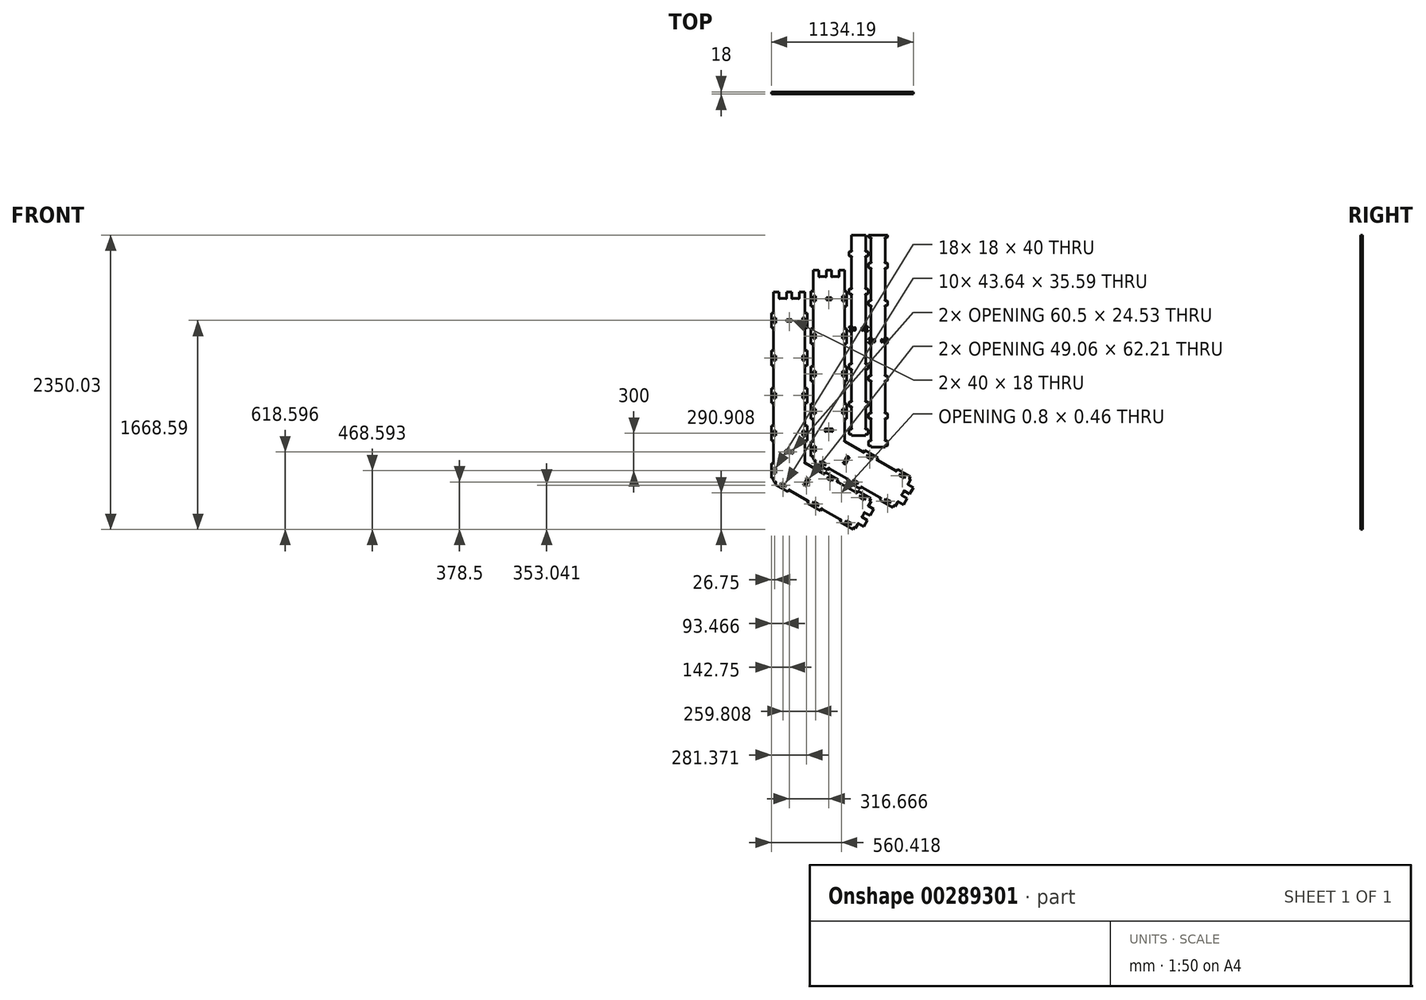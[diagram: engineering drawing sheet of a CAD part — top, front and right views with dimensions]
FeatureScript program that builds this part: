
annotation { "Feature Type Name" : "Feature", "Feature Type Description" : "" }
export const myFeature = defineFeature(function(context is Context, id is Id, definition is map)
    precondition{}
    {
        {
            var Q0;
            Q0=qCreatedBy(makeId("Front.planeOp"),FACE);
            var sketch = newSketch(context, id + "F0", { "sketchPlane" : qUnion([Q0])});
            skLineSegment(sketch, "E0", {"start": v(-135.58, 658.39) * mm, "end": v(-95.58, 658.39) * mm});
            skLineSegment(sketch, "E1", {"start": v(-95.58, 658.39) * mm, "end": v(-95.58, 676.39) * mm});
            skLineSegment(sketch, "E2", {"start": v(-95.58, 676.39) * mm, "end": v(-135.58, 676.39) * mm});
            skLineSegment(sketch, "E3", {"start": v(-135.58, 676.39) * mm, "end": v(-135.58, 658.39) * mm});
            skLineSegment(sketch, "E4", {"start": v(-600, -1200) * mm, "end": v(600, -1200) * mm});
            skLineSegment(sketch, "E5", {"start": v(600, -1200) * mm, "end": v(600, 1200) * mm});
            skLineSegment(sketch, "E6", {"start": v(600, 1200) * mm, "end": v(-600, 1200) * mm});
            skLineSegment(sketch, "E7", {"start": v(-600, 1200) * mm, "end": v(-600, -1200) * mm});
            skLineSegment(sketch, "E8", {"start": v(-480, 825) * mm, "end": v(-480, 1075) * mm});
            skLineSegment(sketch, "E9", {"start": v(-480, 1075) * mm, "end": v(-433.22, 1075) * mm});
            skLineSegment(sketch, "E10", {"start": v(-433.22, 1075) * mm, "end": v(-425, 1083.22) * mm});
            skLineSegment(sketch, "E11", {"start": v(-425, 1083.22) * mm, "end": v(-425, 1166.78) * mm});
            skLineSegment(sketch, "E12", {"start": v(-425, 1166.78) * mm, "end": v(-433.22, 1175) * mm});
            skLineSegment(sketch, "E13", {"start": v(-433.22, 1175) * mm, "end": v(-566.78, 1175) * mm});
            skLineSegment(sketch, "E14", {"start": v(-566.78, 1175) * mm, "end": v(-575, 1166.78) * mm});
            skLineSegment(sketch, "E15", {"start": v(-575, 1166.78) * mm, "end": v(-575, 1083.22) * mm});
            skLineSegment(sketch, "E16", {"start": v(-575, 1083.22) * mm, "end": v(-566.78, 1075) * mm});
            skLineSegment(sketch, "E17", {"start": v(-566.78, 1075) * mm, "end": v(-520, 1075) * mm});
            skLineSegment(sketch, "E18", {"start": v(-520, 1075) * mm, "end": v(-520, 825) * mm});
            skLineSegment(sketch, "E19", {"start": v(-520, 825) * mm, "end": v(-480, 825) * mm});
            skLineSegment(sketch, "E20", {"start": v(-405, 1175) * mm, "end": v(-405, 925) * mm});
            skLineSegment(sketch, "E21", {"start": v(-405, 925) * mm, "end": v(-451.78, 925) * mm});
            skLineSegment(sketch, "E22", {"start": v(-451.78, 925) * mm, "end": v(-460, 916.78) * mm});
            skLineSegment(sketch, "E23", {"start": v(-460, 916.78) * mm, "end": v(-460, 833.22) * mm});
            skLineSegment(sketch, "E24", {"start": v(-460, 833.22) * mm, "end": v(-451.78, 825) * mm});
            skLineSegment(sketch, "E25", {"start": v(-451.78, 825) * mm, "end": v(-318.22, 825) * mm});
            skLineSegment(sketch, "E26", {"start": v(-318.22, 825) * mm, "end": v(-310, 833.22) * mm});
            skLineSegment(sketch, "E27", {"start": v(-310, 833.22) * mm, "end": v(-310, 916.78) * mm});
            skLineSegment(sketch, "E28", {"start": v(-310, 916.78) * mm, "end": v(-318.22, 925) * mm});
            skLineSegment(sketch, "E29", {"start": v(-318.22, 925) * mm, "end": v(-365, 925) * mm});
            skLineSegment(sketch, "E30", {"start": v(-365, 925) * mm, "end": v(-365, 1175) * mm});
            skLineSegment(sketch, "E31", {"start": v(-365, 1175) * mm, "end": v(-405, 1175) * mm});
            skLineSegment(sketch, "E32", {"start": v(575, -1175) * mm, "end": v(575, -953) * mm});
            skLineSegment(sketch, "E33", {"start": v(575, -953) * mm, "end": v(540, -953) * mm});
            skLineSegment(sketch, "E34", {"start": v(540, -953) * mm, "end": v(540, -1008) * mm});
            skLineSegment(sketch, "E35", {"start": v(540, -1008) * mm, "end": v(446, -1008) * mm});
            skLineSegment(sketch, "E36", {"start": v(446, -1008) * mm, "end": v(446, -1033.28) * mm});
            skLineSegment(sketch, "E37", {"start": v(446, -1033.28) * mm, "end": v(527, -1040.95) * mm});
            skLineSegment(sketch, "E38", {"start": v(527, -1040.95) * mm, "end": v(527, -1088.05) * mm});
            skLineSegment(sketch, "E39", {"start": v(527, -1088.05) * mm, "end": v(446, -1095.72) * mm});
            skLineSegment(sketch, "E40", {"start": v(446, -1095.72) * mm, "end": v(446, -1121) * mm});
            skLineSegment(sketch, "E41", {"start": v(446, -1121) * mm, "end": v(540, -1121) * mm});
            skLineSegment(sketch, "E42", {"start": v(540, -1121) * mm, "end": v(540, -1175) * mm});
            skLineSegment(sketch, "E43", {"start": v(540, -1175) * mm, "end": v(575, -1175) * mm});
            skLineSegment(sketch, "E44", {"start": v(199, -1174.72) * mm, "end": v(421, -1174.72) * mm});
            skLineSegment(sketch, "E45", {"start": v(421, -1174.72) * mm, "end": v(421, -1139.72) * mm});
            skLineSegment(sketch, "E46", {"start": v(421, -1139.72) * mm, "end": v(366, -1139.72) * mm});
            skLineSegment(sketch, "E47", {"start": v(366, -1139.72) * mm, "end": v(366, -1045.72) * mm});
            skLineSegment(sketch, "E48", {"start": v(366, -1045.72) * mm, "end": v(340.72, -1045.72) * mm});
            skLineSegment(sketch, "E49", {"start": v(340.72, -1045.72) * mm, "end": v(333.05, -1126.72) * mm});
            skLineSegment(sketch, "E50", {"start": v(333.05, -1126.72) * mm, "end": v(285.95, -1126.72) * mm});
            skLineSegment(sketch, "E51", {"start": v(285.95, -1126.72) * mm, "end": v(278.28, -1045.72) * mm});
            skLineSegment(sketch, "E52", {"start": v(278.28, -1045.72) * mm, "end": v(253, -1045.72) * mm});
            skLineSegment(sketch, "E53", {"start": v(253, -1045.72) * mm, "end": v(253, -1139.72) * mm});
            skLineSegment(sketch, "E54", {"start": v(253, -1139.72) * mm, "end": v(199, -1139.72) * mm});
            skLineSegment(sketch, "E55", {"start": v(199, -1139.72) * mm, "end": v(199, -1174.72) * mm});
            skLineSegment(sketch, "E56", {"start": v(576.88, -543.09) * mm, "end": v(354.87, -543.09) * mm});
            skLineSegment(sketch, "E57", {"start": v(354.87, -543.09) * mm, "end": v(354.87, -578.09) * mm});
            skLineSegment(sketch, "E58", {"start": v(354.87, -578.09) * mm, "end": v(409.87, -578.09) * mm});
            skLineSegment(sketch, "E59", {"start": v(409.87, -578.09) * mm, "end": v(409.87, -672.09) * mm});
            skLineSegment(sketch, "E60", {"start": v(409.87, -672.09) * mm, "end": v(435.16, -672.09) * mm});
            skLineSegment(sketch, "E61", {"start": v(435.16, -672.09) * mm, "end": v(442.82, -591.09) * mm});
            skLineSegment(sketch, "E62", {"start": v(442.82, -591.09) * mm, "end": v(489.93, -591.09) * mm});
            skLineSegment(sketch, "E63", {"start": v(489.93, -591.09) * mm, "end": v(497.6, -672.09) * mm});
            skLineSegment(sketch, "E64", {"start": v(497.6, -672.09) * mm, "end": v(522.88, -672.09) * mm});
            skLineSegment(sketch, "E65", {"start": v(522.88, -672.09) * mm, "end": v(522.88, -578.09) * mm});
            skLineSegment(sketch, "E66", {"start": v(522.88, -578.09) * mm, "end": v(576.88, -578.09) * mm});
            skLineSegment(sketch, "E67", {"start": v(576.88, -578.09) * mm, "end": v(576.88, -543.09) * mm});
            skLineSegment(sketch, "E68", {"start": v(-289.5, -46.66) * mm, "end": v(-307.25, -46.66) * mm});
            skArc(sketch, "E69", {"start": v(-307.25, -46.66) * mm, "mid": v(-310.5, -43.52) * mm, "end": v(-307.5, -40.14) * mm});
            skLineSegment(sketch, "E70", {"start": v(-307.5, -40.14) * mm, "end": v(-307.5, 127.32) * mm});
            skArc(sketch, "E71", {"start": v(-307.5, 127.32) * mm, "mid": v(-310.52, 130.7) * mm, "end": v(-307.25, 133.84) * mm});
            skLineSegment(sketch, "E72", {"start": v(-307.25, 133.84) * mm, "end": v(-289.5, 133.84) * mm});
            skLineSegment(sketch, "E73", {"start": v(-289.5, 133.84) * mm, "end": v(-289.5, 253.34) * mm});
            skLineSegment(sketch, "E74", {"start": v(-289.5, 253.34) * mm, "end": v(-307.25, 253.34) * mm});
            skArc(sketch, "E75", {"start": v(-307.25, 253.34) * mm, "mid": v(-310.5, 256.48) * mm, "end": v(-307.5, 259.86) * mm});
            skLineSegment(sketch, "E76", {"start": v(-307.5, 259.86) * mm, "end": v(-307.5, 427.32) * mm});
            skArc(sketch, "E77", {"start": v(-307.5, 427.32) * mm, "mid": v(-310.52, 430.7) * mm, "end": v(-307.25, 433.84) * mm});
            skLineSegment(sketch, "E78", {"start": v(-307.25, 433.84) * mm, "end": v(-289.5, 433.84) * mm});
            skLineSegment(sketch, "E79", {"start": v(-289.5, 433.84) * mm, "end": v(-289.5, 553.34) * mm});
            skLineSegment(sketch, "E80", {"start": v(-289.5, 553.34) * mm, "end": v(-307.25, 553.34) * mm});
            skArc(sketch, "E81", {"start": v(-307.25, 553.34) * mm, "mid": v(-310.5, 556.48) * mm, "end": v(-307.5, 559.86) * mm});
            skLineSegment(sketch, "E82", {"start": v(-307.5, 559.86) * mm, "end": v(-307.5, 720.04) * mm});
            skLineSegment(sketch, "E83", {"start": v(-307.5, 720.04) * mm, "end": v(-352, 720.04) * mm});
            skLineSegment(sketch, "E84", {"start": v(-352, 720.04) * mm, "end": v(-352, 670.3) * mm});
            skArc(sketch, "E85", {"start": v(-352, 670.3) * mm, "mid": v(-355.14, 667.03) * mm, "end": v(-358.52, 670.04) * mm});
            skLineSegment(sketch, "E86", {"start": v(-358.52, 670.04) * mm, "end": v(-405.98, 670.04) * mm});
            skArc(sketch, "E87", {"start": v(-405.98, 670.04) * mm, "mid": v(-409.36, 667.02) * mm, "end": v(-412.5, 670.3) * mm});
            skLineSegment(sketch, "E88", {"start": v(-412.5, 670.3) * mm, "end": v(-412.5, 720.04) * mm});
            skLineSegment(sketch, "E89", {"start": v(-412.5, 720.04) * mm, "end": v(-452, 720.04) * mm});
            skLineSegment(sketch, "E90", {"start": v(-452, 720.04) * mm, "end": v(-452, 670.3) * mm});
            skArc(sketch, "E91", {"start": v(-452, 670.3) * mm, "mid": v(-455.14, 667.03) * mm, "end": v(-458.52, 670.04) * mm});
            skLineSegment(sketch, "E92", {"start": v(-458.52, 670.04) * mm, "end": v(-505.98, 670.04) * mm});
            skArc(sketch, "E93", {"start": v(-505.98, 670.04) * mm, "mid": v(-509.36, 667.02) * mm, "end": v(-512.5, 670.3) * mm});
            skLineSegment(sketch, "E94", {"start": v(-512.5, 670.3) * mm, "end": v(-512.5, 720.04) * mm});
            skLineSegment(sketch, "E95", {"start": v(-512.5, 720.04) * mm, "end": v(-557, 720.04) * mm});
            skLineSegment(sketch, "E96", {"start": v(-557, 720.04) * mm, "end": v(-557, 559.86) * mm});
            skArc(sketch, "E97", {"start": v(-557, 559.86) * mm, "mid": v(-553.98, 556.48) * mm, "end": v(-557.25, 553.34) * mm});
            skLineSegment(sketch, "E98", {"start": v(-557.25, 553.34) * mm, "end": v(-575, 553.34) * mm});
            skLineSegment(sketch, "E99", {"start": v(-575, 553.34) * mm, "end": v(-575, 433.84) * mm});
            skLineSegment(sketch, "E100", {"start": v(-575, 433.84) * mm, "end": v(-557.25, 433.84) * mm});
            skArc(sketch, "E101", {"start": v(-557.25, 433.84) * mm, "mid": v(-554, 430.7) * mm, "end": v(-557, 427.32) * mm});
            skLineSegment(sketch, "E102", {"start": v(-557, 427.32) * mm, "end": v(-557, 259.86) * mm});
            skArc(sketch, "E103", {"start": v(-557, 259.86) * mm, "mid": v(-553.98, 256.48) * mm, "end": v(-557.25, 253.34) * mm});
            skLineSegment(sketch, "E104", {"start": v(-557.25, 253.34) * mm, "end": v(-575, 253.34) * mm});
            skLineSegment(sketch, "E105", {"start": v(-575, 253.34) * mm, "end": v(-575, 133.84) * mm});
            skLineSegment(sketch, "E106", {"start": v(-575, 133.84) * mm, "end": v(-557.25, 133.84) * mm});
            skArc(sketch, "E107", {"start": v(-557.25, 133.84) * mm, "mid": v(-554, 130.7) * mm, "end": v(-557, 127.32) * mm});
            skLineSegment(sketch, "E108", {"start": v(-557, 127.32) * mm, "end": v(-557, -40.14) * mm});
            skArc(sketch, "E109", {"start": v(-557, -40.14) * mm, "mid": v(-553.98, -43.52) * mm, "end": v(-557.25, -46.66) * mm});
            skLineSegment(sketch, "E110", {"start": v(-557.25, -46.66) * mm, "end": v(-575, -46.66) * mm});
            skLineSegment(sketch, "E111", {"start": v(-575, -46.66) * mm, "end": v(-575, -166.16) * mm});
            skLineSegment(sketch, "E112", {"start": v(-575, -166.16) * mm, "end": v(-557.25, -166.16) * mm});
            skArc(sketch, "E113", {"start": v(-557.25, -166.16) * mm, "mid": v(-554, -169.3) * mm, "end": v(-557, -172.68) * mm});
            skLineSegment(sketch, "E114", {"start": v(-557, -172.68) * mm, "end": v(-557, -340.14) * mm});
            skArc(sketch, "E115", {"start": v(-557, -340.14) * mm, "mid": v(-553.98, -343.52) * mm, "end": v(-557.25, -346.66) * mm});
            skLineSegment(sketch, "E116", {"start": v(-557.25, -346.66) * mm, "end": v(-575, -346.66) * mm});
            skLineSegment(sketch, "E117", {"start": v(-575, -346.66) * mm, "end": v(-575, -466.16) * mm});
            skLineSegment(sketch, "E118", {"start": v(-575, -466.16) * mm, "end": v(-557.25, -466.16) * mm});
            skArc(sketch, "E119", {"start": v(-557.25, -466.16) * mm, "mid": v(-554, -469.3) * mm, "end": v(-557, -472.68) * mm});
            skLineSegment(sketch, "E120", {"start": v(-557, -472.68) * mm, "end": v(-557, -640.14) * mm});
            skArc(sketch, "E121", {"start": v(-557, -640.14) * mm, "mid": v(-553.98, -643.52) * mm, "end": v(-557.25, -646.66) * mm});
            skLineSegment(sketch, "E122", {"start": v(-557.25, -646.66) * mm, "end": v(-575, -646.66) * mm});
            skLineSegment(sketch, "E123", {"start": v(-575, -646.66) * mm, "end": v(-575, -766.16) * mm});
            skLineSegment(sketch, "E124", {"start": v(-575, -766.16) * mm, "end": v(-557.25, -766.16) * mm});
            skArc(sketch, "E125", {"start": v(-557.25, -766.16) * mm, "mid": v(-554, -769.3) * mm, "end": v(-557, -772.68) * mm});
            skLineSegment(sketch, "E126", {"start": v(-557, -772.68) * mm, "end": v(-557, -788.5) * mm});
            skLineSegment(sketch, "E127", {"start": v(-557, -788.5) * mm, "end": v(-543.3, -796.4) * mm});
            skArc(sketch, "E128", {"start": v(-543.3, -796.4) * mm, "mid": v(-538.86, -795.48) * mm, "end": v(-537.78, -799.88) * mm});
            skLineSegment(sketch, "E129", {"start": v(-537.78, -799.88) * mm, "end": v(-546.65, -815.25) * mm});
            skLineSegment(sketch, "E130", {"start": v(-546.65, -815.25) * mm, "end": v(-443.16, -875) * mm});
            skLineSegment(sketch, "E131", {"start": v(-443.16, -875) * mm, "end": v(-434.29, -859.63) * mm});
            skArc(sketch, "E132", {"start": v(-434.29, -859.63) * mm, "mid": v(-429.94, -858.38) * mm, "end": v(-428.52, -862.67) * mm});
            skLineSegment(sketch, "E133", {"start": v(-428.52, -862.67) * mm, "end": v(-283.5, -946.4) * mm});
            skArc(sketch, "E134", {"start": v(-283.5, -946.4) * mm, "mid": v(-279.06, -945.48) * mm, "end": v(-277.97, -949.88) * mm});
            skLineSegment(sketch, "E135", {"start": v(-277.97, -949.88) * mm, "end": v(-286.85, -965.25) * mm});
            skLineSegment(sketch, "E136", {"start": v(-286.85, -965.25) * mm, "end": v(-183.36, -1025) * mm});
            skLineSegment(sketch, "E137", {"start": v(-183.36, -1025) * mm, "end": v(-174.48, -1009.63) * mm});
            skArc(sketch, "E138", {"start": v(-174.48, -1009.63) * mm, "mid": v(-170.13, -1008.38) * mm, "end": v(-168.7, -1012.67) * mm});
            skLineSegment(sketch, "E139", {"start": v(-168.7, -1012.67) * mm, "end": v(-23.69, -1096.4) * mm});
            skArc(sketch, "E140", {"start": v(-23.69, -1096.4) * mm, "mid": v(-19.25, -1095.48) * mm, "end": v(-18.16, -1099.88) * mm});
            skLineSegment(sketch, "E141", {"start": v(-18.16, -1099.88) * mm, "end": v(-27.04, -1115.25) * mm});
            skLineSegment(sketch, "E142", {"start": v(-27.04, -1115.25) * mm, "end": v(76.45, -1175) * mm});
            skLineSegment(sketch, "E143", {"start": v(76.45, -1175) * mm, "end": v(85.33, -1159.63) * mm});
            skArc(sketch, "E144", {"start": v(85.33, -1159.63) * mm, "mid": v(89.67, -1158.38) * mm, "end": v(91.1, -1162.67) * mm});
            skLineSegment(sketch, "E145", {"start": v(91.1, -1162.67) * mm, "end": v(96.97, -1166.06) * mm});
            skLineSegment(sketch, "E146", {"start": v(96.97, -1166.06) * mm, "end": v(116.21, -1132.74) * mm});
            skArc(sketch, "E147", {"start": v(116.21, -1132.74) * mm, "mid": v(115.3, -1128.3) * mm, "end": v(119.7, -1127.22) * mm});
            skLineSegment(sketch, "E148", {"start": v(119.7, -1127.22) * mm, "end": v(162.78, -1152.1) * mm});
            skLineSegment(sketch, "E149", {"start": v(162.78, -1152.1) * mm, "end": v(192.53, -1100.56) * mm});
            skLineSegment(sketch, "E150", {"start": v(192.53, -1100.56) * mm, "end": v(149.44, -1075.69) * mm});
            skArc(sketch, "E151", {"start": v(149.44, -1075.69) * mm, "mid": v(148.2, -1071.34) * mm, "end": v(152.49, -1069.92) * mm});
            skLineSegment(sketch, "E152", {"start": v(152.49, -1069.92) * mm, "end": v(166.21, -1046.14) * mm});
            skArc(sketch, "E153", {"start": v(166.21, -1046.14) * mm, "mid": v(165.3, -1041.7) * mm, "end": v(169.7, -1040.62) * mm});
            skLineSegment(sketch, "E154", {"start": v(169.7, -1040.62) * mm, "end": v(212.78, -1065.5) * mm});
            skLineSegment(sketch, "E155", {"start": v(212.78, -1065.5) * mm, "end": v(242.53, -1013.96) * mm});
            skLineSegment(sketch, "E156", {"start": v(242.53, -1013.96) * mm, "end": v(199.44, -989.09) * mm});
            skArc(sketch, "E157", {"start": v(199.44, -989.09) * mm, "mid": v(198.19, -984.74) * mm, "end": v(202.48, -983.32) * mm});
            skLineSegment(sketch, "E158", {"start": v(202.48, -983.32) * mm, "end": v(221.73, -949.99) * mm});
            skLineSegment(sketch, "E159", {"start": v(221.73, -949.99) * mm, "end": v(215.85, -946.6) * mm});
            skArc(sketch, "E160", {"start": v(215.85, -946.6) * mm, "mid": v(211.41, -947.52) * mm, "end": v(210.33, -943.12) * mm});
            skLineSegment(sketch, "E161", {"start": v(210.33, -943.12) * mm, "end": v(219.2, -927.75) * mm});
            skLineSegment(sketch, "E162", {"start": v(219.2, -927.75) * mm, "end": v(115.71, -868) * mm});
            skLineSegment(sketch, "E163", {"start": v(115.71, -868) * mm, "end": v(106.84, -883.37) * mm});
            skArc(sketch, "E164", {"start": v(106.84, -883.37) * mm, "mid": v(102.49, -884.62) * mm, "end": v(101.06, -880.33) * mm});
            skLineSegment(sketch, "E165", {"start": v(101.06, -880.33) * mm, "end": v(-43.96, -796.6) * mm});
            skArc(sketch, "E166", {"start": v(-43.96, -796.6) * mm, "mid": v(-48.4, -797.52) * mm, "end": v(-49.48, -793.12) * mm});
            skLineSegment(sketch, "E167", {"start": v(-49.48, -793.12) * mm, "end": v(-40.6, -777.75) * mm});
            skLineSegment(sketch, "E168", {"start": v(-40.6, -777.75) * mm, "end": v(-144.1, -718) * mm});
            skLineSegment(sketch, "E169", {"start": v(-144.1, -718) * mm, "end": v(-152.97, -733.37) * mm});
            skArc(sketch, "E170", {"start": v(-152.97, -733.37) * mm, "mid": v(-157.32, -734.62) * mm, "end": v(-158.74, -730.33) * mm});
            skLineSegment(sketch, "E171", {"start": v(-158.74, -730.33) * mm, "end": v(-304.24, -646.33) * mm});
            skArc(sketch, "E172", {"start": v(-304.24, -646.33) * mm, "mid": v(-308.57, -645.06) * mm, "end": v(-307.5, -640.68) * mm});
            skLineSegment(sketch, "E173", {"start": v(-307.5, -640.68) * mm, "end": v(-307.5, -472.68) * mm});
            skArc(sketch, "E174", {"start": v(-307.5, -472.68) * mm, "mid": v(-310.52, -469.3) * mm, "end": v(-307.25, -466.16) * mm});
            skLineSegment(sketch, "E175", {"start": v(-307.25, -466.16) * mm, "end": v(-289.5, -466.16) * mm});
            skLineSegment(sketch, "E176", {"start": v(-289.5, -466.16) * mm, "end": v(-289.5, -346.66) * mm});
            skLineSegment(sketch, "E177", {"start": v(-289.5, -346.66) * mm, "end": v(-307.25, -346.66) * mm});
            skArc(sketch, "E178", {"start": v(-307.25, -346.66) * mm, "mid": v(-310.5, -343.52) * mm, "end": v(-307.5, -340.14) * mm});
            skLineSegment(sketch, "E179", {"start": v(-307.5, -340.14) * mm, "end": v(-307.5, -172.68) * mm});
            skArc(sketch, "E180", {"start": v(-307.5, -172.68) * mm, "mid": v(-310.52, -169.3) * mm, "end": v(-307.25, -166.16) * mm});
            skLineSegment(sketch, "E181", {"start": v(-307.25, -166.16) * mm, "end": v(-289.5, -166.16) * mm});
            skLineSegment(sketch, "E182", {"start": v(-289.5, -166.16) * mm, "end": v(-289.5, -46.66) * mm});
            skLineSegment(sketch, "E183", {"start": v(9.17, 133.66) * mm, "end": v(9.17, 301.12) * mm});
            skArc(sketch, "E184", {"start": v(9.17, 301.12) * mm, "mid": v(6.15, 304.5) * mm, "end": v(9.42, 307.64) * mm});
            skLineSegment(sketch, "E185", {"start": v(9.42, 307.64) * mm, "end": v(27.17, 307.64) * mm});
            skLineSegment(sketch, "E186", {"start": v(27.17, 307.64) * mm, "end": v(27.17, 427.14) * mm});
            skLineSegment(sketch, "E187", {"start": v(27.17, 427.14) * mm, "end": v(9.42, 427.14) * mm});
            skArc(sketch, "E188", {"start": v(9.42, 427.14) * mm, "mid": v(6.16, 430.28) * mm, "end": v(9.17, 433.66) * mm});
            skLineSegment(sketch, "E189", {"start": v(9.17, 433.66) * mm, "end": v(9.17, 601.12) * mm});
            skArc(sketch, "E190", {"start": v(9.17, 601.12) * mm, "mid": v(6.15, 604.5) * mm, "end": v(9.42, 607.64) * mm});
            skLineSegment(sketch, "E191", {"start": v(9.42, 607.64) * mm, "end": v(27.17, 607.64) * mm});
            skLineSegment(sketch, "E192", {"start": v(27.17, 607.64) * mm, "end": v(27.17, 727.14) * mm});
            skLineSegment(sketch, "E193", {"start": v(27.17, 727.14) * mm, "end": v(9.42, 727.14) * mm});
            skArc(sketch, "E194", {"start": v(9.42, 727.14) * mm, "mid": v(6.16, 730.28) * mm, "end": v(9.17, 733.66) * mm});
            skLineSegment(sketch, "E195", {"start": v(9.17, 733.66) * mm, "end": v(9.17, 893.84) * mm});
            skLineSegment(sketch, "E196", {"start": v(9.17, 893.84) * mm, "end": v(-35.33, 893.84) * mm});
            skLineSegment(sketch, "E197", {"start": v(-35.33, 893.84) * mm, "end": v(-35.33, 844.09) * mm});
            skArc(sketch, "E198", {"start": v(-35.33, 844.09) * mm, "mid": v(-38.47, 840.83) * mm, "end": v(-41.85, 843.84) * mm});
            skLineSegment(sketch, "E199", {"start": v(-41.85, 843.84) * mm, "end": v(-89.31, 843.84) * mm});
            skArc(sketch, "E200", {"start": v(-89.31, 843.84) * mm, "mid": v(-92.7, 840.82) * mm, "end": v(-95.83, 844.09) * mm});
            skLineSegment(sketch, "E201", {"start": v(-95.83, 844.09) * mm, "end": v(-95.83, 893.84) * mm});
            skLineSegment(sketch, "E202", {"start": v(-95.83, 893.84) * mm, "end": v(-135.33, 893.84) * mm});
            skLineSegment(sketch, "E203", {"start": v(-135.33, 893.84) * mm, "end": v(-135.33, 844.09) * mm});
            skArc(sketch, "E204", {"start": v(-135.33, 844.09) * mm, "mid": v(-138.47, 840.83) * mm, "end": v(-141.85, 843.84) * mm});
            skLineSegment(sketch, "E205", {"start": v(-141.85, 843.84) * mm, "end": v(-189.31, 843.84) * mm});
            skArc(sketch, "E206", {"start": v(-189.31, 843.84) * mm, "mid": v(-192.7, 840.82) * mm, "end": v(-195.83, 844.09) * mm});
            skLineSegment(sketch, "E207", {"start": v(-195.83, 844.09) * mm, "end": v(-195.83, 893.84) * mm});
            skLineSegment(sketch, "E208", {"start": v(-195.83, 893.84) * mm, "end": v(-240.33, 893.84) * mm});
            skLineSegment(sketch, "E209", {"start": v(-240.33, 893.84) * mm, "end": v(-240.33, 733.66) * mm});
            skArc(sketch, "E210", {"start": v(-240.33, 733.66) * mm, "mid": v(-237.32, 730.28) * mm, "end": v(-240.58, 727.14) * mm});
            skLineSegment(sketch, "E211", {"start": v(-240.58, 727.14) * mm, "end": v(-258.33, 727.14) * mm});
            skLineSegment(sketch, "E212", {"start": v(-258.33, 727.14) * mm, "end": v(-258.33, 607.64) * mm});
            skLineSegment(sketch, "E213", {"start": v(-258.33, 607.64) * mm, "end": v(-240.58, 607.64) * mm});
            skArc(sketch, "E214", {"start": v(-240.58, 607.64) * mm, "mid": v(-237.33, 604.5) * mm, "end": v(-240.33, 601.12) * mm});
            skLineSegment(sketch, "E215", {"start": v(-240.33, 601.12) * mm, "end": v(-240.33, 433.66) * mm});
            skArc(sketch, "E216", {"start": v(-240.33, 433.66) * mm, "mid": v(-237.32, 430.28) * mm, "end": v(-240.58, 427.14) * mm});
            skLineSegment(sketch, "E217", {"start": v(-240.58, 427.14) * mm, "end": v(-258.33, 427.14) * mm});
            skLineSegment(sketch, "E218", {"start": v(-258.33, 427.14) * mm, "end": v(-258.33, 307.64) * mm});
            skLineSegment(sketch, "E219", {"start": v(-258.33, 307.64) * mm, "end": v(-240.58, 307.64) * mm});
            skArc(sketch, "E220", {"start": v(-240.58, 307.64) * mm, "mid": v(-237.33, 304.5) * mm, "end": v(-240.33, 301.12) * mm});
            skLineSegment(sketch, "E221", {"start": v(-240.33, 301.12) * mm, "end": v(-240.33, 133.66) * mm});
            skArc(sketch, "E222", {"start": v(-240.33, 133.66) * mm, "mid": v(-237.32, 130.28) * mm, "end": v(-240.58, 127.14) * mm});
            skLineSegment(sketch, "E223", {"start": v(-240.58, 127.14) * mm, "end": v(-258.33, 127.14) * mm});
            skLineSegment(sketch, "E224", {"start": v(-258.33, 127.14) * mm, "end": v(-258.33, 7.64) * mm});
            skLineSegment(sketch, "E225", {"start": v(-258.33, 7.64) * mm, "end": v(-240.58, 7.64) * mm});
            skArc(sketch, "E226", {"start": v(-240.58, 7.64) * mm, "mid": v(-237.33, 4.5) * mm, "end": v(-240.33, 1.12) * mm});
            skLineSegment(sketch, "E227", {"start": v(-240.33, 1.12) * mm, "end": v(-240.33, -166.34) * mm});
            skArc(sketch, "E228", {"start": v(-240.33, -166.34) * mm, "mid": v(-237.32, -169.72) * mm, "end": v(-240.58, -172.86) * mm});
            skLineSegment(sketch, "E229", {"start": v(-240.58, -172.86) * mm, "end": v(-258.33, -172.86) * mm});
            skLineSegment(sketch, "E230", {"start": v(-258.33, -172.86) * mm, "end": v(-258.33, -292.36) * mm});
            skLineSegment(sketch, "E231", {"start": v(-258.33, -292.36) * mm, "end": v(-240.58, -292.36) * mm});
            skArc(sketch, "E232", {"start": v(-240.58, -292.36) * mm, "mid": v(-237.33, -295.5) * mm, "end": v(-240.33, -298.88) * mm});
            skLineSegment(sketch, "E233", {"start": v(-240.33, -298.88) * mm, "end": v(-240.33, -466.34) * mm});
            skArc(sketch, "E234", {"start": v(-240.33, -466.34) * mm, "mid": v(-237.32, -469.72) * mm, "end": v(-240.58, -472.86) * mm});
            skLineSegment(sketch, "E235", {"start": v(-240.58, -472.86) * mm, "end": v(-258.33, -472.86) * mm});
            skLineSegment(sketch, "E236", {"start": v(-258.33, -472.86) * mm, "end": v(-258.33, -592.36) * mm});
            skLineSegment(sketch, "E237", {"start": v(-258.33, -592.36) * mm, "end": v(-240.58, -592.36) * mm});
            skArc(sketch, "E238", {"start": v(-240.58, -592.36) * mm, "mid": v(-237.33, -595.5) * mm, "end": v(-240.33, -598.88) * mm});
            skLineSegment(sketch, "E239", {"start": v(-240.33, -598.88) * mm, "end": v(-240.33, -614.7) * mm});
            skLineSegment(sketch, "E240", {"start": v(-240.33, -614.7) * mm, "end": v(-226.63, -622.6) * mm});
            skArc(sketch, "E241", {"start": v(-226.63, -622.6) * mm, "mid": v(-222.2, -621.68) * mm, "end": v(-221.11, -626.08) * mm});
            skLineSegment(sketch, "E242", {"start": v(-221.11, -626.08) * mm, "end": v(-229.99, -641.46) * mm});
            skLineSegment(sketch, "E243", {"start": v(-229.99, -641.46) * mm, "end": v(-126.5, -701.2) * mm});
            skLineSegment(sketch, "E244", {"start": v(-126.5, -701.2) * mm, "end": v(-117.62, -685.83) * mm});
            skArc(sketch, "E245", {"start": v(-117.62, -685.83) * mm, "mid": v(-113.27, -684.58) * mm, "end": v(-111.85, -688.88) * mm});
            skLineSegment(sketch, "E246", {"start": v(-111.85, -688.88) * mm, "end": v(33.17, -772.6) * mm});
            skArc(sketch, "E247", {"start": v(33.17, -772.6) * mm, "mid": v(37.6, -771.68) * mm, "end": v(38.7, -776.08) * mm});
            skLineSegment(sketch, "E248", {"start": v(38.7, -776.08) * mm, "end": v(29.82, -791.46) * mm});
            skLineSegment(sketch, "E249", {"start": v(29.82, -791.46) * mm, "end": v(133.3, -851.2) * mm});
            skLineSegment(sketch, "E250", {"start": v(133.3, -851.2) * mm, "end": v(142.18, -835.83) * mm});
            skArc(sketch, "E251", {"start": v(142.18, -835.83) * mm, "mid": v(146.53, -834.58) * mm, "end": v(147.96, -838.88) * mm});
            skLineSegment(sketch, "E252", {"start": v(147.96, -838.88) * mm, "end": v(292.98, -922.6) * mm});
            skArc(sketch, "E253", {"start": v(292.98, -922.6) * mm, "mid": v(297.42, -921.68) * mm, "end": v(298.5, -926.08) * mm});
            skLineSegment(sketch, "E254", {"start": v(298.5, -926.08) * mm, "end": v(289.63, -941.46) * mm});
            skLineSegment(sketch, "E255", {"start": v(289.63, -941.46) * mm, "end": v(393.12, -1001.2) * mm});
            skLineSegment(sketch, "E256", {"start": v(393.12, -1001.2) * mm, "end": v(402, -985.83) * mm});
            skArc(sketch, "E257", {"start": v(402, -985.83) * mm, "mid": v(406.34, -984.58) * mm, "end": v(407.76, -988.88) * mm});
            skLineSegment(sketch, "E258", {"start": v(407.76, -988.88) * mm, "end": v(413.64, -992.27) * mm});
            skLineSegment(sketch, "E259", {"start": v(413.64, -992.27) * mm, "end": v(432.88, -958.95) * mm});
            skArc(sketch, "E260", {"start": v(432.88, -958.95) * mm, "mid": v(431.96, -954.5) * mm, "end": v(436.36, -953.42) * mm});
            skLineSegment(sketch, "E261", {"start": v(436.36, -953.42) * mm, "end": v(479.44, -978.3) * mm});
            skLineSegment(sketch, "E262", {"start": v(479.44, -978.3) * mm, "end": v(509.2, -926.77) * mm});
            skLineSegment(sketch, "E263", {"start": v(509.2, -926.77) * mm, "end": v(466.1, -901.9) * mm});
            skArc(sketch, "E264", {"start": v(466.1, -901.9) * mm, "mid": v(464.86, -897.55) * mm, "end": v(469.15, -896.12) * mm});
            skLineSegment(sketch, "E265", {"start": v(469.15, -896.12) * mm, "end": v(482.88, -872.34) * mm});
            skArc(sketch, "E266", {"start": v(482.88, -872.34) * mm, "mid": v(481.96, -867.9) * mm, "end": v(486.36, -866.82) * mm});
            skLineSegment(sketch, "E267", {"start": v(486.36, -866.82) * mm, "end": v(529.44, -891.7) * mm});
            skLineSegment(sketch, "E268", {"start": v(529.44, -891.7) * mm, "end": v(559.2, -840.17) * mm});
            skLineSegment(sketch, "E269", {"start": v(559.2, -840.17) * mm, "end": v(516.1, -815.3) * mm});
            skArc(sketch, "E270", {"start": v(516.1, -815.3) * mm, "mid": v(514.86, -810.94) * mm, "end": v(519.15, -809.52) * mm});
            skLineSegment(sketch, "E271", {"start": v(519.15, -809.52) * mm, "end": v(538.4, -776.2) * mm});
            skLineSegment(sketch, "E272", {"start": v(538.4, -776.2) * mm, "end": v(532.51, -772.8) * mm});
            skArc(sketch, "E273", {"start": v(532.51, -772.8) * mm, "mid": v(528.08, -773.73) * mm, "end": v(527, -769.33) * mm});
            skLineSegment(sketch, "E274", {"start": v(527, -769.33) * mm, "end": v(535.87, -753.96) * mm});
            skLineSegment(sketch, "E275", {"start": v(535.87, -753.96) * mm, "end": v(432.38, -694.2) * mm});
            skLineSegment(sketch, "E276", {"start": v(432.38, -694.2) * mm, "end": v(423.5, -709.58) * mm});
            skArc(sketch, "E277", {"start": v(423.5, -709.58) * mm, "mid": v(419.15, -710.83) * mm, "end": v(417.73, -706.53) * mm});
            skLineSegment(sketch, "E278", {"start": v(417.73, -706.53) * mm, "end": v(272.7, -622.8) * mm});
            skArc(sketch, "E279", {"start": v(272.7, -622.8) * mm, "mid": v(268.27, -623.73) * mm, "end": v(267.19, -619.33) * mm});
            skLineSegment(sketch, "E280", {"start": v(267.19, -619.33) * mm, "end": v(276.06, -603.96) * mm});
            skLineSegment(sketch, "E281", {"start": v(276.06, -603.96) * mm, "end": v(172.57, -544.2) * mm});
            skLineSegment(sketch, "E282", {"start": v(172.57, -544.2) * mm, "end": v(163.7, -559.58) * mm});
            skArc(sketch, "E283", {"start": v(163.7, -559.58) * mm, "mid": v(159.35, -560.83) * mm, "end": v(157.92, -556.53) * mm});
            skLineSegment(sketch, "E284", {"start": v(157.92, -556.53) * mm, "end": v(12.43, -472.53) * mm});
            skArc(sketch, "E285", {"start": v(12.43, -472.53) * mm, "mid": v(8.1, -471.27) * mm, "end": v(9.17, -466.88) * mm});
            skLineSegment(sketch, "E286", {"start": v(9.17, -466.88) * mm, "end": v(9.17, -298.88) * mm});
            skArc(sketch, "E287", {"start": v(9.17, -298.88) * mm, "mid": v(6.15, -295.5) * mm, "end": v(9.42, -292.36) * mm});
            skLineSegment(sketch, "E288", {"start": v(9.42, -292.36) * mm, "end": v(27.17, -292.36) * mm});
            skLineSegment(sketch, "E289", {"start": v(27.17, -292.36) * mm, "end": v(27.17, -172.86) * mm});
            skLineSegment(sketch, "E290", {"start": v(27.17, -172.86) * mm, "end": v(9.42, -172.86) * mm});
            skArc(sketch, "E291", {"start": v(9.42, -172.86) * mm, "mid": v(6.16, -169.72) * mm, "end": v(9.17, -166.34) * mm});
            skLineSegment(sketch, "E292", {"start": v(9.17, -166.34) * mm, "end": v(9.17, 1.12) * mm});
            skArc(sketch, "E293", {"start": v(9.17, 1.12) * mm, "mid": v(6.15, 4.5) * mm, "end": v(9.42, 7.64) * mm});
            skLineSegment(sketch, "E294", {"start": v(9.42, 7.64) * mm, "end": v(27.17, 7.64) * mm});
            skLineSegment(sketch, "E295", {"start": v(27.17, 7.64) * mm, "end": v(27.17, 127.14) * mm});
            skLineSegment(sketch, "E296", {"start": v(27.17, 127.14) * mm, "end": v(9.42, 127.14) * mm});
            skArc(sketch, "E297", {"start": v(9.42, 127.14) * mm, "mid": v(6.16, 130.28) * mm, "end": v(9.17, 133.66) * mm});
            skLineSegment(sketch, "E298", {"start": v(372, 1175) * mm, "end": v(372, 1158) * mm});
            skLineSegment(sketch, "E299", {"start": v(372, 1158) * mm, "end": v(375, 1155) * mm});
            skLineSegment(sketch, "E300", {"start": v(375, 1155) * mm, "end": v(390, 1155) * mm});
            skArc(sketch, "E301", {"start": v(390, 1155) * mm, "mid": v(393, 1151.99) * mm, "end": v(390, 1148.98) * mm});
            skLineSegment(sketch, "E302", {"start": v(390, 1148.98) * mm, "end": v(390, 957.7) * mm});
            skArc(sketch, "E303", {"start": v(390, 957.7) * mm, "mid": v(393, 954.69) * mm, "end": v(390, 951.68) * mm});
            skLineSegment(sketch, "E304", {"start": v(390, 951.68) * mm, "end": v(375, 951.68) * mm});
            skLineSegment(sketch, "E305", {"start": v(375, 951.68) * mm, "end": v(372, 948.68) * mm});
            skLineSegment(sketch, "E306", {"start": v(372, 948.68) * mm, "end": v(372, 914.68) * mm});
            skLineSegment(sketch, "E307", {"start": v(372, 914.68) * mm, "end": v(375, 911.68) * mm});
            skLineSegment(sketch, "E308", {"start": v(375, 911.68) * mm, "end": v(390, 911.68) * mm});
            skArc(sketch, "E309", {"start": v(390, 911.68) * mm, "mid": v(393, 908.67) * mm, "end": v(390, 905.66) * mm});
            skLineSegment(sketch, "E310", {"start": v(390, 905.66) * mm, "end": v(390, 657.7) * mm});
            skArc(sketch, "E311", {"start": v(390, 657.7) * mm, "mid": v(393.01, 654.69) * mm, "end": v(390, 651.68) * mm});
            skLineSegment(sketch, "E312", {"start": v(390, 651.68) * mm, "end": v(375, 651.68) * mm});
            skLineSegment(sketch, "E313", {"start": v(375, 651.68) * mm, "end": v(372, 648.68) * mm});
            skLineSegment(sketch, "E314", {"start": v(372, 648.68) * mm, "end": v(372, 614.68) * mm});
            skLineSegment(sketch, "E315", {"start": v(372, 614.68) * mm, "end": v(375, 611.68) * mm});
            skLineSegment(sketch, "E316", {"start": v(375, 611.68) * mm, "end": v(390, 611.68) * mm});
            skArc(sketch, "E317", {"start": v(390, 611.68) * mm, "mid": v(393.01, 608.67) * mm, "end": v(390, 605.66) * mm});
            skLineSegment(sketch, "E318", {"start": v(390, 605.66) * mm, "end": v(390, 357.7) * mm});
            skArc(sketch, "E319", {"start": v(390, 357.7) * mm, "mid": v(393.02, 354.69) * mm, "end": v(390, 351.68) * mm});
            skLineSegment(sketch, "E320", {"start": v(390, 351.68) * mm, "end": v(375, 351.68) * mm});
            skLineSegment(sketch, "E321", {"start": v(375, 351.68) * mm, "end": v(372, 348.68) * mm});
            skLineSegment(sketch, "E322", {"start": v(372, 348.68) * mm, "end": v(372, 340.68) * mm});
            skLineSegment(sketch, "E323", {"start": v(372, 340.68) * mm, "end": v(414.99, 340.68) * mm});
            skArc(sketch, "E324", {"start": v(414.99, 340.68) * mm, "mid": v(418, 343.69) * mm, "end": v(421, 340.68) * mm});
            skLineSegment(sketch, "E325", {"start": v(421, 340.68) * mm, "end": v(421, 322.68) * mm});
            skArc(sketch, "E326", {"start": v(421, 322.68) * mm, "mid": v(418, 319.67) * mm, "end": v(414.99, 322.68) * mm});
            skLineSegment(sketch, "E327", {"start": v(414.99, 322.68) * mm, "end": v(372, 322.68) * mm});
            skLineSegment(sketch, "E328", {"start": v(372, 322.68) * mm, "end": v(372, 314.68) * mm});
            skLineSegment(sketch, "E329", {"start": v(372, 314.68) * mm, "end": v(375, 311.68) * mm});
            skLineSegment(sketch, "E330", {"start": v(375, 311.68) * mm, "end": v(390, 311.68) * mm});
            skArc(sketch, "E331", {"start": v(390, 311.68) * mm, "mid": v(393.02, 308.67) * mm, "end": v(390, 305.66) * mm});
            skLineSegment(sketch, "E332", {"start": v(390, 305.66) * mm, "end": v(390.01, 57.7) * mm});
            skArc(sketch, "E333", {"start": v(390.01, 57.7) * mm, "mid": v(393.02, 54.69) * mm, "end": v(390.01, 51.68) * mm});
            skLineSegment(sketch, "E334", {"start": v(390.01, 51.68) * mm, "end": v(375.01, 51.68) * mm});
            skLineSegment(sketch, "E335", {"start": v(375.01, 51.68) * mm, "end": v(372.01, 48.68) * mm});
            skLineSegment(sketch, "E336", {"start": v(372.01, 48.68) * mm, "end": v(372.01, 14.68) * mm});
            skLineSegment(sketch, "E337", {"start": v(372.01, 14.68) * mm, "end": v(375.01, 11.68) * mm});
            skLineSegment(sketch, "E338", {"start": v(375.01, 11.68) * mm, "end": v(390.01, 11.68) * mm});
            skArc(sketch, "E339", {"start": v(390.01, 11.68) * mm, "mid": v(393.02, 8.67) * mm, "end": v(390.01, 5.66) * mm});
            skLineSegment(sketch, "E340", {"start": v(390.01, 5.66) * mm, "end": v(390.02, -242.3) * mm});
            skArc(sketch, "E341", {"start": v(390.02, -242.3) * mm, "mid": v(393.03, -245.31) * mm, "end": v(390.02, -248.32) * mm});
            skLineSegment(sketch, "E342", {"start": v(390.02, -248.32) * mm, "end": v(375.02, -248.32) * mm});
            skLineSegment(sketch, "E343", {"start": v(375.02, -248.32) * mm, "end": v(372.02, -251.32) * mm});
            skLineSegment(sketch, "E344", {"start": v(372.02, -251.32) * mm, "end": v(372.02, -285.32) * mm});
            skLineSegment(sketch, "E345", {"start": v(372.02, -285.32) * mm, "end": v(375.02, -288.32) * mm});
            skLineSegment(sketch, "E346", {"start": v(375.02, -288.32) * mm, "end": v(390.02, -288.32) * mm});
            skArc(sketch, "E347", {"start": v(390.02, -288.32) * mm, "mid": v(393.03, -291.33) * mm, "end": v(390.02, -294.34) * mm});
            skLineSegment(sketch, "E348", {"start": v(390.02, -294.34) * mm, "end": v(390.02, -462.3) * mm});
            skArc(sketch, "E349", {"start": v(390.02, -462.3) * mm, "mid": v(393.03, -465.31) * mm, "end": v(390.02, -468.32) * mm});
            skLineSegment(sketch, "E350", {"start": v(390.02, -468.32) * mm, "end": v(375.02, -468.32) * mm});
            skLineSegment(sketch, "E351", {"start": v(375.02, -468.32) * mm, "end": v(372.02, -471.32) * mm});
            skLineSegment(sketch, "E352", {"start": v(372.02, -471.32) * mm, "end": v(372.02, -505.32) * mm});
            skLineSegment(sketch, "E353", {"start": v(372.02, -505.32) * mm, "end": v(375.02, -508.32) * mm});
            skLineSegment(sketch, "E354", {"start": v(375.02, -508.32) * mm, "end": v(390.02, -508.32) * mm});
            skArc(sketch, "E355", {"start": v(390.02, -508.32) * mm, "mid": v(393.03, -511.33) * mm, "end": v(390.02, -514.34) * mm});
            skLineSegment(sketch, "E356", {"start": v(390.02, -514.34) * mm, "end": v(390.02, -518.09) * mm});
            skLineSegment(sketch, "E357", {"start": v(390.02, -518.09) * mm, "end": v(504.02, -518.09) * mm});
            skLineSegment(sketch, "E358", {"start": v(504.02, -518.09) * mm, "end": v(504.02, -514.34) * mm});
            skArc(sketch, "E359", {"start": v(504.02, -514.34) * mm, "mid": v(501.01, -511.33) * mm, "end": v(504.02, -508.32) * mm});
            skLineSegment(sketch, "E360", {"start": v(504.02, -508.32) * mm, "end": v(519.02, -508.32) * mm});
            skLineSegment(sketch, "E361", {"start": v(519.02, -508.32) * mm, "end": v(522.02, -505.32) * mm});
            skLineSegment(sketch, "E362", {"start": v(522.02, -505.32) * mm, "end": v(522.02, -471.32) * mm});
            skLineSegment(sketch, "E363", {"start": v(522.02, -471.32) * mm, "end": v(519.02, -468.32) * mm});
            skLineSegment(sketch, "E364", {"start": v(519.02, -468.32) * mm, "end": v(504.02, -468.32) * mm});
            skArc(sketch, "E365", {"start": v(504.02, -468.32) * mm, "mid": v(501.01, -465.31) * mm, "end": v(504.02, -462.3) * mm});
            skLineSegment(sketch, "E366", {"start": v(504.02, -462.3) * mm, "end": v(504.02, -294.34) * mm});
            skArc(sketch, "E367", {"start": v(504.02, -294.34) * mm, "mid": v(501, -291.33) * mm, "end": v(504.02, -288.32) * mm});
            skLineSegment(sketch, "E368", {"start": v(504.02, -288.32) * mm, "end": v(519.02, -288.32) * mm});
            skLineSegment(sketch, "E369", {"start": v(519.02, -288.32) * mm, "end": v(522.02, -285.32) * mm});
            skLineSegment(sketch, "E370", {"start": v(522.02, -285.32) * mm, "end": v(522.02, -251.32) * mm});
            skLineSegment(sketch, "E371", {"start": v(522.02, -251.32) * mm, "end": v(519.02, -248.32) * mm});
            skLineSegment(sketch, "E372", {"start": v(519.02, -248.32) * mm, "end": v(504.02, -248.32) * mm});
            skArc(sketch, "E373", {"start": v(504.02, -248.32) * mm, "mid": v(501, -245.31) * mm, "end": v(504.02, -242.3) * mm});
            skLineSegment(sketch, "E374", {"start": v(504.02, -242.3) * mm, "end": v(504.01, 5.66) * mm});
            skArc(sketch, "E375", {"start": v(504.01, 5.66) * mm, "mid": v(501, 8.67) * mm, "end": v(504.01, 11.68) * mm});
            skLineSegment(sketch, "E376", {"start": v(504.01, 11.68) * mm, "end": v(519.01, 11.68) * mm});
            skLineSegment(sketch, "E377", {"start": v(519.01, 11.68) * mm, "end": v(522.01, 14.68) * mm});
            skLineSegment(sketch, "E378", {"start": v(522.01, 14.68) * mm, "end": v(522.01, 48.68) * mm});
            skLineSegment(sketch, "E379", {"start": v(522.01, 48.68) * mm, "end": v(519.01, 51.68) * mm});
            skLineSegment(sketch, "E380", {"start": v(519.01, 51.68) * mm, "end": v(504.01, 51.68) * mm});
            skArc(sketch, "E381", {"start": v(504.01, 51.68) * mm, "mid": v(501, 54.69) * mm, "end": v(504.01, 57.7) * mm});
            skLineSegment(sketch, "E382", {"start": v(504.01, 57.7) * mm, "end": v(504, 305.66) * mm});
            skArc(sketch, "E383", {"start": v(504, 305.66) * mm, "mid": v(501, 308.67) * mm, "end": v(504, 311.68) * mm});
            skLineSegment(sketch, "E384", {"start": v(504, 311.68) * mm, "end": v(519, 311.68) * mm});
            skLineSegment(sketch, "E385", {"start": v(519, 311.68) * mm, "end": v(522, 314.68) * mm});
            skLineSegment(sketch, "E386", {"start": v(522, 314.68) * mm, "end": v(522, 322.68) * mm});
            skLineSegment(sketch, "E387", {"start": v(522, 322.68) * mm, "end": v(479.02, 322.68) * mm});
            skArc(sketch, "E388", {"start": v(479.02, 322.68) * mm, "mid": v(476.01, 319.67) * mm, "end": v(473, 322.68) * mm});
            skLineSegment(sketch, "E389", {"start": v(473, 322.68) * mm, "end": v(473, 340.68) * mm});
            skArc(sketch, "E390", {"start": v(473, 340.68) * mm, "mid": v(476.01, 343.69) * mm, "end": v(479.02, 340.68) * mm});
            skLineSegment(sketch, "E391", {"start": v(479.02, 340.68) * mm, "end": v(522, 340.68) * mm});
            skLineSegment(sketch, "E392", {"start": v(522, 340.68) * mm, "end": v(522, 348.68) * mm});
            skLineSegment(sketch, "E393", {"start": v(522, 348.68) * mm, "end": v(519, 351.68) * mm});
            skLineSegment(sketch, "E394", {"start": v(519, 351.68) * mm, "end": v(504, 351.68) * mm});
            skArc(sketch, "E395", {"start": v(504, 351.68) * mm, "mid": v(501, 354.69) * mm, "end": v(504, 357.7) * mm});
            skLineSegment(sketch, "E396", {"start": v(504, 357.7) * mm, "end": v(504, 605.66) * mm});
            skArc(sketch, "E397", {"start": v(504, 605.66) * mm, "mid": v(501, 608.67) * mm, "end": v(504, 611.68) * mm});
            skLineSegment(sketch, "E398", {"start": v(504, 611.68) * mm, "end": v(519, 611.68) * mm});
            skLineSegment(sketch, "E399", {"start": v(519, 611.68) * mm, "end": v(522, 614.68) * mm});
            skLineSegment(sketch, "E400", {"start": v(522, 614.68) * mm, "end": v(522, 648.68) * mm});
            skLineSegment(sketch, "E401", {"start": v(522, 648.68) * mm, "end": v(519, 651.68) * mm});
            skLineSegment(sketch, "E402", {"start": v(519, 651.68) * mm, "end": v(504, 651.68) * mm});
            skArc(sketch, "E403", {"start": v(504, 651.68) * mm, "mid": v(501, 654.7) * mm, "end": v(504, 657.7) * mm});
            skLineSegment(sketch, "E404", {"start": v(504, 657.7) * mm, "end": v(504, 905.66) * mm});
            skArc(sketch, "E405", {"start": v(504, 905.66) * mm, "mid": v(500.99, 908.67) * mm, "end": v(504, 911.68) * mm});
            skLineSegment(sketch, "E406", {"start": v(504, 911.68) * mm, "end": v(519, 911.68) * mm});
            skLineSegment(sketch, "E407", {"start": v(519, 911.68) * mm, "end": v(522, 914.68) * mm});
            skLineSegment(sketch, "E408", {"start": v(522, 914.68) * mm, "end": v(522, 948.68) * mm});
            skLineSegment(sketch, "E409", {"start": v(522, 948.68) * mm, "end": v(519, 951.68) * mm});
            skLineSegment(sketch, "E410", {"start": v(519, 951.68) * mm, "end": v(504, 951.68) * mm});
            skArc(sketch, "E411", {"start": v(504, 951.68) * mm, "mid": v(500.99, 954.7) * mm, "end": v(504, 957.7) * mm});
            skLineSegment(sketch, "E412", {"start": v(504, 957.7) * mm, "end": v(504, 1148.98) * mm});
            skArc(sketch, "E413", {"start": v(504, 1148.98) * mm, "mid": v(500.99, 1151.99) * mm, "end": v(504, 1155) * mm});
            skLineSegment(sketch, "E414", {"start": v(504, 1155) * mm, "end": v(519, 1155) * mm});
            skLineSegment(sketch, "E415", {"start": v(519, 1155) * mm, "end": v(522, 1158) * mm});
            skLineSegment(sketch, "E416", {"start": v(522, 1158) * mm, "end": v(522, 1175) * mm});
            skLineSegment(sketch, "E417", {"start": v(522, 1175) * mm, "end": v(372, 1175) * mm});
            skLineSegment(sketch, "E418", {"start": v(64.62, 1175.03) * mm, "end": v(64.62, 1051.05) * mm});
            skArc(sketch, "E419", {"start": v(64.62, 1051.05) * mm, "mid": v(67.63, 1048.04) * mm, "end": v(64.62, 1045.03) * mm});
            skLineSegment(sketch, "E420", {"start": v(64.62, 1045.03) * mm, "end": v(49.62, 1045.03) * mm});
            skLineSegment(sketch, "E421", {"start": v(49.62, 1045.03) * mm, "end": v(46.62, 1042.03) * mm});
            skLineSegment(sketch, "E422", {"start": v(46.62, 1042.03) * mm, "end": v(46.62, 1008.03) * mm});
            skLineSegment(sketch, "E423", {"start": v(46.62, 1008.03) * mm, "end": v(49.62, 1005.03) * mm});
            skLineSegment(sketch, "E424", {"start": v(49.62, 1005.03) * mm, "end": v(64.62, 1005.03) * mm});
            skArc(sketch, "E425", {"start": v(64.62, 1005.03) * mm, "mid": v(67.63, 1002.02) * mm, "end": v(64.62, 999) * mm});
            skLineSegment(sketch, "E426", {"start": v(64.62, 999) * mm, "end": v(64.63, 751.05) * mm});
            skArc(sketch, "E427", {"start": v(64.63, 751.05) * mm, "mid": v(67.64, 748.04) * mm, "end": v(64.63, 745.03) * mm});
            skLineSegment(sketch, "E428", {"start": v(64.63, 745.03) * mm, "end": v(49.63, 745.03) * mm});
            skLineSegment(sketch, "E429", {"start": v(49.63, 745.03) * mm, "end": v(46.63, 742.03) * mm});
            skLineSegment(sketch, "E430", {"start": v(46.63, 742.03) * mm, "end": v(46.63, 708.03) * mm});
            skLineSegment(sketch, "E431", {"start": v(46.63, 708.03) * mm, "end": v(49.63, 705.03) * mm});
            skLineSegment(sketch, "E432", {"start": v(49.63, 705.03) * mm, "end": v(64.63, 705.03) * mm});
            skArc(sketch, "E433", {"start": v(64.63, 705.03) * mm, "mid": v(67.64, 702.02) * mm, "end": v(64.63, 699) * mm});
            skLineSegment(sketch, "E434", {"start": v(64.63, 699) * mm, "end": v(64.63, 451.04) * mm});
            skArc(sketch, "E435", {"start": v(64.63, 451.04) * mm, "mid": v(67.64, 448.03) * mm, "end": v(64.63, 445.02) * mm});
            skLineSegment(sketch, "E436", {"start": v(64.63, 445.02) * mm, "end": v(49.63, 445.02) * mm});
            skLineSegment(sketch, "E437", {"start": v(49.63, 445.02) * mm, "end": v(46.63, 442.02) * mm});
            skLineSegment(sketch, "E438", {"start": v(46.63, 442.02) * mm, "end": v(46.63, 434.02) * mm});
            skLineSegment(sketch, "E439", {"start": v(46.63, 434.02) * mm, "end": v(89.6, 434.03) * mm});
            skArc(sketch, "E440", {"start": v(89.6, 434.03) * mm, "mid": v(92.62, 437.04) * mm, "end": v(95.63, 434.03) * mm});
            skLineSegment(sketch, "E441", {"start": v(95.63, 434.03) * mm, "end": v(95.63, 416.03) * mm});
            skArc(sketch, "E442", {"start": v(95.63, 416.03) * mm, "mid": v(92.62, 413.02) * mm, "end": v(89.6, 416.03) * mm});
            skLineSegment(sketch, "E443", {"start": v(89.6, 416.03) * mm, "end": v(46.63, 416.02) * mm});
            skLineSegment(sketch, "E444", {"start": v(46.63, 416.02) * mm, "end": v(46.63, 408.02) * mm});
            skLineSegment(sketch, "E445", {"start": v(46.63, 408.02) * mm, "end": v(49.63, 405.02) * mm});
            skLineSegment(sketch, "E446", {"start": v(49.63, 405.02) * mm, "end": v(64.63, 405.02) * mm});
            skArc(sketch, "E447", {"start": v(64.63, 405.02) * mm, "mid": v(67.64, 402.01) * mm, "end": v(64.63, 399) * mm});
            skLineSegment(sketch, "E448", {"start": v(64.63, 399) * mm, "end": v(64.64, 151.05) * mm});
            skArc(sketch, "E449", {"start": v(64.64, 151.05) * mm, "mid": v(67.65, 148.04) * mm, "end": v(64.64, 145.03) * mm});
            skLineSegment(sketch, "E450", {"start": v(64.64, 145.03) * mm, "end": v(49.64, 145.03) * mm});
            skLineSegment(sketch, "E451", {"start": v(49.64, 145.03) * mm, "end": v(46.64, 142.03) * mm});
            skLineSegment(sketch, "E452", {"start": v(46.64, 142.03) * mm, "end": v(46.64, 108.03) * mm});
            skLineSegment(sketch, "E453", {"start": v(46.64, 108.03) * mm, "end": v(49.64, 105.03) * mm});
            skLineSegment(sketch, "E454", {"start": v(49.64, 105.03) * mm, "end": v(64.64, 105.03) * mm});
            skArc(sketch, "E455", {"start": v(64.64, 105.03) * mm, "mid": v(67.65, 102.02) * mm, "end": v(64.64, 99) * mm});
            skLineSegment(sketch, "E456", {"start": v(64.64, 99) * mm, "end": v(64.64, -148.95) * mm});
            skArc(sketch, "E457", {"start": v(64.64, -148.95) * mm, "mid": v(67.65, -151.96) * mm, "end": v(64.64, -154.97) * mm});
            skLineSegment(sketch, "E458", {"start": v(64.64, -154.97) * mm, "end": v(49.64, -154.98) * mm});
            skLineSegment(sketch, "E459", {"start": v(49.64, -154.98) * mm, "end": v(46.64, -157.97) * mm});
            skLineSegment(sketch, "E460", {"start": v(46.64, -157.97) * mm, "end": v(46.64, -191.97) * mm});
            skLineSegment(sketch, "E461", {"start": v(46.64, -191.97) * mm, "end": v(49.64, -194.98) * mm});
            skLineSegment(sketch, "E462", {"start": v(49.64, -194.98) * mm, "end": v(64.64, -194.98) * mm});
            skArc(sketch, "E463", {"start": v(64.64, -194.98) * mm, "mid": v(67.65, -197.99) * mm, "end": v(64.64, -201) * mm});
            skLineSegment(sketch, "E464", {"start": v(64.64, -201) * mm, "end": v(64.65, -368.95) * mm});
            skArc(sketch, "E465", {"start": v(64.65, -368.95) * mm, "mid": v(67.66, -371.96) * mm, "end": v(64.65, -374.97) * mm});
            skLineSegment(sketch, "E466", {"start": v(64.65, -374.97) * mm, "end": v(49.65, -374.98) * mm});
            skLineSegment(sketch, "E467", {"start": v(49.65, -374.98) * mm, "end": v(46.65, -377.98) * mm});
            skLineSegment(sketch, "E468", {"start": v(46.65, -377.98) * mm, "end": v(46.65, -411.98) * mm});
            skLineSegment(sketch, "E469", {"start": v(46.65, -411.98) * mm, "end": v(49.65, -414.98) * mm});
            skLineSegment(sketch, "E470", {"start": v(49.65, -414.98) * mm, "end": v(64.65, -414.98) * mm});
            skArc(sketch, "E471", {"start": v(64.65, -414.98) * mm, "mid": v(67.66, -417.99) * mm, "end": v(64.65, -421) * mm});
            skLineSegment(sketch, "E472", {"start": v(64.65, -421) * mm, "end": v(64.65, -424.74) * mm});
            skLineSegment(sketch, "E473", {"start": v(64.65, -424.74) * mm, "end": v(178.65, -424.74) * mm});
            skLineSegment(sketch, "E474", {"start": v(178.65, -424.74) * mm, "end": v(178.65, -421) * mm});
            skArc(sketch, "E475", {"start": v(178.65, -421) * mm, "mid": v(175.64, -417.98) * mm, "end": v(178.65, -414.97) * mm});
            skLineSegment(sketch, "E476", {"start": v(178.65, -414.97) * mm, "end": v(193.65, -414.97) * mm});
            skLineSegment(sketch, "E477", {"start": v(193.65, -414.97) * mm, "end": v(196.65, -411.97) * mm});
            skLineSegment(sketch, "E478", {"start": v(196.65, -411.97) * mm, "end": v(196.65, -377.97) * mm});
            skLineSegment(sketch, "E479", {"start": v(196.65, -377.97) * mm, "end": v(193.65, -374.97) * mm});
            skLineSegment(sketch, "E480", {"start": v(193.65, -374.97) * mm, "end": v(178.65, -374.97) * mm});
            skArc(sketch, "E481", {"start": v(178.65, -374.97) * mm, "mid": v(175.64, -371.96) * mm, "end": v(178.65, -368.95) * mm});
            skLineSegment(sketch, "E482", {"start": v(178.65, -368.95) * mm, "end": v(178.64, -201) * mm});
            skArc(sketch, "E483", {"start": v(178.64, -201) * mm, "mid": v(175.63, -197.98) * mm, "end": v(178.64, -194.97) * mm});
            skLineSegment(sketch, "E484", {"start": v(178.64, -194.97) * mm, "end": v(193.64, -194.97) * mm});
            skLineSegment(sketch, "E485", {"start": v(193.64, -194.97) * mm, "end": v(196.64, -191.97) * mm});
            skLineSegment(sketch, "E486", {"start": v(196.64, -191.97) * mm, "end": v(196.64, -157.97) * mm});
            skLineSegment(sketch, "E487", {"start": v(196.64, -157.97) * mm, "end": v(193.64, -154.97) * mm});
            skLineSegment(sketch, "E488", {"start": v(193.64, -154.97) * mm, "end": v(178.64, -154.97) * mm});
            skArc(sketch, "E489", {"start": v(178.64, -154.97) * mm, "mid": v(175.63, -151.96) * mm, "end": v(178.64, -148.95) * mm});
            skLineSegment(sketch, "E490", {"start": v(178.64, -148.95) * mm, "end": v(178.64, 99) * mm});
            skArc(sketch, "E491", {"start": v(178.64, 99) * mm, "mid": v(175.63, 102.02) * mm, "end": v(178.64, 105.03) * mm});
            skLineSegment(sketch, "E492", {"start": v(178.64, 105.03) * mm, "end": v(193.64, 105.03) * mm});
            skLineSegment(sketch, "E493", {"start": v(193.64, 105.03) * mm, "end": v(196.64, 108.03) * mm});
            skLineSegment(sketch, "E494", {"start": v(196.64, 108.03) * mm, "end": v(196.64, 142.03) * mm});
            skLineSegment(sketch, "E495", {"start": v(196.64, 142.03) * mm, "end": v(193.64, 145.03) * mm});
            skLineSegment(sketch, "E496", {"start": v(193.64, 145.03) * mm, "end": v(178.64, 145.03) * mm});
            skArc(sketch, "E497", {"start": v(178.64, 145.03) * mm, "mid": v(175.63, 148.04) * mm, "end": v(178.64, 151.05) * mm});
            skLineSegment(sketch, "E498", {"start": v(178.64, 151.05) * mm, "end": v(178.63, 399) * mm});
            skArc(sketch, "E499", {"start": v(178.63, 399) * mm, "mid": v(175.62, 402.02) * mm, "end": v(178.63, 405.03) * mm});
            skLineSegment(sketch, "E500", {"start": v(178.63, 405.03) * mm, "end": v(193.63, 405.03) * mm});
            skLineSegment(sketch, "E501", {"start": v(193.63, 405.03) * mm, "end": v(196.63, 408.03) * mm});
            skLineSegment(sketch, "E502", {"start": v(196.63, 408.03) * mm, "end": v(196.63, 416.03) * mm});
            skLineSegment(sketch, "E503", {"start": v(196.63, 416.03) * mm, "end": v(153.65, 416.03) * mm});
            skArc(sketch, "E504", {"start": v(153.65, 416.03) * mm, "mid": v(150.64, 413.02) * mm, "end": v(147.63, 416.03) * mm});
            skLineSegment(sketch, "E505", {"start": v(147.63, 416.03) * mm, "end": v(147.63, 434.03) * mm});
            skArc(sketch, "E506", {"start": v(147.63, 434.03) * mm, "mid": v(150.64, 437.04) * mm, "end": v(153.65, 434.03) * mm});
            skLineSegment(sketch, "E507", {"start": v(153.65, 434.03) * mm, "end": v(196.63, 434.03) * mm});
            skLineSegment(sketch, "E508", {"start": v(196.63, 434.03) * mm, "end": v(196.63, 442.03) * mm});
            skLineSegment(sketch, "E509", {"start": v(196.63, 442.03) * mm, "end": v(193.63, 445.03) * mm});
            skLineSegment(sketch, "E510", {"start": v(193.63, 445.03) * mm, "end": v(178.63, 445.03) * mm});
            skArc(sketch, "E511", {"start": v(178.63, 445.03) * mm, "mid": v(175.62, 448.04) * mm, "end": v(178.63, 451.05) * mm});
            skLineSegment(sketch, "E512", {"start": v(178.63, 451.05) * mm, "end": v(178.63, 699) * mm});
            skArc(sketch, "E513", {"start": v(178.63, 699) * mm, "mid": v(175.62, 702.02) * mm, "end": v(178.63, 705.03) * mm});
            skLineSegment(sketch, "E514", {"start": v(178.63, 705.03) * mm, "end": v(193.63, 705.03) * mm});
            skLineSegment(sketch, "E515", {"start": v(193.63, 705.03) * mm, "end": v(196.63, 708.03) * mm});
            skLineSegment(sketch, "E516", {"start": v(196.63, 708.03) * mm, "end": v(196.63, 742.03) * mm});
            skLineSegment(sketch, "E517", {"start": v(196.63, 742.03) * mm, "end": v(193.63, 745.03) * mm});
            skLineSegment(sketch, "E518", {"start": v(193.63, 745.03) * mm, "end": v(178.63, 745.03) * mm});
            skArc(sketch, "E519", {"start": v(178.63, 745.03) * mm, "mid": v(175.62, 748.04) * mm, "end": v(178.63, 751.05) * mm});
            skLineSegment(sketch, "E520", {"start": v(178.63, 751.05) * mm, "end": v(178.62, 999) * mm});
            skArc(sketch, "E521", {"start": v(178.62, 999) * mm, "mid": v(175.61, 1002.02) * mm, "end": v(178.62, 1005.03) * mm});
            skLineSegment(sketch, "E522", {"start": v(178.62, 1005.03) * mm, "end": v(193.62, 1005.03) * mm});
            skLineSegment(sketch, "E523", {"start": v(193.62, 1005.03) * mm, "end": v(196.62, 1008.03) * mm});
            skLineSegment(sketch, "E524", {"start": v(196.62, 1008.03) * mm, "end": v(196.62, 1042.03) * mm});
            skLineSegment(sketch, "E525", {"start": v(196.62, 1042.03) * mm, "end": v(193.62, 1045.03) * mm});
            skLineSegment(sketch, "E526", {"start": v(193.62, 1045.03) * mm, "end": v(178.62, 1045.03) * mm});
            skArc(sketch, "E527", {"start": v(178.62, 1045.03) * mm, "mid": v(175.61, 1048.04) * mm, "end": v(178.62, 1051.05) * mm});
            skLineSegment(sketch, "E528", {"start": v(178.62, 1051.05) * mm, "end": v(178.62, 1175.03) * mm});
            skLineSegment(sketch, "E529", {"start": v(178.62, 1175.03) * mm, "end": v(64.62, 1175.03) * mm});
            skLineSegment(sketch, "E530", {"start": v(201.97, 1175) * mm, "end": v(201.97, 1158) * mm});
            skLineSegment(sketch, "E531", {"start": v(201.97, 1158) * mm, "end": v(204.97, 1155) * mm});
            skLineSegment(sketch, "E532", {"start": v(204.97, 1155) * mm, "end": v(219.97, 1155) * mm});
            skArc(sketch, "E533", {"start": v(219.97, 1155) * mm, "mid": v(222.98, 1151.99) * mm, "end": v(219.97, 1148.98) * mm});
            skLineSegment(sketch, "E534", {"start": v(219.97, 1148.98) * mm, "end": v(219.97, 957.7) * mm});
            skArc(sketch, "E535", {"start": v(219.97, 957.7) * mm, "mid": v(222.98, 954.69) * mm, "end": v(219.97, 951.68) * mm});
            skLineSegment(sketch, "E536", {"start": v(219.97, 951.68) * mm, "end": v(204.97, 951.68) * mm});
            skLineSegment(sketch, "E537", {"start": v(204.97, 951.68) * mm, "end": v(201.97, 948.68) * mm});
            skLineSegment(sketch, "E538", {"start": v(201.97, 948.68) * mm, "end": v(201.97, 914.68) * mm});
            skLineSegment(sketch, "E539", {"start": v(201.97, 914.68) * mm, "end": v(204.97, 911.68) * mm});
            skLineSegment(sketch, "E540", {"start": v(204.97, 911.68) * mm, "end": v(219.97, 911.68) * mm});
            skArc(sketch, "E541", {"start": v(219.97, 911.68) * mm, "mid": v(222.98, 908.67) * mm, "end": v(219.97, 905.66) * mm});
            skLineSegment(sketch, "E542", {"start": v(219.97, 905.66) * mm, "end": v(219.97, 657.7) * mm});
            skArc(sketch, "E543", {"start": v(219.97, 657.7) * mm, "mid": v(222.98, 654.69) * mm, "end": v(219.97, 651.68) * mm});
            skLineSegment(sketch, "E544", {"start": v(219.97, 651.68) * mm, "end": v(204.97, 651.68) * mm});
            skLineSegment(sketch, "E545", {"start": v(204.97, 651.68) * mm, "end": v(201.97, 648.68) * mm});
            skLineSegment(sketch, "E546", {"start": v(201.97, 648.68) * mm, "end": v(201.97, 614.68) * mm});
            skLineSegment(sketch, "E547", {"start": v(201.97, 614.68) * mm, "end": v(204.97, 611.68) * mm});
            skLineSegment(sketch, "E548", {"start": v(204.97, 611.68) * mm, "end": v(219.97, 611.68) * mm});
            skArc(sketch, "E549", {"start": v(219.97, 611.68) * mm, "mid": v(222.98, 608.67) * mm, "end": v(219.97, 605.66) * mm});
            skLineSegment(sketch, "E550", {"start": v(219.97, 605.66) * mm, "end": v(219.98, 357.7) * mm});
            skArc(sketch, "E551", {"start": v(219.98, 357.7) * mm, "mid": v(222.99, 354.69) * mm, "end": v(219.98, 351.68) * mm});
            skLineSegment(sketch, "E552", {"start": v(219.98, 351.68) * mm, "end": v(204.98, 351.68) * mm});
            skLineSegment(sketch, "E553", {"start": v(204.98, 351.68) * mm, "end": v(201.98, 348.68) * mm});
            skLineSegment(sketch, "E554", {"start": v(201.98, 348.68) * mm, "end": v(201.98, 340.68) * mm});
            skLineSegment(sketch, "E555", {"start": v(201.98, 340.68) * mm, "end": v(244.96, 340.68) * mm});
            skArc(sketch, "E556", {"start": v(244.96, 340.68) * mm, "mid": v(247.97, 343.69) * mm, "end": v(250.98, 340.68) * mm});
            skLineSegment(sketch, "E557", {"start": v(250.98, 340.68) * mm, "end": v(250.98, 322.68) * mm});
            skArc(sketch, "E558", {"start": v(250.98, 322.68) * mm, "mid": v(247.97, 319.67) * mm, "end": v(244.96, 322.68) * mm});
            skLineSegment(sketch, "E559", {"start": v(244.96, 322.68) * mm, "end": v(201.98, 322.68) * mm});
            skLineSegment(sketch, "E560", {"start": v(201.98, 322.68) * mm, "end": v(201.98, 314.68) * mm});
            skLineSegment(sketch, "E561", {"start": v(201.98, 314.68) * mm, "end": v(204.98, 311.68) * mm});
            skLineSegment(sketch, "E562", {"start": v(204.98, 311.68) * mm, "end": v(219.98, 311.68) * mm});
            skArc(sketch, "E563", {"start": v(219.98, 311.68) * mm, "mid": v(222.99, 308.67) * mm, "end": v(219.98, 305.66) * mm});
            skLineSegment(sketch, "E564", {"start": v(219.98, 305.66) * mm, "end": v(219.98, 57.7) * mm});
            skArc(sketch, "E565", {"start": v(219.98, 57.7) * mm, "mid": v(223, 54.69) * mm, "end": v(219.98, 51.68) * mm});
            skLineSegment(sketch, "E566", {"start": v(219.98, 51.68) * mm, "end": v(204.98, 51.68) * mm});
            skLineSegment(sketch, "E567", {"start": v(204.98, 51.68) * mm, "end": v(201.98, 48.68) * mm});
            skLineSegment(sketch, "E568", {"start": v(201.98, 48.68) * mm, "end": v(201.98, 14.68) * mm});
            skLineSegment(sketch, "E569", {"start": v(201.98, 14.68) * mm, "end": v(204.98, 11.68) * mm});
            skLineSegment(sketch, "E570", {"start": v(204.98, 11.68) * mm, "end": v(219.98, 11.68) * mm});
            skArc(sketch, "E571", {"start": v(219.98, 11.68) * mm, "mid": v(223, 8.67) * mm, "end": v(219.98, 5.66) * mm});
            skLineSegment(sketch, "E572", {"start": v(219.98, 5.66) * mm, "end": v(219.99, -242.3) * mm});
            skArc(sketch, "E573", {"start": v(219.99, -242.3) * mm, "mid": v(223, -245.31) * mm, "end": v(219.99, -248.32) * mm});
            skLineSegment(sketch, "E574", {"start": v(219.99, -248.32) * mm, "end": v(204.99, -248.32) * mm});
            skLineSegment(sketch, "E575", {"start": v(204.99, -248.32) * mm, "end": v(201.99, -251.32) * mm});
            skLineSegment(sketch, "E576", {"start": v(201.99, -251.32) * mm, "end": v(201.99, -285.32) * mm});
            skLineSegment(sketch, "E577", {"start": v(201.99, -285.32) * mm, "end": v(204.99, -288.32) * mm});
            skLineSegment(sketch, "E578", {"start": v(204.99, -288.32) * mm, "end": v(219.99, -288.32) * mm});
            skArc(sketch, "E579", {"start": v(219.99, -288.32) * mm, "mid": v(223, -291.33) * mm, "end": v(219.99, -294.34) * mm});
            skLineSegment(sketch, "E580", {"start": v(219.99, -294.34) * mm, "end": v(220, -462.3) * mm});
            skArc(sketch, "E581", {"start": v(220, -462.3) * mm, "mid": v(223, -465.31) * mm, "end": v(220, -468.32) * mm});
            skLineSegment(sketch, "E582", {"start": v(220, -468.32) * mm, "end": v(205, -468.32) * mm});
            skLineSegment(sketch, "E583", {"start": v(205, -468.32) * mm, "end": v(202, -471.32) * mm});
            skLineSegment(sketch, "E584", {"start": v(202, -471.32) * mm, "end": v(202, -505.32) * mm});
            skLineSegment(sketch, "E585", {"start": v(202, -505.32) * mm, "end": v(205, -508.32) * mm});
            skLineSegment(sketch, "E586", {"start": v(205, -508.32) * mm, "end": v(220, -508.32) * mm});
            skArc(sketch, "E587", {"start": v(220, -508.32) * mm, "mid": v(223, -511.33) * mm, "end": v(220, -514.34) * mm});
            skLineSegment(sketch, "E588", {"start": v(220, -514.34) * mm, "end": v(220, -518.09) * mm});
            skLineSegment(sketch, "E589", {"start": v(220, -518.09) * mm, "end": v(334, -518.09) * mm});
            skLineSegment(sketch, "E590", {"start": v(334, -518.09) * mm, "end": v(334, -514.34) * mm});
            skArc(sketch, "E591", {"start": v(334, -514.34) * mm, "mid": v(330.98, -511.33) * mm, "end": v(334, -508.32) * mm});
            skLineSegment(sketch, "E592", {"start": v(334, -508.32) * mm, "end": v(349, -508.32) * mm});
            skLineSegment(sketch, "E593", {"start": v(349, -508.32) * mm, "end": v(352, -505.32) * mm});
            skLineSegment(sketch, "E594", {"start": v(352, -505.32) * mm, "end": v(352, -471.32) * mm});
            skLineSegment(sketch, "E595", {"start": v(352, -471.32) * mm, "end": v(349, -468.32) * mm});
            skLineSegment(sketch, "E596", {"start": v(349, -468.32) * mm, "end": v(334, -468.32) * mm});
            skArc(sketch, "E597", {"start": v(334, -468.32) * mm, "mid": v(330.98, -465.31) * mm, "end": v(334, -462.3) * mm});
            skLineSegment(sketch, "E598", {"start": v(334, -462.3) * mm, "end": v(334, -294.34) * mm});
            skArc(sketch, "E599", {"start": v(334, -294.34) * mm, "mid": v(330.98, -291.33) * mm, "end": v(334, -288.32) * mm});
            skLineSegment(sketch, "E600", {"start": v(334, -288.32) * mm, "end": v(349, -288.32) * mm});
            skLineSegment(sketch, "E601", {"start": v(349, -288.32) * mm, "end": v(352, -285.32) * mm});
            skLineSegment(sketch, "E602", {"start": v(352, -285.32) * mm, "end": v(351.99, -251.32) * mm});
            skLineSegment(sketch, "E603", {"start": v(351.99, -251.32) * mm, "end": v(348.99, -248.32) * mm});
            skLineSegment(sketch, "E604", {"start": v(348.99, -248.32) * mm, "end": v(333.99, -248.32) * mm});
            skArc(sketch, "E605", {"start": v(333.99, -248.32) * mm, "mid": v(330.98, -245.31) * mm, "end": v(333.99, -242.3) * mm});
            skLineSegment(sketch, "E606", {"start": v(333.99, -242.3) * mm, "end": v(333.99, 5.66) * mm});
            skArc(sketch, "E607", {"start": v(333.99, 5.66) * mm, "mid": v(330.98, 8.67) * mm, "end": v(333.99, 11.68) * mm});
            skLineSegment(sketch, "E608", {"start": v(333.99, 11.68) * mm, "end": v(348.99, 11.68) * mm});
            skLineSegment(sketch, "E609", {"start": v(348.99, 11.68) * mm, "end": v(351.99, 14.68) * mm});
            skLineSegment(sketch, "E610", {"start": v(351.99, 14.68) * mm, "end": v(351.98, 48.68) * mm});
            skLineSegment(sketch, "E611", {"start": v(351.98, 48.68) * mm, "end": v(348.98, 51.68) * mm});
            skLineSegment(sketch, "E612", {"start": v(348.98, 51.68) * mm, "end": v(333.98, 51.68) * mm});
            skArc(sketch, "E613", {"start": v(333.98, 51.68) * mm, "mid": v(330.97, 54.69) * mm, "end": v(333.98, 57.7) * mm});
            skLineSegment(sketch, "E614", {"start": v(333.98, 57.7) * mm, "end": v(333.98, 305.66) * mm});
            skArc(sketch, "E615", {"start": v(333.98, 305.66) * mm, "mid": v(330.97, 308.67) * mm, "end": v(333.98, 311.68) * mm});
            skLineSegment(sketch, "E616", {"start": v(333.98, 311.68) * mm, "end": v(348.98, 311.68) * mm});
            skLineSegment(sketch, "E617", {"start": v(348.98, 311.68) * mm, "end": v(351.98, 314.68) * mm});
            skLineSegment(sketch, "E618", {"start": v(351.98, 314.68) * mm, "end": v(351.98, 322.68) * mm});
            skLineSegment(sketch, "E619", {"start": v(351.98, 322.68) * mm, "end": v(309, 322.68) * mm});
            skArc(sketch, "E620", {"start": v(309, 322.68) * mm, "mid": v(305.99, 319.67) * mm, "end": v(302.98, 322.68) * mm});
            skLineSegment(sketch, "E621", {"start": v(302.98, 322.68) * mm, "end": v(302.98, 340.68) * mm});
            skArc(sketch, "E622", {"start": v(302.98, 340.68) * mm, "mid": v(305.99, 343.69) * mm, "end": v(309, 340.68) * mm});
            skLineSegment(sketch, "E623", {"start": v(309, 340.68) * mm, "end": v(351.98, 340.68) * mm});
            skLineSegment(sketch, "E624", {"start": v(351.98, 340.68) * mm, "end": v(351.98, 348.68) * mm});
            skLineSegment(sketch, "E625", {"start": v(351.98, 348.68) * mm, "end": v(348.98, 351.68) * mm});
            skLineSegment(sketch, "E626", {"start": v(348.98, 351.68) * mm, "end": v(333.98, 351.68) * mm});
            skArc(sketch, "E627", {"start": v(333.98, 351.68) * mm, "mid": v(330.97, 354.69) * mm, "end": v(333.98, 357.7) * mm});
            skLineSegment(sketch, "E628", {"start": v(333.98, 357.7) * mm, "end": v(333.97, 605.66) * mm});
            skArc(sketch, "E629", {"start": v(333.97, 605.66) * mm, "mid": v(330.96, 608.67) * mm, "end": v(333.97, 611.68) * mm});
            skLineSegment(sketch, "E630", {"start": v(333.97, 611.68) * mm, "end": v(348.97, 611.68) * mm});
            skLineSegment(sketch, "E631", {"start": v(348.97, 611.68) * mm, "end": v(351.97, 614.68) * mm});
            skLineSegment(sketch, "E632", {"start": v(351.97, 614.68) * mm, "end": v(351.97, 648.68) * mm});
            skLineSegment(sketch, "E633", {"start": v(351.97, 648.68) * mm, "end": v(348.97, 651.68) * mm});
            skLineSegment(sketch, "E634", {"start": v(348.97, 651.68) * mm, "end": v(333.97, 651.68) * mm});
            skArc(sketch, "E635", {"start": v(333.97, 651.68) * mm, "mid": v(330.96, 654.7) * mm, "end": v(333.97, 657.7) * mm});
            skLineSegment(sketch, "E636", {"start": v(333.97, 657.7) * mm, "end": v(333.97, 905.66) * mm});
            skArc(sketch, "E637", {"start": v(333.97, 905.66) * mm, "mid": v(330.96, 908.67) * mm, "end": v(333.97, 911.68) * mm});
            skLineSegment(sketch, "E638", {"start": v(333.97, 911.68) * mm, "end": v(348.97, 911.68) * mm});
            skLineSegment(sketch, "E639", {"start": v(348.97, 911.68) * mm, "end": v(351.97, 914.68) * mm});
            skLineSegment(sketch, "E640", {"start": v(351.97, 914.68) * mm, "end": v(351.97, 948.68) * mm});
            skLineSegment(sketch, "E641", {"start": v(351.97, 948.68) * mm, "end": v(348.97, 951.68) * mm});
            skLineSegment(sketch, "E642", {"start": v(348.97, 951.68) * mm, "end": v(333.97, 951.68) * mm});
            skArc(sketch, "E643", {"start": v(333.97, 951.68) * mm, "mid": v(330.96, 954.7) * mm, "end": v(333.97, 957.7) * mm});
            skLineSegment(sketch, "E644", {"start": v(333.97, 957.7) * mm, "end": v(333.97, 1148.98) * mm});
            skArc(sketch, "E645", {"start": v(333.97, 1148.98) * mm, "mid": v(330.96, 1151.99) * mm, "end": v(333.97, 1155) * mm});
            skLineSegment(sketch, "E646", {"start": v(333.97, 1155) * mm, "end": v(348.97, 1155) * mm});
            skLineSegment(sketch, "E647", {"start": v(348.97, 1155) * mm, "end": v(351.97, 1158) * mm});
            skLineSegment(sketch, "E648", {"start": v(351.97, 1158) * mm, "end": v(351.97, 1175) * mm});
            skLineSegment(sketch, "E649", {"start": v(351.97, 1175) * mm, "end": v(201.97, 1175) * mm});
            skLineSegment(sketch, "E650", {"start": v(-49.43, 1058.71) * mm, "end": v(-122.33, 1058.71) * mm});
            skLineSegment(sketch, "E651", {"start": v(-122.33, 1058.71) * mm, "end": v(-122.33, 1174.71) * mm});
            skLineSegment(sketch, "E652", {"start": v(-122.33, 1174.71) * mm, "end": v(26.47, 1174.71) * mm});
            skLineSegment(sketch, "E653", {"start": v(26.47, 1174.71) * mm, "end": v(26.47, 924.91) * mm});
            skLineSegment(sketch, "E654", {"start": v(26.47, 924.91) * mm, "end": v(-122.33, 924.91) * mm});
            skLineSegment(sketch, "E655", {"start": v(-122.33, 924.91) * mm, "end": v(-122.33, 1040.91) * mm});
            skLineSegment(sketch, "E656", {"start": v(-122.33, 1040.91) * mm, "end": v(-49.43, 1040.91) * mm});
            skArc(sketch, "E657", {"start": v(-49.43, 1040.91) * mm, "mid": v(-47.24, 1041.82) * mm, "end": v(-46.33, 1044.01) * mm});
            skLineSegment(sketch, "E658", {"start": v(-46.33, 1044.01) * mm, "end": v(-46.33, 1055.61) * mm});
            skArc(sketch, "E659", {"start": v(-46.33, 1055.61) * mm, "mid": v(-47.24, 1057.8) * mm, "end": v(-49.43, 1058.71) * mm});
            skLineSegment(sketch, "E660", {"start": v(-218.23, 1058.71) * mm, "end": v(-291.13, 1058.71) * mm});
            skLineSegment(sketch, "E661", {"start": v(-291.13, 1058.71) * mm, "end": v(-291.13, 1174.71) * mm});
            skLineSegment(sketch, "E662", {"start": v(-291.13, 1174.71) * mm, "end": v(-142.33, 1174.71) * mm});
            skLineSegment(sketch, "E663", {"start": v(-142.33, 1174.71) * mm, "end": v(-142.33, 924.91) * mm});
            skLineSegment(sketch, "E664", {"start": v(-142.33, 924.91) * mm, "end": v(-291.13, 924.91) * mm});
            skLineSegment(sketch, "E665", {"start": v(-291.13, 924.91) * mm, "end": v(-291.13, 1040.91) * mm});
            skLineSegment(sketch, "E666", {"start": v(-291.13, 1040.91) * mm, "end": v(-218.23, 1040.91) * mm});
            skArc(sketch, "E667", {"start": v(-218.23, 1040.91) * mm, "mid": v(-216.04, 1041.82) * mm, "end": v(-215.13, 1044.01) * mm});
            skLineSegment(sketch, "E668", {"start": v(-215.13, 1044.01) * mm, "end": v(-215.13, 1055.61) * mm});
            skArc(sketch, "E669", {"start": v(-215.13, 1055.61) * mm, "mid": v(-216.04, 1057.8) * mm, "end": v(-218.23, 1058.71) * mm});
            skLineSegment(sketch, "E670", {"start": v(25.26, -1104.16) * mm, "end": v(16.26, -1119.75) * mm});
            skLineSegment(sketch, "E671", {"start": v(16.26, -1119.75) * mm, "end": v(50.9, -1139.75) * mm});
            skLineSegment(sketch, "E672", {"start": v(50.9, -1139.75) * mm, "end": v(59.9, -1124.16) * mm});
            skLineSegment(sketch, "E673", {"start": v(59.9, -1124.16) * mm, "end": v(25.26, -1104.16) * mm});
            skLineSegment(sketch, "E674", {"start": v(141.26, -903.25) * mm, "end": v(132.26, -918.83) * mm});
            skLineSegment(sketch, "E675", {"start": v(132.26, -918.83) * mm, "end": v(166.9, -938.83) * mm});
            skLineSegment(sketch, "E676", {"start": v(166.9, -938.83) * mm, "end": v(175.9, -923.25) * mm});
            skLineSegment(sketch, "E677", {"start": v(175.9, -923.25) * mm, "end": v(141.26, -903.25) * mm});
            skLineSegment(sketch, "E678", {"start": v(-234.55, -954.16) * mm, "end": v(-243.55, -969.75) * mm});
            skLineSegment(sketch, "E679", {"start": v(-243.55, -969.75) * mm, "end": v(-208.9, -989.75) * mm});
            skLineSegment(sketch, "E680", {"start": v(-208.9, -989.75) * mm, "end": v(-199.9, -974.16) * mm});
            skLineSegment(sketch, "E681", {"start": v(-199.9, -974.16) * mm, "end": v(-234.55, -954.16) * mm});
            skLineSegment(sketch, "E682", {"start": v(-118.55, -753.25) * mm, "end": v(-127.55, -768.83) * mm});
            skLineSegment(sketch, "E683", {"start": v(-127.55, -768.83) * mm, "end": v(-92.9, -788.83) * mm});
            skLineSegment(sketch, "E684", {"start": v(-92.9, -788.83) * mm, "end": v(-83.9, -773.25) * mm});
            skLineSegment(sketch, "E685", {"start": v(-83.9, -773.25) * mm, "end": v(-118.55, -753.25) * mm});
            skLineSegment(sketch, "E686", {"start": v(-494.35, -804.16) * mm, "end": v(-503.35, -819.75) * mm});
            skLineSegment(sketch, "E687", {"start": v(-503.35, -819.75) * mm, "end": v(-468.71, -839.75) * mm});
            skLineSegment(sketch, "E688", {"start": v(-468.71, -839.75) * mm, "end": v(-459.71, -824.16) * mm});
            skLineSegment(sketch, "E689", {"start": v(-459.71, -824.16) * mm, "end": v(-494.35, -804.16) * mm});
            skLineSegment(sketch, "E690", {"start": v(-539.25, -686.4) * mm, "end": v(-557.25, -686.4) * mm});
            skLineSegment(sketch, "E691", {"start": v(-557.25, -686.4) * mm, "end": v(-557.25, -726.4) * mm});
            skLineSegment(sketch, "E692", {"start": v(-557.25, -726.4) * mm, "end": v(-539.25, -726.4) * mm});
            skLineSegment(sketch, "E693", {"start": v(-539.25, -726.4) * mm, "end": v(-539.25, -686.4) * mm});
            skLineSegment(sketch, "E694", {"start": v(-325.25, 473.6) * mm, "end": v(-307.25, 473.6) * mm});
            skLineSegment(sketch, "E695", {"start": v(-307.25, 473.6) * mm, "end": v(-307.25, 513.6) * mm});
            skLineSegment(sketch, "E696", {"start": v(-307.25, 513.6) * mm, "end": v(-325.25, 513.6) * mm});
            skLineSegment(sketch, "E697", {"start": v(-325.25, 513.6) * mm, "end": v(-325.25, 473.6) * mm});
            skLineSegment(sketch, "E698", {"start": v(-412.25, 484.6) * mm, "end": v(-412.25, 502.6) * mm});
            skLineSegment(sketch, "E699", {"start": v(-412.25, 502.6) * mm, "end": v(-452.25, 502.6) * mm});
            skLineSegment(sketch, "E700", {"start": v(-452.25, 502.6) * mm, "end": v(-452.25, 484.6) * mm});
            skLineSegment(sketch, "E701", {"start": v(-452.25, 484.6) * mm, "end": v(-412.25, 484.6) * mm});
            skLineSegment(sketch, "E702", {"start": v(-539.25, 473.6) * mm, "end": v(-539.25, 513.6) * mm});
            skLineSegment(sketch, "E703", {"start": v(-539.25, 513.6) * mm, "end": v(-557.25, 513.6) * mm});
            skLineSegment(sketch, "E704", {"start": v(-557.25, 513.6) * mm, "end": v(-557.25, 473.6) * mm});
            skLineSegment(sketch, "E705", {"start": v(-557.25, 473.6) * mm, "end": v(-539.25, 473.6) * mm});
            skLineSegment(sketch, "E706", {"start": v(-325.25, -386.4) * mm, "end": v(-325.25, -426.4) * mm});
            skLineSegment(sketch, "E707", {"start": v(-325.25, -426.4) * mm, "end": v(-307.25, -426.4) * mm});
            skLineSegment(sketch, "E708", {"start": v(-307.25, -426.4) * mm, "end": v(-307.25, -386.4) * mm});
            skLineSegment(sketch, "E709", {"start": v(-307.25, -386.4) * mm, "end": v(-325.25, -386.4) * mm});
            skLineSegment(sketch, "E710", {"start": v(-539.25, -386.4) * mm, "end": v(-557.25, -386.4) * mm});
            skLineSegment(sketch, "E711", {"start": v(-557.25, -386.4) * mm, "end": v(-557.25, -426.4) * mm});
            skLineSegment(sketch, "E712", {"start": v(-557.25, -426.4) * mm, "end": v(-539.25, -426.4) * mm});
            skLineSegment(sketch, "E713", {"start": v(-539.25, -426.4) * mm, "end": v(-539.25, -386.4) * mm});
            skLineSegment(sketch, "E714", {"start": v(-325.25, 173.6) * mm, "end": v(-307.25, 173.6) * mm});
            skLineSegment(sketch, "E715", {"start": v(-307.25, 173.6) * mm, "end": v(-307.25, 213.6) * mm});
            skLineSegment(sketch, "E716", {"start": v(-307.25, 213.6) * mm, "end": v(-325.25, 213.6) * mm});
            skLineSegment(sketch, "E717", {"start": v(-325.25, 213.6) * mm, "end": v(-325.25, 173.6) * mm});
            skLineSegment(sketch, "E718", {"start": v(-539.25, 173.6) * mm, "end": v(-539.25, 213.6) * mm});
            skLineSegment(sketch, "E719", {"start": v(-539.25, 213.6) * mm, "end": v(-557.25, 213.6) * mm});
            skLineSegment(sketch, "E720", {"start": v(-557.25, 213.6) * mm, "end": v(-557.25, 173.6) * mm});
            skLineSegment(sketch, "E721", {"start": v(-557.25, 173.6) * mm, "end": v(-539.25, 173.6) * mm});
            skLineSegment(sketch, "E722", {"start": v(-325.25, -86.4) * mm, "end": v(-325.25, -126.4) * mm});
            skLineSegment(sketch, "E723", {"start": v(-325.25, -126.4) * mm, "end": v(-307.25, -126.4) * mm});
            skLineSegment(sketch, "E724", {"start": v(-307.25, -126.4) * mm, "end": v(-307.25, -86.4) * mm});
            skLineSegment(sketch, "E725", {"start": v(-307.25, -86.4) * mm, "end": v(-325.25, -86.4) * mm});
            skLineSegment(sketch, "E726", {"start": v(-539.25, -86.4) * mm, "end": v(-557.25, -86.4) * mm});
            skLineSegment(sketch, "E727", {"start": v(-557.25, -86.4) * mm, "end": v(-557.25, -126.4) * mm});
            skLineSegment(sketch, "E728", {"start": v(-557.25, -126.4) * mm, "end": v(-539.25, -126.4) * mm});
            skLineSegment(sketch, "E729", {"start": v(-539.25, -126.4) * mm, "end": v(-539.25, -86.4) * mm});
            skArc(sketch, "E730", {"start": v(-273.75, -780.57) * mm, "mid": v(-269.46, -779.15) * mm, "end": v(-270.7, -774.8) * mm});
            skLineSegment(sketch, "E731", {"start": v(-270.7, -774.8) * mm, "end": v(-286.3, -765.8) * mm});
            skArc(sketch, "E732", {"start": v(-286.3, -765.8) * mm, "mid": v(-290.7, -766.89) * mm, "end": v(-289.77, -771.32) * mm});
            skLineSegment(sketch, "E733", {"start": v(-289.77, -771.32) * mm, "end": v(-313.5, -812.43) * mm});
            skArc(sketch, "E734", {"start": v(-313.5, -812.43) * mm, "mid": v(-317.8, -813.85) * mm, "end": v(-316.55, -818.2) * mm});
            skLineSegment(sketch, "E735", {"start": v(-316.55, -818.2) * mm, "end": v(-300.96, -827.2) * mm});
            skArc(sketch, "E736", {"start": v(-300.96, -827.2) * mm, "mid": v(-296.56, -826.11) * mm, "end": v(-297.48, -821.68) * mm});
            skLineSegment(sketch, "E737", {"start": v(-297.48, -821.68) * mm, "end": v(-273.75, -780.57) * mm});
            skArc(sketch, "E738", {"start": v(-402, -547.4) * mm, "mid": v(-405.14, -544.14) * mm, "end": v(-408.52, -547.15) * mm});
            skLineSegment(sketch, "E739", {"start": v(-408.52, -547.15) * mm, "end": v(-455.98, -547.15) * mm});
            skArc(sketch, "E740", {"start": v(-455.98, -547.15) * mm, "mid": v(-459.36, -544.15) * mm, "end": v(-462.5, -547.4) * mm});
            skLineSegment(sketch, "E741", {"start": v(-462.5, -547.4) * mm, "end": v(-462.5, -565.4) * mm});
            skArc(sketch, "E742", {"start": v(-462.5, -565.4) * mm, "mid": v(-459.36, -568.67) * mm, "end": v(-455.98, -565.65) * mm});
            skLineSegment(sketch, "E743", {"start": v(-455.98, -565.65) * mm, "end": v(-408.52, -565.65) * mm});
            skArc(sketch, "E744", {"start": v(-408.52, -565.65) * mm, "mid": v(-405.14, -568.66) * mm, "end": v(-402, -565.4) * mm});
            skLineSegment(sketch, "E745", {"start": v(-402, -565.4) * mm, "end": v(-402, -547.4) * mm});
            skLineSegment(sketch, "E746", {"start": v(341.93, -930.37) * mm, "end": v(332.93, -945.96) * mm});
            skLineSegment(sketch, "E747", {"start": v(332.93, -945.96) * mm, "end": v(367.57, -965.96) * mm});
            skLineSegment(sketch, "E748", {"start": v(367.57, -965.96) * mm, "end": v(376.57, -950.37) * mm});
            skLineSegment(sketch, "E749", {"start": v(376.57, -950.37) * mm, "end": v(341.93, -930.37) * mm});
            skLineSegment(sketch, "E750", {"start": v(457.93, -729.45) * mm, "end": v(448.93, -745.04) * mm});
            skLineSegment(sketch, "E751", {"start": v(448.93, -745.04) * mm, "end": v(483.57, -765.04) * mm});
            skLineSegment(sketch, "E752", {"start": v(483.57, -765.04) * mm, "end": v(492.57, -749.45) * mm});
            skLineSegment(sketch, "E753", {"start": v(492.57, -749.45) * mm, "end": v(457.93, -729.45) * mm});
            skLineSegment(sketch, "E754", {"start": v(-8.58, 647.39) * mm, "end": v(9.42, 647.39) * mm});
            skLineSegment(sketch, "E755", {"start": v(9.42, 647.39) * mm, "end": v(9.42, 687.39) * mm});
            skLineSegment(sketch, "E756", {"start": v(9.42, 687.39) * mm, "end": v(-8.58, 687.39) * mm});
            skLineSegment(sketch, "E757", {"start": v(-8.58, 687.39) * mm, "end": v(-8.58, 647.39) * mm});
            skLineSegment(sketch, "E758", {"start": v(-222.58, 647.39) * mm, "end": v(-222.58, 687.39) * mm});
            skLineSegment(sketch, "E759", {"start": v(-222.58, 687.39) * mm, "end": v(-240.58, 687.39) * mm});
            skLineSegment(sketch, "E760", {"start": v(-240.58, 687.39) * mm, "end": v(-240.58, 647.39) * mm});
            skLineSegment(sketch, "E761", {"start": v(-240.58, 647.39) * mm, "end": v(-222.58, 647.39) * mm});
            skLineSegment(sketch, "E762", {"start": v(82.12, -780.37) * mm, "end": v(73.12, -795.96) * mm});
            skLineSegment(sketch, "E763", {"start": v(73.12, -795.96) * mm, "end": v(107.76, -815.96) * mm});
            skLineSegment(sketch, "E764", {"start": v(107.76, -815.96) * mm, "end": v(116.76, -800.37) * mm});
            skLineSegment(sketch, "E765", {"start": v(116.76, -800.37) * mm, "end": v(82.12, -780.37) * mm});
            skLineSegment(sketch, "E766", {"start": v(198.12, -579.45) * mm, "end": v(189.12, -595.04) * mm});
            skLineSegment(sketch, "E767", {"start": v(189.12, -595.04) * mm, "end": v(223.76, -615.04) * mm});
            skLineSegment(sketch, "E768", {"start": v(223.76, -615.04) * mm, "end": v(232.76, -599.45) * mm});
            skLineSegment(sketch, "E769", {"start": v(232.76, -599.45) * mm, "end": v(198.12, -579.45) * mm});
            skLineSegment(sketch, "E770", {"start": v(-177.69, -630.37) * mm, "end": v(-186.69, -645.96) * mm});
            skLineSegment(sketch, "E771", {"start": v(-186.69, -645.96) * mm, "end": v(-152.05, -665.96) * mm});
            skLineSegment(sketch, "E772", {"start": v(-152.05, -665.96) * mm, "end": v(-143.05, -650.37) * mm});
            skLineSegment(sketch, "E773", {"start": v(-143.05, -650.37) * mm, "end": v(-177.69, -630.37) * mm});
            skLineSegment(sketch, "E774", {"start": v(-8.58, 347.39) * mm, "end": v(9.42, 347.39) * mm});
            skLineSegment(sketch, "E775", {"start": v(9.42, 347.39) * mm, "end": v(9.42, 387.39) * mm});
            skLineSegment(sketch, "E776", {"start": v(9.42, 387.39) * mm, "end": v(-8.58, 387.39) * mm});
            skLineSegment(sketch, "E777", {"start": v(-8.58, 387.39) * mm, "end": v(-8.58, 347.39) * mm});
            skLineSegment(sketch, "E778", {"start": v(-222.58, 347.39) * mm, "end": v(-222.58, 387.39) * mm});
            skLineSegment(sketch, "E779", {"start": v(-222.58, 387.39) * mm, "end": v(-240.58, 387.39) * mm});
            skLineSegment(sketch, "E780", {"start": v(-240.58, 387.39) * mm, "end": v(-240.58, 347.39) * mm});
            skLineSegment(sketch, "E781", {"start": v(-240.58, 347.39) * mm, "end": v(-222.58, 347.39) * mm});
            skLineSegment(sketch, "E782", {"start": v(-222.58, -512.61) * mm, "end": v(-240.58, -512.61) * mm});
            skLineSegment(sketch, "E783", {"start": v(-240.58, -512.61) * mm, "end": v(-240.58, -552.61) * mm});
            skLineSegment(sketch, "E784", {"start": v(-240.58, -552.61) * mm, "end": v(-222.58, -552.61) * mm});
            skLineSegment(sketch, "E785", {"start": v(-222.58, -552.61) * mm, "end": v(-222.58, -512.61) * mm});
            skLineSegment(sketch, "E786", {"start": v(-8.58, 47.39) * mm, "end": v(9.42, 47.39) * mm});
            skLineSegment(sketch, "E787", {"start": v(9.42, 47.39) * mm, "end": v(9.42, 87.39) * mm});
            skLineSegment(sketch, "E788", {"start": v(9.42, 87.39) * mm, "end": v(-8.58, 87.39) * mm});
            skLineSegment(sketch, "E789", {"start": v(-8.58, 87.39) * mm, "end": v(-8.58, 47.39) * mm});
            skLineSegment(sketch, "E790", {"start": v(-222.58, 47.39) * mm, "end": v(-222.58, 87.39) * mm});
            skLineSegment(sketch, "E791", {"start": v(-222.58, 87.39) * mm, "end": v(-240.58, 87.39) * mm});
            skLineSegment(sketch, "E792", {"start": v(-240.58, 87.39) * mm, "end": v(-240.58, 47.39) * mm});
            skLineSegment(sketch, "E793", {"start": v(-240.58, 47.39) * mm, "end": v(-222.58, 47.39) * mm});
            skLineSegment(sketch, "E794", {"start": v(-8.58, -212.61) * mm, "end": v(-8.58, -252.61) * mm});
            skLineSegment(sketch, "E795", {"start": v(-8.58, -252.61) * mm, "end": v(9.42, -252.61) * mm});
            skLineSegment(sketch, "E796", {"start": v(9.42, -252.61) * mm, "end": v(9.42, -212.61) * mm});
            skLineSegment(sketch, "E797", {"start": v(9.42, -212.61) * mm, "end": v(-8.58, -212.61) * mm});
            skLineSegment(sketch, "E798", {"start": v(-222.58, -212.61) * mm, "end": v(-240.58, -212.61) * mm});
            skLineSegment(sketch, "E799", {"start": v(-240.58, -212.61) * mm, "end": v(-240.58, -252.61) * mm});
            skLineSegment(sketch, "E800", {"start": v(-240.58, -252.61) * mm, "end": v(-222.58, -252.61) * mm});
            skLineSegment(sketch, "E801", {"start": v(-222.58, -252.61) * mm, "end": v(-222.58, -212.61) * mm});
            skArc(sketch, "E802", {"start": v(-85.33, -373.6) * mm, "mid": v(-88.47, -370.34) * mm, "end": v(-91.85, -373.36) * mm});
            skLineSegment(sketch, "E803", {"start": v(-91.85, -373.36) * mm, "end": v(-139.32, -373.36) * mm});
            skArc(sketch, "E804", {"start": v(-139.32, -373.36) * mm, "mid": v(-142.7, -370.35) * mm, "end": v(-145.83, -373.6) * mm});
            skLineSegment(sketch, "E805", {"start": v(-145.83, -373.6) * mm, "end": v(-145.83, -391.6) * mm});
            skArc(sketch, "E806", {"start": v(-145.83, -391.6) * mm, "mid": v(-142.7, -394.87) * mm, "end": v(-139.32, -391.86) * mm});
            skLineSegment(sketch, "E807", {"start": v(-139.32, -391.86) * mm, "end": v(-91.85, -391.86) * mm});
            skArc(sketch, "E808", {"start": v(-91.85, -391.86) * mm, "mid": v(-88.47, -394.87) * mm, "end": v(-85.33, -391.6) * mm});
            skLineSegment(sketch, "E809", {"start": v(-85.33, -391.6) * mm, "end": v(-85.33, -373.6) * mm});
            skArc(sketch, "E810", {"start": v(30.37, -592) * mm, "mid": v(25.97, -593.1) * mm, "end": v(26.9, -597.53) * mm});
            skLineSegment(sketch, "E811", {"start": v(26.9, -597.53) * mm, "end": v(3.16, -638.63) * mm});
            skArc(sketch, "E812", {"start": v(3.16, -638.63) * mm, "mid": v(-1.14, -640.06) * mm, "end": v(0.12, -644.4) * mm});
            skLineSegment(sketch, "E813", {"start": v(0.12, -644.4) * mm, "end": v(15.7, -653.4) * mm});
            skArc(sketch, "E814", {"start": v(15.7, -653.4) * mm, "mid": v(20.1, -652.32) * mm, "end": v(19.18, -647.88) * mm});
            skLineSegment(sketch, "E815", {"start": v(19.18, -647.88) * mm, "end": v(42.92, -606.78) * mm});
            skArc(sketch, "E816", {"start": v(42.92, -606.78) * mm, "mid": v(47.21, -605.36) * mm, "end": v(45.96, -601) * mm});
            skLineSegment(sketch, "E817", {"start": v(45.96, -601) * mm, "end": v(30.37, -592) * mm});
            skLineSegment(sketch, "E818", {"start": v(-65.34, -1014.85) * mm, "end": v(-99.97, -994.85) * mm});
            skLineSegment(sketch, "E819", {"start": v(-99.97, -994.85) * mm, "end": v(-87.54, -973.32) * mm});
            skLineSegment(sketch, "E820", {"start": v(-83.42, -1004.4) * mm, "end": v(-71.89, -984.43) * mm});
            skLineSegment(sketch, "E821", {"start": v(-22.2, -940.1) * mm, "end": v(-45.59, -900.66) * mm});
            skLineSegment(sketch, "E822", {"start": v(-5.64, -889.26) * mm, "end": v(-5.17, -889.56) * mm});
            skLineSegment(sketch, "E823", {"start": v(-5.17, -889.56) * mm, "end": v(-4.73, -889.9) * mm});
            skLineSegment(sketch, "E824", {"start": v(-4.73, -889.9) * mm, "end": v(-4.3, -890.24) * mm});
            skLineSegment(sketch, "E825", {"start": v(-4.3, -890.24) * mm, "end": v(-3.88, -890.6) * mm});
            skLineSegment(sketch, "E826", {"start": v(-3.88, -890.6) * mm, "end": v(-3.48, -890.98) * mm});
            skLineSegment(sketch, "E827", {"start": v(-3.48, -890.98) * mm, "end": v(-3.1, -891.38) * mm});
            skLineSegment(sketch, "E828", {"start": v(-3.1, -891.38) * mm, "end": v(-2.74, -891.79) * mm});
            skLineSegment(sketch, "E829", {"start": v(-2.74, -891.79) * mm, "end": v(-2.4, -892.21) * mm});
            skLineSegment(sketch, "E830", {"start": v(-2.4, -892.21) * mm, "end": v(-2.06, -892.66) * mm});
            skLineSegment(sketch, "E831", {"start": v(-2.06, -892.66) * mm, "end": v(-1.76, -893.11) * mm});
            skLineSegment(sketch, "E832", {"start": v(-1.76, -893.11) * mm, "end": v(-1.47, -893.58) * mm});
            skLineSegment(sketch, "E833", {"start": v(-1.47, -893.58) * mm, "end": v(-1.2, -894.06) * mm});
            skLineSegment(sketch, "E834", {"start": v(-1.2, -894.06) * mm, "end": v(-0.95, -894.56) * mm});
            skLineSegment(sketch, "E835", {"start": v(-0.95, -894.56) * mm, "end": v(-0.73, -895.06) * mm});
            skLineSegment(sketch, "E836", {"start": v(-0.73, -895.06) * mm, "end": v(-0.52, -895.57) * mm});
            skLineSegment(sketch, "E837", {"start": v(-0.52, -895.57) * mm, "end": v(-0.34, -896.1) * mm});
            skLineSegment(sketch, "E838", {"start": v(-0.34, -896.1) * mm, "end": v(-0.2, -896.66) * mm});
            skLineSegment(sketch, "E839", {"start": v(-0.2, -896.66) * mm, "end": v(-0.08, -897.23) * mm});
            skLineSegment(sketch, "E840", {"start": v(-0.08, -897.23) * mm, "end": v(0, -897.8) * mm});
            skLineSegment(sketch, "E841", {"start": v(0, -897.8) * mm, "end": v(0.06, -898.37) * mm});
            skLineSegment(sketch, "E842", {"start": v(0.06, -898.37) * mm, "end": v(0.08, -898.94) * mm});
            skLineSegment(sketch, "E843", {"start": v(0.08, -898.94) * mm, "end": v(0.08, -899.5) * mm});
            skLineSegment(sketch, "E844", {"start": v(0.08, -899.5) * mm, "end": v(0.05, -900.08) * mm});
            skLineSegment(sketch, "E845", {"start": v(0.05, -900.08) * mm, "end": v(-0.01, -900.65) * mm});
            skLineSegment(sketch, "E846", {"start": v(-0.01, -900.65) * mm, "end": v(-0.1, -901.2) * mm});
            skLineSegment(sketch, "E847", {"start": v(-0.1, -901.2) * mm, "end": v(-0.22, -901.77) * mm});
            skLineSegment(sketch, "E848", {"start": v(-0.22, -901.77) * mm, "end": v(-0.36, -902.32) * mm});
            skLineSegment(sketch, "E849", {"start": v(-0.36, -902.32) * mm, "end": v(-0.53, -902.87) * mm});
            skLineSegment(sketch, "E850", {"start": v(-0.53, -902.87) * mm, "end": v(-0.73, -903.4) * mm});
            skLineSegment(sketch, "E851", {"start": v(-0.73, -903.4) * mm, "end": v(-0.96, -903.93) * mm});
            skLineSegment(sketch, "E852", {"start": v(-0.96, -903.93) * mm, "end": v(-1.21, -904.45) * mm});
            skLineSegment(sketch, "E853", {"start": v(-1.21, -904.45) * mm, "end": v(-1.5, -904.96) * mm});
            skLineSegment(sketch, "E854", {"start": v(-1.5, -904.96) * mm, "end": v(-1.74, -905.42) * mm});
            skLineSegment(sketch, "E855", {"start": v(-1.74, -905.42) * mm, "end": v(-2.01, -905.86) * mm});
            skLineSegment(sketch, "E856", {"start": v(-2.01, -905.86) * mm, "end": v(-2.3, -906.3) * mm});
            skLineSegment(sketch, "E857", {"start": v(-2.3, -906.3) * mm, "end": v(-2.62, -906.7) * mm});
            skLineSegment(sketch, "E858", {"start": v(-2.62, -906.7) * mm, "end": v(-2.95, -907.1) * mm});
            skLineSegment(sketch, "E859", {"start": v(-2.95, -907.1) * mm, "end": v(-3.3, -907.48) * mm});
            skLineSegment(sketch, "E860", {"start": v(-3.3, -907.48) * mm, "end": v(-3.67, -907.84) * mm});
            skLineSegment(sketch, "E861", {"start": v(-3.67, -907.84) * mm, "end": v(-4.06, -908.19) * mm});
            skLineSegment(sketch, "E862", {"start": v(-4.06, -908.19) * mm, "end": v(-4.46, -908.5) * mm});
            skLineSegment(sketch, "E863", {"start": v(-4.46, -908.5) * mm, "end": v(-4.88, -908.8) * mm});
            skLineSegment(sketch, "E864", {"start": v(-4.88, -908.8) * mm, "end": v(-5.32, -909.09) * mm});
            skLineSegment(sketch, "E865", {"start": v(-5.32, -909.09) * mm, "end": v(-5.76, -909.35) * mm});
            skLineSegment(sketch, "E866", {"start": v(-5.76, -909.35) * mm, "end": v(-6.23, -909.58) * mm});
            skLineSegment(sketch, "E867", {"start": v(-6.23, -909.58) * mm, "end": v(-6.7, -909.8) * mm});
            skLineSegment(sketch, "E868", {"start": v(-6.7, -909.8) * mm, "end": v(-7.19, -909.98) * mm});
            skLineSegment(sketch, "E869", {"start": v(-7.19, -909.98) * mm, "end": v(-7.69, -910.15) * mm});
            skLineSegment(sketch, "E870", {"start": v(-7.69, -910.15) * mm, "end": v(-7.98, -910.23) * mm});
            skLineSegment(sketch, "E871", {"start": v(-7.98, -910.23) * mm, "end": v(-8.28, -910.3) * mm});
            skLineSegment(sketch, "E872", {"start": v(-8.28, -910.3) * mm, "end": v(-8.58, -910.36) * mm});
            skLineSegment(sketch, "E873", {"start": v(-8.58, -910.36) * mm, "end": v(-8.89, -910.4) * mm});
            skLineSegment(sketch, "E874", {"start": v(-8.89, -910.4) * mm, "end": v(-9.2, -910.42) * mm});
            skLineSegment(sketch, "E875", {"start": v(-9.2, -910.42) * mm, "end": v(-9.5, -910.42) * mm});
            skLineSegment(sketch, "E876", {"start": v(-9.5, -910.42) * mm, "end": v(-9.8, -910.41) * mm});
            skLineSegment(sketch, "E877", {"start": v(-9.8, -910.41) * mm, "end": v(-10.1, -910.39) * mm});
            skLineSegment(sketch, "E878", {"start": v(-10.1, -910.39) * mm, "end": v(-10.4, -910.35) * mm});
            skLineSegment(sketch, "E879", {"start": v(-10.4, -910.35) * mm, "end": v(-10.7, -910.3) * mm});
            skLineSegment(sketch, "E880", {"start": v(-10.7, -910.3) * mm, "end": v(-11, -910.22) * mm});
            skLineSegment(sketch, "E881", {"start": v(-11, -910.22) * mm, "end": v(-11.3, -910.13) * mm});
            skLineSegment(sketch, "E882", {"start": v(-11.3, -910.13) * mm, "end": v(-11.58, -910.03) * mm});
            skLineSegment(sketch, "E883", {"start": v(-11.58, -910.03) * mm, "end": v(-11.87, -909.92) * mm});
            skLineSegment(sketch, "E884", {"start": v(-11.87, -909.92) * mm, "end": v(-12.15, -909.79) * mm});
            skLineSegment(sketch, "E885", {"start": v(-12.15, -909.79) * mm, "end": v(-12.42, -909.64) * mm});
            skLineSegment(sketch, "E886", {"start": v(-12.42, -909.64) * mm, "end": v(-12.77, -909.45) * mm});
            skLineSegment(sketch, "E887", {"start": v(-12.77, -909.45) * mm, "end": v(-13.1, -909.25) * mm});
            skLineSegment(sketch, "E888", {"start": v(-13.1, -909.25) * mm, "end": v(-13.44, -909.03) * mm});
            skLineSegment(sketch, "E889", {"start": v(-13.44, -909.03) * mm, "end": v(-13.75, -908.8) * mm});
            skLineSegment(sketch, "E890", {"start": v(-13.75, -908.8) * mm, "end": v(-14.05, -908.54) * mm});
            skLineSegment(sketch, "E891", {"start": v(-14.05, -908.54) * mm, "end": v(-14.34, -908.27) * mm});
            skLineSegment(sketch, "E892", {"start": v(-14.34, -908.27) * mm, "end": v(-14.61, -908) * mm});
            skLineSegment(sketch, "E893", {"start": v(-14.61, -908) * mm, "end": v(-14.87, -907.7) * mm});
            skLineSegment(sketch, "E894", {"start": v(-14.87, -907.7) * mm, "end": v(-15.11, -907.4) * mm});
            skLineSegment(sketch, "E895", {"start": v(-15.11, -907.4) * mm, "end": v(-15.34, -907.08) * mm});
            skLineSegment(sketch, "E896", {"start": v(-15.34, -907.08) * mm, "end": v(-15.55, -906.75) * mm});
            skLineSegment(sketch, "E897", {"start": v(-15.55, -906.75) * mm, "end": v(-15.75, -906.4) * mm});
            skLineSegment(sketch, "E898", {"start": v(-15.75, -906.4) * mm, "end": v(-15.92, -906.05) * mm});
            skLineSegment(sketch, "E899", {"start": v(-15.92, -906.05) * mm, "end": v(-16.08, -905.7) * mm});
            skLineSegment(sketch, "E900", {"start": v(-16.08, -905.7) * mm, "end": v(-16.22, -905.32) * mm});
            skLineSegment(sketch, "E901", {"start": v(-16.22, -905.32) * mm, "end": v(-16.35, -904.95) * mm});
            skLineSegment(sketch, "E902", {"start": v(-16.35, -904.95) * mm, "end": v(-16.4, -904.41) * mm});
            skLineSegment(sketch, "E903", {"start": v(-16.4, -904.41) * mm, "end": v(-16.44, -903.88) * mm});
            skLineSegment(sketch, "E904", {"start": v(-16.44, -903.88) * mm, "end": v(-16.46, -903.34) * mm});
            skLineSegment(sketch, "E905", {"start": v(-16.46, -903.34) * mm, "end": v(-16.46, -902.8) * mm});
            skLineSegment(sketch, "E906", {"start": v(-16.46, -902.8) * mm, "end": v(-16.43, -902.27) * mm});
            skLineSegment(sketch, "E907", {"start": v(-16.43, -902.27) * mm, "end": v(-16.4, -901.74) * mm});
            skLineSegment(sketch, "E908", {"start": v(-16.4, -901.74) * mm, "end": v(-16.33, -901.2) * mm});
            skLineSegment(sketch, "E909", {"start": v(-16.33, -901.2) * mm, "end": v(-16.25, -900.68) * mm});
            skLineSegment(sketch, "E910", {"start": v(-16.25, -900.68) * mm, "end": v(-16.15, -900.16) * mm});
            skLineSegment(sketch, "E911", {"start": v(-16.15, -900.16) * mm, "end": v(-16.04, -899.63) * mm});
            skLineSegment(sketch, "E912", {"start": v(-16.04, -899.63) * mm, "end": v(-15.9, -899.12) * mm});
            skLineSegment(sketch, "E913", {"start": v(-15.9, -899.12) * mm, "end": v(-15.74, -898.6) * mm});
            skLineSegment(sketch, "E914", {"start": v(-15.74, -898.6) * mm, "end": v(-15.57, -898.1) * mm});
            skLineSegment(sketch, "E915", {"start": v(-15.57, -898.1) * mm, "end": v(-15.38, -897.6) * mm});
            skLineSegment(sketch, "E916", {"start": v(-15.38, -897.6) * mm, "end": v(-15.17, -897.1) * mm});
            skLineSegment(sketch, "E917", {"start": v(-15.17, -897.1) * mm, "end": v(-14.94, -896.62) * mm});
            skLineSegment(sketch, "E918", {"start": v(-14.94, -896.62) * mm, "end": v(-12.4, -889.38) * mm});
            skLineSegment(sketch, "E919", {"start": v(-12.4, -889.38) * mm, "end": v(-12.35, -889.17) * mm});
            skLineSegment(sketch, "E920", {"start": v(-12.35, -889.17) * mm, "end": v(-12.3, -888.96) * mm});
            skLineSegment(sketch, "E921", {"start": v(-12.3, -888.96) * mm, "end": v(-12.27, -888.75) * mm});
            skLineSegment(sketch, "E922", {"start": v(-12.27, -888.75) * mm, "end": v(-12.25, -888.54) * mm});
            skLineSegment(sketch, "E923", {"start": v(-12.25, -888.54) * mm, "end": v(-12.23, -888.33) * mm});
            skLineSegment(sketch, "E924", {"start": v(-12.23, -888.33) * mm, "end": v(-12.23, -888.13) * mm});
            skLineSegment(sketch, "E925", {"start": v(-12.23, -888.13) * mm, "end": v(-12.23, -887.92) * mm});
            skLineSegment(sketch, "E926", {"start": v(-12.23, -887.92) * mm, "end": v(-12.25, -887.71) * mm});
            skLineSegment(sketch, "E927", {"start": v(-12.25, -887.71) * mm, "end": v(-12.27, -887.5) * mm});
            skLineSegment(sketch, "E928", {"start": v(-12.27, -887.5) * mm, "end": v(-12.3, -887.3) * mm});
            skLineSegment(sketch, "E929", {"start": v(-12.3, -887.3) * mm, "end": v(-12.34, -887.1) * mm});
            skLineSegment(sketch, "E930", {"start": v(-12.34, -887.1) * mm, "end": v(-12.4, -886.9) * mm});
            skLineSegment(sketch, "E931", {"start": v(-12.4, -886.9) * mm, "end": v(-12.45, -886.71) * mm});
            skLineSegment(sketch, "E932", {"start": v(-12.45, -886.71) * mm, "end": v(-12.51, -886.52) * mm});
            skLineSegment(sketch, "E933", {"start": v(-12.51, -886.52) * mm, "end": v(-12.59, -886.33) * mm});
            skLineSegment(sketch, "E934", {"start": v(-12.59, -886.33) * mm, "end": v(-12.67, -886.14) * mm});
            skLineSegment(sketch, "E935", {"start": v(-12.67, -886.14) * mm, "end": v(-12.76, -885.96) * mm});
            skLineSegment(sketch, "E936", {"start": v(-12.76, -885.96) * mm, "end": v(-12.86, -885.78) * mm});
            skLineSegment(sketch, "E937", {"start": v(-12.86, -885.78) * mm, "end": v(-12.97, -885.6) * mm});
            skLineSegment(sketch, "E938", {"start": v(-12.97, -885.6) * mm, "end": v(-13.08, -885.44) * mm});
            skLineSegment(sketch, "E939", {"start": v(-13.08, -885.44) * mm, "end": v(-13.2, -885.27) * mm});
            skLineSegment(sketch, "E940", {"start": v(-13.2, -885.27) * mm, "end": v(-13.33, -885.11) * mm});
            skLineSegment(sketch, "E941", {"start": v(-13.33, -885.11) * mm, "end": v(-13.46, -884.96) * mm});
            skLineSegment(sketch, "E942", {"start": v(-13.46, -884.96) * mm, "end": v(-13.6, -884.81) * mm});
            skLineSegment(sketch, "E943", {"start": v(-13.6, -884.81) * mm, "end": v(-13.75, -884.67) * mm});
            skLineSegment(sketch, "E944", {"start": v(-13.75, -884.67) * mm, "end": v(-13.91, -884.53) * mm});
            skLineSegment(sketch, "E945", {"start": v(-13.91, -884.53) * mm, "end": v(-14.07, -884.4) * mm});
            skLineSegment(sketch, "E946", {"start": v(-14.07, -884.4) * mm, "end": v(-14.24, -884.28) * mm});
            skLineSegment(sketch, "E947", {"start": v(-14.24, -884.28) * mm, "end": v(-14.42, -884.16) * mm});
            skLineSegment(sketch, "E948", {"start": v(-14.42, -884.16) * mm, "end": v(-14.6, -884.06) * mm});
            skLineSegment(sketch, "E949", {"start": v(-14.6, -884.06) * mm, "end": v(-14.79, -883.95) * mm});
            skLineSegment(sketch, "E950", {"start": v(-14.79, -883.95) * mm, "end": v(-14.98, -883.86) * mm});
            skLineSegment(sketch, "E951", {"start": v(-25.44, -900.62) * mm, "end": v(-25.7, -900.4) * mm});
            skLineSegment(sketch, "E952", {"start": v(-25.7, -900.4) * mm, "end": v(-25.95, -900.16) * mm});
            skLineSegment(sketch, "E953", {"start": v(-25.95, -900.16) * mm, "end": v(-26.2, -899.93) * mm});
            skLineSegment(sketch, "E954", {"start": v(-26.2, -899.93) * mm, "end": v(-26.42, -899.68) * mm});
            skLineSegment(sketch, "E955", {"start": v(-26.42, -899.68) * mm, "end": v(-26.65, -899.42) * mm});
            skLineSegment(sketch, "E956", {"start": v(-26.65, -899.42) * mm, "end": v(-26.86, -899.16) * mm});
            skLineSegment(sketch, "E957", {"start": v(-26.86, -899.16) * mm, "end": v(-27.06, -898.89) * mm});
            skLineSegment(sketch, "E958", {"start": v(-27.06, -898.89) * mm, "end": v(-27.26, -898.61) * mm});
            skLineSegment(sketch, "E959", {"start": v(-27.26, -898.61) * mm, "end": v(-27.44, -898.33) * mm});
            skLineSegment(sketch, "E960", {"start": v(-27.44, -898.33) * mm, "end": v(-27.61, -898.03) * mm});
            skLineSegment(sketch, "E961", {"start": v(-27.61, -898.03) * mm, "end": v(-27.77, -897.74) * mm});
            skLineSegment(sketch, "E962", {"start": v(-27.77, -897.74) * mm, "end": v(-27.93, -897.43) * mm});
            skLineSegment(sketch, "E963", {"start": v(-27.93, -897.43) * mm, "end": v(-28.07, -897.12) * mm});
            skLineSegment(sketch, "E964", {"start": v(-28.07, -897.12) * mm, "end": v(-28.2, -896.8) * mm});
            skLineSegment(sketch, "E965", {"start": v(-28.2, -896.8) * mm, "end": v(-28.31, -896.5) * mm});
            skLineSegment(sketch, "E966", {"start": v(-28.31, -896.5) * mm, "end": v(-28.42, -896.17) * mm});
            skLineSegment(sketch, "E967", {"start": v(-28.42, -896.17) * mm, "end": v(-28.53, -895.62) * mm});
            skLineSegment(sketch, "E968", {"start": v(-28.53, -895.62) * mm, "end": v(-28.61, -895.07) * mm});
            skLineSegment(sketch, "E969", {"start": v(-28.61, -895.07) * mm, "end": v(-28.67, -894.53) * mm});
            skLineSegment(sketch, "E970", {"start": v(-28.67, -894.53) * mm, "end": v(-28.7, -893.98) * mm});
            skLineSegment(sketch, "E971", {"start": v(-28.7, -893.98) * mm, "end": v(-28.7, -893.43) * mm});
            skLineSegment(sketch, "E972", {"start": v(-28.7, -893.43) * mm, "end": v(-28.67, -892.88) * mm});
            skLineSegment(sketch, "E973", {"start": v(-28.67, -892.88) * mm, "end": v(-28.62, -892.33) * mm});
            skLineSegment(sketch, "E974", {"start": v(-28.62, -892.33) * mm, "end": v(-28.54, -891.79) * mm});
            skLineSegment(sketch, "E975", {"start": v(-28.54, -891.79) * mm, "end": v(-28.43, -891.25) * mm});
            skLineSegment(sketch, "E976", {"start": v(-28.43, -891.25) * mm, "end": v(-28.3, -890.72) * mm});
            skLineSegment(sketch, "E977", {"start": v(-28.3, -890.72) * mm, "end": v(-28.14, -890.2) * mm});
            skLineSegment(sketch, "E978", {"start": v(-28.14, -890.2) * mm, "end": v(-27.96, -889.68) * mm});
            skLineSegment(sketch, "E979", {"start": v(-27.96, -889.68) * mm, "end": v(-27.75, -889.17) * mm});
            skLineSegment(sketch, "E980", {"start": v(-27.75, -889.17) * mm, "end": v(-27.51, -888.67) * mm});
            skLineSegment(sketch, "E981", {"start": v(-27.51, -888.67) * mm, "end": v(-27.25, -888.18) * mm});
            skLineSegment(sketch, "E982", {"start": v(-27.25, -888.18) * mm, "end": v(-26.96, -887.7) * mm});
            skLineSegment(sketch, "E983", {"start": v(-26.96, -887.7) * mm, "end": v(-26.72, -887.25) * mm});
            skLineSegment(sketch, "E984", {"start": v(-26.72, -887.25) * mm, "end": v(-26.46, -886.8) * mm});
            skLineSegment(sketch, "E985", {"start": v(-26.46, -886.8) * mm, "end": v(-26.18, -886.38) * mm});
            skLineSegment(sketch, "E986", {"start": v(-26.18, -886.38) * mm, "end": v(-25.88, -885.96) * mm});
            skLineSegment(sketch, "E987", {"start": v(-25.88, -885.96) * mm, "end": v(-25.56, -885.57) * mm});
            skLineSegment(sketch, "E988", {"start": v(-25.56, -885.57) * mm, "end": v(-25.22, -885.18) * mm});
            skLineSegment(sketch, "E989", {"start": v(-25.22, -885.18) * mm, "end": v(-24.86, -884.82) * mm});
            skLineSegment(sketch, "E990", {"start": v(-24.86, -884.82) * mm, "end": v(-24.49, -884.48) * mm});
            skLineSegment(sketch, "E991", {"start": v(-24.49, -884.48) * mm, "end": v(-24.1, -884.15) * mm});
            skLineSegment(sketch, "E992", {"start": v(-24.1, -884.15) * mm, "end": v(-23.69, -883.84) * mm});
            skLineSegment(sketch, "E993", {"start": v(-23.69, -883.84) * mm, "end": v(-23.27, -883.55) * mm});
            skLineSegment(sketch, "E994", {"start": v(-23.27, -883.55) * mm, "end": v(-22.83, -883.28) * mm});
            skLineSegment(sketch, "E995", {"start": v(-22.83, -883.28) * mm, "end": v(-22.39, -883.03) * mm});
            skLineSegment(sketch, "E996", {"start": v(-22.39, -883.03) * mm, "end": v(-21.93, -882.8) * mm});
            skLineSegment(sketch, "E997", {"start": v(-21.93, -882.8) * mm, "end": v(-21.45, -882.6) * mm});
            skLineSegment(sketch, "E998", {"start": v(-21.45, -882.6) * mm, "end": v(-20.97, -882.42) * mm});
            skLineSegment(sketch, "E999", {"start": v(-20.97, -882.42) * mm, "end": v(-20.58, -882.39) * mm});
            skLineSegment(sketch, "E1000", {"start": v(-20.58, -882.39) * mm, "end": v(-20.18, -882.37) * mm});
            skLineSegment(sketch, "E1001", {"start": v(-20.18, -882.37) * mm, "end": v(-19.79, -882.37) * mm});
            skLineSegment(sketch, "E1002", {"start": v(-19.79, -882.37) * mm, "end": v(-19.4, -882.38) * mm});
            skLineSegment(sketch, "E1003", {"start": v(-19.4, -882.38) * mm, "end": v(-19, -882.41) * mm});
            skLineSegment(sketch, "E1004", {"start": v(-19, -882.41) * mm, "end": v(-18.62, -882.46) * mm});
            skLineSegment(sketch, "E1005", {"start": v(-18.62, -882.46) * mm, "end": v(-18.23, -882.53) * mm});
            skLineSegment(sketch, "E1006", {"start": v(-18.23, -882.53) * mm, "end": v(-17.85, -882.61) * mm});
            skLineSegment(sketch, "E1007", {"start": v(-17.85, -882.61) * mm, "end": v(-17.47, -882.71) * mm});
            skLineSegment(sketch, "E1008", {"start": v(-17.47, -882.71) * mm, "end": v(-17.1, -882.83) * mm});
            skLineSegment(sketch, "E1009", {"start": v(-17.1, -882.83) * mm, "end": v(-16.73, -882.96) * mm});
            skLineSegment(sketch, "E1010", {"start": v(-16.73, -882.96) * mm, "end": v(-16.36, -883.1) * mm});
            skLineSegment(sketch, "E1011", {"start": v(-16.36, -883.1) * mm, "end": v(-16, -883.27) * mm});
            skLineSegment(sketch, "E1012", {"start": v(-16, -883.27) * mm, "end": v(-15.66, -883.45) * mm});
            skLineSegment(sketch, "E1013", {"start": v(-15.66, -883.45) * mm, "end": v(-15.32, -883.65) * mm});
            skLineSegment(sketch, "E1014", {"start": v(-15.32, -883.65) * mm, "end": v(-14.98, -883.86) * mm});
            skLineSegment(sketch, "E1015", {"start": v(-14.98, -883.86) * mm, "end": v(1.13, -893.16) * mm});
            skLineSegment(sketch, "E1016", {"start": v(1.13, -893.16) * mm, "end": v(1.27, -893.25) * mm});
            skLineSegment(sketch, "E1017", {"start": v(1.27, -893.25) * mm, "end": v(1.42, -893.33) * mm});
            skLineSegment(sketch, "E1018", {"start": v(1.42, -893.33) * mm, "end": v(1.57, -893.4) * mm});
            skLineSegment(sketch, "E1019", {"start": v(1.57, -893.4) * mm, "end": v(1.72, -893.46) * mm});
            skLineSegment(sketch, "E1020", {"start": v(1.72, -893.46) * mm, "end": v(1.88, -893.5) * mm});
            skLineSegment(sketch, "E1021", {"start": v(1.88, -893.5) * mm, "end": v(2.03, -893.55) * mm});
            skLineSegment(sketch, "E1022", {"start": v(2.03, -893.55) * mm, "end": v(2.2, -893.58) * mm});
            skLineSegment(sketch, "E1023", {"start": v(2.2, -893.58) * mm, "end": v(2.36, -893.6) * mm});
            skLineSegment(sketch, "E1024", {"start": v(2.36, -893.6) * mm, "end": v(2.52, -893.62) * mm});
            skLineSegment(sketch, "E1025", {"start": v(2.52, -893.62) * mm, "end": v(2.68, -893.62) * mm});
            skLineSegment(sketch, "E1026", {"start": v(2.68, -893.62) * mm, "end": v(2.84, -893.61) * mm});
            skLineSegment(sketch, "E1027", {"start": v(2.84, -893.61) * mm, "end": v(3, -893.6) * mm});
            skLineSegment(sketch, "E1028", {"start": v(3, -893.6) * mm, "end": v(3.17, -893.57) * mm});
            skLineSegment(sketch, "E1029", {"start": v(3.17, -893.57) * mm, "end": v(3.33, -893.53) * mm});
            skLineSegment(sketch, "E1030", {"start": v(3.33, -893.53) * mm, "end": v(3.49, -893.49) * mm});
            skLineSegment(sketch, "E1031", {"start": v(3.49, -893.49) * mm, "end": v(3.64, -893.43) * mm});
            skLineSegment(sketch, "E1032", {"start": v(3.64, -893.43) * mm, "end": v(3.86, -893.32) * mm});
            skLineSegment(sketch, "E1033", {"start": v(3.86, -893.32) * mm, "end": v(4.08, -893.2) * mm});
            skLineSegment(sketch, "E1034", {"start": v(4.08, -893.2) * mm, "end": v(4.28, -893.06) * mm});
            skLineSegment(sketch, "E1035", {"start": v(4.28, -893.06) * mm, "end": v(4.48, -892.92) * mm});
            skLineSegment(sketch, "E1036", {"start": v(4.48, -892.92) * mm, "end": v(4.68, -892.76) * mm});
            skLineSegment(sketch, "E1037", {"start": v(4.68, -892.76) * mm, "end": v(4.86, -892.6) * mm});
            skLineSegment(sketch, "E1038", {"start": v(4.86, -892.6) * mm, "end": v(5.04, -892.44) * mm});
            skLineSegment(sketch, "E1039", {"start": v(5.04, -892.44) * mm, "end": v(5.22, -892.27) * mm});
            skLineSegment(sketch, "E1040", {"start": v(5.22, -892.27) * mm, "end": v(5.38, -892.09) * mm});
            skLineSegment(sketch, "E1041", {"start": v(5.38, -892.09) * mm, "end": v(5.54, -891.9) * mm});
            skLineSegment(sketch, "E1042", {"start": v(5.54, -891.9) * mm, "end": v(5.69, -891.7) * mm});
            skLineSegment(sketch, "E1043", {"start": v(5.69, -891.7) * mm, "end": v(5.83, -891.5) * mm});
            skLineSegment(sketch, "E1044", {"start": v(5.83, -891.5) * mm, "end": v(5.96, -891.3) * mm});
            skLineSegment(sketch, "E1045", {"start": v(5.96, -891.3) * mm, "end": v(6.08, -891.08) * mm});
            skLineSegment(sketch, "E1046", {"start": v(6.08, -891.08) * mm, "end": v(6.2, -890.86) * mm});
            skLineSegment(sketch, "E1047", {"start": v(6.2, -890.86) * mm, "end": v(6.3, -890.64) * mm});
            skLineSegment(sketch, "E1048", {"start": v(-30.91, -62.96) * mm, "end": v(-30.91, -102.95) * mm});
            skLineSegment(sketch, "E1049", {"start": v(-30.91, -102.95) * mm, "end": v(-55.78, -102.95) * mm});
            skLineSegment(sketch, "E1050", {"start": v(-30.91, -83.84) * mm, "end": v(-53.98, -83.84) * mm});
            skLineSegment(sketch, "E1051", {"start": v(-117.21, -62.97) * mm, "end": v(-139.68, -102.95) * mm});
            skLineSegment(sketch, "E1052", {"start": v(-172.85, -72.13) * mm, "end": v(-172.74, -71.68) * mm});
            skLineSegment(sketch, "E1053", {"start": v(-172.74, -71.68) * mm, "end": v(-172.61, -71.25) * mm});
            skLineSegment(sketch, "E1054", {"start": v(-172.61, -71.25) * mm, "end": v(-172.47, -70.81) * mm});
            skLineSegment(sketch, "E1055", {"start": v(-172.47, -70.81) * mm, "end": v(-172.31, -70.39) * mm});
            skLineSegment(sketch, "E1056", {"start": v(-172.31, -70.39) * mm, "end": v(-172.14, -69.97) * mm});
            skLineSegment(sketch, "E1057", {"start": v(-172.14, -69.97) * mm, "end": v(-171.95, -69.55) * mm});
            skLineSegment(sketch, "E1058", {"start": v(-171.95, -69.55) * mm, "end": v(-171.75, -69.15) * mm});
            skLineSegment(sketch, "E1059", {"start": v(-171.75, -69.15) * mm, "end": v(-171.54, -68.75) * mm});
            skLineSegment(sketch, "E1060", {"start": v(-171.54, -68.75) * mm, "end": v(-171.31, -68.35) * mm});
            skLineSegment(sketch, "E1061", {"start": v(-171.31, -68.35) * mm, "end": v(-171.07, -67.97) * mm});
            skLineSegment(sketch, "E1062", {"start": v(-171.07, -67.97) * mm, "end": v(-170.81, -67.6) * mm});
            skLineSegment(sketch, "E1063", {"start": v(-170.81, -67.6) * mm, "end": v(-170.55, -67.22) * mm});
            skLineSegment(sketch, "E1064", {"start": v(-170.55, -67.22) * mm, "end": v(-170.27, -66.87) * mm});
            skLineSegment(sketch, "E1065", {"start": v(-170.27, -66.87) * mm, "end": v(-169.97, -66.52) * mm});
            skLineSegment(sketch, "E1066", {"start": v(-169.97, -66.52) * mm, "end": v(-169.67, -66.18) * mm});
            skLineSegment(sketch, "E1067", {"start": v(-169.67, -66.18) * mm, "end": v(-169.35, -65.85) * mm});
            skLineSegment(sketch, "E1068", {"start": v(-169.35, -65.85) * mm, "end": v(-168.95, -65.46) * mm});
            skLineSegment(sketch, "E1069", {"start": v(-168.95, -65.46) * mm, "end": v(-168.54, -65.1) * mm});
            skLineSegment(sketch, "E1070", {"start": v(-168.54, -65.1) * mm, "end": v(-168.1, -64.75) * mm});
            skLineSegment(sketch, "E1071", {"start": v(-168.1, -64.75) * mm, "end": v(-167.66, -64.43) * mm});
            skLineSegment(sketch, "E1072", {"start": v(-167.66, -64.43) * mm, "end": v(-167.2, -64.13) * mm});
            skLineSegment(sketch, "E1073", {"start": v(-167.2, -64.13) * mm, "end": v(-166.72, -63.86) * mm});
            skLineSegment(sketch, "E1074", {"start": v(-166.72, -63.86) * mm, "end": v(-166.23, -63.6) * mm});
            skLineSegment(sketch, "E1075", {"start": v(-166.23, -63.6) * mm, "end": v(-165.73, -63.38) * mm});
            skLineSegment(sketch, "E1076", {"start": v(-165.73, -63.38) * mm, "end": v(-165.22, -63.18) * mm});
            skLineSegment(sketch, "E1077", {"start": v(-165.22, -63.18) * mm, "end": v(-164.7, -63) * mm});
            skLineSegment(sketch, "E1078", {"start": v(-164.7, -63) * mm, "end": v(-164.17, -62.85) * mm});
            skLineSegment(sketch, "E1079", {"start": v(-164.17, -62.85) * mm, "end": v(-163.63, -62.73) * mm});
            skLineSegment(sketch, "E1080", {"start": v(-163.63, -62.73) * mm, "end": v(-163.09, -62.63) * mm});
            skLineSegment(sketch, "E1081", {"start": v(-163.09, -62.63) * mm, "end": v(-162.54, -62.56) * mm});
            skLineSegment(sketch, "E1082", {"start": v(-162.54, -62.56) * mm, "end": v(-161.99, -62.52) * mm});
            skLineSegment(sketch, "E1083", {"start": v(-161.99, -62.52) * mm, "end": v(-161.43, -62.5) * mm});
            skLineSegment(sketch, "E1084", {"start": v(-161.43, -62.5) * mm, "end": v(-161.13, -62.5) * mm});
            skLineSegment(sketch, "E1085", {"start": v(-161.13, -62.5) * mm, "end": v(-160.82, -62.51) * mm});
            skLineSegment(sketch, "E1086", {"start": v(-160.82, -62.51) * mm, "end": v(-160.52, -62.53) * mm});
            skLineSegment(sketch, "E1087", {"start": v(-160.52, -62.53) * mm, "end": v(-160.21, -62.55) * mm});
            skLineSegment(sketch, "E1088", {"start": v(-160.21, -62.55) * mm, "end": v(-159.9, -62.58) * mm});
            skLineSegment(sketch, "E1089", {"start": v(-159.9, -62.58) * mm, "end": v(-159.6, -62.62) * mm});
            skLineSegment(sketch, "E1090", {"start": v(-159.6, -62.62) * mm, "end": v(-159.3, -62.67) * mm});
            skLineSegment(sketch, "E1091", {"start": v(-159.3, -62.67) * mm, "end": v(-159.01, -62.72) * mm});
            skLineSegment(sketch, "E1092", {"start": v(-159.01, -62.72) * mm, "end": v(-158.72, -62.79) * mm});
            skLineSegment(sketch, "E1093", {"start": v(-158.72, -62.79) * mm, "end": v(-158.42, -62.86) * mm});
            skLineSegment(sketch, "E1094", {"start": v(-158.42, -62.86) * mm, "end": v(-158.13, -62.93) * mm});
            skLineSegment(sketch, "E1095", {"start": v(-158.13, -62.93) * mm, "end": v(-157.84, -63.02) * mm});
            skLineSegment(sketch, "E1096", {"start": v(-157.84, -63.02) * mm, "end": v(-157.55, -63.1) * mm});
            skLineSegment(sketch, "E1097", {"start": v(-157.55, -63.1) * mm, "end": v(-157.27, -63.2) * mm});
            skLineSegment(sketch, "E1098", {"start": v(-157.27, -63.2) * mm, "end": v(-156.98, -63.3) * mm});
            skLineSegment(sketch, "E1099", {"start": v(-156.98, -63.3) * mm, "end": v(-156.7, -63.42) * mm});
            skLineSegment(sketch, "E1100", {"start": v(-156.7, -63.42) * mm, "end": v(-156.43, -63.54) * mm});
            skLineSegment(sketch, "E1101", {"start": v(-156.43, -63.54) * mm, "end": v(-156.15, -63.67) * mm});
            skLineSegment(sketch, "E1102", {"start": v(-156.15, -63.67) * mm, "end": v(-155.88, -63.8) * mm});
            skLineSegment(sketch, "E1103", {"start": v(-155.88, -63.8) * mm, "end": v(-155.61, -63.94) * mm});
            skLineSegment(sketch, "E1104", {"start": v(-155.61, -63.94) * mm, "end": v(-155.35, -64.08) * mm});
            skLineSegment(sketch, "E1105", {"start": v(-155.35, -64.08) * mm, "end": v(-155.09, -64.24) * mm});
            skLineSegment(sketch, "E1106", {"start": v(-155.09, -64.24) * mm, "end": v(-154.83, -64.4) * mm});
            skLineSegment(sketch, "E1107", {"start": v(-154.83, -64.4) * mm, "end": v(-154.58, -64.56) * mm});
            skLineSegment(sketch, "E1108", {"start": v(-154.58, -64.56) * mm, "end": v(-154.33, -64.73) * mm});
            skLineSegment(sketch, "E1109", {"start": v(-154.33, -64.73) * mm, "end": v(-154.09, -64.91) * mm});
            skLineSegment(sketch, "E1110", {"start": v(-154.09, -64.91) * mm, "end": v(-153.85, -65.1) * mm});
            skLineSegment(sketch, "E1111", {"start": v(-153.85, -65.1) * mm, "end": v(-153.6, -65.29) * mm});
            skLineSegment(sketch, "E1112", {"start": v(-153.6, -65.29) * mm, "end": v(-153.38, -65.49) * mm});
            skLineSegment(sketch, "E1113", {"start": v(-153.38, -65.49) * mm, "end": v(-153.15, -65.69) * mm});
            skLineSegment(sketch, "E1114", {"start": v(-153.15, -65.69) * mm, "end": v(-152.93, -65.9) * mm});
            skLineSegment(sketch, "E1115", {"start": v(-152.93, -65.9) * mm, "end": v(-152.71, -66.12) * mm});
            skLineSegment(sketch, "E1116", {"start": v(-152.71, -66.12) * mm, "end": v(-152.44, -66.42) * mm});
            skLineSegment(sketch, "E1117", {"start": v(-152.44, -66.42) * mm, "end": v(-152.18, -66.73) * mm});
            skLineSegment(sketch, "E1118", {"start": v(-152.18, -66.73) * mm, "end": v(-151.93, -67.04) * mm});
            skLineSegment(sketch, "E1119", {"start": v(-151.93, -67.04) * mm, "end": v(-151.69, -67.37) * mm});
            skLineSegment(sketch, "E1120", {"start": v(-151.69, -67.37) * mm, "end": v(-151.45, -67.7) * mm});
            skLineSegment(sketch, "E1121", {"start": v(-151.45, -67.7) * mm, "end": v(-151.22, -68.02) * mm});
            skLineSegment(sketch, "E1122", {"start": v(-151.22, -68.02) * mm, "end": v(-151, -68.36) * mm});
            skLineSegment(sketch, "E1123", {"start": v(-151, -68.36) * mm, "end": v(-150.8, -68.7) * mm});
            skLineSegment(sketch, "E1124", {"start": v(-150.8, -68.7) * mm, "end": v(-150.6, -69.05) * mm});
            skLineSegment(sketch, "E1125", {"start": v(-150.6, -69.05) * mm, "end": v(-150.4, -69.4) * mm});
            skLineSegment(sketch, "E1126", {"start": v(-150.4, -69.4) * mm, "end": v(-150.22, -69.76) * mm});
            skLineSegment(sketch, "E1127", {"start": v(-150.22, -69.76) * mm, "end": v(-150.04, -70.12) * mm});
            skLineSegment(sketch, "E1128", {"start": v(-150.04, -70.12) * mm, "end": v(-149.87, -70.48) * mm});
            skLineSegment(sketch, "E1129", {"start": v(-149.87, -70.48) * mm, "end": v(-149.72, -70.85) * mm});
            skLineSegment(sketch, "E1130", {"start": v(-149.72, -70.85) * mm, "end": v(-149.57, -71.22) * mm});
            skLineSegment(sketch, "E1131", {"start": v(-149.57, -71.22) * mm, "end": v(-149.43, -71.6) * mm});
            skLineSegment(sketch, "E1132", {"start": v(-149.43, -71.6) * mm, "end": v(-149.3, -71.97) * mm});
            skLineSegment(sketch, "E1133", {"start": v(-149.3, -71.97) * mm, "end": v(-149.18, -72.35) * mm});
            skLineSegment(sketch, "E1134", {"start": v(-149.18, -72.35) * mm, "end": v(-149.06, -72.74) * mm});
            skLineSegment(sketch, "E1135", {"start": v(-149.06, -72.74) * mm, "end": v(-148.96, -73.12) * mm});
            skLineSegment(sketch, "E1136", {"start": v(-148.96, -73.12) * mm, "end": v(-148.87, -73.51) * mm});
            skLineSegment(sketch, "E1137", {"start": v(-148.87, -73.51) * mm, "end": v(-148.79, -73.9) * mm});
            skLineSegment(sketch, "E1138", {"start": v(-148.79, -73.9) * mm, "end": v(-148.71, -74.3) * mm});
            skLineSegment(sketch, "E1139", {"start": v(-148.71, -74.3) * mm, "end": v(-148.65, -74.7) * mm});
            skLineSegment(sketch, "E1140", {"start": v(-148.65, -74.7) * mm, "end": v(-148.6, -75.1) * mm});
            skLineSegment(sketch, "E1141", {"start": v(-148.6, -75.1) * mm, "end": v(-148.55, -75.5) * mm});
            skLineSegment(sketch, "E1142", {"start": v(-148.55, -75.5) * mm, "end": v(-148.51, -75.9) * mm});
            skLineSegment(sketch, "E1143", {"start": v(-148.51, -75.9) * mm, "end": v(-148.49, -76.3) * mm});
            skLineSegment(sketch, "E1144", {"start": v(-148.49, -76.3) * mm, "end": v(-148.47, -76.7) * mm});
            skLineSegment(sketch, "E1145", {"start": v(-148.47, -76.7) * mm, "end": v(-148.47, -77.1) * mm});
            skLineSegment(sketch, "E1146", {"start": v(-148.47, -77.1) * mm, "end": v(-148.47, -77.5) * mm});
            skLineSegment(sketch, "E1147", {"start": v(-148.47, -77.5) * mm, "end": v(-148.48, -77.91) * mm});
            skLineSegment(sketch, "E1148", {"start": v(-148.48, -77.91) * mm, "end": v(-148.47, -78.32) * mm});
            skLineSegment(sketch, "E1149", {"start": v(-148.47, -78.32) * mm, "end": v(-148.47, -78.73) * mm});
            skLineSegment(sketch, "E1150", {"start": v(-148.47, -78.73) * mm, "end": v(-148.48, -79.15) * mm});
            skLineSegment(sketch, "E1151", {"start": v(-148.48, -79.15) * mm, "end": v(-148.5, -79.56) * mm});
            skLineSegment(sketch, "E1152", {"start": v(-148.5, -79.56) * mm, "end": v(-148.52, -79.97) * mm});
            skLineSegment(sketch, "E1153", {"start": v(-148.52, -79.97) * mm, "end": v(-148.56, -80.37) * mm});
            skLineSegment(sketch, "E1154", {"start": v(-148.56, -80.37) * mm, "end": v(-148.6, -80.78) * mm});
            skLineSegment(sketch, "E1155", {"start": v(-148.6, -80.78) * mm, "end": v(-148.66, -81.18) * mm});
            skLineSegment(sketch, "E1156", {"start": v(-148.66, -81.18) * mm, "end": v(-148.73, -81.59) * mm});
            skLineSegment(sketch, "E1157", {"start": v(-148.73, -81.59) * mm, "end": v(-148.8, -81.99) * mm});
            skLineSegment(sketch, "E1158", {"start": v(-148.8, -81.99) * mm, "end": v(-148.89, -82.39) * mm});
            skLineSegment(sketch, "E1159", {"start": v(-148.89, -82.39) * mm, "end": v(-148.98, -82.78) * mm});
            skLineSegment(sketch, "E1160", {"start": v(-148.98, -82.78) * mm, "end": v(-149.09, -83.18) * mm});
            skLineSegment(sketch, "E1161", {"start": v(-149.09, -83.18) * mm, "end": v(-149.2, -83.57) * mm});
            skLineSegment(sketch, "E1162", {"start": v(-149.2, -83.57) * mm, "end": v(-149.32, -83.96) * mm});
            skLineSegment(sketch, "E1163", {"start": v(-149.32, -83.96) * mm, "end": v(-149.46, -84.34) * mm});
            skLineSegment(sketch, "E1164", {"start": v(-149.46, -84.34) * mm, "end": v(-149.6, -84.72) * mm});
            skLineSegment(sketch, "E1165", {"start": v(-149.6, -84.72) * mm, "end": v(-149.75, -85.1) * mm});
            skLineSegment(sketch, "E1166", {"start": v(-149.75, -85.1) * mm, "end": v(-149.9, -85.47) * mm});
            skLineSegment(sketch, "E1167", {"start": v(-149.9, -85.47) * mm, "end": v(-150.08, -85.85) * mm});
            skLineSegment(sketch, "E1168", {"start": v(-150.08, -85.85) * mm, "end": v(-150.25, -86.21) * mm});
            skLineSegment(sketch, "E1169", {"start": v(-150.25, -86.21) * mm, "end": v(-150.44, -86.57) * mm});
            skLineSegment(sketch, "E1170", {"start": v(-150.44, -86.57) * mm, "end": v(-150.63, -86.93) * mm});
            skLineSegment(sketch, "E1171", {"start": v(-150.63, -86.93) * mm, "end": v(-150.84, -87.29) * mm});
            skLineSegment(sketch, "E1172", {"start": v(-150.84, -87.29) * mm, "end": v(-151.05, -87.64) * mm});
            skLineSegment(sketch, "E1173", {"start": v(-151.05, -87.64) * mm, "end": v(-151.27, -87.98) * mm});
            skLineSegment(sketch, "E1174", {"start": v(-151.27, -87.98) * mm, "end": v(-151.5, -88.32) * mm});
            skLineSegment(sketch, "E1175", {"start": v(-151.5, -88.32) * mm, "end": v(-151.74, -88.65) * mm});
            skLineSegment(sketch, "E1176", {"start": v(-151.74, -88.65) * mm, "end": v(-151.99, -88.98) * mm});
            skLineSegment(sketch, "E1177", {"start": v(-151.99, -88.98) * mm, "end": v(-152.24, -89.3) * mm});
            skLineSegment(sketch, "E1178", {"start": v(-152.24, -89.3) * mm, "end": v(-152.5, -89.62) * mm});
            skLineSegment(sketch, "E1179", {"start": v(-152.5, -89.62) * mm, "end": v(-152.78, -89.93) * mm});
            skLineSegment(sketch, "E1180", {"start": v(-152.78, -89.93) * mm, "end": v(-153.18, -90.32) * mm});
            skLineSegment(sketch, "E1181", {"start": v(-153.18, -90.32) * mm, "end": v(-153.6, -90.7) * mm});
            skLineSegment(sketch, "E1182", {"start": v(-153.6, -90.7) * mm, "end": v(-154.05, -91.04) * mm});
            skLineSegment(sketch, "E1183", {"start": v(-154.05, -91.04) * mm, "end": v(-154.5, -91.37) * mm});
            skLineSegment(sketch, "E1184", {"start": v(-154.5, -91.37) * mm, "end": v(-154.98, -91.67) * mm});
            skLineSegment(sketch, "E1185", {"start": v(-154.98, -91.67) * mm, "end": v(-155.47, -91.95) * mm});
            skLineSegment(sketch, "E1186", {"start": v(-155.47, -91.95) * mm, "end": v(-155.96, -92.2) * mm});
            skLineSegment(sketch, "E1187", {"start": v(-155.96, -92.2) * mm, "end": v(-156.47, -92.43) * mm});
            skLineSegment(sketch, "E1188", {"start": v(-156.47, -92.43) * mm, "end": v(-157, -92.63) * mm});
            skLineSegment(sketch, "E1189", {"start": v(-157, -92.63) * mm, "end": v(-157.52, -92.8) * mm});
            skLineSegment(sketch, "E1190", {"start": v(-157.52, -92.8) * mm, "end": v(-158.06, -92.96) * mm});
            skLineSegment(sketch, "E1191", {"start": v(-158.06, -92.96) * mm, "end": v(-158.6, -93.08) * mm});
            skLineSegment(sketch, "E1192", {"start": v(-158.6, -93.08) * mm, "end": v(-159.16, -93.18) * mm});
            skLineSegment(sketch, "E1193", {"start": v(-159.16, -93.18) * mm, "end": v(-159.72, -93.25) * mm});
            skLineSegment(sketch, "E1194", {"start": v(-159.72, -93.25) * mm, "end": v(-160.28, -93.3) * mm});
            skLineSegment(sketch, "E1195", {"start": v(-160.28, -93.3) * mm, "end": v(-160.85, -93.3) * mm});
            skLineSegment(sketch, "E1196", {"start": v(-160.85, -93.3) * mm, "end": v(-161.16, -93.3) * mm});
            skLineSegment(sketch, "E1197", {"start": v(-161.16, -93.3) * mm, "end": v(-161.46, -93.29) * mm});
            skLineSegment(sketch, "E1198", {"start": v(-161.46, -93.29) * mm, "end": v(-161.77, -93.27) * mm});
            skLineSegment(sketch, "E1199", {"start": v(-161.77, -93.27) * mm, "end": v(-162.08, -93.24) * mm});
            skLineSegment(sketch, "E1200", {"start": v(-162.08, -93.24) * mm, "end": v(-162.38, -93.2) * mm});
            skLineSegment(sketch, "E1201", {"start": v(-162.38, -93.2) * mm, "end": v(-162.68, -93.16) * mm});
            skLineSegment(sketch, "E1202", {"start": v(-162.68, -93.16) * mm, "end": v(-162.99, -93.1) * mm});
            skLineSegment(sketch, "E1203", {"start": v(-162.99, -93.1) * mm, "end": v(-163.29, -93.05) * mm});
            skLineSegment(sketch, "E1204", {"start": v(-163.29, -93.05) * mm, "end": v(-163.58, -92.98) * mm});
            skLineSegment(sketch, "E1205", {"start": v(-163.58, -92.98) * mm, "end": v(-163.88, -92.91) * mm});
            skLineSegment(sketch, "E1206", {"start": v(-163.88, -92.91) * mm, "end": v(-164.17, -92.83) * mm});
            skLineSegment(sketch, "E1207", {"start": v(-164.17, -92.83) * mm, "end": v(-164.46, -92.74) * mm});
            skLineSegment(sketch, "E1208", {"start": v(-164.46, -92.74) * mm, "end": v(-164.75, -92.65) * mm});
            skLineSegment(sketch, "E1209", {"start": v(-164.75, -92.65) * mm, "end": v(-165.04, -92.54) * mm});
            skLineSegment(sketch, "E1210", {"start": v(-165.04, -92.54) * mm, "end": v(-165.32, -92.43) * mm});
            skLineSegment(sketch, "E1211", {"start": v(-165.32, -92.43) * mm, "end": v(-165.6, -92.32) * mm});
            skLineSegment(sketch, "E1212", {"start": v(-165.6, -92.32) * mm, "end": v(-165.88, -92.2) * mm});
            skLineSegment(sketch, "E1213", {"start": v(-165.88, -92.2) * mm, "end": v(-166.15, -92.06) * mm});
            skLineSegment(sketch, "E1214", {"start": v(-166.15, -92.06) * mm, "end": v(-166.43, -91.92) * mm});
            skLineSegment(sketch, "E1215", {"start": v(-166.43, -91.92) * mm, "end": v(-166.7, -91.78) * mm});
            skLineSegment(sketch, "E1216", {"start": v(-166.7, -91.78) * mm, "end": v(-166.96, -91.63) * mm});
            skLineSegment(sketch, "E1217", {"start": v(-166.96, -91.63) * mm, "end": v(-167.22, -91.47) * mm});
            skLineSegment(sketch, "E1218", {"start": v(-167.22, -91.47) * mm, "end": v(-167.47, -91.3) * mm});
            skLineSegment(sketch, "E1219", {"start": v(-167.47, -91.3) * mm, "end": v(-167.73, -91.13) * mm});
            skLineSegment(sketch, "E1220", {"start": v(-167.73, -91.13) * mm, "end": v(-167.97, -90.95) * mm});
            skLineSegment(sketch, "E1221", {"start": v(-167.97, -90.95) * mm, "end": v(-168.22, -90.77) * mm});
            skLineSegment(sketch, "E1222", {"start": v(-168.22, -90.77) * mm, "end": v(-168.46, -90.58) * mm});
            skLineSegment(sketch, "E1223", {"start": v(-168.46, -90.58) * mm, "end": v(-168.7, -90.38) * mm});
            skLineSegment(sketch, "E1224", {"start": v(-168.7, -90.38) * mm, "end": v(-168.92, -90.18) * mm});
            skLineSegment(sketch, "E1225", {"start": v(-168.92, -90.18) * mm, "end": v(-169.15, -89.97) * mm});
            skLineSegment(sketch, "E1226", {"start": v(-169.15, -89.97) * mm, "end": v(-169.37, -89.75) * mm});
            skLineSegment(sketch, "E1227", {"start": v(-169.37, -89.75) * mm, "end": v(-169.58, -89.53) * mm});
            skLineSegment(sketch, "E1228", {"start": v(-169.58, -89.53) * mm, "end": v(-169.99, -89.12) * mm});
            skLineSegment(sketch, "E1229", {"start": v(-169.99, -89.12) * mm, "end": v(-170.37, -88.7) * mm});
            skLineSegment(sketch, "E1230", {"start": v(-170.37, -88.7) * mm, "end": v(-170.73, -88.25) * mm});
            skLineSegment(sketch, "E1231", {"start": v(-170.73, -88.25) * mm, "end": v(-171.07, -87.78) * mm});
            skLineSegment(sketch, "E1232", {"start": v(-171.07, -87.78) * mm, "end": v(-171.38, -87.3) * mm});
            skLineSegment(sketch, "E1233", {"start": v(-171.38, -87.3) * mm, "end": v(-171.67, -86.8) * mm});
            skLineSegment(sketch, "E1234", {"start": v(-171.67, -86.8) * mm, "end": v(-171.94, -86.3) * mm});
            skLineSegment(sketch, "E1235", {"start": v(-171.94, -86.3) * mm, "end": v(-172.18, -85.77) * mm});
            skLineSegment(sketch, "E1236", {"start": v(466.2, 382.01) * mm, "end": v(431.2, 382.01) * mm});
            skLineSegment(sketch, "E1237", {"start": v(431.2, 382.01) * mm, "end": v(431.2, 403.77) * mm});
            skLineSegment(sketch, "E1238", {"start": v(447.93, 382.01) * mm, "end": v(447.93, 402.2) * mm});
            skLineSegment(sketch, "E1239", {"start": v(466.18, 432.03) * mm, "end": v(466.18, 411.47) * mm});
            skLineSegment(sketch, "E1240", {"start": v(466.18, 411.47) * mm, "end": v(431.22, 411.47) * mm});
            skLineSegment(sketch, "E1241", {"start": v(466.67, 445.3) * mm, "end": v(466.67, 444.93) * mm});
            skLineSegment(sketch, "E1242", {"start": v(466.67, 444.93) * mm, "end": v(466.66, 444.56) * mm});
            skLineSegment(sketch, "E1243", {"start": v(466.66, 444.56) * mm, "end": v(466.65, 444.2) * mm});
            skLineSegment(sketch, "E1244", {"start": v(466.65, 444.2) * mm, "end": v(466.62, 443.83) * mm});
            skLineSegment(sketch, "E1245", {"start": v(466.62, 443.83) * mm, "end": v(466.6, 443.47) * mm});
            skLineSegment(sketch, "E1246", {"start": v(466.6, 443.47) * mm, "end": v(466.55, 443.1) * mm});
            skLineSegment(sketch, "E1247", {"start": v(466.55, 443.1) * mm, "end": v(466.5, 442.75) * mm});
            skLineSegment(sketch, "E1248", {"start": v(466.5, 442.75) * mm, "end": v(466.43, 442.39) * mm});
            skLineSegment(sketch, "E1249", {"start": v(466.43, 442.39) * mm, "end": v(466.36, 442.03) * mm});
            skLineSegment(sketch, "E1250", {"start": v(466.36, 442.03) * mm, "end": v(466.29, 441.68) * mm});
            skLineSegment(sketch, "E1251", {"start": v(466.29, 441.68) * mm, "end": v(466.2, 441.32) * mm});
            skLineSegment(sketch, "E1252", {"start": v(466.2, 441.32) * mm, "end": v(466.1, 440.97) * mm});
            skLineSegment(sketch, "E1253", {"start": v(466.1, 440.97) * mm, "end": v(466, 440.63) * mm});
            skLineSegment(sketch, "E1254", {"start": v(466, 440.63) * mm, "end": v(465.89, 440.28) * mm});
            skLineSegment(sketch, "E1255", {"start": v(465.89, 440.28) * mm, "end": v(465.76, 439.94) * mm});
            skLineSegment(sketch, "E1256", {"start": v(465.76, 439.94) * mm, "end": v(465.64, 439.6) * mm});
            skLineSegment(sketch, "E1257", {"start": v(465.64, 439.6) * mm, "end": v(465.5, 439.27) * mm});
            skLineSegment(sketch, "E1258", {"start": v(465.5, 439.27) * mm, "end": v(465.35, 438.94) * mm});
            skLineSegment(sketch, "E1259", {"start": v(465.35, 438.94) * mm, "end": v(465.2, 438.61) * mm});
            skLineSegment(sketch, "E1260", {"start": v(465.2, 438.61) * mm, "end": v(465.03, 438.29) * mm});
            skLineSegment(sketch, "E1261", {"start": v(465.03, 438.29) * mm, "end": v(464.86, 437.97) * mm});
            skLineSegment(sketch, "E1262", {"start": v(464.86, 437.97) * mm, "end": v(464.68, 437.65) * mm});
            skLineSegment(sketch, "E1263", {"start": v(464.68, 437.65) * mm, "end": v(464.5, 437.34) * mm});
            skLineSegment(sketch, "E1264", {"start": v(464.5, 437.34) * mm, "end": v(464.3, 437.04) * mm});
            skLineSegment(sketch, "E1265", {"start": v(464.3, 437.04) * mm, "end": v(464.1, 436.73) * mm});
            skLineSegment(sketch, "E1266", {"start": v(464.1, 436.73) * mm, "end": v(463.9, 436.44) * mm});
            skLineSegment(sketch, "E1267", {"start": v(463.9, 436.44) * mm, "end": v(463.67, 436.14) * mm});
            skLineSegment(sketch, "E1268", {"start": v(463.67, 436.14) * mm, "end": v(463.45, 435.86) * mm});
            skLineSegment(sketch, "E1269", {"start": v(463.45, 435.86) * mm, "end": v(463.22, 435.58) * mm});
            skLineSegment(sketch, "E1270", {"start": v(463.22, 435.58) * mm, "end": v(462.98, 435.3) * mm});
            skLineSegment(sketch, "E1271", {"start": v(462.98, 435.3) * mm, "end": v(462.73, 435.03) * mm});
            skLineSegment(sketch, "E1272", {"start": v(462.73, 435.03) * mm, "end": v(462.47, 434.76) * mm});
            skLineSegment(sketch, "E1273", {"start": v(462.47, 434.76) * mm, "end": v(462.14, 434.46) * mm});
            skLineSegment(sketch, "E1274", {"start": v(462.14, 434.46) * mm, "end": v(461.8, 434.16) * mm});
            skLineSegment(sketch, "E1275", {"start": v(461.8, 434.16) * mm, "end": v(461.45, 433.87) * mm});
            skLineSegment(sketch, "E1276", {"start": v(461.45, 433.87) * mm, "end": v(461.1, 433.6) * mm});
            skLineSegment(sketch, "E1277", {"start": v(461.1, 433.6) * mm, "end": v(460.74, 433.32) * mm});
            skLineSegment(sketch, "E1278", {"start": v(460.74, 433.32) * mm, "end": v(460.38, 433.06) * mm});
            skLineSegment(sketch, "E1279", {"start": v(460.38, 433.06) * mm, "end": v(460, 432.81) * mm});
            skLineSegment(sketch, "E1280", {"start": v(460, 432.81) * mm, "end": v(459.63, 432.57) * mm});
            skLineSegment(sketch, "E1281", {"start": v(459.63, 432.57) * mm, "end": v(459.25, 432.34) * mm});
            skLineSegment(sketch, "E1282", {"start": v(459.25, 432.34) * mm, "end": v(458.86, 432.12) * mm});
            skLineSegment(sketch, "E1283", {"start": v(458.86, 432.12) * mm, "end": v(458.47, 431.9) * mm});
            skLineSegment(sketch, "E1284", {"start": v(458.47, 431.9) * mm, "end": v(458.07, 431.7) * mm});
            skLineSegment(sketch, "E1285", {"start": v(458.07, 431.7) * mm, "end": v(457.67, 431.51) * mm});
            skLineSegment(sketch, "E1286", {"start": v(457.67, 431.51) * mm, "end": v(457.26, 431.33) * mm});
            skLineSegment(sketch, "E1287", {"start": v(457.26, 431.33) * mm, "end": v(456.85, 431.16) * mm});
            skLineSegment(sketch, "E1288", {"start": v(456.85, 431.16) * mm, "end": v(456.43, 431) * mm});
            skLineSegment(sketch, "E1289", {"start": v(456.43, 431) * mm, "end": v(456.01, 430.84) * mm});
            skLineSegment(sketch, "E1290", {"start": v(456.01, 430.84) * mm, "end": v(455.6, 430.7) * mm});
            skLineSegment(sketch, "E1291", {"start": v(455.6, 430.7) * mm, "end": v(455.17, 430.57) * mm});
            skLineSegment(sketch, "E1292", {"start": v(455.17, 430.57) * mm, "end": v(454.74, 430.45) * mm});
            skLineSegment(sketch, "E1293", {"start": v(454.74, 430.45) * mm, "end": v(454.3, 430.34) * mm});
            skLineSegment(sketch, "E1294", {"start": v(454.3, 430.34) * mm, "end": v(453.87, 430.24) * mm});
            skLineSegment(sketch, "E1295", {"start": v(453.87, 430.24) * mm, "end": v(453.43, 430.15) * mm});
            skLineSegment(sketch, "E1296", {"start": v(453.43, 430.15) * mm, "end": v(453, 430.07) * mm});
            skLineSegment(sketch, "E1297", {"start": v(453, 430.07) * mm, "end": v(452.55, 430) * mm});
            skLineSegment(sketch, "E1298", {"start": v(452.55, 430) * mm, "end": v(452.1, 429.95) * mm});
            skLineSegment(sketch, "E1299", {"start": v(452.1, 429.95) * mm, "end": v(451.66, 429.9) * mm});
            skLineSegment(sketch, "E1300", {"start": v(451.66, 429.9) * mm, "end": v(451.21, 429.87) * mm});
            skLineSegment(sketch, "E1301", {"start": v(451.21, 429.87) * mm, "end": v(450.76, 429.84) * mm});
            skLineSegment(sketch, "E1302", {"start": v(450.76, 429.84) * mm, "end": v(450.31, 429.83) * mm});
            skLineSegment(sketch, "E1303", {"start": v(450.31, 429.83) * mm, "end": v(449.86, 429.83) * mm});
            skLineSegment(sketch, "E1304", {"start": v(449.86, 429.83) * mm, "end": v(449.4, 429.84) * mm});
            skLineSegment(sketch, "E1305", {"start": v(449.4, 429.84) * mm, "end": v(448.92, 429.83) * mm});
            skLineSegment(sketch, "E1306", {"start": v(448.92, 429.83) * mm, "end": v(448.43, 429.83) * mm});
            skLineSegment(sketch, "E1307", {"start": v(448.43, 429.83) * mm, "end": v(447.94, 429.84) * mm});
            skLineSegment(sketch, "E1308", {"start": v(447.94, 429.84) * mm, "end": v(447.45, 429.86) * mm});
            skLineSegment(sketch, "E1309", {"start": v(447.45, 429.86) * mm, "end": v(446.96, 429.9) * mm});
            skLineSegment(sketch, "E1310", {"start": v(446.96, 429.9) * mm, "end": v(446.48, 429.94) * mm});
            skLineSegment(sketch, "E1311", {"start": v(446.48, 429.94) * mm, "end": v(446, 430) * mm});
            skLineSegment(sketch, "E1312", {"start": v(446, 430) * mm, "end": v(445.52, 430.07) * mm});
            skLineSegment(sketch, "E1313", {"start": v(445.52, 430.07) * mm, "end": v(445.04, 430.16) * mm});
            skLineSegment(sketch, "E1314", {"start": v(445.04, 430.16) * mm, "end": v(444.56, 430.25) * mm});
            skLineSegment(sketch, "E1315", {"start": v(444.56, 430.25) * mm, "end": v(444.09, 430.36) * mm});
            skLineSegment(sketch, "E1316", {"start": v(444.09, 430.36) * mm, "end": v(443.62, 430.48) * mm});
            skLineSegment(sketch, "E1317", {"start": v(443.62, 430.48) * mm, "end": v(443.15, 430.6) * mm});
            skLineSegment(sketch, "E1318", {"start": v(443.15, 430.6) * mm, "end": v(442.7, 430.75) * mm});
            skLineSegment(sketch, "E1319", {"start": v(442.7, 430.75) * mm, "end": v(442.23, 430.9) * mm});
            skLineSegment(sketch, "E1320", {"start": v(442.23, 430.9) * mm, "end": v(441.78, 431.07) * mm});
            skLineSegment(sketch, "E1321", {"start": v(441.78, 431.07) * mm, "end": v(441.33, 431.24) * mm});
            skLineSegment(sketch, "E1322", {"start": v(441.33, 431.24) * mm, "end": v(440.88, 431.43) * mm});
            skLineSegment(sketch, "E1323", {"start": v(440.88, 431.43) * mm, "end": v(440.44, 431.63) * mm});
            skLineSegment(sketch, "E1324", {"start": v(440.44, 431.63) * mm, "end": v(440, 431.84) * mm});
            skLineSegment(sketch, "E1325", {"start": v(440, 431.84) * mm, "end": v(439.57, 432.06) * mm});
            skLineSegment(sketch, "E1326", {"start": v(439.57, 432.06) * mm, "end": v(439.14, 432.29) * mm});
            skLineSegment(sketch, "E1327", {"start": v(439.14, 432.29) * mm, "end": v(438.72, 432.53) * mm});
            skLineSegment(sketch, "E1328", {"start": v(438.72, 432.53) * mm, "end": v(438.3, 432.78) * mm});
            skLineSegment(sketch, "E1329", {"start": v(438.3, 432.78) * mm, "end": v(437.9, 433.04) * mm});
            skLineSegment(sketch, "E1330", {"start": v(437.9, 433.04) * mm, "end": v(437.5, 433.32) * mm});
            skLineSegment(sketch, "E1331", {"start": v(437.5, 433.32) * mm, "end": v(437.1, 433.6) * mm});
            skLineSegment(sketch, "E1332", {"start": v(437.1, 433.6) * mm, "end": v(436.71, 433.9) * mm});
            skLineSegment(sketch, "E1333", {"start": v(436.71, 433.9) * mm, "end": v(436.33, 434.2) * mm});
            skLineSegment(sketch, "E1334", {"start": v(436.33, 434.2) * mm, "end": v(435.95, 434.51) * mm});
            skLineSegment(sketch, "E1335", {"start": v(435.95, 434.51) * mm, "end": v(435.59, 434.84) * mm});
            skLineSegment(sketch, "E1336", {"start": v(435.59, 434.84) * mm, "end": v(435.23, 435.17) * mm});
            skLineSegment(sketch, "E1337", {"start": v(435.23, 435.17) * mm, "end": v(434.97, 435.42) * mm});
            skLineSegment(sketch, "E1338", {"start": v(434.97, 435.42) * mm, "end": v(434.72, 435.68) * mm});
            skLineSegment(sketch, "E1339", {"start": v(434.72, 435.68) * mm, "end": v(434.48, 435.94) * mm});
            skLineSegment(sketch, "E1340", {"start": v(434.48, 435.94) * mm, "end": v(434.25, 436.2) * mm});
            skLineSegment(sketch, "E1341", {"start": v(434.25, 436.2) * mm, "end": v(434.03, 436.48) * mm});
            skLineSegment(sketch, "E1342", {"start": v(434.03, 436.48) * mm, "end": v(433.8, 436.76) * mm});
            skLineSegment(sketch, "E1343", {"start": v(433.8, 436.76) * mm, "end": v(433.6, 437.04) * mm});
            skLineSegment(sketch, "E1344", {"start": v(433.6, 437.04) * mm, "end": v(433.4, 437.33) * mm});
            skLineSegment(sketch, "E1345", {"start": v(433.4, 437.33) * mm, "end": v(433.2, 437.62) * mm});
            skLineSegment(sketch, "E1346", {"start": v(433.2, 437.62) * mm, "end": v(433.01, 437.92) * mm});
            skLineSegment(sketch, "E1347", {"start": v(433.01, 437.92) * mm, "end": v(432.84, 438.22) * mm});
            skLineSegment(sketch, "E1348", {"start": v(432.84, 438.22) * mm, "end": v(432.66, 438.53) * mm});
            skLineSegment(sketch, "E1349", {"start": v(432.66, 438.53) * mm, "end": v(432.5, 438.84) * mm});
            skLineSegment(sketch, "E1350", {"start": v(432.5, 438.84) * mm, "end": v(432.34, 439.15) * mm});
            skLineSegment(sketch, "E1351", {"start": v(432.34, 439.15) * mm, "end": v(432.2, 439.47) * mm});
            skLineSegment(sketch, "E1352", {"start": v(432.2, 439.47) * mm, "end": v(432.06, 439.8) * mm});
            skLineSegment(sketch, "E1353", {"start": v(432.06, 439.8) * mm, "end": v(431.93, 440.12) * mm});
            skLineSegment(sketch, "E1354", {"start": v(431.93, 440.12) * mm, "end": v(431.8, 440.45) * mm});
            skLineSegment(sketch, "E1355", {"start": v(431.8, 440.45) * mm, "end": v(431.7, 440.78) * mm});
            skLineSegment(sketch, "E1356", {"start": v(431.7, 440.78) * mm, "end": v(431.59, 441.12) * mm});
            skLineSegment(sketch, "E1357", {"start": v(431.59, 441.12) * mm, "end": v(431.49, 441.45) * mm});
            skLineSegment(sketch, "E1358", {"start": v(431.49, 441.45) * mm, "end": v(431.4, 441.8) * mm});
            skLineSegment(sketch, "E1359", {"start": v(431.4, 441.8) * mm, "end": v(431.32, 442.14) * mm});
            skLineSegment(sketch, "E1360", {"start": v(431.32, 442.14) * mm, "end": v(431.25, 442.48) * mm});
            skLineSegment(sketch, "E1361", {"start": v(431.25, 442.48) * mm, "end": v(431.19, 442.83) * mm});
            skLineSegment(sketch, "E1362", {"start": v(431.19, 442.83) * mm, "end": v(431.13, 443.18) * mm});
            skLineSegment(sketch, "E1363", {"start": v(431.13, 443.18) * mm, "end": v(431.09, 443.53) * mm});
            skLineSegment(sketch, "E1364", {"start": v(431.09, 443.53) * mm, "end": v(431.05, 443.88) * mm});
            skLineSegment(sketch, "E1365", {"start": v(431.05, 443.88) * mm, "end": v(431.03, 444.23) * mm});
            skLineSegment(sketch, "E1366", {"start": v(431.03, 444.23) * mm, "end": v(431, 444.59) * mm});
            skLineSegment(sketch, "E1367", {"start": v(431, 444.59) * mm, "end": v(431, 444.94) * mm});
            skLineSegment(sketch, "E1368", {"start": v(431, 444.94) * mm, "end": v(431, 445.3) * mm});
            skLineSegment(sketch, "E1369", {"start": v(431, 445.3) * mm, "end": v(431, 445.66) * mm});
            skLineSegment(sketch, "E1370", {"start": v(431, 445.66) * mm, "end": v(431.02, 446.03) * mm});
            skLineSegment(sketch, "E1371", {"start": v(431.02, 446.03) * mm, "end": v(431.04, 446.39) * mm});
            skLineSegment(sketch, "E1372", {"start": v(431.04, 446.39) * mm, "end": v(431.07, 446.74) * mm});
            skLineSegment(sketch, "E1373", {"start": v(431.07, 446.74) * mm, "end": v(431.11, 447.1) * mm});
            skLineSegment(sketch, "E1374", {"start": v(431.11, 447.1) * mm, "end": v(431.16, 447.46) * mm});
            skLineSegment(sketch, "E1375", {"start": v(431.16, 447.46) * mm, "end": v(431.22, 447.81) * mm});
            skLineSegment(sketch, "E1376", {"start": v(431.22, 447.81) * mm, "end": v(431.29, 448.16) * mm});
            skLineSegment(sketch, "E1377", {"start": v(431.29, 448.16) * mm, "end": v(431.37, 448.51) * mm});
            skLineSegment(sketch, "E1378", {"start": v(431.37, 448.51) * mm, "end": v(431.45, 448.86) * mm});
            skLineSegment(sketch, "E1379", {"start": v(431.45, 448.86) * mm, "end": v(431.55, 449.2) * mm});
            skLineSegment(sketch, "E1380", {"start": v(431.55, 449.2) * mm, "end": v(431.65, 449.55) * mm});
            skLineSegment(sketch, "E1381", {"start": v(431.65, 449.55) * mm, "end": v(431.76, 449.89) * mm});
            skLineSegment(sketch, "E1382", {"start": v(431.76, 449.89) * mm, "end": v(431.88, 450.22) * mm});
            skLineSegment(sketch, "E1383", {"start": v(431.88, 450.22) * mm, "end": v(432, 450.56) * mm});
            skLineSegment(sketch, "E1384", {"start": v(432, 450.56) * mm, "end": v(432.15, 450.88) * mm});
            skLineSegment(sketch, "E1385", {"start": v(432.15, 450.88) * mm, "end": v(432.3, 451.21) * mm});
            skLineSegment(sketch, "E1386", {"start": v(432.3, 451.21) * mm, "end": v(432.44, 451.53) * mm});
            skLineSegment(sketch, "E1387", {"start": v(432.44, 451.53) * mm, "end": v(432.6, 451.85) * mm});
            skLineSegment(sketch, "E1388", {"start": v(432.6, 451.85) * mm, "end": v(432.78, 452.16) * mm});
            skLineSegment(sketch, "E1389", {"start": v(432.78, 452.16) * mm, "end": v(432.95, 452.47) * mm});
            skLineSegment(sketch, "E1390", {"start": v(432.95, 452.47) * mm, "end": v(433.14, 452.78) * mm});
            skLineSegment(sketch, "E1391", {"start": v(433.14, 452.78) * mm, "end": v(433.33, 453.08) * mm});
            skLineSegment(sketch, "E1392", {"start": v(433.33, 453.08) * mm, "end": v(433.54, 453.38) * mm});
            skLineSegment(sketch, "E1393", {"start": v(433.54, 453.38) * mm, "end": v(433.75, 453.67) * mm});
            skLineSegment(sketch, "E1394", {"start": v(433.75, 453.67) * mm, "end": v(433.96, 453.95) * mm});
            skLineSegment(sketch, "E1395", {"start": v(433.96, 453.95) * mm, "end": v(434.19, 454.23) * mm});
            skLineSegment(sketch, "E1396", {"start": v(434.19, 454.23) * mm, "end": v(434.42, 454.5) * mm});
            skLineSegment(sketch, "E1397", {"start": v(434.42, 454.5) * mm, "end": v(434.66, 454.78) * mm});
            skLineSegment(sketch, "E1398", {"start": v(434.66, 454.78) * mm, "end": v(434.9, 455.04) * mm});
            skLineSegment(sketch, "E1399", {"start": v(434.9, 455.04) * mm, "end": v(435.16, 455.3) * mm});
            skLineSegment(sketch, "E1400", {"start": v(435.16, 455.3) * mm, "end": v(435.42, 455.55) * mm});
            skLineSegment(sketch, "E1401", {"start": v(435.42, 455.55) * mm, "end": v(435.78, 455.87) * mm});
            skLineSegment(sketch, "E1402", {"start": v(435.78, 455.87) * mm, "end": v(436.15, 456.19) * mm});
            skLineSegment(sketch, "E1403", {"start": v(436.15, 456.19) * mm, "end": v(436.52, 456.49) * mm});
            skLineSegment(sketch, "E1404", {"start": v(436.52, 456.49) * mm, "end": v(436.9, 456.78) * mm});
            skLineSegment(sketch, "E1405", {"start": v(436.9, 456.78) * mm, "end": v(437.29, 457.07) * mm});
            skLineSegment(sketch, "E1406", {"start": v(437.29, 457.07) * mm, "end": v(437.68, 457.34) * mm});
            skLineSegment(sketch, "E1407", {"start": v(437.68, 457.34) * mm, "end": v(438.08, 457.6) * mm});
            skLineSegment(sketch, "E1408", {"start": v(438.08, 457.6) * mm, "end": v(438.48, 457.86) * mm});
            skLineSegment(sketch, "E1409", {"start": v(438.48, 457.86) * mm, "end": v(438.9, 458.1) * mm});
            skLineSegment(sketch, "E1410", {"start": v(438.9, 458.1) * mm, "end": v(439.3, 458.34) * mm});
            skLineSegment(sketch, "E1411", {"start": v(439.3, 458.34) * mm, "end": v(439.73, 458.56) * mm});
            skLineSegment(sketch, "E1412", {"start": v(439.73, 458.56) * mm, "end": v(440.16, 458.77) * mm});
            skLineSegment(sketch, "E1413", {"start": v(440.16, 458.77) * mm, "end": v(440.59, 458.97) * mm});
            skLineSegment(sketch, "E1414", {"start": v(440.59, 458.97) * mm, "end": v(441.03, 459.16) * mm});
            skLineSegment(sketch, "E1415", {"start": v(441.03, 459.16) * mm, "end": v(441.47, 459.34) * mm});
            skLineSegment(sketch, "E1416", {"start": v(441.47, 459.34) * mm, "end": v(441.91, 459.5) * mm});
            skLineSegment(sketch, "E1417", {"start": v(441.91, 459.5) * mm, "end": v(442.36, 459.67) * mm});
            skLineSegment(sketch, "E1418", {"start": v(442.36, 459.67) * mm, "end": v(442.81, 459.81) * mm});
            skLineSegment(sketch, "E1419", {"start": v(442.81, 459.81) * mm, "end": v(443.27, 459.95) * mm});
            skLineSegment(sketch, "E1420", {"start": v(443.27, 459.95) * mm, "end": v(443.73, 460.07) * mm});
            skLineSegment(sketch, "E1421", {"start": v(443.73, 460.07) * mm, "end": v(444.2, 460.18) * mm});
            skLineSegment(sketch, "E1422", {"start": v(444.2, 460.18) * mm, "end": v(444.66, 460.29) * mm});
            skLineSegment(sketch, "E1423", {"start": v(444.66, 460.29) * mm, "end": v(445.13, 460.38) * mm});
            skLineSegment(sketch, "E1424", {"start": v(445.13, 460.38) * mm, "end": v(445.6, 460.45) * mm});
            skLineSegment(sketch, "E1425", {"start": v(445.6, 460.45) * mm, "end": v(446.07, 460.52) * mm});
            skLineSegment(sketch, "E1426", {"start": v(446.07, 460.52) * mm, "end": v(446.55, 460.57) * mm});
            skLineSegment(sketch, "E1427", {"start": v(446.55, 460.57) * mm, "end": v(447.02, 460.62) * mm});
            skLineSegment(sketch, "E1428", {"start": v(447.02, 460.62) * mm, "end": v(447.5, 460.65) * mm});
            skLineSegment(sketch, "E1429", {"start": v(447.5, 460.65) * mm, "end": v(447.98, 460.67) * mm});
            skLineSegment(sketch, "E1430", {"start": v(447.98, 460.67) * mm, "end": v(448.46, 460.67) * mm});
            skLineSegment(sketch, "E1431", {"start": v(448.46, 460.67) * mm, "end": v(448.95, 460.67) * mm});
            skLineSegment(sketch, "E1432", {"start": v(448.95, 460.67) * mm, "end": v(449.43, 460.65) * mm});
            skLineSegment(sketch, "E1433", {"start": v(449.43, 460.65) * mm, "end": v(449.88, 460.66) * mm});
            skLineSegment(sketch, "E1434", {"start": v(449.88, 460.66) * mm, "end": v(450.33, 460.66) * mm});
            skLineSegment(sketch, "E1435", {"start": v(450.33, 460.66) * mm, "end": v(450.78, 460.64) * mm});
            skLineSegment(sketch, "E1436", {"start": v(450.78, 460.64) * mm, "end": v(451.22, 460.61) * mm});
            skLineSegment(sketch, "E1437", {"start": v(451.22, 460.61) * mm, "end": v(451.67, 460.58) * mm});
            skLineSegment(sketch, "E1438", {"start": v(451.67, 460.58) * mm, "end": v(452.11, 460.53) * mm});
            skLineSegment(sketch, "E1439", {"start": v(452.11, 460.53) * mm, "end": v(452.56, 460.47) * mm});
            skLineSegment(sketch, "E1440", {"start": v(452.56, 460.47) * mm, "end": v(453, 460.4) * mm});
            skLineSegment(sketch, "E1441", {"start": v(453, 460.4) * mm, "end": v(453.43, 460.31) * mm});
            skLineSegment(sketch, "E1442", {"start": v(453.43, 460.31) * mm, "end": v(453.87, 460.22) * mm});
            skLineSegment(sketch, "E1443", {"start": v(453.87, 460.22) * mm, "end": v(454.3, 460.12) * mm});
            skLineSegment(sketch, "E1444", {"start": v(454.3, 460.12) * mm, "end": v(454.73, 460) * mm});
            skLineSegment(sketch, "E1445", {"start": v(454.73, 460) * mm, "end": v(455.16, 459.88) * mm});
            skLineSegment(sketch, "E1446", {"start": v(455.16, 459.88) * mm, "end": v(455.58, 459.74) * mm});
            skLineSegment(sketch, "E1447", {"start": v(455.58, 459.74) * mm, "end": v(456, 459.6) * mm});
            skLineSegment(sketch, "E1448", {"start": v(456, 459.6) * mm, "end": v(456.42, 459.44) * mm});
            skLineSegment(sketch, "E1449", {"start": v(456.42, 459.44) * mm, "end": v(456.83, 459.28) * mm});
            skLineSegment(sketch, "E1450", {"start": v(456.83, 459.28) * mm, "end": v(457.23, 459.1) * mm});
            skLineSegment(sketch, "E1451", {"start": v(457.23, 459.1) * mm, "end": v(457.64, 458.91) * mm});
            skLineSegment(sketch, "E1452", {"start": v(457.64, 458.91) * mm, "end": v(458.04, 458.72) * mm});
            skLineSegment(sketch, "E1453", {"start": v(458.04, 458.72) * mm, "end": v(458.43, 458.51) * mm});
            skLineSegment(sketch, "E1454", {"start": v(458.43, 458.51) * mm, "end": v(458.82, 458.3) * mm});
            skLineSegment(sketch, "E1455", {"start": v(458.82, 458.3) * mm, "end": v(459.2, 458.07) * mm});
            skLineSegment(sketch, "E1456", {"start": v(459.2, 458.07) * mm, "end": v(459.58, 457.83) * mm});
            skLineSegment(sketch, "E1457", {"start": v(459.58, 457.83) * mm, "end": v(459.95, 457.59) * mm});
            skLineSegment(sketch, "E1458", {"start": v(459.95, 457.59) * mm, "end": v(460.32, 457.33) * mm});
            skLineSegment(sketch, "E1459", {"start": v(460.32, 457.33) * mm, "end": v(460.68, 457.07) * mm});
            skLineSegment(sketch, "E1460", {"start": v(460.68, 457.07) * mm, "end": v(461.03, 456.8) * mm});
            skLineSegment(sketch, "E1461", {"start": v(461.03, 456.8) * mm, "end": v(461.38, 456.51) * mm});
            skLineSegment(sketch, "E1462", {"start": v(461.38, 456.51) * mm, "end": v(461.72, 456.22) * mm});
            skLineSegment(sketch, "E1463", {"start": v(461.72, 456.22) * mm, "end": v(462.05, 455.92) * mm});
            skLineSegment(sketch, "E1464", {"start": v(462.05, 455.92) * mm, "end": v(462.38, 455.61) * mm});
            skLineSegment(sketch, "E1465", {"start": v(462.38, 455.61) * mm, "end": v(462.64, 455.35) * mm});
            skLineSegment(sketch, "E1466", {"start": v(462.64, 455.35) * mm, "end": v(462.88, 455.09) * mm});
            skLineSegment(sketch, "E1467", {"start": v(462.88, 455.09) * mm, "end": v(463.12, 454.82) * mm});
            skLineSegment(sketch, "E1468", {"start": v(463.12, 454.82) * mm, "end": v(463.36, 454.55) * mm});
            skLineSegment(sketch, "E1469", {"start": v(463.36, 454.55) * mm, "end": v(463.58, 454.27) * mm});
            skLineSegment(sketch, "E1470", {"start": v(463.58, 454.27) * mm, "end": v(463.8, 453.98) * mm});
            skLineSegment(sketch, "E1471", {"start": v(463.8, 453.98) * mm, "end": v(464.01, 453.7) * mm});
            skLineSegment(sketch, "E1472", {"start": v(464.01, 453.7) * mm, "end": v(464.22, 453.4) * mm});
            skLineSegment(sketch, "E1473", {"start": v(464.22, 453.4) * mm, "end": v(464.41, 453.1) * mm});
            skLineSegment(sketch, "E1474", {"start": v(464.41, 453.1) * mm, "end": v(464.6, 452.8) * mm});
            skLineSegment(sketch, "E1475", {"start": v(464.6, 452.8) * mm, "end": v(464.78, 452.49) * mm});
            skLineSegment(sketch, "E1476", {"start": v(464.78, 452.49) * mm, "end": v(464.95, 452.17) * mm});
            skLineSegment(sketch, "E1477", {"start": v(464.95, 452.17) * mm, "end": v(465.12, 451.86) * mm});
            skLineSegment(sketch, "E1478", {"start": v(465.12, 451.86) * mm, "end": v(465.28, 451.54) * mm});
            skLineSegment(sketch, "E1479", {"start": v(465.28, 451.54) * mm, "end": v(465.43, 451.21) * mm});
            skLineSegment(sketch, "E1480", {"start": v(465.43, 451.21) * mm, "end": v(465.57, 450.89) * mm});
            skLineSegment(sketch, "E1481", {"start": v(465.57, 450.89) * mm, "end": v(465.7, 450.55) * mm});
            skLineSegment(sketch, "E1482", {"start": v(465.7, 450.55) * mm, "end": v(465.82, 450.22) * mm});
            skLineSegment(sketch, "E1483", {"start": v(465.82, 450.22) * mm, "end": v(465.94, 449.88) * mm});
            skLineSegment(sketch, "E1484", {"start": v(465.94, 449.88) * mm, "end": v(466.05, 449.54) * mm});
            skLineSegment(sketch, "E1485", {"start": v(466.05, 449.54) * mm, "end": v(466.15, 449.2) * mm});
            skLineSegment(sketch, "E1486", {"start": v(466.15, 449.2) * mm, "end": v(466.24, 448.85) * mm});
            skLineSegment(sketch, "E1487", {"start": v(466.24, 448.85) * mm, "end": v(466.32, 448.5) * mm});
            skLineSegment(sketch, "E1488", {"start": v(466.32, 448.5) * mm, "end": v(466.4, 448.16) * mm});
            skLineSegment(sketch, "E1489", {"start": v(466.4, 448.16) * mm, "end": v(466.46, 447.8) * mm});
            skLineSegment(sketch, "E1490", {"start": v(466.46, 447.8) * mm, "end": v(466.52, 447.45) * mm});
            skLineSegment(sketch, "E1491", {"start": v(466.52, 447.45) * mm, "end": v(466.56, 447.1) * mm});
            skLineSegment(sketch, "E1492", {"start": v(466.56, 447.1) * mm, "end": v(466.6, 446.74) * mm});
            skLineSegment(sketch, "E1493", {"start": v(466.6, 446.74) * mm, "end": v(466.63, 446.38) * mm});
            skLineSegment(sketch, "E1494", {"start": v(466.63, 446.38) * mm, "end": v(466.65, 446.02) * mm});
            skLineSegment(sketch, "E1495", {"start": v(466.65, 446.02) * mm, "end": v(466.67, 445.66) * mm});
            skLineSegment(sketch, "E1496", {"start": v(466.67, 445.66) * mm, "end": v(466.67, 445.3) * mm});
            skLineSegment(sketch, "E1497", {"start": v(466.67, 484) * mm, "end": v(466.67, 483.64) * mm});
            skLineSegment(sketch, "E1498", {"start": v(466.67, 483.64) * mm, "end": v(466.66, 483.28) * mm});
            skLineSegment(sketch, "E1499", {"start": v(466.66, 483.28) * mm, "end": v(466.65, 482.9) * mm});
            skLineSegment(sketch, "E1500", {"start": v(466.65, 482.9) * mm, "end": v(466.62, 482.54) * mm});
            skLineSegment(sketch, "E1501", {"start": v(466.62, 482.54) * mm, "end": v(466.6, 482.18) * mm});
            skLineSegment(sketch, "E1502", {"start": v(466.6, 482.18) * mm, "end": v(466.55, 481.82) * mm});
            skLineSegment(sketch, "E1503", {"start": v(466.55, 481.82) * mm, "end": v(466.5, 481.46) * mm});
            skLineSegment(sketch, "E1504", {"start": v(466.5, 481.46) * mm, "end": v(466.43, 481.1) * mm});
            skLineSegment(sketch, "E1505", {"start": v(466.43, 481.1) * mm, "end": v(466.36, 480.75) * mm});
            skLineSegment(sketch, "E1506", {"start": v(466.36, 480.75) * mm, "end": v(466.29, 480.4) * mm});
            skLineSegment(sketch, "E1507", {"start": v(466.29, 480.4) * mm, "end": v(466.2, 480.04) * mm});
            skLineSegment(sketch, "E1508", {"start": v(466.2, 480.04) * mm, "end": v(466.1, 479.69) * mm});
            skLineSegment(sketch, "E1509", {"start": v(466.1, 479.69) * mm, "end": v(466, 479.34) * mm});
            skLineSegment(sketch, "E1510", {"start": v(466, 479.34) * mm, "end": v(465.89, 479) * mm});
            skLineSegment(sketch, "E1511", {"start": v(465.89, 479) * mm, "end": v(465.76, 478.66) * mm});
            skLineSegment(sketch, "E1512", {"start": v(465.76, 478.66) * mm, "end": v(465.64, 478.32) * mm});
            skLineSegment(sketch, "E1513", {"start": v(465.64, 478.32) * mm, "end": v(465.5, 477.98) * mm});
            skLineSegment(sketch, "E1514", {"start": v(465.5, 477.98) * mm, "end": v(465.35, 477.65) * mm});
            skLineSegment(sketch, "E1515", {"start": v(465.35, 477.65) * mm, "end": v(465.2, 477.33) * mm});
            skLineSegment(sketch, "E1516", {"start": v(465.2, 477.33) * mm, "end": v(465.03, 477) * mm});
            skLineSegment(sketch, "E1517", {"start": v(465.03, 477) * mm, "end": v(464.86, 476.68) * mm});
            skLineSegment(sketch, "E1518", {"start": v(464.86, 476.68) * mm, "end": v(464.68, 476.37) * mm});
            skLineSegment(sketch, "E1519", {"start": v(464.68, 476.37) * mm, "end": v(464.5, 476.06) * mm});
            skLineSegment(sketch, "E1520", {"start": v(464.5, 476.06) * mm, "end": v(464.3, 475.75) * mm});
            skLineSegment(sketch, "E1521", {"start": v(464.3, 475.75) * mm, "end": v(464.1, 475.45) * mm});
            skLineSegment(sketch, "E1522", {"start": v(464.1, 475.45) * mm, "end": v(463.9, 475.15) * mm});
            skLineSegment(sketch, "E1523", {"start": v(463.9, 475.15) * mm, "end": v(463.67, 474.86) * mm});
            skLineSegment(sketch, "E1524", {"start": v(463.67, 474.86) * mm, "end": v(463.45, 474.57) * mm});
            skLineSegment(sketch, "E1525", {"start": v(463.45, 474.57) * mm, "end": v(463.22, 474.29) * mm});
            skLineSegment(sketch, "E1526", {"start": v(463.22, 474.29) * mm, "end": v(462.98, 474.01) * mm});
            skLineSegment(sketch, "E1527", {"start": v(462.98, 474.01) * mm, "end": v(462.73, 473.74) * mm});
            skLineSegment(sketch, "E1528", {"start": v(462.73, 473.74) * mm, "end": v(462.47, 473.48) * mm});
            skLineSegment(sketch, "E1529", {"start": v(462.47, 473.48) * mm, "end": v(462.14, 473.17) * mm});
            skLineSegment(sketch, "E1530", {"start": v(462.14, 473.17) * mm, "end": v(461.8, 472.88) * mm});
            skLineSegment(sketch, "E1531", {"start": v(461.8, 472.88) * mm, "end": v(461.45, 472.59) * mm});
            skLineSegment(sketch, "E1532", {"start": v(461.45, 472.59) * mm, "end": v(461.1, 472.3) * mm});
            skLineSegment(sketch, "E1533", {"start": v(461.1, 472.3) * mm, "end": v(460.74, 472.04) * mm});
            skLineSegment(sketch, "E1534", {"start": v(460.74, 472.04) * mm, "end": v(460.38, 471.78) * mm});
            skLineSegment(sketch, "E1535", {"start": v(460.38, 471.78) * mm, "end": v(460, 471.53) * mm});
            skLineSegment(sketch, "E1536", {"start": v(460, 471.53) * mm, "end": v(459.63, 471.29) * mm});
            skLineSegment(sketch, "E1537", {"start": v(459.63, 471.29) * mm, "end": v(459.25, 471.06) * mm});
            skLineSegment(sketch, "E1538", {"start": v(459.25, 471.06) * mm, "end": v(458.86, 470.83) * mm});
            skLineSegment(sketch, "E1539", {"start": v(458.86, 470.83) * mm, "end": v(458.47, 470.62) * mm});
            skLineSegment(sketch, "E1540", {"start": v(458.47, 470.62) * mm, "end": v(458.07, 470.42) * mm});
            skLineSegment(sketch, "E1541", {"start": v(458.07, 470.42) * mm, "end": v(457.67, 470.23) * mm});
            skLineSegment(sketch, "E1542", {"start": v(457.67, 470.23) * mm, "end": v(457.26, 470.04) * mm});
            skLineSegment(sketch, "E1543", {"start": v(457.26, 470.04) * mm, "end": v(456.85, 469.87) * mm});
            skLineSegment(sketch, "E1544", {"start": v(456.85, 469.87) * mm, "end": v(456.43, 469.7) * mm});
            skLineSegment(sketch, "E1545", {"start": v(456.43, 469.7) * mm, "end": v(456.01, 469.56) * mm});
            skLineSegment(sketch, "E1546", {"start": v(456.01, 469.56) * mm, "end": v(455.6, 469.42) * mm});
            skLineSegment(sketch, "E1547", {"start": v(455.6, 469.42) * mm, "end": v(455.17, 469.28) * mm});
            skLineSegment(sketch, "E1548", {"start": v(455.17, 469.28) * mm, "end": v(454.74, 469.16) * mm});
            skLineSegment(sketch, "E1549", {"start": v(454.74, 469.16) * mm, "end": v(454.3, 469.05) * mm});
            skLineSegment(sketch, "E1550", {"start": v(454.3, 469.05) * mm, "end": v(453.87, 468.95) * mm});
            skLineSegment(sketch, "E1551", {"start": v(453.87, 468.95) * mm, "end": v(453.43, 468.86) * mm});
            skLineSegment(sketch, "E1552", {"start": v(453.43, 468.86) * mm, "end": v(453, 468.79) * mm});
            skLineSegment(sketch, "E1553", {"start": v(453, 468.79) * mm, "end": v(452.55, 468.72) * mm});
            skLineSegment(sketch, "E1554", {"start": v(452.55, 468.72) * mm, "end": v(452.1, 468.66) * mm});
            skLineSegment(sketch, "E1555", {"start": v(452.1, 468.66) * mm, "end": v(451.66, 468.62) * mm});
            skLineSegment(sketch, "E1556", {"start": v(451.66, 468.62) * mm, "end": v(451.21, 468.58) * mm});
            skLineSegment(sketch, "E1557", {"start": v(451.21, 468.58) * mm, "end": v(450.76, 468.56) * mm});
            skLineSegment(sketch, "E1558", {"start": v(450.76, 468.56) * mm, "end": v(450.31, 468.55) * mm});
            skLineSegment(sketch, "E1559", {"start": v(450.31, 468.55) * mm, "end": v(449.86, 468.54) * mm});
            skLineSegment(sketch, "E1560", {"start": v(449.86, 468.54) * mm, "end": v(449.4, 468.56) * mm});
            skLineSegment(sketch, "E1561", {"start": v(449.4, 468.56) * mm, "end": v(448.92, 468.54) * mm});
            skLineSegment(sketch, "E1562", {"start": v(448.92, 468.54) * mm, "end": v(448.43, 468.54) * mm});
            skLineSegment(sketch, "E1563", {"start": v(448.43, 468.54) * mm, "end": v(447.94, 468.55) * mm});
            skLineSegment(sketch, "E1564", {"start": v(447.94, 468.55) * mm, "end": v(447.45, 468.57) * mm});
            skLineSegment(sketch, "E1565", {"start": v(447.45, 468.57) * mm, "end": v(446.96, 468.6) * mm});
            skLineSegment(sketch, "E1566", {"start": v(446.96, 468.6) * mm, "end": v(446.48, 468.66) * mm});
            skLineSegment(sketch, "E1567", {"start": v(446.48, 468.66) * mm, "end": v(446, 468.72) * mm});
            skLineSegment(sketch, "E1568", {"start": v(446, 468.72) * mm, "end": v(445.52, 468.79) * mm});
            skLineSegment(sketch, "E1569", {"start": v(445.52, 468.79) * mm, "end": v(445.04, 468.87) * mm});
            skLineSegment(sketch, "E1570", {"start": v(445.04, 468.87) * mm, "end": v(444.56, 468.97) * mm});
            skLineSegment(sketch, "E1571", {"start": v(444.56, 468.97) * mm, "end": v(444.09, 469.07) * mm});
            skLineSegment(sketch, "E1572", {"start": v(444.09, 469.07) * mm, "end": v(443.62, 469.2) * mm});
            skLineSegment(sketch, "E1573", {"start": v(443.62, 469.2) * mm, "end": v(443.15, 469.32) * mm});
            skLineSegment(sketch, "E1574", {"start": v(443.15, 469.32) * mm, "end": v(442.7, 469.47) * mm});
            skLineSegment(sketch, "E1575", {"start": v(442.7, 469.47) * mm, "end": v(442.23, 469.62) * mm});
            skLineSegment(sketch, "E1576", {"start": v(442.23, 469.62) * mm, "end": v(441.78, 469.78) * mm});
            skLineSegment(sketch, "E1577", {"start": v(441.78, 469.78) * mm, "end": v(441.33, 469.96) * mm});
            skLineSegment(sketch, "E1578", {"start": v(441.33, 469.96) * mm, "end": v(440.88, 470.15) * mm});
            skLineSegment(sketch, "E1579", {"start": v(440.88, 470.15) * mm, "end": v(440.44, 470.34) * mm});
            skLineSegment(sketch, "E1580", {"start": v(440.44, 470.34) * mm, "end": v(440, 470.55) * mm});
            skLineSegment(sketch, "E1581", {"start": v(440, 470.55) * mm, "end": v(439.57, 470.77) * mm});
            skLineSegment(sketch, "E1582", {"start": v(439.57, 470.77) * mm, "end": v(439.14, 471) * mm});
            skLineSegment(sketch, "E1583", {"start": v(439.14, 471) * mm, "end": v(438.72, 471.24) * mm});
            skLineSegment(sketch, "E1584", {"start": v(438.72, 471.24) * mm, "end": v(438.3, 471.5) * mm});
            skLineSegment(sketch, "E1585", {"start": v(438.3, 471.5) * mm, "end": v(437.9, 471.76) * mm});
            skLineSegment(sketch, "E1586", {"start": v(437.9, 471.76) * mm, "end": v(437.5, 472.03) * mm});
            skLineSegment(sketch, "E1587", {"start": v(437.5, 472.03) * mm, "end": v(437.1, 472.32) * mm});
            skLineSegment(sketch, "E1588", {"start": v(437.1, 472.32) * mm, "end": v(436.71, 472.6) * mm});
            skLineSegment(sketch, "E1589", {"start": v(436.71, 472.6) * mm, "end": v(436.33, 472.91) * mm});
            skLineSegment(sketch, "E1590", {"start": v(436.33, 472.91) * mm, "end": v(435.95, 473.23) * mm});
            skLineSegment(sketch, "E1591", {"start": v(435.95, 473.23) * mm, "end": v(435.59, 473.55) * mm});
            skLineSegment(sketch, "E1592", {"start": v(435.59, 473.55) * mm, "end": v(435.23, 473.88) * mm});
            skLineSegment(sketch, "E1593", {"start": v(435.23, 473.88) * mm, "end": v(434.97, 474.13) * mm});
            skLineSegment(sketch, "E1594", {"start": v(434.97, 474.13) * mm, "end": v(434.72, 474.4) * mm});
            skLineSegment(sketch, "E1595", {"start": v(434.72, 474.4) * mm, "end": v(434.48, 474.65) * mm});
            skLineSegment(sketch, "E1596", {"start": v(434.48, 474.65) * mm, "end": v(434.25, 474.92) * mm});
            skLineSegment(sketch, "E1597", {"start": v(434.25, 474.92) * mm, "end": v(434.03, 475.2) * mm});
            skLineSegment(sketch, "E1598", {"start": v(434.03, 475.2) * mm, "end": v(433.8, 475.47) * mm});
            skLineSegment(sketch, "E1599", {"start": v(433.8, 475.47) * mm, "end": v(433.6, 475.76) * mm});
            skLineSegment(sketch, "E1600", {"start": v(433.6, 475.76) * mm, "end": v(433.4, 476.04) * mm});
            skLineSegment(sketch, "E1601", {"start": v(433.4, 476.04) * mm, "end": v(433.2, 476.34) * mm});
            skLineSegment(sketch, "E1602", {"start": v(433.2, 476.34) * mm, "end": v(433.01, 476.63) * mm});
            skLineSegment(sketch, "E1603", {"start": v(433.01, 476.63) * mm, "end": v(432.84, 476.94) * mm});
            skLineSegment(sketch, "E1604", {"start": v(432.84, 476.94) * mm, "end": v(432.66, 477.24) * mm});
            skLineSegment(sketch, "E1605", {"start": v(432.66, 477.24) * mm, "end": v(432.5, 477.55) * mm});
            skLineSegment(sketch, "E1606", {"start": v(432.5, 477.55) * mm, "end": v(432.34, 477.87) * mm});
            skLineSegment(sketch, "E1607", {"start": v(432.34, 477.87) * mm, "end": v(432.2, 478.19) * mm});
            skLineSegment(sketch, "E1608", {"start": v(432.2, 478.19) * mm, "end": v(432.06, 478.51) * mm});
            skLineSegment(sketch, "E1609", {"start": v(432.06, 478.51) * mm, "end": v(431.93, 478.84) * mm});
            skLineSegment(sketch, "E1610", {"start": v(431.93, 478.84) * mm, "end": v(431.8, 479.16) * mm});
            skLineSegment(sketch, "E1611", {"start": v(431.8, 479.16) * mm, "end": v(431.7, 479.5) * mm});
            skLineSegment(sketch, "E1612", {"start": v(431.7, 479.5) * mm, "end": v(431.59, 479.83) * mm});
            skLineSegment(sketch, "E1613", {"start": v(431.59, 479.83) * mm, "end": v(431.49, 480.17) * mm});
            skLineSegment(sketch, "E1614", {"start": v(431.49, 480.17) * mm, "end": v(431.4, 480.5) * mm});
            skLineSegment(sketch, "E1615", {"start": v(431.4, 480.5) * mm, "end": v(431.32, 480.85) * mm});
            skLineSegment(sketch, "E1616", {"start": v(431.32, 480.85) * mm, "end": v(431.25, 481.2) * mm});
            skLineSegment(sketch, "E1617", {"start": v(431.25, 481.2) * mm, "end": v(431.19, 481.54) * mm});
            skLineSegment(sketch, "E1618", {"start": v(431.19, 481.54) * mm, "end": v(431.13, 481.9) * mm});
            skLineSegment(sketch, "E1619", {"start": v(431.13, 481.9) * mm, "end": v(431.09, 482.24) * mm});
            skLineSegment(sketch, "E1620", {"start": v(431.09, 482.24) * mm, "end": v(431.05, 482.6) * mm});
            skLineSegment(sketch, "E1621", {"start": v(431.05, 482.6) * mm, "end": v(431.03, 482.95) * mm});
            skLineSegment(sketch, "E1622", {"start": v(431.03, 482.95) * mm, "end": v(431, 483.3) * mm});
            skLineSegment(sketch, "E1623", {"start": v(431, 483.3) * mm, "end": v(431, 483.66) * mm});
            skLineSegment(sketch, "E1624", {"start": v(431, 483.66) * mm, "end": v(431, 484.02) * mm});
            skLineSegment(sketch, "E1625", {"start": v(431, 484.02) * mm, "end": v(431, 484.38) * mm});
            skLineSegment(sketch, "E1626", {"start": v(431, 484.38) * mm, "end": v(431.02, 484.74) * mm});
            skLineSegment(sketch, "E1627", {"start": v(431.02, 484.74) * mm, "end": v(431.04, 485.1) * mm});
            skLineSegment(sketch, "E1628", {"start": v(431.04, 485.1) * mm, "end": v(431.07, 485.46) * mm});
            skLineSegment(sketch, "E1629", {"start": v(431.07, 485.46) * mm, "end": v(431.11, 485.82) * mm});
            skLineSegment(sketch, "E1630", {"start": v(431.11, 485.82) * mm, "end": v(431.16, 486.17) * mm});
            skLineSegment(sketch, "E1631", {"start": v(431.16, 486.17) * mm, "end": v(431.22, 486.53) * mm});
            skLineSegment(sketch, "E1632", {"start": v(431.22, 486.53) * mm, "end": v(431.29, 486.88) * mm});
            skLineSegment(sketch, "E1633", {"start": v(431.29, 486.88) * mm, "end": v(431.37, 487.23) * mm});
            skLineSegment(sketch, "E1634", {"start": v(431.37, 487.23) * mm, "end": v(431.45, 487.58) * mm});
            skLineSegment(sketch, "E1635", {"start": v(431.45, 487.58) * mm, "end": v(431.55, 487.92) * mm});
            skLineSegment(sketch, "E1636", {"start": v(431.55, 487.92) * mm, "end": v(431.65, 488.26) * mm});
            skLineSegment(sketch, "E1637", {"start": v(431.65, 488.26) * mm, "end": v(431.76, 488.6) * mm});
            skLineSegment(sketch, "E1638", {"start": v(431.76, 488.6) * mm, "end": v(431.88, 488.94) * mm});
            skLineSegment(sketch, "E1639", {"start": v(431.88, 488.94) * mm, "end": v(432, 489.27) * mm});
            skLineSegment(sketch, "E1640", {"start": v(432, 489.27) * mm, "end": v(432.15, 489.6) * mm});
            skLineSegment(sketch, "E1641", {"start": v(432.15, 489.6) * mm, "end": v(432.3, 489.92) * mm});
            skLineSegment(sketch, "E1642", {"start": v(432.3, 489.92) * mm, "end": v(432.44, 490.25) * mm});
            skLineSegment(sketch, "E1643", {"start": v(432.44, 490.25) * mm, "end": v(432.6, 490.56) * mm});
            skLineSegment(sketch, "E1644", {"start": v(432.6, 490.56) * mm, "end": v(432.78, 490.88) * mm});
            skLineSegment(sketch, "E1645", {"start": v(432.78, 490.88) * mm, "end": v(432.95, 491.19) * mm});
            skLineSegment(sketch, "E1646", {"start": v(432.95, 491.19) * mm, "end": v(433.14, 491.5) * mm});
            skLineSegment(sketch, "E1647", {"start": v(433.14, 491.5) * mm, "end": v(433.33, 491.8) * mm});
            skLineSegment(sketch, "E1648", {"start": v(433.33, 491.8) * mm, "end": v(433.54, 492.09) * mm});
            skLineSegment(sketch, "E1649", {"start": v(433.54, 492.09) * mm, "end": v(433.75, 492.38) * mm});
            skLineSegment(sketch, "E1650", {"start": v(433.75, 492.38) * mm, "end": v(433.96, 492.67) * mm});
            skLineSegment(sketch, "E1651", {"start": v(433.96, 492.67) * mm, "end": v(434.19, 492.95) * mm});
            skLineSegment(sketch, "E1652", {"start": v(434.19, 492.95) * mm, "end": v(434.42, 493.22) * mm});
            skLineSegment(sketch, "E1653", {"start": v(434.42, 493.22) * mm, "end": v(434.66, 493.5) * mm});
            skLineSegment(sketch, "E1654", {"start": v(434.66, 493.5) * mm, "end": v(434.9, 493.75) * mm});
            skLineSegment(sketch, "E1655", {"start": v(434.9, 493.75) * mm, "end": v(435.16, 494.01) * mm});
            skLineSegment(sketch, "E1656", {"start": v(435.16, 494.01) * mm, "end": v(435.42, 494.26) * mm});
            skLineSegment(sketch, "E1657", {"start": v(435.42, 494.26) * mm, "end": v(435.78, 494.59) * mm});
            skLineSegment(sketch, "E1658", {"start": v(435.78, 494.59) * mm, "end": v(436.15, 494.9) * mm});
            skLineSegment(sketch, "E1659", {"start": v(436.15, 494.9) * mm, "end": v(436.52, 495.2) * mm});
            skLineSegment(sketch, "E1660", {"start": v(436.52, 495.2) * mm, "end": v(436.9, 495.5) * mm});
            skLineSegment(sketch, "E1661", {"start": v(436.9, 495.5) * mm, "end": v(437.29, 495.78) * mm});
            skLineSegment(sketch, "E1662", {"start": v(437.29, 495.78) * mm, "end": v(437.68, 496.06) * mm});
            skLineSegment(sketch, "E1663", {"start": v(437.68, 496.06) * mm, "end": v(438.08, 496.32) * mm});
            skLineSegment(sketch, "E1664", {"start": v(438.08, 496.32) * mm, "end": v(438.48, 496.57) * mm});
            skLineSegment(sketch, "E1665", {"start": v(438.48, 496.57) * mm, "end": v(438.9, 496.82) * mm});
            skLineSegment(sketch, "E1666", {"start": v(438.9, 496.82) * mm, "end": v(439.3, 497.05) * mm});
            skLineSegment(sketch, "E1667", {"start": v(439.3, 497.05) * mm, "end": v(439.73, 497.27) * mm});
            skLineSegment(sketch, "E1668", {"start": v(439.73, 497.27) * mm, "end": v(440.16, 497.48) * mm});
            skLineSegment(sketch, "E1669", {"start": v(440.16, 497.48) * mm, "end": v(440.59, 497.69) * mm});
            skLineSegment(sketch, "E1670", {"start": v(440.59, 497.69) * mm, "end": v(441.03, 497.88) * mm});
            skLineSegment(sketch, "E1671", {"start": v(441.03, 497.88) * mm, "end": v(441.47, 498.05) * mm});
            skLineSegment(sketch, "E1672", {"start": v(441.47, 498.05) * mm, "end": v(441.91, 498.22) * mm});
            skLineSegment(sketch, "E1673", {"start": v(441.91, 498.22) * mm, "end": v(442.36, 498.38) * mm});
            skLineSegment(sketch, "E1674", {"start": v(442.36, 498.38) * mm, "end": v(442.81, 498.53) * mm});
            skLineSegment(sketch, "E1675", {"start": v(442.81, 498.53) * mm, "end": v(443.27, 498.66) * mm});
            skLineSegment(sketch, "E1676", {"start": v(443.27, 498.66) * mm, "end": v(443.73, 498.79) * mm});
            skLineSegment(sketch, "E1677", {"start": v(443.73, 498.79) * mm, "end": v(444.2, 498.9) * mm});
            skLineSegment(sketch, "E1678", {"start": v(444.2, 498.9) * mm, "end": v(444.66, 499) * mm});
            skLineSegment(sketch, "E1679", {"start": v(444.66, 499) * mm, "end": v(445.13, 499.09) * mm});
            skLineSegment(sketch, "E1680", {"start": v(445.13, 499.09) * mm, "end": v(445.6, 499.17) * mm});
            skLineSegment(sketch, "E1681", {"start": v(445.6, 499.17) * mm, "end": v(446.07, 499.23) * mm});
            skLineSegment(sketch, "E1682", {"start": v(446.07, 499.23) * mm, "end": v(446.55, 499.29) * mm});
            skLineSegment(sketch, "E1683", {"start": v(446.55, 499.29) * mm, "end": v(447.02, 499.33) * mm});
            skLineSegment(sketch, "E1684", {"start": v(447.02, 499.33) * mm, "end": v(447.5, 499.36) * mm});
            skLineSegment(sketch, "E1685", {"start": v(447.5, 499.36) * mm, "end": v(447.98, 499.38) * mm});
            skLineSegment(sketch, "E1686", {"start": v(447.98, 499.38) * mm, "end": v(448.46, 499.39) * mm});
            skLineSegment(sketch, "E1687", {"start": v(448.46, 499.39) * mm, "end": v(448.95, 499.38) * mm});
            skLineSegment(sketch, "E1688", {"start": v(448.95, 499.38) * mm, "end": v(449.43, 499.37) * mm});
            skLineSegment(sketch, "E1689", {"start": v(449.43, 499.37) * mm, "end": v(449.88, 499.37) * mm});
            skLineSegment(sketch, "E1690", {"start": v(449.88, 499.37) * mm, "end": v(450.33, 499.37) * mm});
            skLineSegment(sketch, "E1691", {"start": v(450.33, 499.37) * mm, "end": v(450.78, 499.35) * mm});
            skLineSegment(sketch, "E1692", {"start": v(450.78, 499.35) * mm, "end": v(451.22, 499.33) * mm});
            skLineSegment(sketch, "E1693", {"start": v(451.22, 499.33) * mm, "end": v(451.67, 499.3) * mm});
            skLineSegment(sketch, "E1694", {"start": v(451.67, 499.3) * mm, "end": v(452.11, 499.24) * mm});
            skLineSegment(sketch, "E1695", {"start": v(452.11, 499.24) * mm, "end": v(452.56, 499.18) * mm});
            skLineSegment(sketch, "E1696", {"start": v(452.56, 499.18) * mm, "end": v(453, 499.11) * mm});
            skLineSegment(sketch, "E1697", {"start": v(453, 499.11) * mm, "end": v(453.43, 499.03) * mm});
            skLineSegment(sketch, "E1698", {"start": v(453.43, 499.03) * mm, "end": v(453.87, 498.94) * mm});
            skLineSegment(sketch, "E1699", {"start": v(453.87, 498.94) * mm, "end": v(454.3, 498.83) * mm});
            skLineSegment(sketch, "E1700", {"start": v(454.3, 498.83) * mm, "end": v(454.73, 498.72) * mm});
            skLineSegment(sketch, "E1701", {"start": v(454.73, 498.72) * mm, "end": v(455.16, 498.6) * mm});
            skLineSegment(sketch, "E1702", {"start": v(455.16, 498.6) * mm, "end": v(455.58, 498.46) * mm});
            skLineSegment(sketch, "E1703", {"start": v(455.58, 498.46) * mm, "end": v(456, 498.31) * mm});
            skLineSegment(sketch, "E1704", {"start": v(456, 498.31) * mm, "end": v(456.42, 498.16) * mm});
            skLineSegment(sketch, "E1705", {"start": v(456.42, 498.16) * mm, "end": v(456.83, 498) * mm});
            skLineSegment(sketch, "E1706", {"start": v(456.83, 498) * mm, "end": v(457.23, 497.81) * mm});
            skLineSegment(sketch, "E1707", {"start": v(457.23, 497.81) * mm, "end": v(457.64, 497.63) * mm});
            skLineSegment(sketch, "E1708", {"start": v(457.64, 497.63) * mm, "end": v(458.04, 497.43) * mm});
            skLineSegment(sketch, "E1709", {"start": v(458.04, 497.43) * mm, "end": v(458.43, 497.23) * mm});
            skLineSegment(sketch, "E1710", {"start": v(458.43, 497.23) * mm, "end": v(458.82, 497) * mm});
            skLineSegment(sketch, "E1711", {"start": v(458.82, 497) * mm, "end": v(459.2, 496.78) * mm});
            skLineSegment(sketch, "E1712", {"start": v(459.2, 496.78) * mm, "end": v(459.58, 496.55) * mm});
            skLineSegment(sketch, "E1713", {"start": v(459.58, 496.55) * mm, "end": v(459.95, 496.3) * mm});
            skLineSegment(sketch, "E1714", {"start": v(459.95, 496.3) * mm, "end": v(460.32, 496.05) * mm});
            skLineSegment(sketch, "E1715", {"start": v(460.32, 496.05) * mm, "end": v(460.68, 495.78) * mm});
            skLineSegment(sketch, "E1716", {"start": v(460.68, 495.78) * mm, "end": v(461.03, 495.51) * mm});
            skLineSegment(sketch, "E1717", {"start": v(461.03, 495.51) * mm, "end": v(461.38, 495.23) * mm});
            skLineSegment(sketch, "E1718", {"start": v(461.38, 495.23) * mm, "end": v(461.72, 494.94) * mm});
            skLineSegment(sketch, "E1719", {"start": v(461.72, 494.94) * mm, "end": v(462.05, 494.63) * mm});
            skLineSegment(sketch, "E1720", {"start": v(462.05, 494.63) * mm, "end": v(462.38, 494.32) * mm});
            skLineSegment(sketch, "E1721", {"start": v(462.38, 494.32) * mm, "end": v(462.64, 494.07) * mm});
            skLineSegment(sketch, "E1722", {"start": v(462.64, 494.07) * mm, "end": v(462.88, 493.8) * mm});
            skLineSegment(sketch, "E1723", {"start": v(462.88, 493.8) * mm, "end": v(463.12, 493.54) * mm});
            skLineSegment(sketch, "E1724", {"start": v(463.12, 493.54) * mm, "end": v(463.36, 493.26) * mm});
            skLineSegment(sketch, "E1725", {"start": v(463.36, 493.26) * mm, "end": v(463.58, 492.98) * mm});
            skLineSegment(sketch, "E1726", {"start": v(463.58, 492.98) * mm, "end": v(463.8, 492.7) * mm});
            skLineSegment(sketch, "E1727", {"start": v(463.8, 492.7) * mm, "end": v(464.01, 492.4) * mm});
            skLineSegment(sketch, "E1728", {"start": v(464.01, 492.4) * mm, "end": v(464.22, 492.11) * mm});
            skLineSegment(sketch, "E1729", {"start": v(464.22, 492.11) * mm, "end": v(464.41, 491.81) * mm});
            skLineSegment(sketch, "E1730", {"start": v(464.41, 491.81) * mm, "end": v(464.6, 491.5) * mm});
            skLineSegment(sketch, "E1731", {"start": v(464.6, 491.5) * mm, "end": v(464.78, 491.2) * mm});
            skLineSegment(sketch, "E1732", {"start": v(464.78, 491.2) * mm, "end": v(464.95, 490.89) * mm});
            skLineSegment(sketch, "E1733", {"start": v(464.95, 490.89) * mm, "end": v(465.12, 490.57) * mm});
            skLineSegment(sketch, "E1734", {"start": v(465.12, 490.57) * mm, "end": v(465.28, 490.25) * mm});
            skLineSegment(sketch, "E1735", {"start": v(465.28, 490.25) * mm, "end": v(465.43, 489.93) * mm});
            skLineSegment(sketch, "E1736", {"start": v(465.43, 489.93) * mm, "end": v(465.57, 489.6) * mm});
            skLineSegment(sketch, "E1737", {"start": v(465.57, 489.6) * mm, "end": v(465.7, 489.27) * mm});
            skLineSegment(sketch, "E1738", {"start": v(465.7, 489.27) * mm, "end": v(465.82, 488.93) * mm});
            skLineSegment(sketch, "E1739", {"start": v(465.82, 488.93) * mm, "end": v(465.94, 488.6) * mm});
            skLineSegment(sketch, "E1740", {"start": v(465.94, 488.6) * mm, "end": v(466.05, 488.26) * mm});
            skLineSegment(sketch, "E1741", {"start": v(466.05, 488.26) * mm, "end": v(466.15, 487.91) * mm});
            skLineSegment(sketch, "E1742", {"start": v(466.15, 487.91) * mm, "end": v(466.24, 487.57) * mm});
            skLineSegment(sketch, "E1743", {"start": v(466.24, 487.57) * mm, "end": v(466.32, 487.22) * mm});
            skLineSegment(sketch, "E1744", {"start": v(466.32, 487.22) * mm, "end": v(466.4, 486.87) * mm});
            skLineSegment(sketch, "E1745", {"start": v(466.4, 486.87) * mm, "end": v(466.46, 486.52) * mm});
            skLineSegment(sketch, "E1746", {"start": v(466.46, 486.52) * mm, "end": v(466.52, 486.16) * mm});
            skLineSegment(sketch, "E1747", {"start": v(466.52, 486.16) * mm, "end": v(466.56, 485.8) * mm});
            skLineSegment(sketch, "E1748", {"start": v(466.56, 485.8) * mm, "end": v(466.6, 485.45) * mm});
            skLineSegment(sketch, "E1749", {"start": v(466.6, 485.45) * mm, "end": v(466.63, 485.1) * mm});
            skLineSegment(sketch, "E1750", {"start": v(466.63, 485.1) * mm, "end": v(466.65, 484.73) * mm});
            skLineSegment(sketch, "E1751", {"start": v(466.65, 484.73) * mm, "end": v(466.67, 484.37) * mm});
            skLineSegment(sketch, "E1752", {"start": v(466.67, 484.37) * mm, "end": v(466.67, 484) * mm});
            skLineSegment(sketch, "E1753", {"start": v(466.18, 507.26) * mm, "end": v(431.21, 507.26) * mm});
            skLineSegment(sketch, "E1754", {"start": v(431.21, 507.26) * mm, "end": v(431.21, 522.63) * mm});
            skLineSegment(sketch, "E1755", {"start": v(431.21, 522.63) * mm, "end": v(431.22, 523.06) * mm});
            skLineSegment(sketch, "E1756", {"start": v(431.22, 523.06) * mm, "end": v(431.24, 523.49) * mm});
            skLineSegment(sketch, "E1757", {"start": v(431.24, 523.49) * mm, "end": v(431.29, 523.92) * mm});
            skLineSegment(sketch, "E1758", {"start": v(431.29, 523.92) * mm, "end": v(431.36, 524.34) * mm});
            skLineSegment(sketch, "E1759", {"start": v(431.36, 524.34) * mm, "end": v(431.45, 524.76) * mm});
            skLineSegment(sketch, "E1760", {"start": v(431.45, 524.76) * mm, "end": v(431.56, 525.17) * mm});
            skLineSegment(sketch, "E1761", {"start": v(431.56, 525.17) * mm, "end": v(431.7, 525.57) * mm});
            skLineSegment(sketch, "E1762", {"start": v(431.7, 525.57) * mm, "end": v(431.84, 525.97) * mm});
            skLineSegment(sketch, "E1763", {"start": v(431.84, 525.97) * mm, "end": v(432.02, 526.36) * mm});
            skLineSegment(sketch, "E1764", {"start": v(432.02, 526.36) * mm, "end": v(432.2, 526.74) * mm});
            skLineSegment(sketch, "E1765", {"start": v(432.2, 526.74) * mm, "end": v(432.42, 527.11) * mm});
            skLineSegment(sketch, "E1766", {"start": v(432.42, 527.11) * mm, "end": v(432.65, 527.47) * mm});
            skLineSegment(sketch, "E1767", {"start": v(432.65, 527.47) * mm, "end": v(432.9, 527.82) * mm});
            skLineSegment(sketch, "E1768", {"start": v(432.9, 527.82) * mm, "end": v(433.16, 528.16) * mm});
            skLineSegment(sketch, "E1769", {"start": v(433.16, 528.16) * mm, "end": v(433.45, 528.48) * mm});
            skLineSegment(sketch, "E1770", {"start": v(433.45, 528.48) * mm, "end": v(433.75, 528.79) * mm});
            skLineSegment(sketch, "E1771", {"start": v(433.75, 528.79) * mm, "end": v(434.06, 529.09) * mm});
            skLineSegment(sketch, "E1772", {"start": v(434.06, 529.09) * mm, "end": v(434.38, 529.37) * mm});
            skLineSegment(sketch, "E1773", {"start": v(434.38, 529.37) * mm, "end": v(434.71, 529.63) * mm});
            skLineSegment(sketch, "E1774", {"start": v(434.71, 529.63) * mm, "end": v(435.06, 529.88) * mm});
            skLineSegment(sketch, "E1775", {"start": v(435.06, 529.88) * mm, "end": v(435.42, 530.1) * mm});
            skLineSegment(sketch, "E1776", {"start": v(435.42, 530.1) * mm, "end": v(435.78, 530.31) * mm});
            skLineSegment(sketch, "E1777", {"start": v(435.78, 530.31) * mm, "end": v(436.16, 530.5) * mm});
            skLineSegment(sketch, "E1778", {"start": v(436.16, 530.5) * mm, "end": v(436.55, 530.68) * mm});
            skLineSegment(sketch, "E1779", {"start": v(436.55, 530.68) * mm, "end": v(436.94, 530.83) * mm});
            skLineSegment(sketch, "E1780", {"start": v(436.94, 530.83) * mm, "end": v(437.34, 530.97) * mm});
            skLineSegment(sketch, "E1781", {"start": v(437.34, 530.97) * mm, "end": v(437.75, 531.08) * mm});
            skLineSegment(sketch, "E1782", {"start": v(437.75, 531.08) * mm, "end": v(438.16, 531.17) * mm});
            skLineSegment(sketch, "E1783", {"start": v(438.16, 531.17) * mm, "end": v(438.58, 531.25) * mm});
            skLineSegment(sketch, "E1784", {"start": v(438.58, 531.25) * mm, "end": v(439, 531.3) * mm});
            skLineSegment(sketch, "E1785", {"start": v(439, 531.3) * mm, "end": v(439.43, 531.33) * mm});
            skLineSegment(sketch, "E1786", {"start": v(439.43, 531.33) * mm, "end": v(439.86, 531.34) * mm});
            skLineSegment(sketch, "E1787", {"start": v(439.86, 531.34) * mm, "end": v(440.3, 531.34) * mm});
            skLineSegment(sketch, "E1788", {"start": v(440.3, 531.34) * mm, "end": v(440.73, 531.32) * mm});
            skLineSegment(sketch, "E1789", {"start": v(440.73, 531.32) * mm, "end": v(441.16, 531.28) * mm});
            skLineSegment(sketch, "E1790", {"start": v(441.16, 531.28) * mm, "end": v(441.6, 531.22) * mm});
            skLineSegment(sketch, "E1791", {"start": v(441.6, 531.22) * mm, "end": v(442.02, 531.13) * mm});
            skLineSegment(sketch, "E1792", {"start": v(442.02, 531.13) * mm, "end": v(442.44, 531.02) * mm});
            skLineSegment(sketch, "E1793", {"start": v(442.44, 531.02) * mm, "end": v(442.85, 530.9) * mm});
            skLineSegment(sketch, "E1794", {"start": v(442.85, 530.9) * mm, "end": v(443.26, 530.75) * mm});
            skLineSegment(sketch, "E1795", {"start": v(443.26, 530.75) * mm, "end": v(443.66, 530.58) * mm});
            skLineSegment(sketch, "E1796", {"start": v(443.66, 530.58) * mm, "end": v(444.05, 530.4) * mm});
            skLineSegment(sketch, "E1797", {"start": v(444.05, 530.4) * mm, "end": v(444.43, 530.18) * mm});
            skLineSegment(sketch, "E1798", {"start": v(444.43, 530.18) * mm, "end": v(444.8, 529.95) * mm});
            skLineSegment(sketch, "E1799", {"start": v(444.8, 529.95) * mm, "end": v(445.15, 529.7) * mm});
            skLineSegment(sketch, "E1800", {"start": v(445.15, 529.7) * mm, "end": v(445.5, 529.44) * mm});
            skLineSegment(sketch, "E1801", {"start": v(445.5, 529.44) * mm, "end": v(445.83, 529.16) * mm});
            skLineSegment(sketch, "E1802", {"start": v(445.83, 529.16) * mm, "end": v(446.15, 528.86) * mm});
            skLineSegment(sketch, "E1803", {"start": v(446.15, 528.86) * mm, "end": v(446.45, 528.54) * mm});
            skLineSegment(sketch, "E1804", {"start": v(446.45, 528.54) * mm, "end": v(446.74, 528.21) * mm});
            skLineSegment(sketch, "E1805", {"start": v(446.74, 528.21) * mm, "end": v(447, 527.87) * mm});
            skLineSegment(sketch, "E1806", {"start": v(447, 527.87) * mm, "end": v(447.25, 527.52) * mm});
            skLineSegment(sketch, "E1807", {"start": v(447.25, 527.52) * mm, "end": v(447.48, 527.15) * mm});
            skLineSegment(sketch, "E1808", {"start": v(447.48, 527.15) * mm, "end": v(447.69, 526.78) * mm});
            skLineSegment(sketch, "E1809", {"start": v(447.69, 526.78) * mm, "end": v(447.88, 526.4) * mm});
            skLineSegment(sketch, "E1810", {"start": v(447.88, 526.4) * mm, "end": v(448.05, 526) * mm});
            skLineSegment(sketch, "E1811", {"start": v(448.05, 526) * mm, "end": v(448.2, 525.6) * mm});
            skLineSegment(sketch, "E1812", {"start": v(448.2, 525.6) * mm, "end": v(448.34, 525.19) * mm});
            skLineSegment(sketch, "E1813", {"start": v(448.34, 525.19) * mm, "end": v(448.45, 524.77) * mm});
            skLineSegment(sketch, "E1814", {"start": v(448.45, 524.77) * mm, "end": v(448.54, 524.35) * mm});
            skLineSegment(sketch, "E1815", {"start": v(448.54, 524.35) * mm, "end": v(448.6, 523.92) * mm});
            skLineSegment(sketch, "E1816", {"start": v(448.6, 523.92) * mm, "end": v(448.66, 523.5) * mm});
            skLineSegment(sketch, "E1817", {"start": v(448.66, 523.5) * mm, "end": v(448.68, 523.06) * mm});
            skLineSegment(sketch, "E1818", {"start": v(448.68, 523.06) * mm, "end": v(448.69, 522.63) * mm});
            skLineSegment(sketch, "E1819", {"start": v(448.69, 522.63) * mm, "end": v(448.69, 507.26) * mm});
            skLineSegment(sketch, "E1820", {"start": v(448.69, 522.63) * mm, "end": v(448.69, 522.98) * mm});
            skLineSegment(sketch, "E1821", {"start": v(448.69, 522.98) * mm, "end": v(448.7, 523.34) * mm});
            skLineSegment(sketch, "E1822", {"start": v(448.7, 523.34) * mm, "end": v(448.75, 523.7) * mm});
            skLineSegment(sketch, "E1823", {"start": v(448.75, 523.7) * mm, "end": v(448.8, 524.05) * mm});
            skLineSegment(sketch, "E1824", {"start": v(448.8, 524.05) * mm, "end": v(448.88, 524.4) * mm});
            skLineSegment(sketch, "E1825", {"start": v(448.88, 524.4) * mm, "end": v(448.97, 524.73) * mm});
            skLineSegment(sketch, "E1826", {"start": v(448.97, 524.73) * mm, "end": v(449.08, 525.07) * mm});
            skLineSegment(sketch, "E1827", {"start": v(449.08, 525.07) * mm, "end": v(449.2, 525.4) * mm});
            skLineSegment(sketch, "E1828", {"start": v(449.2, 525.4) * mm, "end": v(449.34, 525.72) * mm});
            skLineSegment(sketch, "E1829", {"start": v(449.34, 525.72) * mm, "end": v(449.5, 526.04) * mm});
            skLineSegment(sketch, "E1830", {"start": v(449.5, 526.04) * mm, "end": v(449.67, 526.35) * mm});
            skLineSegment(sketch, "E1831", {"start": v(449.67, 526.35) * mm, "end": v(449.86, 526.65) * mm});
            skLineSegment(sketch, "E1832", {"start": v(449.86, 526.65) * mm, "end": v(450.07, 526.94) * mm});
            skLineSegment(sketch, "E1833", {"start": v(450.07, 526.94) * mm, "end": v(450.29, 527.22) * mm});
            skLineSegment(sketch, "E1834", {"start": v(450.29, 527.22) * mm, "end": v(450.52, 527.49) * mm});
            skLineSegment(sketch, "E1835", {"start": v(450.52, 527.49) * mm, "end": v(450.77, 527.75) * mm});
            skLineSegment(sketch, "E1836", {"start": v(450.77, 527.75) * mm, "end": v(451.21, 528.04) * mm});
            skLineSegment(sketch, "E1837", {"start": v(451.21, 528.04) * mm, "end": v(451.66, 528.32) * mm});
            skLineSegment(sketch, "E1838", {"start": v(451.66, 528.32) * mm, "end": v(452.12, 528.58) * mm});
            skLineSegment(sketch, "E1839", {"start": v(452.12, 528.58) * mm, "end": v(452.59, 528.81) * mm});
            skLineSegment(sketch, "E1840", {"start": v(452.59, 528.81) * mm, "end": v(453.07, 529.03) * mm});
            skLineSegment(sketch, "E1841", {"start": v(453.07, 529.03) * mm, "end": v(453.56, 529.22) * mm});
            skLineSegment(sketch, "E1842", {"start": v(453.56, 529.22) * mm, "end": v(454.05, 529.39) * mm});
            skLineSegment(sketch, "E1843", {"start": v(454.05, 529.39) * mm, "end": v(454.55, 529.54) * mm});
            skLineSegment(sketch, "E1844", {"start": v(454.55, 529.54) * mm, "end": v(455.06, 529.66) * mm});
            skLineSegment(sketch, "E1845", {"start": v(455.06, 529.66) * mm, "end": v(455.58, 529.77) * mm});
            skLineSegment(sketch, "E1846", {"start": v(455.58, 529.77) * mm, "end": v(456.1, 529.85) * mm});
            skLineSegment(sketch, "E1847", {"start": v(456.1, 529.85) * mm, "end": v(456.62, 529.9) * mm});
            skLineSegment(sketch, "E1848", {"start": v(456.62, 529.9) * mm, "end": v(457.14, 529.94) * mm});
            skLineSegment(sketch, "E1849", {"start": v(457.14, 529.94) * mm, "end": v(457.67, 529.95) * mm});
            skLineSegment(sketch, "E1850", {"start": v(457.67, 529.95) * mm, "end": v(458.2, 529.94) * mm});
            skLineSegment(sketch, "E1851", {"start": v(458.2, 529.94) * mm, "end": v(458.72, 529.9) * mm});
            skLineSegment(sketch, "E1852", {"start": v(458.72, 529.9) * mm, "end": v(459.2, 529.9) * mm});
            skLineSegment(sketch, "E1853", {"start": v(459.2, 529.9) * mm, "end": v(459.66, 529.9) * mm});
            skLineSegment(sketch, "E1854", {"start": v(459.66, 529.9) * mm, "end": v(460.13, 529.9) * mm});
            skLineSegment(sketch, "E1855", {"start": v(460.13, 529.9) * mm, "end": v(460.6, 529.92) * mm});
            skLineSegment(sketch, "E1856", {"start": v(460.6, 529.92) * mm, "end": v(461.08, 529.95) * mm});
            skLineSegment(sketch, "E1857", {"start": v(461.08, 529.95) * mm, "end": v(461.55, 529.98) * mm});
            skLineSegment(sketch, "E1858", {"start": v(461.55, 529.98) * mm, "end": v(462.01, 530.03) * mm});
            skLineSegment(sketch, "E1859", {"start": v(462.01, 530.03) * mm, "end": v(462.48, 530.08) * mm});
            skLineSegment(sketch, "E1860", {"start": v(462.48, 530.08) * mm, "end": v(462.95, 530.14) * mm});
            skLineSegment(sketch, "E1861", {"start": v(462.95, 530.14) * mm, "end": v(463.42, 530.21) * mm});
            skLineSegment(sketch, "E1862", {"start": v(463.42, 530.21) * mm, "end": v(463.88, 530.29) * mm});
            skLineSegment(sketch, "E1863", {"start": v(463.88, 530.29) * mm, "end": v(464.34, 530.37) * mm});
            skLineSegment(sketch, "E1864", {"start": v(464.34, 530.37) * mm, "end": v(464.8, 530.47) * mm});
            skLineSegment(sketch, "E1865", {"start": v(464.8, 530.47) * mm, "end": v(465.27, 530.57) * mm});
            skLineSegment(sketch, "E1866", {"start": v(465.27, 530.57) * mm, "end": v(465.72, 530.68) * mm});
            skLineSegment(sketch, "E1867", {"start": v(465.72, 530.68) * mm, "end": v(466.18, 530.8) * mm});
            skLineSegment(sketch, "E1868", {"start": v(453.12, 539.04) * mm, "end": v(453.12, 563.17) * mm});
            skLineSegment(sketch, "E1869", {"start": v(466.18, 570.87) * mm, "end": v(440, 570.87) * mm});
            skLineSegment(sketch, "E1870", {"start": v(431.73, 570.87) * mm, "end": v(431.29, 570.87) * mm});
            skLineSegment(sketch, "E1871", {"start": v(466.18, 578.57) * mm, "end": v(439.95, 578.57) * mm});
            skLineSegment(sketch, "E1872", {"start": v(450.2, 578.57) * mm, "end": v(449.63, 578.59) * mm});
            skLineSegment(sketch, "E1873", {"start": v(449.63, 578.59) * mm, "end": v(449.06, 578.63) * mm});
            skLineSegment(sketch, "E1874", {"start": v(449.06, 578.63) * mm, "end": v(448.5, 578.7) * mm});
            skLineSegment(sketch, "E1875", {"start": v(448.5, 578.7) * mm, "end": v(447.94, 578.8) * mm});
            skLineSegment(sketch, "E1876", {"start": v(447.94, 578.8) * mm, "end": v(447.39, 578.94) * mm});
            skLineSegment(sketch, "E1877", {"start": v(447.39, 578.94) * mm, "end": v(446.84, 579.1) * mm});
            skLineSegment(sketch, "E1878", {"start": v(446.84, 579.1) * mm, "end": v(446.3, 579.28) * mm});
            skLineSegment(sketch, "E1879", {"start": v(446.3, 579.28) * mm, "end": v(445.78, 579.49) * mm});
            skLineSegment(sketch, "E1880", {"start": v(445.78, 579.49) * mm, "end": v(445.27, 579.72) * mm});
            skLineSegment(sketch, "E1881", {"start": v(445.27, 579.72) * mm, "end": v(444.77, 579.98) * mm});
            skLineSegment(sketch, "E1882", {"start": v(444.77, 579.98) * mm, "end": v(444.28, 580.27) * mm});
            skLineSegment(sketch, "E1883", {"start": v(444.28, 580.27) * mm, "end": v(443.8, 580.58) * mm});
            skLineSegment(sketch, "E1884", {"start": v(443.8, 580.58) * mm, "end": v(443.34, 580.9) * mm});
            skLineSegment(sketch, "E1885", {"start": v(443.34, 580.9) * mm, "end": v(442.9, 581.27) * mm});
            skLineSegment(sketch, "E1886", {"start": v(442.9, 581.27) * mm, "end": v(442.47, 581.65) * mm});
            skLineSegment(sketch, "E1887", {"start": v(442.47, 581.65) * mm, "end": v(442.07, 582.05) * mm});
            skLineSegment(sketch, "E1888", {"start": v(442.07, 582.05) * mm, "end": v(441.73, 582.4) * mm});
            skLineSegment(sketch, "E1889", {"start": v(441.73, 582.4) * mm, "end": v(441.42, 582.77) * mm});
            skLineSegment(sketch, "E1890", {"start": v(441.42, 582.77) * mm, "end": v(441.13, 583.16) * mm});
            skLineSegment(sketch, "E1891", {"start": v(441.13, 583.16) * mm, "end": v(440.86, 583.55) * mm});
            skLineSegment(sketch, "E1892", {"start": v(440.86, 583.55) * mm, "end": v(440.61, 583.96) * mm});
            skLineSegment(sketch, "E1893", {"start": v(440.61, 583.96) * mm, "end": v(440.38, 584.38) * mm});
            skLineSegment(sketch, "E1894", {"start": v(440.38, 584.38) * mm, "end": v(440.17, 584.8) * mm});
            skLineSegment(sketch, "E1895", {"start": v(440.17, 584.8) * mm, "end": v(439.99, 585.25) * mm});
            skLineSegment(sketch, "E1896", {"start": v(439.99, 585.25) * mm, "end": v(439.82, 585.7) * mm});
            skLineSegment(sketch, "E1897", {"start": v(439.82, 585.7) * mm, "end": v(439.68, 586.15) * mm});
            skLineSegment(sketch, "E1898", {"start": v(439.68, 586.15) * mm, "end": v(439.56, 586.62) * mm});
            skLineSegment(sketch, "E1899", {"start": v(439.56, 586.62) * mm, "end": v(439.47, 587.08) * mm});
            skLineSegment(sketch, "E1900", {"start": v(439.47, 587.08) * mm, "end": v(439.4, 587.56) * mm});
            skLineSegment(sketch, "E1901", {"start": v(439.4, 587.56) * mm, "end": v(439.34, 588.04) * mm});
            skLineSegment(sketch, "E1902", {"start": v(439.34, 588.04) * mm, "end": v(439.32, 588.52) * mm});
            skLineSegment(sketch, "E1903", {"start": v(439.32, 588.52) * mm, "end": v(439.32, 589) * mm});
            skLineSegment(sketch, "E1904", {"start": v(439.32, 589) * mm, "end": v(439.29, 589.46) * mm});
            skLineSegment(sketch, "E1905", {"start": v(439.29, 589.46) * mm, "end": v(439.28, 589.92) * mm});
            skLineSegment(sketch, "E1906", {"start": v(439.28, 589.92) * mm, "end": v(439.3, 590.38) * mm});
            skLineSegment(sketch, "E1907", {"start": v(439.3, 590.38) * mm, "end": v(439.34, 590.84) * mm});
            skLineSegment(sketch, "E1908", {"start": v(439.34, 590.84) * mm, "end": v(439.41, 591.3) * mm});
            skLineSegment(sketch, "E1909", {"start": v(439.41, 591.3) * mm, "end": v(439.5, 591.74) * mm});
            skLineSegment(sketch, "E1910", {"start": v(439.5, 591.74) * mm, "end": v(439.61, 592.18) * mm});
            skLineSegment(sketch, "E1911", {"start": v(439.61, 592.18) * mm, "end": v(439.75, 592.62) * mm});
            skLineSegment(sketch, "E1912", {"start": v(439.75, 592.62) * mm, "end": v(439.9, 593.05) * mm});
            skLineSegment(sketch, "E1913", {"start": v(439.9, 593.05) * mm, "end": v(440.08, 593.47) * mm});
            skLineSegment(sketch, "E1914", {"start": v(440.08, 593.47) * mm, "end": v(440.28, 593.88) * mm});
            skLineSegment(sketch, "E1915", {"start": v(440.28, 593.88) * mm, "end": v(440.5, 594.28) * mm});
            skLineSegment(sketch, "E1916", {"start": v(440.5, 594.28) * mm, "end": v(440.74, 594.67) * mm});
            skLineSegment(sketch, "E1917", {"start": v(440.74, 594.67) * mm, "end": v(441, 595.04) * mm});
            skLineSegment(sketch, "E1918", {"start": v(441, 595.04) * mm, "end": v(441.29, 595.4) * mm});
            skLineSegment(sketch, "E1919", {"start": v(441.29, 595.4) * mm, "end": v(441.6, 595.76) * mm});
            skLineSegment(sketch, "E1920", {"start": v(441.6, 595.76) * mm, "end": v(441.85, 595.97) * mm});
            skLineSegment(sketch, "E1921", {"start": v(441.85, 595.97) * mm, "end": v(442.11, 596.17) * mm});
            skLineSegment(sketch, "E1922", {"start": v(442.11, 596.17) * mm, "end": v(442.38, 596.36) * mm});
            skLineSegment(sketch, "E1923", {"start": v(442.38, 596.36) * mm, "end": v(442.66, 596.54) * mm});
            skLineSegment(sketch, "E1924", {"start": v(442.66, 596.54) * mm, "end": v(442.95, 596.7) * mm});
            skLineSegment(sketch, "E1925", {"start": v(442.95, 596.7) * mm, "end": v(443.24, 596.84) * mm});
            skLineSegment(sketch, "E1926", {"start": v(443.24, 596.84) * mm, "end": v(443.54, 596.98) * mm});
            skLineSegment(sketch, "E1927", {"start": v(443.54, 596.98) * mm, "end": v(443.85, 597.1) * mm});
            skLineSegment(sketch, "E1928", {"start": v(443.85, 597.1) * mm, "end": v(444.16, 597.2) * mm});
            skLineSegment(sketch, "E1929", {"start": v(444.16, 597.2) * mm, "end": v(444.48, 597.3) * mm});
            skLineSegment(sketch, "E1930", {"start": v(444.48, 597.3) * mm, "end": v(444.8, 597.37) * mm});
            skLineSegment(sketch, "E1931", {"start": v(444.8, 597.37) * mm, "end": v(445.12, 597.43) * mm});
            skLineSegment(sketch, "E1932", {"start": v(445.12, 597.43) * mm, "end": v(445.45, 597.48) * mm});
            skLineSegment(sketch, "E1933", {"start": v(445.45, 597.48) * mm, "end": v(445.78, 597.5) * mm});
            skLineSegment(sketch, "E1934", {"start": v(445.78, 597.5) * mm, "end": v(446.1, 597.53) * mm});
            skLineSegment(sketch, "E1935", {"start": v(446.1, 597.53) * mm, "end": v(446.44, 597.53) * mm});
            skLineSegment(sketch, "E1936", {"start": v(446.44, 597.53) * mm, "end": v(466.18, 597.53) * mm});
            skLineSegment(sketch, "E1937", {"start": v(135.36, 471.67) * mm, "end": v(100.37, 471.67) * mm});
            skLineSegment(sketch, "E1938", {"start": v(100.37, 471.67) * mm, "end": v(100.37, 493.43) * mm});
            skLineSegment(sketch, "E1939", {"start": v(117.09, 471.67) * mm, "end": v(117.09, 491.86) * mm});
            skLineSegment(sketch, "E1940", {"start": v(135.34, 521.69) * mm, "end": v(135.34, 501.13) * mm});
            skLineSegment(sketch, "E1941", {"start": v(135.34, 501.13) * mm, "end": v(100.38, 501.13) * mm});
            skLineSegment(sketch, "E1942", {"start": v(135.83, 534.96) * mm, "end": v(135.83, 534.59) * mm});
            skLineSegment(sketch, "E1943", {"start": v(135.83, 534.59) * mm, "end": v(135.82, 534.22) * mm});
            skLineSegment(sketch, "E1944", {"start": v(135.82, 534.22) * mm, "end": v(135.8, 533.86) * mm});
            skLineSegment(sketch, "E1945", {"start": v(135.8, 533.86) * mm, "end": v(135.78, 533.5) * mm});
            skLineSegment(sketch, "E1946", {"start": v(135.78, 533.5) * mm, "end": v(135.75, 533.13) * mm});
            skLineSegment(sketch, "E1947", {"start": v(135.75, 533.13) * mm, "end": v(135.7, 532.77) * mm});
            skLineSegment(sketch, "E1948", {"start": v(135.7, 532.77) * mm, "end": v(135.65, 532.4) * mm});
            skLineSegment(sketch, "E1949", {"start": v(135.65, 532.4) * mm, "end": v(135.6, 532.05) * mm});
            skLineSegment(sketch, "E1950", {"start": v(135.6, 532.05) * mm, "end": v(135.52, 531.7) * mm});
            skLineSegment(sketch, "E1951", {"start": v(135.52, 531.7) * mm, "end": v(135.45, 531.34) * mm});
            skLineSegment(sketch, "E1952", {"start": v(135.45, 531.34) * mm, "end": v(135.36, 530.99) * mm});
            skLineSegment(sketch, "E1953", {"start": v(135.36, 530.99) * mm, "end": v(135.26, 530.64) * mm});
            skLineSegment(sketch, "E1954", {"start": v(135.26, 530.64) * mm, "end": v(135.16, 530.29) * mm});
            skLineSegment(sketch, "E1955", {"start": v(135.16, 530.29) * mm, "end": v(135.05, 529.95) * mm});
            skLineSegment(sketch, "E1956", {"start": v(135.05, 529.95) * mm, "end": v(134.92, 529.6) * mm});
            skLineSegment(sketch, "E1957", {"start": v(134.92, 529.6) * mm, "end": v(134.8, 529.27) * mm});
            skLineSegment(sketch, "E1958", {"start": v(134.8, 529.27) * mm, "end": v(134.66, 528.93) * mm});
            skLineSegment(sketch, "E1959", {"start": v(134.66, 528.93) * mm, "end": v(134.5, 528.6) * mm});
            skLineSegment(sketch, "E1960", {"start": v(134.5, 528.6) * mm, "end": v(134.36, 528.27) * mm});
            skLineSegment(sketch, "E1961", {"start": v(134.36, 528.27) * mm, "end": v(134.2, 527.95) * mm});
            skLineSegment(sketch, "E1962", {"start": v(134.2, 527.95) * mm, "end": v(134.02, 527.63) * mm});
            skLineSegment(sketch, "E1963", {"start": v(134.02, 527.63) * mm, "end": v(133.84, 527.31) * mm});
            skLineSegment(sketch, "E1964", {"start": v(133.84, 527.31) * mm, "end": v(133.66, 527) * mm});
            skLineSegment(sketch, "E1965", {"start": v(133.66, 527) * mm, "end": v(133.46, 526.7) * mm});
            skLineSegment(sketch, "E1966", {"start": v(133.46, 526.7) * mm, "end": v(133.26, 526.4) * mm});
            skLineSegment(sketch, "E1967", {"start": v(133.26, 526.4) * mm, "end": v(133.05, 526.1) * mm});
            skLineSegment(sketch, "E1968", {"start": v(133.05, 526.1) * mm, "end": v(132.83, 525.8) * mm});
            skLineSegment(sketch, "E1969", {"start": v(132.83, 525.8) * mm, "end": v(132.6, 525.52) * mm});
            skLineSegment(sketch, "E1970", {"start": v(132.6, 525.52) * mm, "end": v(132.37, 525.24) * mm});
            skLineSegment(sketch, "E1971", {"start": v(132.37, 525.24) * mm, "end": v(132.13, 524.96) * mm});
            skLineSegment(sketch, "E1972", {"start": v(132.13, 524.96) * mm, "end": v(131.89, 524.7) * mm});
            skLineSegment(sketch, "E1973", {"start": v(131.89, 524.7) * mm, "end": v(131.63, 524.43) * mm});
            skLineSegment(sketch, "E1974", {"start": v(131.63, 524.43) * mm, "end": v(131.3, 524.12) * mm});
            skLineSegment(sketch, "E1975", {"start": v(131.3, 524.12) * mm, "end": v(130.96, 523.82) * mm});
            skLineSegment(sketch, "E1976", {"start": v(130.96, 523.82) * mm, "end": v(130.61, 523.53) * mm});
            skLineSegment(sketch, "E1977", {"start": v(130.61, 523.53) * mm, "end": v(130.26, 523.26) * mm});
            skLineSegment(sketch, "E1978", {"start": v(130.26, 523.26) * mm, "end": v(129.9, 522.99) * mm});
            skLineSegment(sketch, "E1979", {"start": v(129.9, 522.99) * mm, "end": v(129.54, 522.73) * mm});
            skLineSegment(sketch, "E1980", {"start": v(129.54, 522.73) * mm, "end": v(129.16, 522.48) * mm});
            skLineSegment(sketch, "E1981", {"start": v(129.16, 522.48) * mm, "end": v(128.79, 522.23) * mm});
            skLineSegment(sketch, "E1982", {"start": v(128.79, 522.23) * mm, "end": v(128.4, 522) * mm});
            skLineSegment(sketch, "E1983", {"start": v(128.4, 522) * mm, "end": v(128.02, 521.78) * mm});
            skLineSegment(sketch, "E1984", {"start": v(128.02, 521.78) * mm, "end": v(127.62, 521.57) * mm});
            skLineSegment(sketch, "E1985", {"start": v(127.62, 521.57) * mm, "end": v(127.23, 521.37) * mm});
            skLineSegment(sketch, "E1986", {"start": v(127.23, 521.37) * mm, "end": v(126.83, 521.17) * mm});
            skLineSegment(sketch, "E1987", {"start": v(126.83, 521.17) * mm, "end": v(126.42, 521) * mm});
            skLineSegment(sketch, "E1988", {"start": v(126.42, 521) * mm, "end": v(126, 520.82) * mm});
            skLineSegment(sketch, "E1989", {"start": v(126, 520.82) * mm, "end": v(125.6, 520.66) * mm});
            skLineSegment(sketch, "E1990", {"start": v(125.6, 520.66) * mm, "end": v(125.17, 520.5) * mm});
            skLineSegment(sketch, "E1991", {"start": v(125.17, 520.5) * mm, "end": v(124.75, 520.36) * mm});
            skLineSegment(sketch, "E1992", {"start": v(124.75, 520.36) * mm, "end": v(124.32, 520.23) * mm});
            skLineSegment(sketch, "E1993", {"start": v(124.32, 520.23) * mm, "end": v(123.9, 520.11) * mm});
            skLineSegment(sketch, "E1994", {"start": v(123.9, 520.11) * mm, "end": v(123.46, 520) * mm});
            skLineSegment(sketch, "E1995", {"start": v(123.46, 520) * mm, "end": v(123.03, 519.9) * mm});
            skLineSegment(sketch, "E1996", {"start": v(123.03, 519.9) * mm, "end": v(122.6, 519.81) * mm});
            skLineSegment(sketch, "E1997", {"start": v(122.6, 519.81) * mm, "end": v(122.15, 519.73) * mm});
            skLineSegment(sketch, "E1998", {"start": v(122.15, 519.73) * mm, "end": v(121.7, 519.67) * mm});
            skLineSegment(sketch, "E1999", {"start": v(121.7, 519.67) * mm, "end": v(121.26, 519.6) * mm});
            skLineSegment(sketch, "E2000", {"start": v(121.26, 519.6) * mm, "end": v(120.82, 519.56) * mm});
            skLineSegment(sketch, "E2001", {"start": v(120.82, 519.56) * mm, "end": v(120.37, 519.53) * mm});
            skLineSegment(sketch, "E2002", {"start": v(120.37, 519.53) * mm, "end": v(119.92, 519.5) * mm});
            skLineSegment(sketch, "E2003", {"start": v(119.92, 519.5) * mm, "end": v(119.47, 519.5) * mm});
            skLineSegment(sketch, "E2004", {"start": v(119.47, 519.5) * mm, "end": v(119.02, 519.5) * mm});
            skLineSegment(sketch, "E2005", {"start": v(119.02, 519.5) * mm, "end": v(118.57, 519.5) * mm});
            skLineSegment(sketch, "E2006", {"start": v(118.57, 519.5) * mm, "end": v(118.08, 519.49) * mm});
            skLineSegment(sketch, "E2007", {"start": v(118.08, 519.49) * mm, "end": v(117.59, 519.49) * mm});
            skLineSegment(sketch, "E2008", {"start": v(117.59, 519.49) * mm, "end": v(117.1, 519.5) * mm});
            skLineSegment(sketch, "E2009", {"start": v(117.1, 519.5) * mm, "end": v(116.6, 519.52) * mm});
            skLineSegment(sketch, "E2010", {"start": v(116.6, 519.52) * mm, "end": v(116.12, 519.56) * mm});
            skLineSegment(sketch, "E2011", {"start": v(116.12, 519.56) * mm, "end": v(115.64, 519.6) * mm});
            skLineSegment(sketch, "E2012", {"start": v(115.64, 519.6) * mm, "end": v(115.16, 519.66) * mm});
            skLineSegment(sketch, "E2013", {"start": v(115.16, 519.66) * mm, "end": v(114.68, 519.74) * mm});
            skLineSegment(sketch, "E2014", {"start": v(114.68, 519.74) * mm, "end": v(114.2, 519.82) * mm});
            skLineSegment(sketch, "E2015", {"start": v(114.2, 519.82) * mm, "end": v(113.72, 519.91) * mm});
            skLineSegment(sketch, "E2016", {"start": v(113.72, 519.91) * mm, "end": v(113.25, 520.02) * mm});
            skLineSegment(sketch, "E2017", {"start": v(113.25, 520.02) * mm, "end": v(112.78, 520.14) * mm});
            skLineSegment(sketch, "E2018", {"start": v(112.78, 520.14) * mm, "end": v(112.31, 520.27) * mm});
            skLineSegment(sketch, "E2019", {"start": v(112.31, 520.27) * mm, "end": v(111.85, 520.41) * mm});
            skLineSegment(sketch, "E2020", {"start": v(111.85, 520.41) * mm, "end": v(111.4, 520.57) * mm});
            skLineSegment(sketch, "E2021", {"start": v(111.4, 520.57) * mm, "end": v(110.94, 520.73) * mm});
            skLineSegment(sketch, "E2022", {"start": v(110.94, 520.73) * mm, "end": v(110.49, 520.9) * mm});
            skLineSegment(sketch, "E2023", {"start": v(110.49, 520.9) * mm, "end": v(110.04, 521.1) * mm});
            skLineSegment(sketch, "E2024", {"start": v(110.04, 521.1) * mm, "end": v(109.6, 521.3) * mm});
            skLineSegment(sketch, "E2025", {"start": v(109.6, 521.3) * mm, "end": v(109.16, 521.5) * mm});
            skLineSegment(sketch, "E2026", {"start": v(109.16, 521.5) * mm, "end": v(108.73, 521.72) * mm});
            skLineSegment(sketch, "E2027", {"start": v(108.73, 521.72) * mm, "end": v(108.3, 521.95) * mm});
            skLineSegment(sketch, "E2028", {"start": v(108.3, 521.95) * mm, "end": v(107.88, 522.2) * mm});
            skLineSegment(sketch, "E2029", {"start": v(107.88, 522.2) * mm, "end": v(107.47, 522.44) * mm});
            skLineSegment(sketch, "E2030", {"start": v(107.47, 522.44) * mm, "end": v(107.06, 522.7) * mm});
            skLineSegment(sketch, "E2031", {"start": v(107.06, 522.7) * mm, "end": v(106.66, 522.98) * mm});
            skLineSegment(sketch, "E2032", {"start": v(106.66, 522.98) * mm, "end": v(106.26, 523.26) * mm});
            skLineSegment(sketch, "E2033", {"start": v(106.26, 523.26) * mm, "end": v(105.87, 523.56) * mm});
            skLineSegment(sketch, "E2034", {"start": v(105.87, 523.56) * mm, "end": v(105.49, 523.86) * mm});
            skLineSegment(sketch, "E2035", {"start": v(105.49, 523.86) * mm, "end": v(105.11, 524.17) * mm});
            skLineSegment(sketch, "E2036", {"start": v(105.11, 524.17) * mm, "end": v(104.75, 524.5) * mm});
            skLineSegment(sketch, "E2037", {"start": v(104.75, 524.5) * mm, "end": v(104.39, 524.83) * mm});
            skLineSegment(sketch, "E2038", {"start": v(104.39, 524.83) * mm, "end": v(104.13, 525.08) * mm});
            skLineSegment(sketch, "E2039", {"start": v(104.13, 525.08) * mm, "end": v(103.88, 525.34) * mm});
            skLineSegment(sketch, "E2040", {"start": v(103.88, 525.34) * mm, "end": v(103.64, 525.6) * mm});
            skLineSegment(sketch, "E2041", {"start": v(103.64, 525.6) * mm, "end": v(103.41, 525.87) * mm});
            skLineSegment(sketch, "E2042", {"start": v(103.41, 525.87) * mm, "end": v(103.19, 526.14) * mm});
            skLineSegment(sketch, "E2043", {"start": v(103.19, 526.14) * mm, "end": v(102.97, 526.42) * mm});
            skLineSegment(sketch, "E2044", {"start": v(102.97, 526.42) * mm, "end": v(102.76, 526.7) * mm});
            skLineSegment(sketch, "E2045", {"start": v(102.76, 526.7) * mm, "end": v(102.56, 527) * mm});
            skLineSegment(sketch, "E2046", {"start": v(102.56, 527) * mm, "end": v(102.36, 527.28) * mm});
            skLineSegment(sketch, "E2047", {"start": v(102.36, 527.28) * mm, "end": v(102.17, 527.58) * mm});
            skLineSegment(sketch, "E2048", {"start": v(102.17, 527.58) * mm, "end": v(102, 527.88) * mm});
            skLineSegment(sketch, "E2049", {"start": v(102, 527.88) * mm, "end": v(101.82, 528.2) * mm});
            skLineSegment(sketch, "E2050", {"start": v(101.82, 528.2) * mm, "end": v(101.66, 528.5) * mm});
            skLineSegment(sketch, "E2051", {"start": v(101.66, 528.5) * mm, "end": v(101.5, 528.82) * mm});
            skLineSegment(sketch, "E2052", {"start": v(101.5, 528.82) * mm, "end": v(101.36, 529.13) * mm});
            skLineSegment(sketch, "E2053", {"start": v(101.36, 529.13) * mm, "end": v(101.22, 529.46) * mm});
            skLineSegment(sketch, "E2054", {"start": v(101.22, 529.46) * mm, "end": v(101.09, 529.78) * mm});
            skLineSegment(sketch, "E2055", {"start": v(101.09, 529.78) * mm, "end": v(100.96, 530.11) * mm});
            skLineSegment(sketch, "E2056", {"start": v(100.96, 530.11) * mm, "end": v(100.85, 530.44) * mm});
            skLineSegment(sketch, "E2057", {"start": v(100.85, 530.44) * mm, "end": v(100.74, 530.78) * mm});
            skLineSegment(sketch, "E2058", {"start": v(100.74, 530.78) * mm, "end": v(100.65, 531.12) * mm});
            skLineSegment(sketch, "E2059", {"start": v(100.65, 531.12) * mm, "end": v(100.56, 531.46) * mm});
            skLineSegment(sketch, "E2060", {"start": v(100.56, 531.46) * mm, "end": v(100.48, 531.8) * mm});
            skLineSegment(sketch, "E2061", {"start": v(100.48, 531.8) * mm, "end": v(100.4, 532.14) * mm});
            skLineSegment(sketch, "E2062", {"start": v(100.4, 532.14) * mm, "end": v(100.35, 532.5) * mm});
            skLineSegment(sketch, "E2063", {"start": v(100.35, 532.5) * mm, "end": v(100.3, 532.84) * mm});
            skLineSegment(sketch, "E2064", {"start": v(100.3, 532.84) * mm, "end": v(100.25, 533.2) * mm});
            skLineSegment(sketch, "E2065", {"start": v(100.25, 533.2) * mm, "end": v(100.21, 533.54) * mm});
            skLineSegment(sketch, "E2066", {"start": v(100.21, 533.54) * mm, "end": v(100.19, 533.9) * mm});
            skLineSegment(sketch, "E2067", {"start": v(100.19, 533.9) * mm, "end": v(100.17, 534.25) * mm});
            skLineSegment(sketch, "E2068", {"start": v(100.17, 534.25) * mm, "end": v(100.16, 534.6) * mm});
            skLineSegment(sketch, "E2069", {"start": v(100.16, 534.6) * mm, "end": v(100.16, 534.96) * mm});
            skLineSegment(sketch, "E2070", {"start": v(100.16, 534.96) * mm, "end": v(100.17, 535.33) * mm});
            skLineSegment(sketch, "E2071", {"start": v(100.17, 535.33) * mm, "end": v(100.18, 535.69) * mm});
            skLineSegment(sketch, "E2072", {"start": v(100.18, 535.69) * mm, "end": v(100.2, 536.05) * mm});
            skLineSegment(sketch, "E2073", {"start": v(100.2, 536.05) * mm, "end": v(100.23, 536.4) * mm});
            skLineSegment(sketch, "E2074", {"start": v(100.23, 536.4) * mm, "end": v(100.27, 536.76) * mm});
            skLineSegment(sketch, "E2075", {"start": v(100.27, 536.76) * mm, "end": v(100.32, 537.12) * mm});
            skLineSegment(sketch, "E2076", {"start": v(100.32, 537.12) * mm, "end": v(100.38, 537.47) * mm});
            skLineSegment(sketch, "E2077", {"start": v(100.38, 537.47) * mm, "end": v(100.45, 537.83) * mm});
            skLineSegment(sketch, "E2078", {"start": v(100.45, 537.83) * mm, "end": v(100.52, 538.17) * mm});
            skLineSegment(sketch, "E2079", {"start": v(100.52, 538.17) * mm, "end": v(100.61, 538.52) * mm});
            skLineSegment(sketch, "E2080", {"start": v(100.61, 538.52) * mm, "end": v(100.7, 538.87) * mm});
            skLineSegment(sketch, "E2081", {"start": v(100.7, 538.87) * mm, "end": v(100.8, 539.2) * mm});
            skLineSegment(sketch, "E2082", {"start": v(100.8, 539.2) * mm, "end": v(100.92, 539.55) * mm});
            skLineSegment(sketch, "E2083", {"start": v(100.92, 539.55) * mm, "end": v(101.04, 539.88) * mm});
            skLineSegment(sketch, "E2084", {"start": v(101.04, 539.88) * mm, "end": v(101.17, 540.22) * mm});
            skLineSegment(sketch, "E2085", {"start": v(101.17, 540.22) * mm, "end": v(101.3, 540.55) * mm});
            skLineSegment(sketch, "E2086", {"start": v(101.3, 540.55) * mm, "end": v(101.45, 540.87) * mm});
            skLineSegment(sketch, "E2087", {"start": v(101.45, 540.87) * mm, "end": v(101.6, 541.2) * mm});
            skLineSegment(sketch, "E2088", {"start": v(101.6, 541.2) * mm, "end": v(101.77, 541.51) * mm});
            skLineSegment(sketch, "E2089", {"start": v(101.77, 541.51) * mm, "end": v(101.94, 541.83) * mm});
            skLineSegment(sketch, "E2090", {"start": v(101.94, 541.83) * mm, "end": v(102.11, 542.14) * mm});
            skLineSegment(sketch, "E2091", {"start": v(102.11, 542.14) * mm, "end": v(102.3, 542.44) * mm});
            skLineSegment(sketch, "E2092", {"start": v(102.3, 542.44) * mm, "end": v(102.5, 542.74) * mm});
            skLineSegment(sketch, "E2093", {"start": v(102.5, 542.74) * mm, "end": v(102.7, 543.04) * mm});
            skLineSegment(sketch, "E2094", {"start": v(102.7, 543.04) * mm, "end": v(102.9, 543.33) * mm});
            skLineSegment(sketch, "E2095", {"start": v(102.9, 543.33) * mm, "end": v(103.12, 543.61) * mm});
            skLineSegment(sketch, "E2096", {"start": v(103.12, 543.61) * mm, "end": v(103.35, 543.9) * mm});
            skLineSegment(sketch, "E2097", {"start": v(103.35, 543.9) * mm, "end": v(103.58, 544.17) * mm});
            skLineSegment(sketch, "E2098", {"start": v(103.58, 544.17) * mm, "end": v(103.82, 544.44) * mm});
            skLineSegment(sketch, "E2099", {"start": v(103.82, 544.44) * mm, "end": v(104.07, 544.7) * mm});
            skLineSegment(sketch, "E2100", {"start": v(104.07, 544.7) * mm, "end": v(104.32, 544.96) * mm});
            skLineSegment(sketch, "E2101", {"start": v(104.32, 544.96) * mm, "end": v(104.58, 545.2) * mm});
            skLineSegment(sketch, "E2102", {"start": v(104.58, 545.2) * mm, "end": v(104.94, 545.53) * mm});
            skLineSegment(sketch, "E2103", {"start": v(104.94, 545.53) * mm, "end": v(105.3, 545.85) * mm});
            skLineSegment(sketch, "E2104", {"start": v(105.3, 545.85) * mm, "end": v(105.68, 546.15) * mm});
            skLineSegment(sketch, "E2105", {"start": v(105.68, 546.15) * mm, "end": v(106.06, 546.45) * mm});
            skLineSegment(sketch, "E2106", {"start": v(106.06, 546.45) * mm, "end": v(106.44, 546.73) * mm});
            skLineSegment(sketch, "E2107", {"start": v(106.44, 546.73) * mm, "end": v(106.84, 547) * mm});
            skLineSegment(sketch, "E2108", {"start": v(106.84, 547) * mm, "end": v(107.24, 547.27) * mm});
            skLineSegment(sketch, "E2109", {"start": v(107.24, 547.27) * mm, "end": v(107.64, 547.52) * mm});
            skLineSegment(sketch, "E2110", {"start": v(107.64, 547.52) * mm, "end": v(108.05, 547.76) * mm});
            skLineSegment(sketch, "E2111", {"start": v(108.05, 547.76) * mm, "end": v(108.47, 548) * mm});
            skLineSegment(sketch, "E2112", {"start": v(108.47, 548) * mm, "end": v(108.9, 548.22) * mm});
            skLineSegment(sketch, "E2113", {"start": v(108.9, 548.22) * mm, "end": v(109.32, 548.43) * mm});
            skLineSegment(sketch, "E2114", {"start": v(109.32, 548.43) * mm, "end": v(109.75, 548.63) * mm});
            skLineSegment(sketch, "E2115", {"start": v(109.75, 548.63) * mm, "end": v(110.19, 548.82) * mm});
            skLineSegment(sketch, "E2116", {"start": v(110.19, 548.82) * mm, "end": v(110.63, 549) * mm});
            skLineSegment(sketch, "E2117", {"start": v(110.63, 549) * mm, "end": v(111.07, 549.17) * mm});
            skLineSegment(sketch, "E2118", {"start": v(111.07, 549.17) * mm, "end": v(111.52, 549.33) * mm});
            skLineSegment(sketch, "E2119", {"start": v(111.52, 549.33) * mm, "end": v(111.97, 549.47) * mm});
            skLineSegment(sketch, "E2120", {"start": v(111.97, 549.47) * mm, "end": v(112.43, 549.6) * mm});
            skLineSegment(sketch, "E2121", {"start": v(112.43, 549.6) * mm, "end": v(112.89, 549.73) * mm});
            skLineSegment(sketch, "E2122", {"start": v(112.89, 549.73) * mm, "end": v(113.35, 549.85) * mm});
            skLineSegment(sketch, "E2123", {"start": v(113.35, 549.85) * mm, "end": v(113.82, 549.95) * mm});
            skLineSegment(sketch, "E2124", {"start": v(113.82, 549.95) * mm, "end": v(114.29, 550.04) * mm});
            skLineSegment(sketch, "E2125", {"start": v(114.29, 550.04) * mm, "end": v(114.76, 550.11) * mm});
            skLineSegment(sketch, "E2126", {"start": v(114.76, 550.11) * mm, "end": v(115.23, 550.18) * mm});
            skLineSegment(sketch, "E2127", {"start": v(115.23, 550.18) * mm, "end": v(115.7, 550.24) * mm});
            skLineSegment(sketch, "E2128", {"start": v(115.7, 550.24) * mm, "end": v(116.18, 550.28) * mm});
            skLineSegment(sketch, "E2129", {"start": v(116.18, 550.28) * mm, "end": v(116.66, 550.31) * mm});
            skLineSegment(sketch, "E2130", {"start": v(116.66, 550.31) * mm, "end": v(117.14, 550.33) * mm});
            skLineSegment(sketch, "E2131", {"start": v(117.14, 550.33) * mm, "end": v(117.62, 550.34) * mm});
            skLineSegment(sketch, "E2132", {"start": v(117.62, 550.34) * mm, "end": v(118.1, 550.33) * mm});
            skLineSegment(sketch, "E2133", {"start": v(118.1, 550.33) * mm, "end": v(118.59, 550.31) * mm});
            skLineSegment(sketch, "E2134", {"start": v(118.59, 550.31) * mm, "end": v(119.04, 550.32) * mm});
            skLineSegment(sketch, "E2135", {"start": v(119.04, 550.32) * mm, "end": v(119.49, 550.32) * mm});
            skLineSegment(sketch, "E2136", {"start": v(119.49, 550.32) * mm, "end": v(119.94, 550.3) * mm});
            skLineSegment(sketch, "E2137", {"start": v(119.94, 550.3) * mm, "end": v(120.38, 550.28) * mm});
            skLineSegment(sketch, "E2138", {"start": v(120.38, 550.28) * mm, "end": v(120.83, 550.24) * mm});
            skLineSegment(sketch, "E2139", {"start": v(120.83, 550.24) * mm, "end": v(121.27, 550.19) * mm});
            skLineSegment(sketch, "E2140", {"start": v(121.27, 550.19) * mm, "end": v(121.72, 550.13) * mm});
            skLineSegment(sketch, "E2141", {"start": v(121.72, 550.13) * mm, "end": v(122.16, 550.06) * mm});
            skLineSegment(sketch, "E2142", {"start": v(122.16, 550.06) * mm, "end": v(122.6, 549.97) * mm});
            skLineSegment(sketch, "E2143", {"start": v(122.6, 549.97) * mm, "end": v(123.03, 549.88) * mm});
            skLineSegment(sketch, "E2144", {"start": v(123.03, 549.88) * mm, "end": v(123.46, 549.78) * mm});
            skLineSegment(sketch, "E2145", {"start": v(123.46, 549.78) * mm, "end": v(123.9, 549.66) * mm});
            skLineSegment(sketch, "E2146", {"start": v(123.9, 549.66) * mm, "end": v(124.32, 549.54) * mm});
            skLineSegment(sketch, "E2147", {"start": v(124.32, 549.54) * mm, "end": v(124.74, 549.4) * mm});
            skLineSegment(sketch, "E2148", {"start": v(124.74, 549.4) * mm, "end": v(125.16, 549.26) * mm});
            skLineSegment(sketch, "E2149", {"start": v(125.16, 549.26) * mm, "end": v(125.57, 549.1) * mm});
            skLineSegment(sketch, "E2150", {"start": v(125.57, 549.1) * mm, "end": v(125.99, 548.94) * mm});
            skLineSegment(sketch, "E2151", {"start": v(125.99, 548.94) * mm, "end": v(126.4, 548.76) * mm});
            skLineSegment(sketch, "E2152", {"start": v(126.4, 548.76) * mm, "end": v(126.8, 548.57) * mm});
            skLineSegment(sketch, "E2153", {"start": v(126.8, 548.57) * mm, "end": v(127.2, 548.38) * mm});
            skLineSegment(sketch, "E2154", {"start": v(127.2, 548.38) * mm, "end": v(127.59, 548.17) * mm});
            skLineSegment(sketch, "E2155", {"start": v(127.59, 548.17) * mm, "end": v(127.98, 547.96) * mm});
            skLineSegment(sketch, "E2156", {"start": v(127.98, 547.96) * mm, "end": v(128.36, 547.73) * mm});
            skLineSegment(sketch, "E2157", {"start": v(128.36, 547.73) * mm, "end": v(128.74, 547.5) * mm});
            skLineSegment(sketch, "E2158", {"start": v(128.74, 547.5) * mm, "end": v(129.11, 547.25) * mm});
            skLineSegment(sketch, "E2159", {"start": v(129.11, 547.25) * mm, "end": v(129.48, 547) * mm});
            skLineSegment(sketch, "E2160", {"start": v(129.48, 547) * mm, "end": v(129.84, 546.73) * mm});
            skLineSegment(sketch, "E2161", {"start": v(129.84, 546.73) * mm, "end": v(130.2, 546.46) * mm});
            skLineSegment(sketch, "E2162", {"start": v(130.2, 546.46) * mm, "end": v(130.54, 546.17) * mm});
            skLineSegment(sketch, "E2163", {"start": v(130.54, 546.17) * mm, "end": v(130.88, 545.88) * mm});
            skLineSegment(sketch, "E2164", {"start": v(130.88, 545.88) * mm, "end": v(131.21, 545.58) * mm});
            skLineSegment(sketch, "E2165", {"start": v(131.21, 545.58) * mm, "end": v(131.54, 545.27) * mm});
            skLineSegment(sketch, "E2166", {"start": v(131.54, 545.27) * mm, "end": v(131.8, 545.01) * mm});
            skLineSegment(sketch, "E2167", {"start": v(131.8, 545.01) * mm, "end": v(132.04, 544.75) * mm});
            skLineSegment(sketch, "E2168", {"start": v(132.04, 544.75) * mm, "end": v(132.28, 544.48) * mm});
            skLineSegment(sketch, "E2169", {"start": v(132.28, 544.48) * mm, "end": v(132.52, 544.2) * mm});
            skLineSegment(sketch, "E2170", {"start": v(132.52, 544.2) * mm, "end": v(132.74, 543.93) * mm});
            skLineSegment(sketch, "E2171", {"start": v(132.74, 543.93) * mm, "end": v(132.96, 543.64) * mm});
            skLineSegment(sketch, "E2172", {"start": v(132.96, 543.64) * mm, "end": v(133.17, 543.35) * mm});
            skLineSegment(sketch, "E2173", {"start": v(133.17, 543.35) * mm, "end": v(133.38, 543.06) * mm});
            skLineSegment(sketch, "E2174", {"start": v(133.38, 543.06) * mm, "end": v(133.57, 542.76) * mm});
            skLineSegment(sketch, "E2175", {"start": v(133.57, 542.76) * mm, "end": v(133.76, 542.46) * mm});
            skLineSegment(sketch, "E2176", {"start": v(133.76, 542.46) * mm, "end": v(133.94, 542.15) * mm});
            skLineSegment(sketch, "E2177", {"start": v(133.94, 542.15) * mm, "end": v(134.11, 541.84) * mm});
            skLineSegment(sketch, "E2178", {"start": v(134.11, 541.84) * mm, "end": v(134.28, 541.52) * mm});
            skLineSegment(sketch, "E2179", {"start": v(134.28, 541.52) * mm, "end": v(134.44, 541.2) * mm});
            skLineSegment(sketch, "E2180", {"start": v(134.44, 541.2) * mm, "end": v(134.59, 540.87) * mm});
            skLineSegment(sketch, "E2181", {"start": v(134.59, 540.87) * mm, "end": v(134.73, 540.55) * mm});
            skLineSegment(sketch, "E2182", {"start": v(134.73, 540.55) * mm, "end": v(134.86, 540.22) * mm});
            skLineSegment(sketch, "E2183", {"start": v(134.86, 540.22) * mm, "end": v(134.98, 539.88) * mm});
            skLineSegment(sketch, "E2184", {"start": v(134.98, 539.88) * mm, "end": v(135.1, 539.54) * mm});
            skLineSegment(sketch, "E2185", {"start": v(135.1, 539.54) * mm, "end": v(135.2, 539.2) * mm});
            skLineSegment(sketch, "E2186", {"start": v(135.2, 539.2) * mm, "end": v(135.3, 538.86) * mm});
            skLineSegment(sketch, "E2187", {"start": v(135.3, 538.86) * mm, "end": v(135.4, 538.52) * mm});
            skLineSegment(sketch, "E2188", {"start": v(135.4, 538.52) * mm, "end": v(135.48, 538.17) * mm});
            skLineSegment(sketch, "E2189", {"start": v(135.48, 538.17) * mm, "end": v(135.55, 537.82) * mm});
            skLineSegment(sketch, "E2190", {"start": v(135.55, 537.82) * mm, "end": v(135.62, 537.47) * mm});
            skLineSegment(sketch, "E2191", {"start": v(135.62, 537.47) * mm, "end": v(135.68, 537.11) * mm});
            skLineSegment(sketch, "E2192", {"start": v(135.68, 537.11) * mm, "end": v(135.72, 536.76) * mm});
            skLineSegment(sketch, "E2193", {"start": v(135.72, 536.76) * mm, "end": v(135.76, 536.4) * mm});
            skLineSegment(sketch, "E2194", {"start": v(135.76, 536.4) * mm, "end": v(135.8, 536.04) * mm});
            skLineSegment(sketch, "E2195", {"start": v(135.8, 536.04) * mm, "end": v(135.81, 535.68) * mm});
            skLineSegment(sketch, "E2196", {"start": v(135.81, 535.68) * mm, "end": v(135.82, 535.32) * mm});
            skLineSegment(sketch, "E2197", {"start": v(135.82, 535.32) * mm, "end": v(135.83, 534.96) * mm});
            skLineSegment(sketch, "E2198", {"start": v(135.83, 573.67) * mm, "end": v(135.83, 573.3) * mm});
            skLineSegment(sketch, "E2199", {"start": v(135.83, 573.3) * mm, "end": v(135.82, 572.94) * mm});
            skLineSegment(sketch, "E2200", {"start": v(135.82, 572.94) * mm, "end": v(135.8, 572.57) * mm});
            skLineSegment(sketch, "E2201", {"start": v(135.8, 572.57) * mm, "end": v(135.78, 572.2) * mm});
            skLineSegment(sketch, "E2202", {"start": v(135.78, 572.2) * mm, "end": v(135.75, 571.84) * mm});
            skLineSegment(sketch, "E2203", {"start": v(135.75, 571.84) * mm, "end": v(135.7, 571.48) * mm});
            skLineSegment(sketch, "E2204", {"start": v(135.7, 571.48) * mm, "end": v(135.65, 571.12) * mm});
            skLineSegment(sketch, "E2205", {"start": v(135.65, 571.12) * mm, "end": v(135.6, 570.76) * mm});
            skLineSegment(sketch, "E2206", {"start": v(135.6, 570.76) * mm, "end": v(135.52, 570.4) * mm});
            skLineSegment(sketch, "E2207", {"start": v(135.52, 570.4) * mm, "end": v(135.45, 570.05) * mm});
            skLineSegment(sketch, "E2208", {"start": v(135.45, 570.05) * mm, "end": v(135.36, 569.7) * mm});
            skLineSegment(sketch, "E2209", {"start": v(135.36, 569.7) * mm, "end": v(135.26, 569.35) * mm});
            skLineSegment(sketch, "E2210", {"start": v(135.26, 569.35) * mm, "end": v(135.16, 569) * mm});
            skLineSegment(sketch, "E2211", {"start": v(135.16, 569) * mm, "end": v(135.05, 568.66) * mm});
            skLineSegment(sketch, "E2212", {"start": v(135.05, 568.66) * mm, "end": v(134.92, 568.32) * mm});
            skLineSegment(sketch, "E2213", {"start": v(134.92, 568.32) * mm, "end": v(134.8, 567.98) * mm});
            skLineSegment(sketch, "E2214", {"start": v(134.8, 567.98) * mm, "end": v(134.66, 567.65) * mm});
            skLineSegment(sketch, "E2215", {"start": v(134.66, 567.65) * mm, "end": v(134.5, 567.32) * mm});
            skLineSegment(sketch, "E2216", {"start": v(134.5, 567.32) * mm, "end": v(134.36, 566.99) * mm});
            skLineSegment(sketch, "E2217", {"start": v(134.36, 566.99) * mm, "end": v(134.2, 566.66) * mm});
            skLineSegment(sketch, "E2218", {"start": v(134.2, 566.66) * mm, "end": v(134.02, 566.34) * mm});
            skLineSegment(sketch, "E2219", {"start": v(134.02, 566.34) * mm, "end": v(133.84, 566.03) * mm});
            skLineSegment(sketch, "E2220", {"start": v(133.84, 566.03) * mm, "end": v(133.66, 565.72) * mm});
            skLineSegment(sketch, "E2221", {"start": v(133.66, 565.72) * mm, "end": v(133.46, 565.41) * mm});
            skLineSegment(sketch, "E2222", {"start": v(133.46, 565.41) * mm, "end": v(133.26, 565.1) * mm});
            skLineSegment(sketch, "E2223", {"start": v(133.26, 565.1) * mm, "end": v(133.05, 564.81) * mm});
            skLineSegment(sketch, "E2224", {"start": v(133.05, 564.81) * mm, "end": v(132.83, 564.52) * mm});
            skLineSegment(sketch, "E2225", {"start": v(132.83, 564.52) * mm, "end": v(132.6, 564.23) * mm});
            skLineSegment(sketch, "E2226", {"start": v(132.6, 564.23) * mm, "end": v(132.37, 563.95) * mm});
            skLineSegment(sketch, "E2227", {"start": v(132.37, 563.95) * mm, "end": v(132.13, 563.68) * mm});
            skLineSegment(sketch, "E2228", {"start": v(132.13, 563.68) * mm, "end": v(131.89, 563.4) * mm});
            skLineSegment(sketch, "E2229", {"start": v(131.89, 563.4) * mm, "end": v(131.63, 563.14) * mm});
            skLineSegment(sketch, "E2230", {"start": v(131.63, 563.14) * mm, "end": v(131.3, 562.83) * mm});
            skLineSegment(sketch, "E2231", {"start": v(131.3, 562.83) * mm, "end": v(130.96, 562.54) * mm});
            skLineSegment(sketch, "E2232", {"start": v(130.96, 562.54) * mm, "end": v(130.61, 562.25) * mm});
            skLineSegment(sketch, "E2233", {"start": v(130.61, 562.25) * mm, "end": v(130.26, 561.97) * mm});
            skLineSegment(sketch, "E2234", {"start": v(130.26, 561.97) * mm, "end": v(129.9, 561.7) * mm});
            skLineSegment(sketch, "E2235", {"start": v(129.9, 561.7) * mm, "end": v(129.54, 561.44) * mm});
            skLineSegment(sketch, "E2236", {"start": v(129.54, 561.44) * mm, "end": v(129.16, 561.19) * mm});
            skLineSegment(sketch, "E2237", {"start": v(129.16, 561.19) * mm, "end": v(128.79, 560.95) * mm});
            skLineSegment(sketch, "E2238", {"start": v(128.79, 560.95) * mm, "end": v(128.4, 560.72) * mm});
            skLineSegment(sketch, "E2239", {"start": v(128.4, 560.72) * mm, "end": v(128.02, 560.5) * mm});
            skLineSegment(sketch, "E2240", {"start": v(128.02, 560.5) * mm, "end": v(127.62, 560.28) * mm});
            skLineSegment(sketch, "E2241", {"start": v(127.62, 560.28) * mm, "end": v(127.23, 560.08) * mm});
            skLineSegment(sketch, "E2242", {"start": v(127.23, 560.08) * mm, "end": v(126.83, 559.89) * mm});
            skLineSegment(sketch, "E2243", {"start": v(126.83, 559.89) * mm, "end": v(126.42, 559.7) * mm});
            skLineSegment(sketch, "E2244", {"start": v(126.42, 559.7) * mm, "end": v(126, 559.53) * mm});
            skLineSegment(sketch, "E2245", {"start": v(126, 559.53) * mm, "end": v(125.6, 559.37) * mm});
            skLineSegment(sketch, "E2246", {"start": v(125.6, 559.37) * mm, "end": v(125.17, 559.22) * mm});
            skLineSegment(sketch, "E2247", {"start": v(125.17, 559.22) * mm, "end": v(124.75, 559.08) * mm});
            skLineSegment(sketch, "E2248", {"start": v(124.75, 559.08) * mm, "end": v(124.32, 558.95) * mm});
            skLineSegment(sketch, "E2249", {"start": v(124.32, 558.95) * mm, "end": v(123.9, 558.83) * mm});
            skLineSegment(sketch, "E2250", {"start": v(123.9, 558.83) * mm, "end": v(123.46, 558.71) * mm});
            skLineSegment(sketch, "E2251", {"start": v(123.46, 558.71) * mm, "end": v(123.03, 558.61) * mm});
            skLineSegment(sketch, "E2252", {"start": v(123.03, 558.61) * mm, "end": v(122.6, 558.53) * mm});
            skLineSegment(sketch, "E2253", {"start": v(122.6, 558.53) * mm, "end": v(122.15, 558.45) * mm});
            skLineSegment(sketch, "E2254", {"start": v(122.15, 558.45) * mm, "end": v(121.7, 558.38) * mm});
            skLineSegment(sketch, "E2255", {"start": v(121.7, 558.38) * mm, "end": v(121.26, 558.32) * mm});
            skLineSegment(sketch, "E2256", {"start": v(121.26, 558.32) * mm, "end": v(120.82, 558.28) * mm});
            skLineSegment(sketch, "E2257", {"start": v(120.82, 558.28) * mm, "end": v(120.37, 558.24) * mm});
            skLineSegment(sketch, "E2258", {"start": v(120.37, 558.24) * mm, "end": v(119.92, 558.22) * mm});
            skLineSegment(sketch, "E2259", {"start": v(119.92, 558.22) * mm, "end": v(119.47, 558.2) * mm});
            skLineSegment(sketch, "E2260", {"start": v(119.47, 558.2) * mm, "end": v(119.02, 558.2) * mm});
            skLineSegment(sketch, "E2261", {"start": v(119.02, 558.2) * mm, "end": v(118.57, 558.22) * mm});
            skLineSegment(sketch, "E2262", {"start": v(118.57, 558.22) * mm, "end": v(118.08, 558.2) * mm});
            skLineSegment(sketch, "E2263", {"start": v(118.08, 558.2) * mm, "end": v(117.59, 558.2) * mm});
            skLineSegment(sketch, "E2264", {"start": v(117.59, 558.2) * mm, "end": v(117.1, 558.21) * mm});
            skLineSegment(sketch, "E2265", {"start": v(117.1, 558.21) * mm, "end": v(116.6, 558.24) * mm});
            skLineSegment(sketch, "E2266", {"start": v(116.6, 558.24) * mm, "end": v(116.12, 558.27) * mm});
            skLineSegment(sketch, "E2267", {"start": v(116.12, 558.27) * mm, "end": v(115.64, 558.32) * mm});
            skLineSegment(sketch, "E2268", {"start": v(115.64, 558.32) * mm, "end": v(115.16, 558.38) * mm});
            skLineSegment(sketch, "E2269", {"start": v(115.16, 558.38) * mm, "end": v(114.68, 558.45) * mm});
            skLineSegment(sketch, "E2270", {"start": v(114.68, 558.45) * mm, "end": v(114.2, 558.53) * mm});
            skLineSegment(sketch, "E2271", {"start": v(114.2, 558.53) * mm, "end": v(113.72, 558.63) * mm});
            skLineSegment(sketch, "E2272", {"start": v(113.72, 558.63) * mm, "end": v(113.25, 558.74) * mm});
            skLineSegment(sketch, "E2273", {"start": v(113.25, 558.74) * mm, "end": v(112.78, 558.85) * mm});
            skLineSegment(sketch, "E2274", {"start": v(112.78, 558.85) * mm, "end": v(112.31, 558.99) * mm});
            skLineSegment(sketch, "E2275", {"start": v(112.31, 558.99) * mm, "end": v(111.85, 559.13) * mm});
            skLineSegment(sketch, "E2276", {"start": v(111.85, 559.13) * mm, "end": v(111.4, 559.28) * mm});
            skLineSegment(sketch, "E2277", {"start": v(111.4, 559.28) * mm, "end": v(110.94, 559.44) * mm});
            skLineSegment(sketch, "E2278", {"start": v(110.94, 559.44) * mm, "end": v(110.49, 559.62) * mm});
            skLineSegment(sketch, "E2279", {"start": v(110.49, 559.62) * mm, "end": v(110.04, 559.8) * mm});
            skLineSegment(sketch, "E2280", {"start": v(110.04, 559.8) * mm, "end": v(109.6, 560) * mm});
            skLineSegment(sketch, "E2281", {"start": v(109.6, 560) * mm, "end": v(109.16, 560.21) * mm});
            skLineSegment(sketch, "E2282", {"start": v(109.16, 560.21) * mm, "end": v(108.73, 560.43) * mm});
            skLineSegment(sketch, "E2283", {"start": v(108.73, 560.43) * mm, "end": v(108.3, 560.66) * mm});
            skLineSegment(sketch, "E2284", {"start": v(108.3, 560.66) * mm, "end": v(107.88, 560.9) * mm});
            skLineSegment(sketch, "E2285", {"start": v(107.88, 560.9) * mm, "end": v(107.47, 561.16) * mm});
            skLineSegment(sketch, "E2286", {"start": v(107.47, 561.16) * mm, "end": v(107.06, 561.42) * mm});
            skLineSegment(sketch, "E2287", {"start": v(107.06, 561.42) * mm, "end": v(106.66, 561.7) * mm});
            skLineSegment(sketch, "E2288", {"start": v(106.66, 561.7) * mm, "end": v(106.26, 561.98) * mm});
            skLineSegment(sketch, "E2289", {"start": v(106.26, 561.98) * mm, "end": v(105.87, 562.27) * mm});
            skLineSegment(sketch, "E2290", {"start": v(105.87, 562.27) * mm, "end": v(105.49, 562.57) * mm});
            skLineSegment(sketch, "E2291", {"start": v(105.49, 562.57) * mm, "end": v(105.11, 562.89) * mm});
            skLineSegment(sketch, "E2292", {"start": v(105.11, 562.89) * mm, "end": v(104.75, 563.21) * mm});
            skLineSegment(sketch, "E2293", {"start": v(104.75, 563.21) * mm, "end": v(104.39, 563.55) * mm});
            skLineSegment(sketch, "E2294", {"start": v(104.39, 563.55) * mm, "end": v(104.13, 563.8) * mm});
            skLineSegment(sketch, "E2295", {"start": v(104.13, 563.8) * mm, "end": v(103.88, 564.05) * mm});
            skLineSegment(sketch, "E2296", {"start": v(103.88, 564.05) * mm, "end": v(103.64, 564.31) * mm});
            skLineSegment(sketch, "E2297", {"start": v(103.64, 564.31) * mm, "end": v(103.41, 564.58) * mm});
            skLineSegment(sketch, "E2298", {"start": v(103.41, 564.58) * mm, "end": v(103.19, 564.85) * mm});
            skLineSegment(sketch, "E2299", {"start": v(103.19, 564.85) * mm, "end": v(102.97, 565.13) * mm});
            skLineSegment(sketch, "E2300", {"start": v(102.97, 565.13) * mm, "end": v(102.76, 565.42) * mm});
            skLineSegment(sketch, "E2301", {"start": v(102.76, 565.42) * mm, "end": v(102.56, 565.7) * mm});
            skLineSegment(sketch, "E2302", {"start": v(102.56, 565.7) * mm, "end": v(102.36, 566) * mm});
            skLineSegment(sketch, "E2303", {"start": v(102.36, 566) * mm, "end": v(102.17, 566.3) * mm});
            skLineSegment(sketch, "E2304", {"start": v(102.17, 566.3) * mm, "end": v(102, 566.6) * mm});
            skLineSegment(sketch, "E2305", {"start": v(102, 566.6) * mm, "end": v(101.82, 566.9) * mm});
            skLineSegment(sketch, "E2306", {"start": v(101.82, 566.9) * mm, "end": v(101.66, 567.22) * mm});
            skLineSegment(sketch, "E2307", {"start": v(101.66, 567.22) * mm, "end": v(101.5, 567.53) * mm});
            skLineSegment(sketch, "E2308", {"start": v(101.5, 567.53) * mm, "end": v(101.36, 567.85) * mm});
            skLineSegment(sketch, "E2309", {"start": v(101.36, 567.85) * mm, "end": v(101.22, 568.17) * mm});
            skLineSegment(sketch, "E2310", {"start": v(101.22, 568.17) * mm, "end": v(101.09, 568.5) * mm});
            skLineSegment(sketch, "E2311", {"start": v(101.09, 568.5) * mm, "end": v(100.96, 568.83) * mm});
            skLineSegment(sketch, "E2312", {"start": v(100.96, 568.83) * mm, "end": v(100.85, 569.16) * mm});
            skLineSegment(sketch, "E2313", {"start": v(100.85, 569.16) * mm, "end": v(100.74, 569.5) * mm});
            skLineSegment(sketch, "E2314", {"start": v(100.74, 569.5) * mm, "end": v(100.65, 569.83) * mm});
            skLineSegment(sketch, "E2315", {"start": v(100.65, 569.83) * mm, "end": v(100.56, 570.17) * mm});
            skLineSegment(sketch, "E2316", {"start": v(100.56, 570.17) * mm, "end": v(100.48, 570.51) * mm});
            skLineSegment(sketch, "E2317", {"start": v(100.48, 570.51) * mm, "end": v(100.4, 570.86) * mm});
            skLineSegment(sketch, "E2318", {"start": v(100.4, 570.86) * mm, "end": v(100.35, 571.2) * mm});
            skLineSegment(sketch, "E2319", {"start": v(100.35, 571.2) * mm, "end": v(100.3, 571.55) * mm});
            skLineSegment(sketch, "E2320", {"start": v(100.3, 571.55) * mm, "end": v(100.25, 571.9) * mm});
            skLineSegment(sketch, "E2321", {"start": v(100.25, 571.9) * mm, "end": v(100.21, 572.26) * mm});
            skLineSegment(sketch, "E2322", {"start": v(100.21, 572.26) * mm, "end": v(100.19, 572.61) * mm});
            skLineSegment(sketch, "E2323", {"start": v(100.19, 572.61) * mm, "end": v(100.17, 572.97) * mm});
            skLineSegment(sketch, "E2324", {"start": v(100.17, 572.97) * mm, "end": v(100.16, 573.32) * mm});
            skLineSegment(sketch, "E2325", {"start": v(100.16, 573.32) * mm, "end": v(100.16, 573.68) * mm});
            skLineSegment(sketch, "E2326", {"start": v(100.16, 573.68) * mm, "end": v(100.17, 574.04) * mm});
            skLineSegment(sketch, "E2327", {"start": v(100.17, 574.04) * mm, "end": v(100.18, 574.4) * mm});
            skLineSegment(sketch, "E2328", {"start": v(100.18, 574.4) * mm, "end": v(100.2, 574.76) * mm});
            skLineSegment(sketch, "E2329", {"start": v(100.2, 574.76) * mm, "end": v(100.23, 575.12) * mm});
            skLineSegment(sketch, "E2330", {"start": v(100.23, 575.12) * mm, "end": v(100.27, 575.48) * mm});
            skLineSegment(sketch, "E2331", {"start": v(100.27, 575.48) * mm, "end": v(100.32, 575.83) * mm});
            skLineSegment(sketch, "E2332", {"start": v(100.32, 575.83) * mm, "end": v(100.38, 576.19) * mm});
            skLineSegment(sketch, "E2333", {"start": v(100.38, 576.19) * mm, "end": v(100.45, 576.54) * mm});
            skLineSegment(sketch, "E2334", {"start": v(100.45, 576.54) * mm, "end": v(100.52, 576.89) * mm});
            skLineSegment(sketch, "E2335", {"start": v(100.52, 576.89) * mm, "end": v(100.61, 577.24) * mm});
            skLineSegment(sketch, "E2336", {"start": v(100.61, 577.24) * mm, "end": v(100.7, 577.58) * mm});
            skLineSegment(sketch, "E2337", {"start": v(100.7, 577.58) * mm, "end": v(100.8, 577.92) * mm});
            skLineSegment(sketch, "E2338", {"start": v(100.8, 577.92) * mm, "end": v(100.92, 578.26) * mm});
            skLineSegment(sketch, "E2339", {"start": v(100.92, 578.26) * mm, "end": v(101.04, 578.6) * mm});
            skLineSegment(sketch, "E2340", {"start": v(101.04, 578.6) * mm, "end": v(101.17, 578.93) * mm});
            skLineSegment(sketch, "E2341", {"start": v(101.17, 578.93) * mm, "end": v(101.3, 579.26) * mm});
            skLineSegment(sketch, "E2342", {"start": v(101.3, 579.26) * mm, "end": v(101.45, 579.59) * mm});
            skLineSegment(sketch, "E2343", {"start": v(101.45, 579.59) * mm, "end": v(101.6, 579.9) * mm});
            skLineSegment(sketch, "E2344", {"start": v(101.6, 579.9) * mm, "end": v(101.77, 580.23) * mm});
            skLineSegment(sketch, "E2345", {"start": v(101.77, 580.23) * mm, "end": v(101.94, 580.54) * mm});
            skLineSegment(sketch, "E2346", {"start": v(101.94, 580.54) * mm, "end": v(102.11, 580.85) * mm});
            skLineSegment(sketch, "E2347", {"start": v(102.11, 580.85) * mm, "end": v(102.3, 581.16) * mm});
            skLineSegment(sketch, "E2348", {"start": v(102.3, 581.16) * mm, "end": v(102.5, 581.46) * mm});
            skLineSegment(sketch, "E2349", {"start": v(102.5, 581.46) * mm, "end": v(102.7, 581.75) * mm});
            skLineSegment(sketch, "E2350", {"start": v(102.7, 581.75) * mm, "end": v(102.9, 582.04) * mm});
            skLineSegment(sketch, "E2351", {"start": v(102.9, 582.04) * mm, "end": v(103.12, 582.33) * mm});
            skLineSegment(sketch, "E2352", {"start": v(103.12, 582.33) * mm, "end": v(103.35, 582.6) * mm});
            skLineSegment(sketch, "E2353", {"start": v(103.35, 582.6) * mm, "end": v(103.58, 582.88) * mm});
            skLineSegment(sketch, "E2354", {"start": v(103.58, 582.88) * mm, "end": v(103.82, 583.15) * mm});
            skLineSegment(sketch, "E2355", {"start": v(103.82, 583.15) * mm, "end": v(104.07, 583.41) * mm});
            skLineSegment(sketch, "E2356", {"start": v(104.07, 583.41) * mm, "end": v(104.32, 583.67) * mm});
            skLineSegment(sketch, "E2357", {"start": v(104.32, 583.67) * mm, "end": v(104.58, 583.92) * mm});
            skLineSegment(sketch, "E2358", {"start": v(104.58, 583.92) * mm, "end": v(104.94, 584.25) * mm});
            skLineSegment(sketch, "E2359", {"start": v(104.94, 584.25) * mm, "end": v(105.3, 584.56) * mm});
            skLineSegment(sketch, "E2360", {"start": v(105.3, 584.56) * mm, "end": v(105.68, 584.87) * mm});
            skLineSegment(sketch, "E2361", {"start": v(105.68, 584.87) * mm, "end": v(106.06, 585.16) * mm});
            skLineSegment(sketch, "E2362", {"start": v(106.06, 585.16) * mm, "end": v(106.44, 585.44) * mm});
            skLineSegment(sketch, "E2363", {"start": v(106.44, 585.44) * mm, "end": v(106.84, 585.72) * mm});
            skLineSegment(sketch, "E2364", {"start": v(106.84, 585.72) * mm, "end": v(107.24, 585.98) * mm});
            skLineSegment(sketch, "E2365", {"start": v(107.24, 585.98) * mm, "end": v(107.64, 586.24) * mm});
            skLineSegment(sketch, "E2366", {"start": v(107.64, 586.24) * mm, "end": v(108.05, 586.48) * mm});
            skLineSegment(sketch, "E2367", {"start": v(108.05, 586.48) * mm, "end": v(108.47, 586.71) * mm});
            skLineSegment(sketch, "E2368", {"start": v(108.47, 586.71) * mm, "end": v(108.9, 586.93) * mm});
            skLineSegment(sketch, "E2369", {"start": v(108.9, 586.93) * mm, "end": v(109.32, 587.15) * mm});
            skLineSegment(sketch, "E2370", {"start": v(109.32, 587.15) * mm, "end": v(109.75, 587.35) * mm});
            skLineSegment(sketch, "E2371", {"start": v(109.75, 587.35) * mm, "end": v(110.19, 587.54) * mm});
            skLineSegment(sketch, "E2372", {"start": v(110.19, 587.54) * mm, "end": v(110.63, 587.72) * mm});
            skLineSegment(sketch, "E2373", {"start": v(110.63, 587.72) * mm, "end": v(111.07, 587.88) * mm});
            skLineSegment(sketch, "E2374", {"start": v(111.07, 587.88) * mm, "end": v(111.52, 588.04) * mm});
            skLineSegment(sketch, "E2375", {"start": v(111.52, 588.04) * mm, "end": v(111.97, 588.19) * mm});
            skLineSegment(sketch, "E2376", {"start": v(111.97, 588.19) * mm, "end": v(112.43, 588.32) * mm});
            skLineSegment(sketch, "E2377", {"start": v(112.43, 588.32) * mm, "end": v(112.89, 588.45) * mm});
            skLineSegment(sketch, "E2378", {"start": v(112.89, 588.45) * mm, "end": v(113.35, 588.56) * mm});
            skLineSegment(sketch, "E2379", {"start": v(113.35, 588.56) * mm, "end": v(113.82, 588.66) * mm});
            skLineSegment(sketch, "E2380", {"start": v(113.82, 588.66) * mm, "end": v(114.29, 588.75) * mm});
            skLineSegment(sketch, "E2381", {"start": v(114.29, 588.75) * mm, "end": v(114.76, 588.83) * mm});
            skLineSegment(sketch, "E2382", {"start": v(114.76, 588.83) * mm, "end": v(115.23, 588.9) * mm});
            skLineSegment(sketch, "E2383", {"start": v(115.23, 588.9) * mm, "end": v(115.7, 588.95) * mm});
            skLineSegment(sketch, "E2384", {"start": v(115.7, 588.95) * mm, "end": v(116.18, 589) * mm});
            skLineSegment(sketch, "E2385", {"start": v(116.18, 589) * mm, "end": v(116.66, 589.02) * mm});
            skLineSegment(sketch, "E2386", {"start": v(116.66, 589.02) * mm, "end": v(117.14, 589.04) * mm});
            skLineSegment(sketch, "E2387", {"start": v(117.14, 589.04) * mm, "end": v(117.62, 589.05) * mm});
            skLineSegment(sketch, "E2388", {"start": v(117.62, 589.05) * mm, "end": v(118.1, 589.05) * mm});
            skLineSegment(sketch, "E2389", {"start": v(118.1, 589.05) * mm, "end": v(118.59, 589.03) * mm});
            skLineSegment(sketch, "E2390", {"start": v(118.59, 589.03) * mm, "end": v(119.04, 589.04) * mm});
            skLineSegment(sketch, "E2391", {"start": v(119.04, 589.04) * mm, "end": v(119.49, 589.03) * mm});
            skLineSegment(sketch, "E2392", {"start": v(119.49, 589.03) * mm, "end": v(119.94, 589.02) * mm});
            skLineSegment(sketch, "E2393", {"start": v(119.94, 589.02) * mm, "end": v(120.38, 588.99) * mm});
            skLineSegment(sketch, "E2394", {"start": v(120.38, 588.99) * mm, "end": v(120.83, 588.95) * mm});
            skLineSegment(sketch, "E2395", {"start": v(120.83, 588.95) * mm, "end": v(121.27, 588.9) * mm});
            skLineSegment(sketch, "E2396", {"start": v(121.27, 588.9) * mm, "end": v(121.72, 588.84) * mm});
            skLineSegment(sketch, "E2397", {"start": v(121.72, 588.84) * mm, "end": v(122.16, 588.77) * mm});
            skLineSegment(sketch, "E2398", {"start": v(122.16, 588.77) * mm, "end": v(122.6, 588.69) * mm});
            skLineSegment(sketch, "E2399", {"start": v(122.6, 588.69) * mm, "end": v(123.03, 588.6) * mm});
            skLineSegment(sketch, "E2400", {"start": v(123.03, 588.6) * mm, "end": v(123.46, 588.5) * mm});
            skLineSegment(sketch, "E2401", {"start": v(123.46, 588.5) * mm, "end": v(123.9, 588.38) * mm});
            skLineSegment(sketch, "E2402", {"start": v(123.9, 588.38) * mm, "end": v(124.32, 588.25) * mm});
            skLineSegment(sketch, "E2403", {"start": v(124.32, 588.25) * mm, "end": v(124.74, 588.12) * mm});
            skLineSegment(sketch, "E2404", {"start": v(124.74, 588.12) * mm, "end": v(125.16, 587.97) * mm});
            skLineSegment(sketch, "E2405", {"start": v(125.16, 587.97) * mm, "end": v(125.57, 587.82) * mm});
            skLineSegment(sketch, "E2406", {"start": v(125.57, 587.82) * mm, "end": v(125.99, 587.65) * mm});
            skLineSegment(sketch, "E2407", {"start": v(125.99, 587.65) * mm, "end": v(126.4, 587.48) * mm});
            skLineSegment(sketch, "E2408", {"start": v(126.4, 587.48) * mm, "end": v(126.8, 587.29) * mm});
            skLineSegment(sketch, "E2409", {"start": v(126.8, 587.29) * mm, "end": v(127.2, 587.1) * mm});
            skLineSegment(sketch, "E2410", {"start": v(127.2, 587.1) * mm, "end": v(127.59, 586.89) * mm});
            skLineSegment(sketch, "E2411", {"start": v(127.59, 586.89) * mm, "end": v(127.98, 586.67) * mm});
            skLineSegment(sketch, "E2412", {"start": v(127.98, 586.67) * mm, "end": v(128.36, 586.44) * mm});
            skLineSegment(sketch, "E2413", {"start": v(128.36, 586.44) * mm, "end": v(128.74, 586.2) * mm});
            skLineSegment(sketch, "E2414", {"start": v(128.74, 586.2) * mm, "end": v(129.11, 585.96) * mm});
            skLineSegment(sketch, "E2415", {"start": v(129.11, 585.96) * mm, "end": v(129.48, 585.7) * mm});
            skLineSegment(sketch, "E2416", {"start": v(129.48, 585.7) * mm, "end": v(129.84, 585.45) * mm});
            skLineSegment(sketch, "E2417", {"start": v(129.84, 585.45) * mm, "end": v(130.2, 585.17) * mm});
            skLineSegment(sketch, "E2418", {"start": v(130.2, 585.17) * mm, "end": v(130.54, 584.89) * mm});
            skLineSegment(sketch, "E2419", {"start": v(130.54, 584.89) * mm, "end": v(130.88, 584.6) * mm});
            skLineSegment(sketch, "E2420", {"start": v(130.88, 584.6) * mm, "end": v(131.21, 584.3) * mm});
            skLineSegment(sketch, "E2421", {"start": v(131.21, 584.3) * mm, "end": v(131.54, 583.99) * mm});
            skLineSegment(sketch, "E2422", {"start": v(131.54, 583.99) * mm, "end": v(131.8, 583.73) * mm});
            skLineSegment(sketch, "E2423", {"start": v(131.8, 583.73) * mm, "end": v(132.04, 583.47) * mm});
            skLineSegment(sketch, "E2424", {"start": v(132.04, 583.47) * mm, "end": v(132.28, 583.2) * mm});
            skLineSegment(sketch, "E2425", {"start": v(132.28, 583.2) * mm, "end": v(132.52, 582.92) * mm});
            skLineSegment(sketch, "E2426", {"start": v(132.52, 582.92) * mm, "end": v(132.74, 582.64) * mm});
            skLineSegment(sketch, "E2427", {"start": v(132.74, 582.64) * mm, "end": v(132.96, 582.36) * mm});
            skLineSegment(sketch, "E2428", {"start": v(132.96, 582.36) * mm, "end": v(133.17, 582.07) * mm});
            skLineSegment(sketch, "E2429", {"start": v(133.17, 582.07) * mm, "end": v(133.38, 581.77) * mm});
            skLineSegment(sketch, "E2430", {"start": v(133.38, 581.77) * mm, "end": v(133.57, 581.47) * mm});
            skLineSegment(sketch, "E2431", {"start": v(133.57, 581.47) * mm, "end": v(133.76, 581.17) * mm});
            skLineSegment(sketch, "E2432", {"start": v(133.76, 581.17) * mm, "end": v(133.94, 580.86) * mm});
            skLineSegment(sketch, "E2433", {"start": v(133.94, 580.86) * mm, "end": v(134.11, 580.55) * mm});
            skLineSegment(sketch, "E2434", {"start": v(134.11, 580.55) * mm, "end": v(134.28, 580.23) * mm});
            skLineSegment(sketch, "E2435", {"start": v(134.28, 580.23) * mm, "end": v(134.44, 579.91) * mm});
            skLineSegment(sketch, "E2436", {"start": v(134.44, 579.91) * mm, "end": v(134.59, 579.59) * mm});
            skLineSegment(sketch, "E2437", {"start": v(134.59, 579.59) * mm, "end": v(134.73, 579.26) * mm});
            skLineSegment(sketch, "E2438", {"start": v(134.73, 579.26) * mm, "end": v(134.86, 578.93) * mm});
            skLineSegment(sketch, "E2439", {"start": v(134.86, 578.93) * mm, "end": v(134.98, 578.6) * mm});
            skLineSegment(sketch, "E2440", {"start": v(134.98, 578.6) * mm, "end": v(135.1, 578.26) * mm});
            skLineSegment(sketch, "E2441", {"start": v(135.1, 578.26) * mm, "end": v(135.2, 577.92) * mm});
            skLineSegment(sketch, "E2442", {"start": v(135.2, 577.92) * mm, "end": v(135.3, 577.58) * mm});
            skLineSegment(sketch, "E2443", {"start": v(135.3, 577.58) * mm, "end": v(135.4, 577.23) * mm});
            skLineSegment(sketch, "E2444", {"start": v(135.4, 577.23) * mm, "end": v(135.48, 576.88) * mm});
            skLineSegment(sketch, "E2445", {"start": v(135.48, 576.88) * mm, "end": v(135.55, 576.53) * mm});
            skLineSegment(sketch, "E2446", {"start": v(135.55, 576.53) * mm, "end": v(135.62, 576.18) * mm});
            skLineSegment(sketch, "E2447", {"start": v(135.62, 576.18) * mm, "end": v(135.68, 575.83) * mm});
            skLineSegment(sketch, "E2448", {"start": v(135.68, 575.83) * mm, "end": v(135.72, 575.47) * mm});
            skLineSegment(sketch, "E2449", {"start": v(135.72, 575.47) * mm, "end": v(135.76, 575.11) * mm});
            skLineSegment(sketch, "E2450", {"start": v(135.76, 575.11) * mm, "end": v(135.8, 574.75) * mm});
            skLineSegment(sketch, "E2451", {"start": v(135.8, 574.75) * mm, "end": v(135.81, 574.4) * mm});
            skLineSegment(sketch, "E2452", {"start": v(135.81, 574.4) * mm, "end": v(135.82, 574.03) * mm});
            skLineSegment(sketch, "E2453", {"start": v(135.82, 574.03) * mm, "end": v(135.83, 573.67) * mm});
            skLineSegment(sketch, "E2454", {"start": v(135.34, 596.92) * mm, "end": v(100.37, 596.92) * mm});
            skLineSegment(sketch, "E2455", {"start": v(100.37, 596.92) * mm, "end": v(100.37, 612.29) * mm});
            skLineSegment(sketch, "E2456", {"start": v(100.37, 612.29) * mm, "end": v(100.38, 612.72) * mm});
            skLineSegment(sketch, "E2457", {"start": v(100.38, 612.72) * mm, "end": v(100.4, 613.15) * mm});
            skLineSegment(sketch, "E2458", {"start": v(100.4, 613.15) * mm, "end": v(100.45, 613.58) * mm});
            skLineSegment(sketch, "E2459", {"start": v(100.45, 613.58) * mm, "end": v(100.52, 614) * mm});
            skLineSegment(sketch, "E2460", {"start": v(100.52, 614) * mm, "end": v(100.6, 614.42) * mm});
            skLineSegment(sketch, "E2461", {"start": v(100.6, 614.42) * mm, "end": v(100.72, 614.83) * mm});
            skLineSegment(sketch, "E2462", {"start": v(100.72, 614.83) * mm, "end": v(100.85, 615.23) * mm});
            skLineSegment(sketch, "E2463", {"start": v(100.85, 615.23) * mm, "end": v(101, 615.63) * mm});
            skLineSegment(sketch, "E2464", {"start": v(101, 615.63) * mm, "end": v(101.17, 616.02) * mm});
            skLineSegment(sketch, "E2465", {"start": v(101.17, 616.02) * mm, "end": v(101.37, 616.4) * mm});
            skLineSegment(sketch, "E2466", {"start": v(101.37, 616.4) * mm, "end": v(101.58, 616.77) * mm});
            skLineSegment(sketch, "E2467", {"start": v(101.58, 616.77) * mm, "end": v(101.8, 617.13) * mm});
            skLineSegment(sketch, "E2468", {"start": v(101.8, 617.13) * mm, "end": v(102.06, 617.48) * mm});
            skLineSegment(sketch, "E2469", {"start": v(102.06, 617.48) * mm, "end": v(102.32, 617.82) * mm});
            skLineSegment(sketch, "E2470", {"start": v(102.32, 617.82) * mm, "end": v(102.6, 618.14) * mm});
            skLineSegment(sketch, "E2471", {"start": v(102.6, 618.14) * mm, "end": v(102.91, 618.45) * mm});
            skLineSegment(sketch, "E2472", {"start": v(102.91, 618.45) * mm, "end": v(103.22, 618.75) * mm});
            skLineSegment(sketch, "E2473", {"start": v(103.22, 618.75) * mm, "end": v(103.54, 619.03) * mm});
            skLineSegment(sketch, "E2474", {"start": v(103.54, 619.03) * mm, "end": v(103.87, 619.3) * mm});
            skLineSegment(sketch, "E2475", {"start": v(103.87, 619.3) * mm, "end": v(104.22, 619.54) * mm});
            skLineSegment(sketch, "E2476", {"start": v(104.22, 619.54) * mm, "end": v(104.58, 619.77) * mm});
            skLineSegment(sketch, "E2477", {"start": v(104.58, 619.77) * mm, "end": v(104.94, 619.98) * mm});
            skLineSegment(sketch, "E2478", {"start": v(104.94, 619.98) * mm, "end": v(105.32, 620.17) * mm});
            skLineSegment(sketch, "E2479", {"start": v(105.32, 620.17) * mm, "end": v(105.7, 620.34) * mm});
            skLineSegment(sketch, "E2480", {"start": v(105.7, 620.34) * mm, "end": v(106.1, 620.5) * mm});
            skLineSegment(sketch, "E2481", {"start": v(106.1, 620.5) * mm, "end": v(106.5, 620.63) * mm});
            skLineSegment(sketch, "E2482", {"start": v(106.5, 620.63) * mm, "end": v(106.9, 620.74) * mm});
            skLineSegment(sketch, "E2483", {"start": v(106.9, 620.74) * mm, "end": v(107.32, 620.83) * mm});
            skLineSegment(sketch, "E2484", {"start": v(107.32, 620.83) * mm, "end": v(107.74, 620.9) * mm});
            skLineSegment(sketch, "E2485", {"start": v(107.74, 620.9) * mm, "end": v(108.16, 620.96) * mm});
            skLineSegment(sketch, "E2486", {"start": v(108.16, 620.96) * mm, "end": v(108.59, 621) * mm});
            skLineSegment(sketch, "E2487", {"start": v(108.59, 621) * mm, "end": v(109.01, 621) * mm});
            skLineSegment(sketch, "E2488", {"start": v(109.01, 621) * mm, "end": v(109.45, 621) * mm});
            skLineSegment(sketch, "E2489", {"start": v(109.45, 621) * mm, "end": v(109.9, 620.98) * mm});
            skLineSegment(sketch, "E2490", {"start": v(109.9, 620.98) * mm, "end": v(110.32, 620.94) * mm});
            skLineSegment(sketch, "E2491", {"start": v(110.32, 620.94) * mm, "end": v(110.75, 620.88) * mm});
            skLineSegment(sketch, "E2492", {"start": v(110.75, 620.88) * mm, "end": v(111.18, 620.8) * mm});
            skLineSegment(sketch, "E2493", {"start": v(111.18, 620.8) * mm, "end": v(111.6, 620.69) * mm});
            skLineSegment(sketch, "E2494", {"start": v(111.6, 620.69) * mm, "end": v(112.01, 620.56) * mm});
            skLineSegment(sketch, "E2495", {"start": v(112.01, 620.56) * mm, "end": v(112.42, 620.4) * mm});
            skLineSegment(sketch, "E2496", {"start": v(112.42, 620.4) * mm, "end": v(112.82, 620.24) * mm});
            skLineSegment(sketch, "E2497", {"start": v(112.82, 620.24) * mm, "end": v(113.2, 620.05) * mm});
            skLineSegment(sketch, "E2498", {"start": v(113.2, 620.05) * mm, "end": v(113.59, 619.84) * mm});
            skLineSegment(sketch, "E2499", {"start": v(113.59, 619.84) * mm, "end": v(113.95, 619.62) * mm});
            skLineSegment(sketch, "E2500", {"start": v(113.95, 619.62) * mm, "end": v(114.31, 619.37) * mm});
            skLineSegment(sketch, "E2501", {"start": v(114.31, 619.37) * mm, "end": v(114.66, 619.1) * mm});
            skLineSegment(sketch, "E2502", {"start": v(114.66, 619.1) * mm, "end": v(115, 618.82) * mm});
            skLineSegment(sketch, "E2503", {"start": v(115, 618.82) * mm, "end": v(115.31, 618.52) * mm});
            skLineSegment(sketch, "E2504", {"start": v(115.31, 618.52) * mm, "end": v(115.61, 618.2) * mm});
            skLineSegment(sketch, "E2505", {"start": v(115.61, 618.2) * mm, "end": v(115.9, 617.88) * mm});
            skLineSegment(sketch, "E2506", {"start": v(115.9, 617.88) * mm, "end": v(116.16, 617.53) * mm});
            skLineSegment(sketch, "E2507", {"start": v(116.16, 617.53) * mm, "end": v(116.4, 617.18) * mm});
            skLineSegment(sketch, "E2508", {"start": v(116.4, 617.18) * mm, "end": v(116.64, 616.82) * mm});
            skLineSegment(sketch, "E2509", {"start": v(116.64, 616.82) * mm, "end": v(116.85, 616.44) * mm});
            skLineSegment(sketch, "E2510", {"start": v(116.85, 616.44) * mm, "end": v(117.04, 616.05) * mm});
            skLineSegment(sketch, "E2511", {"start": v(117.04, 616.05) * mm, "end": v(117.21, 615.66) * mm});
            skLineSegment(sketch, "E2512", {"start": v(117.21, 615.66) * mm, "end": v(117.36, 615.26) * mm});
            skLineSegment(sketch, "E2513", {"start": v(117.36, 615.26) * mm, "end": v(117.5, 614.85) * mm});
            skLineSegment(sketch, "E2514", {"start": v(117.5, 614.85) * mm, "end": v(117.6, 614.43) * mm});
            skLineSegment(sketch, "E2515", {"start": v(117.6, 614.43) * mm, "end": v(117.7, 614.01) * mm});
            skLineSegment(sketch, "E2516", {"start": v(117.7, 614.01) * mm, "end": v(117.77, 613.59) * mm});
            skLineSegment(sketch, "E2517", {"start": v(117.77, 613.59) * mm, "end": v(117.82, 613.16) * mm});
            skLineSegment(sketch, "E2518", {"start": v(117.82, 613.16) * mm, "end": v(117.84, 612.72) * mm});
            skLineSegment(sketch, "E2519", {"start": v(117.84, 612.72) * mm, "end": v(117.85, 612.29) * mm});
            skLineSegment(sketch, "E2520", {"start": v(117.85, 612.29) * mm, "end": v(117.85, 596.92) * mm});
            skLineSegment(sketch, "E2521", {"start": v(117.85, 612.29) * mm, "end": v(117.85, 612.65) * mm});
            skLineSegment(sketch, "E2522", {"start": v(117.85, 612.65) * mm, "end": v(117.87, 613) * mm});
            skLineSegment(sketch, "E2523", {"start": v(117.87, 613) * mm, "end": v(117.9, 613.36) * mm});
            skLineSegment(sketch, "E2524", {"start": v(117.9, 613.36) * mm, "end": v(117.96, 613.7) * mm});
            skLineSegment(sketch, "E2525", {"start": v(117.96, 613.7) * mm, "end": v(118.04, 614.05) * mm});
            skLineSegment(sketch, "E2526", {"start": v(118.04, 614.05) * mm, "end": v(118.13, 614.4) * mm});
            skLineSegment(sketch, "E2527", {"start": v(118.13, 614.4) * mm, "end": v(118.24, 614.73) * mm});
            skLineSegment(sketch, "E2528", {"start": v(118.24, 614.73) * mm, "end": v(118.36, 615.06) * mm});
            skLineSegment(sketch, "E2529", {"start": v(118.36, 615.06) * mm, "end": v(118.5, 615.39) * mm});
            skLineSegment(sketch, "E2530", {"start": v(118.5, 615.39) * mm, "end": v(118.66, 615.7) * mm});
            skLineSegment(sketch, "E2531", {"start": v(118.66, 615.7) * mm, "end": v(118.83, 616.01) * mm});
            skLineSegment(sketch, "E2532", {"start": v(118.83, 616.01) * mm, "end": v(119.02, 616.31) * mm});
            skLineSegment(sketch, "E2533", {"start": v(119.02, 616.31) * mm, "end": v(119.23, 616.6) * mm});
            skLineSegment(sketch, "E2534", {"start": v(119.23, 616.6) * mm, "end": v(119.45, 616.88) * mm});
            skLineSegment(sketch, "E2535", {"start": v(119.45, 616.88) * mm, "end": v(119.68, 617.15) * mm});
            skLineSegment(sketch, "E2536", {"start": v(119.68, 617.15) * mm, "end": v(119.93, 617.4) * mm});
            skLineSegment(sketch, "E2537", {"start": v(119.93, 617.4) * mm, "end": v(120.37, 617.7) * mm});
            skLineSegment(sketch, "E2538", {"start": v(120.37, 617.7) * mm, "end": v(120.82, 617.98) * mm});
            skLineSegment(sketch, "E2539", {"start": v(120.82, 617.98) * mm, "end": v(121.28, 618.24) * mm});
            skLineSegment(sketch, "E2540", {"start": v(121.28, 618.24) * mm, "end": v(121.75, 618.47) * mm});
            skLineSegment(sketch, "E2541", {"start": v(121.75, 618.47) * mm, "end": v(122.23, 618.69) * mm});
            skLineSegment(sketch, "E2542", {"start": v(122.23, 618.69) * mm, "end": v(122.72, 618.88) * mm});
            skLineSegment(sketch, "E2543", {"start": v(122.72, 618.88) * mm, "end": v(123.21, 619.05) * mm});
            skLineSegment(sketch, "E2544", {"start": v(123.21, 619.05) * mm, "end": v(123.71, 619.2) * mm});
            skLineSegment(sketch, "E2545", {"start": v(123.71, 619.2) * mm, "end": v(124.22, 619.32) * mm});
            skLineSegment(sketch, "E2546", {"start": v(124.22, 619.32) * mm, "end": v(124.74, 619.43) * mm});
            skLineSegment(sketch, "E2547", {"start": v(124.74, 619.43) * mm, "end": v(125.25, 619.5) * mm});
            skLineSegment(sketch, "E2548", {"start": v(125.25, 619.5) * mm, "end": v(125.78, 619.57) * mm});
            skLineSegment(sketch, "E2549", {"start": v(125.78, 619.57) * mm, "end": v(126.3, 619.6) * mm});
            skLineSegment(sketch, "E2550", {"start": v(126.3, 619.6) * mm, "end": v(126.83, 619.61) * mm});
            skLineSegment(sketch, "E2551", {"start": v(126.83, 619.61) * mm, "end": v(127.35, 619.6) * mm});
            skLineSegment(sketch, "E2552", {"start": v(127.35, 619.6) * mm, "end": v(127.88, 619.56) * mm});
            skLineSegment(sketch, "E2553", {"start": v(127.88, 619.56) * mm, "end": v(128.35, 619.55) * mm});
            skLineSegment(sketch, "E2554", {"start": v(128.35, 619.55) * mm, "end": v(128.82, 619.55) * mm});
            skLineSegment(sketch, "E2555", {"start": v(128.82, 619.55) * mm, "end": v(129.3, 619.56) * mm});
            skLineSegment(sketch, "E2556", {"start": v(129.3, 619.56) * mm, "end": v(129.76, 619.58) * mm});
            skLineSegment(sketch, "E2557", {"start": v(129.76, 619.58) * mm, "end": v(130.23, 619.61) * mm});
            skLineSegment(sketch, "E2558", {"start": v(130.23, 619.61) * mm, "end": v(130.7, 619.65) * mm});
            skLineSegment(sketch, "E2559", {"start": v(130.7, 619.65) * mm, "end": v(131.17, 619.69) * mm});
            skLineSegment(sketch, "E2560", {"start": v(131.17, 619.69) * mm, "end": v(131.64, 619.74) * mm});
            skLineSegment(sketch, "E2561", {"start": v(131.64, 619.74) * mm, "end": v(132.1, 619.8) * mm});
            skLineSegment(sketch, "E2562", {"start": v(132.1, 619.8) * mm, "end": v(132.58, 619.87) * mm});
            skLineSegment(sketch, "E2563", {"start": v(132.58, 619.87) * mm, "end": v(133.04, 619.95) * mm});
            skLineSegment(sketch, "E2564", {"start": v(133.04, 619.95) * mm, "end": v(133.5, 620.04) * mm});
            skLineSegment(sketch, "E2565", {"start": v(133.5, 620.04) * mm, "end": v(133.96, 620.13) * mm});
            skLineSegment(sketch, "E2566", {"start": v(133.96, 620.13) * mm, "end": v(134.42, 620.23) * mm});
            skLineSegment(sketch, "E2567", {"start": v(134.42, 620.23) * mm, "end": v(134.88, 620.34) * mm});
            skLineSegment(sketch, "E2568", {"start": v(134.88, 620.34) * mm, "end": v(135.34, 620.46) * mm});
            skLineSegment(sketch, "E2569", {"start": v(122.28, 628.7) * mm, "end": v(122.28, 652.83) * mm});
            skLineSegment(sketch, "E2570", {"start": v(135.77, 672.1) * mm, "end": v(135.77, 671.58) * mm});
            skLineSegment(sketch, "E2571", {"start": v(135.77, 671.58) * mm, "end": v(135.75, 671.07) * mm});
            skLineSegment(sketch, "E2572", {"start": v(135.75, 671.07) * mm, "end": v(135.7, 670.56) * mm});
            skLineSegment(sketch, "E2573", {"start": v(135.7, 670.56) * mm, "end": v(135.62, 670.05) * mm});
            skLineSegment(sketch, "E2574", {"start": v(135.62, 670.05) * mm, "end": v(135.51, 669.56) * mm});
            skLineSegment(sketch, "E2575", {"start": v(135.51, 669.56) * mm, "end": v(135.39, 669.06) * mm});
            skLineSegment(sketch, "E2576", {"start": v(135.39, 669.06) * mm, "end": v(135.23, 668.58) * mm});
            skLineSegment(sketch, "E2577", {"start": v(135.23, 668.58) * mm, "end": v(135.06, 668.1) * mm});
            skLineSegment(sketch, "E2578", {"start": v(135.06, 668.1) * mm, "end": v(134.86, 667.64) * mm});
            skLineSegment(sketch, "E2579", {"start": v(134.86, 667.64) * mm, "end": v(134.63, 667.18) * mm});
            skLineSegment(sketch, "E2580", {"start": v(134.63, 667.18) * mm, "end": v(134.39, 666.74) * mm});
            skLineSegment(sketch, "E2581", {"start": v(134.39, 666.74) * mm, "end": v(134.12, 666.3) * mm});
            skLineSegment(sketch, "E2582", {"start": v(134.12, 666.3) * mm, "end": v(133.82, 665.89) * mm});
            skLineSegment(sketch, "E2583", {"start": v(133.82, 665.89) * mm, "end": v(133.51, 665.48) * mm});
            skLineSegment(sketch, "E2584", {"start": v(133.51, 665.48) * mm, "end": v(133.18, 665.1) * mm});
            skLineSegment(sketch, "E2585", {"start": v(133.18, 665.1) * mm, "end": v(132.82, 664.72) * mm});
            skLineSegment(sketch, "E2586", {"start": v(132.82, 664.72) * mm, "end": v(132.56, 664.47) * mm});
            skLineSegment(sketch, "E2587", {"start": v(132.56, 664.47) * mm, "end": v(132.3, 664.22) * mm});
            skLineSegment(sketch, "E2588", {"start": v(132.3, 664.22) * mm, "end": v(132.03, 663.97) * mm});
            skLineSegment(sketch, "E2589", {"start": v(132.03, 663.97) * mm, "end": v(131.76, 663.74) * mm});
            skLineSegment(sketch, "E2590", {"start": v(131.76, 663.74) * mm, "end": v(131.48, 663.5) * mm});
            skLineSegment(sketch, "E2591", {"start": v(131.48, 663.5) * mm, "end": v(131.2, 663.29) * mm});
            skLineSegment(sketch, "E2592", {"start": v(131.2, 663.29) * mm, "end": v(130.9, 663.08) * mm});
            skLineSegment(sketch, "E2593", {"start": v(130.9, 663.08) * mm, "end": v(130.6, 662.87) * mm});
            skLineSegment(sketch, "E2594", {"start": v(130.6, 662.87) * mm, "end": v(130.3, 662.68) * mm});
            skLineSegment(sketch, "E2595", {"start": v(130.3, 662.68) * mm, "end": v(130, 662.49) * mm});
            skLineSegment(sketch, "E2596", {"start": v(130, 662.49) * mm, "end": v(129.7, 662.3) * mm});
            skLineSegment(sketch, "E2597", {"start": v(129.7, 662.3) * mm, "end": v(129.38, 662.14) * mm});
            skLineSegment(sketch, "E2598", {"start": v(129.38, 662.14) * mm, "end": v(129.06, 661.97) * mm});
            skLineSegment(sketch, "E2599", {"start": v(129.06, 661.97) * mm, "end": v(128.74, 661.82) * mm});
            skLineSegment(sketch, "E2600", {"start": v(128.74, 661.82) * mm, "end": v(128.41, 661.67) * mm});
            skLineSegment(sketch, "E2601", {"start": v(128.41, 661.67) * mm, "end": v(128.08, 661.53) * mm});
            skLineSegment(sketch, "E2602", {"start": v(128.08, 661.53) * mm, "end": v(127.75, 661.4) * mm});
            skLineSegment(sketch, "E2603", {"start": v(127.75, 661.4) * mm, "end": v(127.41, 661.28) * mm});
            skLineSegment(sketch, "E2604", {"start": v(127.41, 661.28) * mm, "end": v(127.07, 661.17) * mm});
            skLineSegment(sketch, "E2605", {"start": v(127.07, 661.17) * mm, "end": v(126.73, 661.06) * mm});
            skLineSegment(sketch, "E2606", {"start": v(126.73, 661.06) * mm, "end": v(126.39, 660.97) * mm});
            skLineSegment(sketch, "E2607", {"start": v(126.39, 660.97) * mm, "end": v(126.04, 660.88) * mm});
            skLineSegment(sketch, "E2608", {"start": v(126.04, 660.88) * mm, "end": v(125.69, 660.8) * mm});
            skLineSegment(sketch, "E2609", {"start": v(125.69, 660.8) * mm, "end": v(125.33, 660.74) * mm});
            skLineSegment(sketch, "E2610", {"start": v(125.33, 660.74) * mm, "end": v(124.98, 660.68) * mm});
            skLineSegment(sketch, "E2611", {"start": v(124.98, 660.68) * mm, "end": v(124.62, 660.63) * mm});
            skLineSegment(sketch, "E2612", {"start": v(124.62, 660.63) * mm, "end": v(124.27, 660.59) * mm});
            skLineSegment(sketch, "E2613", {"start": v(124.27, 660.59) * mm, "end": v(123.9, 660.56) * mm});
            skLineSegment(sketch, "E2614", {"start": v(123.9, 660.56) * mm, "end": v(123.55, 660.54) * mm});
            skLineSegment(sketch, "E2615", {"start": v(123.55, 660.54) * mm, "end": v(123.18, 660.52) * mm});
            skLineSegment(sketch, "E2616", {"start": v(123.18, 660.52) * mm, "end": v(122.82, 660.52) * mm});
            skLineSegment(sketch, "E2617", {"start": v(122.82, 660.52) * mm, "end": v(122.46, 660.53) * mm});
            skLineSegment(sketch, "E2618", {"start": v(122.46, 660.53) * mm, "end": v(122.1, 660.51) * mm});
            skLineSegment(sketch, "E2619", {"start": v(122.1, 660.51) * mm, "end": v(121.73, 660.5) * mm});
            skLineSegment(sketch, "E2620", {"start": v(121.73, 660.5) * mm, "end": v(121.37, 660.51) * mm});
            skLineSegment(sketch, "E2621", {"start": v(121.37, 660.51) * mm, "end": v(121.01, 660.53) * mm});
            skLineSegment(sketch, "E2622", {"start": v(121.01, 660.53) * mm, "end": v(120.65, 660.55) * mm});
            skLineSegment(sketch, "E2623", {"start": v(120.65, 660.55) * mm, "end": v(120.3, 660.58) * mm});
            skLineSegment(sketch, "E2624", {"start": v(120.3, 660.58) * mm, "end": v(119.94, 660.62) * mm});
            skLineSegment(sketch, "E2625", {"start": v(119.94, 660.62) * mm, "end": v(119.58, 660.67) * mm});
            skLineSegment(sketch, "E2626", {"start": v(119.58, 660.67) * mm, "end": v(119.23, 660.72) * mm});
            skLineSegment(sketch, "E2627", {"start": v(119.23, 660.72) * mm, "end": v(118.88, 660.79) * mm});
            skLineSegment(sketch, "E2628", {"start": v(118.88, 660.79) * mm, "end": v(118.53, 660.86) * mm});
            skLineSegment(sketch, "E2629", {"start": v(118.53, 660.86) * mm, "end": v(118.18, 660.94) * mm});
            skLineSegment(sketch, "E2630", {"start": v(118.18, 660.94) * mm, "end": v(117.83, 661.04) * mm});
            skLineSegment(sketch, "E2631", {"start": v(117.83, 661.04) * mm, "end": v(117.5, 661.13) * mm});
            skLineSegment(sketch, "E2632", {"start": v(117.5, 661.13) * mm, "end": v(117.15, 661.24) * mm});
            skLineSegment(sketch, "E2633", {"start": v(117.15, 661.24) * mm, "end": v(116.81, 661.36) * mm});
            skLineSegment(sketch, "E2634", {"start": v(116.81, 661.36) * mm, "end": v(116.48, 661.48) * mm});
            skLineSegment(sketch, "E2635", {"start": v(116.48, 661.48) * mm, "end": v(116.14, 661.61) * mm});
            skLineSegment(sketch, "E2636", {"start": v(116.14, 661.61) * mm, "end": v(115.82, 661.75) * mm});
            skLineSegment(sketch, "E2637", {"start": v(115.82, 661.75) * mm, "end": v(115.5, 661.9) * mm});
            skLineSegment(sketch, "E2638", {"start": v(115.5, 661.9) * mm, "end": v(115.17, 662.06) * mm});
            skLineSegment(sketch, "E2639", {"start": v(115.17, 662.06) * mm, "end": v(114.85, 662.22) * mm});
            skLineSegment(sketch, "E2640", {"start": v(114.85, 662.22) * mm, "end": v(114.54, 662.4) * mm});
            skLineSegment(sketch, "E2641", {"start": v(114.54, 662.4) * mm, "end": v(114.23, 662.57) * mm});
            skLineSegment(sketch, "E2642", {"start": v(114.23, 662.57) * mm, "end": v(113.92, 662.76) * mm});
            skLineSegment(sketch, "E2643", {"start": v(113.92, 662.76) * mm, "end": v(113.62, 662.95) * mm});
            skLineSegment(sketch, "E2644", {"start": v(113.62, 662.95) * mm, "end": v(113.32, 663.15) * mm});
            skLineSegment(sketch, "E2645", {"start": v(113.32, 663.15) * mm, "end": v(113.03, 663.36) * mm});
            skLineSegment(sketch, "E2646", {"start": v(113.03, 663.36) * mm, "end": v(112.74, 663.58) * mm});
            skLineSegment(sketch, "E2647", {"start": v(112.74, 663.58) * mm, "end": v(112.46, 663.8) * mm});
            skLineSegment(sketch, "E2648", {"start": v(112.46, 663.8) * mm, "end": v(112.18, 664.04) * mm});
            skLineSegment(sketch, "E2649", {"start": v(112.18, 664.04) * mm, "end": v(111.91, 664.28) * mm});
            skLineSegment(sketch, "E2650", {"start": v(111.91, 664.28) * mm, "end": v(111.55, 664.68) * mm});
            skLineSegment(sketch, "E2651", {"start": v(111.55, 664.68) * mm, "end": v(111.2, 665.1) * mm});
            skLineSegment(sketch, "E2652", {"start": v(111.2, 665.1) * mm, "end": v(110.88, 665.53) * mm});
            skLineSegment(sketch, "E2653", {"start": v(110.88, 665.53) * mm, "end": v(110.58, 665.98) * mm});
            skLineSegment(sketch, "E2654", {"start": v(110.58, 665.98) * mm, "end": v(110.3, 666.44) * mm});
            skLineSegment(sketch, "E2655", {"start": v(110.3, 666.44) * mm, "end": v(110.05, 666.9) * mm});
            skLineSegment(sketch, "E2656", {"start": v(110.05, 666.9) * mm, "end": v(109.81, 667.4) * mm});
            skLineSegment(sketch, "E2657", {"start": v(109.81, 667.4) * mm, "end": v(109.6, 667.89) * mm});
            skLineSegment(sketch, "E2658", {"start": v(109.6, 667.89) * mm, "end": v(109.42, 668.39) * mm});
            skLineSegment(sketch, "E2659", {"start": v(109.42, 668.39) * mm, "end": v(109.25, 668.9) * mm});
            skLineSegment(sketch, "E2660", {"start": v(109.25, 668.9) * mm, "end": v(109.12, 669.42) * mm});
            skLineSegment(sketch, "E2661", {"start": v(109.12, 669.42) * mm, "end": v(109, 669.94) * mm});
            skLineSegment(sketch, "E2662", {"start": v(109, 669.94) * mm, "end": v(108.91, 670.48) * mm});
            skLineSegment(sketch, "E2663", {"start": v(108.91, 670.48) * mm, "end": v(108.85, 671.01) * mm});
            skLineSegment(sketch, "E2664", {"start": v(108.85, 671.01) * mm, "end": v(108.81, 671.55) * mm});
            skLineSegment(sketch, "E2665", {"start": v(108.81, 671.55) * mm, "end": v(108.8, 672.1) * mm});
            skLineSegment(sketch, "E2666", {"start": v(108.8, 672.1) * mm, "end": v(108.82, 672.62) * mm});
            skLineSegment(sketch, "E2667", {"start": v(108.82, 672.62) * mm, "end": v(108.88, 673.14) * mm});
            skLineSegment(sketch, "E2668", {"start": v(108.88, 673.14) * mm, "end": v(108.96, 673.66) * mm});
            skLineSegment(sketch, "E2669", {"start": v(108.96, 673.66) * mm, "end": v(109.06, 674.17) * mm});
            skLineSegment(sketch, "E2670", {"start": v(109.06, 674.17) * mm, "end": v(109.2, 674.67) * mm});
            skLineSegment(sketch, "E2671", {"start": v(109.2, 674.67) * mm, "end": v(109.36, 675.17) * mm});
            skLineSegment(sketch, "E2672", {"start": v(109.36, 675.17) * mm, "end": v(109.54, 675.65) * mm});
            skLineSegment(sketch, "E2673", {"start": v(109.54, 675.65) * mm, "end": v(109.75, 676.12) * mm});
            skLineSegment(sketch, "E2674", {"start": v(109.75, 676.12) * mm, "end": v(109.98, 676.59) * mm});
            skLineSegment(sketch, "E2675", {"start": v(109.98, 676.59) * mm, "end": v(110.24, 677.04) * mm});
            skLineSegment(sketch, "E2676", {"start": v(110.24, 677.04) * mm, "end": v(110.52, 677.47) * mm});
            skLineSegment(sketch, "E2677", {"start": v(110.52, 677.47) * mm, "end": v(110.83, 677.9) * mm});
            skLineSegment(sketch, "E2678", {"start": v(110.83, 677.9) * mm, "end": v(111.15, 678.3) * mm});
            skLineSegment(sketch, "E2679", {"start": v(111.15, 678.3) * mm, "end": v(111.5, 678.7) * mm});
            skLineSegment(sketch, "E2680", {"start": v(111.5, 678.7) * mm, "end": v(111.87, 679.06) * mm});
            skLineSegment(sketch, "E2681", {"start": v(111.87, 679.06) * mm, "end": v(112.26, 679.42) * mm});
            skLineSegment(sketch, "E2682", {"start": v(112.26, 679.42) * mm, "end": v(112.52, 679.66) * mm});
            skLineSegment(sketch, "E2683", {"start": v(112.52, 679.66) * mm, "end": v(112.78, 679.9) * mm});
            skLineSegment(sketch, "E2684", {"start": v(112.78, 679.9) * mm, "end": v(113.05, 680.12) * mm});
            skLineSegment(sketch, "E2685", {"start": v(113.05, 680.12) * mm, "end": v(113.33, 680.33) * mm});
            skLineSegment(sketch, "E2686", {"start": v(113.33, 680.33) * mm, "end": v(113.6, 680.54) * mm});
            skLineSegment(sketch, "E2687", {"start": v(113.6, 680.54) * mm, "end": v(113.9, 680.75) * mm});
            skLineSegment(sketch, "E2688", {"start": v(113.9, 680.75) * mm, "end": v(114.18, 680.94) * mm});
            skLineSegment(sketch, "E2689", {"start": v(114.18, 680.94) * mm, "end": v(114.47, 681.13) * mm});
            skLineSegment(sketch, "E2690", {"start": v(114.47, 681.13) * mm, "end": v(114.77, 681.3) * mm});
            skLineSegment(sketch, "E2691", {"start": v(114.77, 681.3) * mm, "end": v(115.07, 681.48) * mm});
            skLineSegment(sketch, "E2692", {"start": v(115.07, 681.48) * mm, "end": v(115.38, 681.64) * mm});
            skLineSegment(sketch, "E2693", {"start": v(115.38, 681.64) * mm, "end": v(115.7, 681.8) * mm});
            skLineSegment(sketch, "E2694", {"start": v(115.7, 681.8) * mm, "end": v(116, 681.95) * mm});
            skLineSegment(sketch, "E2695", {"start": v(116, 681.95) * mm, "end": v(116.32, 682.09) * mm});
            skLineSegment(sketch, "E2696", {"start": v(116.32, 682.09) * mm, "end": v(116.65, 682.22) * mm});
            skLineSegment(sketch, "E2697", {"start": v(116.65, 682.22) * mm, "end": v(116.97, 682.34) * mm});
            skLineSegment(sketch, "E2698", {"start": v(116.97, 682.34) * mm, "end": v(117.3, 682.45) * mm});
            skLineSegment(sketch, "E2699", {"start": v(117.3, 682.45) * mm, "end": v(117.63, 682.56) * mm});
            skLineSegment(sketch, "E2700", {"start": v(117.63, 682.56) * mm, "end": v(117.96, 682.66) * mm});
            skLineSegment(sketch, "E2701", {"start": v(117.96, 682.66) * mm, "end": v(118.3, 682.75) * mm});
            skLineSegment(sketch, "E2702", {"start": v(118.3, 682.75) * mm, "end": v(118.63, 682.83) * mm});
            skLineSegment(sketch, "E2703", {"start": v(118.63, 682.83) * mm, "end": v(118.97, 682.9) * mm});
            skLineSegment(sketch, "E2704", {"start": v(118.97, 682.9) * mm, "end": v(119.32, 682.96) * mm});
            skLineSegment(sketch, "E2705", {"start": v(119.32, 682.96) * mm, "end": v(119.66, 683.02) * mm});
            skLineSegment(sketch, "E2706", {"start": v(119.66, 683.02) * mm, "end": v(120, 683.06) * mm});
            skLineSegment(sketch, "E2707", {"start": v(120, 683.06) * mm, "end": v(120.35, 683.1) * mm});
            skLineSegment(sketch, "E2708", {"start": v(120.35, 683.1) * mm, "end": v(120.7, 683.13) * mm});
            skLineSegment(sketch, "E2709", {"start": v(120.7, 683.13) * mm, "end": v(121.05, 683.15) * mm});
            skLineSegment(sketch, "E2710", {"start": v(121.05, 683.15) * mm, "end": v(121.4, 683.16) * mm});
            skLineSegment(sketch, "E2711", {"start": v(121.4, 683.16) * mm, "end": v(121.75, 683.16) * mm});
            skLineSegment(sketch, "E2712", {"start": v(121.75, 683.16) * mm, "end": v(122.1, 683.15) * mm});
            skLineSegment(sketch, "E2713", {"start": v(122.1, 683.15) * mm, "end": v(122.46, 683.13) * mm});
            skLineSegment(sketch, "E2714", {"start": v(122.46, 683.13) * mm, "end": v(122.8, 683.14) * mm});
            skLineSegment(sketch, "E2715", {"start": v(122.8, 683.14) * mm, "end": v(123.16, 683.14) * mm});
            skLineSegment(sketch, "E2716", {"start": v(123.16, 683.14) * mm, "end": v(123.5, 683.14) * mm});
            skLineSegment(sketch, "E2717", {"start": v(123.5, 683.14) * mm, "end": v(123.85, 683.12) * mm});
            skLineSegment(sketch, "E2718", {"start": v(123.85, 683.12) * mm, "end": v(124.2, 683.1) * mm});
            skLineSegment(sketch, "E2719", {"start": v(124.2, 683.1) * mm, "end": v(124.54, 683.07) * mm});
            skLineSegment(sketch, "E2720", {"start": v(124.54, 683.07) * mm, "end": v(124.89, 683.03) * mm});
            skLineSegment(sketch, "E2721", {"start": v(124.89, 683.03) * mm, "end": v(125.23, 682.98) * mm});
            skLineSegment(sketch, "E2722", {"start": v(125.23, 682.98) * mm, "end": v(125.57, 682.92) * mm});
            skLineSegment(sketch, "E2723", {"start": v(125.57, 682.92) * mm, "end": v(125.91, 682.85) * mm});
            skLineSegment(sketch, "E2724", {"start": v(125.91, 682.85) * mm, "end": v(126.25, 682.78) * mm});
            skLineSegment(sketch, "E2725", {"start": v(126.25, 682.78) * mm, "end": v(126.58, 682.7) * mm});
            skLineSegment(sketch, "E2726", {"start": v(126.58, 682.7) * mm, "end": v(126.91, 682.6) * mm});
            skLineSegment(sketch, "E2727", {"start": v(126.91, 682.6) * mm, "end": v(127.24, 682.5) * mm});
            skLineSegment(sketch, "E2728", {"start": v(127.24, 682.5) * mm, "end": v(127.57, 682.4) * mm});
            skLineSegment(sketch, "E2729", {"start": v(127.57, 682.4) * mm, "end": v(127.9, 682.28) * mm});
            skLineSegment(sketch, "E2730", {"start": v(127.9, 682.28) * mm, "end": v(128.22, 682.15) * mm});
            skLineSegment(sketch, "E2731", {"start": v(128.22, 682.15) * mm, "end": v(128.54, 682.02) * mm});
            skLineSegment(sketch, "E2732", {"start": v(128.54, 682.02) * mm, "end": v(128.85, 681.88) * mm});
            skLineSegment(sketch, "E2733", {"start": v(128.85, 681.88) * mm, "end": v(129.16, 681.73) * mm});
            skLineSegment(sketch, "E2734", {"start": v(129.16, 681.73) * mm, "end": v(129.47, 681.58) * mm});
            skLineSegment(sketch, "E2735", {"start": v(129.47, 681.58) * mm, "end": v(129.77, 681.41) * mm});
            skLineSegment(sketch, "E2736", {"start": v(129.77, 681.41) * mm, "end": v(130.07, 681.24) * mm});
            skLineSegment(sketch, "E2737", {"start": v(130.07, 681.24) * mm, "end": v(130.37, 681.06) * mm});
            skLineSegment(sketch, "E2738", {"start": v(130.37, 681.06) * mm, "end": v(130.66, 680.88) * mm});
            skLineSegment(sketch, "E2739", {"start": v(130.66, 680.88) * mm, "end": v(130.95, 680.68) * mm});
            skLineSegment(sketch, "E2740", {"start": v(130.95, 680.68) * mm, "end": v(131.23, 680.48) * mm});
            skLineSegment(sketch, "E2741", {"start": v(131.23, 680.48) * mm, "end": v(131.5, 680.28) * mm});
            skLineSegment(sketch, "E2742", {"start": v(131.5, 680.28) * mm, "end": v(131.78, 680.06) * mm});
            skLineSegment(sketch, "E2743", {"start": v(131.78, 680.06) * mm, "end": v(132.05, 679.84) * mm});
            skLineSegment(sketch, "E2744", {"start": v(132.05, 679.84) * mm, "end": v(132.31, 679.6) * mm});
            skLineSegment(sketch, "E2745", {"start": v(132.31, 679.6) * mm, "end": v(132.57, 679.37) * mm});
            skLineSegment(sketch, "E2746", {"start": v(132.57, 679.37) * mm, "end": v(132.94, 679) * mm});
            skLineSegment(sketch, "E2747", {"start": v(132.94, 679) * mm, "end": v(133.28, 678.63) * mm});
            skLineSegment(sketch, "E2748", {"start": v(133.28, 678.63) * mm, "end": v(133.61, 678.24) * mm});
            skLineSegment(sketch, "E2749", {"start": v(133.61, 678.24) * mm, "end": v(133.92, 677.83) * mm});
            skLineSegment(sketch, "E2750", {"start": v(133.92, 677.83) * mm, "end": v(134.2, 677.4) * mm});
            skLineSegment(sketch, "E2751", {"start": v(134.2, 677.4) * mm, "end": v(134.46, 676.97) * mm});
            skLineSegment(sketch, "E2752", {"start": v(134.46, 676.97) * mm, "end": v(134.7, 676.52) * mm});
            skLineSegment(sketch, "E2753", {"start": v(134.7, 676.52) * mm, "end": v(134.92, 676.06) * mm});
            skLineSegment(sketch, "E2754", {"start": v(134.92, 676.06) * mm, "end": v(135.11, 675.6) * mm});
            skLineSegment(sketch, "E2755", {"start": v(135.11, 675.6) * mm, "end": v(135.28, 675.11) * mm});
            skLineSegment(sketch, "E2756", {"start": v(135.28, 675.11) * mm, "end": v(135.43, 674.63) * mm});
            skLineSegment(sketch, "E2757", {"start": v(135.43, 674.63) * mm, "end": v(135.55, 674.13) * mm});
            skLineSegment(sketch, "E2758", {"start": v(135.55, 674.13) * mm, "end": v(135.64, 673.63) * mm});
            skLineSegment(sketch, "E2759", {"start": v(135.64, 673.63) * mm, "end": v(135.71, 673.12) * mm});
            skLineSegment(sketch, "E2760", {"start": v(135.71, 673.12) * mm, "end": v(135.75, 672.61) * mm});
            skLineSegment(sketch, "E2761", {"start": v(135.75, 672.61) * mm, "end": v(135.77, 672.1) * mm});
            skLineSegment(sketch, "E2762", {"start": v(135.35, 710.03) * mm, "end": v(109.22, 710.03) * mm});
            skLineSegment(sketch, "E2763", {"start": v(125.92, 710.03) * mm, "end": v(126.4, 710.01) * mm});
            skLineSegment(sketch, "E2764", {"start": v(126.4, 710.01) * mm, "end": v(126.87, 709.97) * mm});
            skLineSegment(sketch, "E2765", {"start": v(126.87, 709.97) * mm, "end": v(127.34, 709.9) * mm});
            skLineSegment(sketch, "E2766", {"start": v(127.34, 709.9) * mm, "end": v(127.8, 709.81) * mm});
            skLineSegment(sketch, "E2767", {"start": v(127.8, 709.81) * mm, "end": v(128.26, 709.7) * mm});
            skLineSegment(sketch, "E2768", {"start": v(128.26, 709.7) * mm, "end": v(128.71, 709.56) * mm});
            skLineSegment(sketch, "E2769", {"start": v(128.71, 709.56) * mm, "end": v(129.16, 709.4) * mm});
            skLineSegment(sketch, "E2770", {"start": v(129.16, 709.4) * mm, "end": v(129.6, 709.23) * mm});
            skLineSegment(sketch, "E2771", {"start": v(129.6, 709.23) * mm, "end": v(130.02, 709.03) * mm});
            skLineSegment(sketch, "E2772", {"start": v(130.02, 709.03) * mm, "end": v(130.43, 708.8) * mm});
            skLineSegment(sketch, "E2773", {"start": v(130.43, 708.8) * mm, "end": v(130.84, 708.56) * mm});
            skLineSegment(sketch, "E2774", {"start": v(130.84, 708.56) * mm, "end": v(131.23, 708.3) * mm});
            skLineSegment(sketch, "E2775", {"start": v(131.23, 708.3) * mm, "end": v(131.61, 708.02) * mm});
            skLineSegment(sketch, "E2776", {"start": v(131.61, 708.02) * mm, "end": v(131.98, 707.72) * mm});
            skLineSegment(sketch, "E2777", {"start": v(131.98, 707.72) * mm, "end": v(132.33, 707.4) * mm});
            skLineSegment(sketch, "E2778", {"start": v(132.33, 707.4) * mm, "end": v(132.67, 707.06) * mm});
            skLineSegment(sketch, "E2779", {"start": v(132.67, 707.06) * mm, "end": v(133, 706.72) * mm});
            skLineSegment(sketch, "E2780", {"start": v(133, 706.72) * mm, "end": v(133.32, 706.36) * mm});
            skLineSegment(sketch, "E2781", {"start": v(133.32, 706.36) * mm, "end": v(133.62, 705.98) * mm});
            skLineSegment(sketch, "E2782", {"start": v(133.62, 705.98) * mm, "end": v(133.9, 705.6) * mm});
            skLineSegment(sketch, "E2783", {"start": v(133.9, 705.6) * mm, "end": v(134.16, 705.2) * mm});
            skLineSegment(sketch, "E2784", {"start": v(134.16, 705.2) * mm, "end": v(134.4, 704.79) * mm});
            skLineSegment(sketch, "E2785", {"start": v(134.4, 704.79) * mm, "end": v(134.62, 704.36) * mm});
            skLineSegment(sketch, "E2786", {"start": v(134.62, 704.36) * mm, "end": v(134.82, 703.93) * mm});
            skLineSegment(sketch, "E2787", {"start": v(134.82, 703.93) * mm, "end": v(135, 703.49) * mm});
            skLineSegment(sketch, "E2788", {"start": v(135, 703.49) * mm, "end": v(135.15, 703.04) * mm});
            skLineSegment(sketch, "E2789", {"start": v(135.15, 703.04) * mm, "end": v(135.28, 702.58) * mm});
            skLineSegment(sketch, "E2790", {"start": v(135.28, 702.58) * mm, "end": v(135.39, 702.12) * mm});
            skLineSegment(sketch, "E2791", {"start": v(135.39, 702.12) * mm, "end": v(135.47, 701.65) * mm});
            skLineSegment(sketch, "E2792", {"start": v(135.47, 701.65) * mm, "end": v(135.54, 701.17) * mm});
            skLineSegment(sketch, "E2793", {"start": v(135.54, 701.17) * mm, "end": v(135.57, 700.7) * mm});
            skLineSegment(sketch, "E2794", {"start": v(135.57, 700.7) * mm, "end": v(135.59, 700.21) * mm});
            skLineSegment(sketch, "E2795", {"start": v(135.59, 700.21) * mm, "end": v(135.63, 699.74) * mm});
            skLineSegment(sketch, "E2796", {"start": v(135.63, 699.74) * mm, "end": v(135.64, 699.27) * mm});
            skLineSegment(sketch, "E2797", {"start": v(135.64, 699.27) * mm, "end": v(135.63, 698.8) * mm});
            skLineSegment(sketch, "E2798", {"start": v(135.63, 698.8) * mm, "end": v(135.6, 698.34) * mm});
            skLineSegment(sketch, "E2799", {"start": v(135.6, 698.34) * mm, "end": v(135.54, 697.87) * mm});
            skLineSegment(sketch, "E2800", {"start": v(135.54, 697.87) * mm, "end": v(135.46, 697.41) * mm});
            skLineSegment(sketch, "E2801", {"start": v(135.46, 697.41) * mm, "end": v(135.36, 696.96) * mm});
            skLineSegment(sketch, "E2802", {"start": v(135.36, 696.96) * mm, "end": v(135.23, 696.51) * mm});
            skLineSegment(sketch, "E2803", {"start": v(135.23, 696.51) * mm, "end": v(135.09, 696.07) * mm});
            skLineSegment(sketch, "E2804", {"start": v(135.09, 696.07) * mm, "end": v(134.92, 695.63) * mm});
            skLineSegment(sketch, "E2805", {"start": v(134.92, 695.63) * mm, "end": v(134.73, 695.2) * mm});
            skLineSegment(sketch, "E2806", {"start": v(134.73, 695.2) * mm, "end": v(134.52, 694.8) * mm});
            skLineSegment(sketch, "E2807", {"start": v(134.52, 694.8) * mm, "end": v(134.29, 694.38) * mm});
            skLineSegment(sketch, "E2808", {"start": v(134.29, 694.38) * mm, "end": v(134.04, 693.99) * mm});
            skLineSegment(sketch, "E2809", {"start": v(134.04, 693.99) * mm, "end": v(133.76, 693.6) * mm});
            skLineSegment(sketch, "E2810", {"start": v(133.76, 693.6) * mm, "end": v(133.47, 693.24) * mm});
            skLineSegment(sketch, "E2811", {"start": v(133.47, 693.24) * mm, "end": v(133.15, 692.95) * mm});
            skLineSegment(sketch, "E2812", {"start": v(133.15, 692.95) * mm, "end": v(132.82, 692.69) * mm});
            skLineSegment(sketch, "E2813", {"start": v(132.82, 692.69) * mm, "end": v(132.48, 692.44) * mm});
            skLineSegment(sketch, "E2814", {"start": v(132.48, 692.44) * mm, "end": v(132.13, 692.22) * mm});
            skLineSegment(sketch, "E2815", {"start": v(132.13, 692.22) * mm, "end": v(131.77, 692) * mm});
            skLineSegment(sketch, "E2816", {"start": v(131.77, 692) * mm, "end": v(131.4, 691.82) * mm});
            skLineSegment(sketch, "E2817", {"start": v(131.4, 691.82) * mm, "end": v(131.01, 691.65) * mm});
            skLineSegment(sketch, "E2818", {"start": v(131.01, 691.65) * mm, "end": v(130.62, 691.5) * mm});
            skLineSegment(sketch, "E2819", {"start": v(130.62, 691.5) * mm, "end": v(130.23, 691.37) * mm});
            skLineSegment(sketch, "E2820", {"start": v(130.23, 691.37) * mm, "end": v(129.83, 691.26) * mm});
            skLineSegment(sketch, "E2821", {"start": v(129.83, 691.26) * mm, "end": v(129.42, 691.17) * mm});
            skLineSegment(sketch, "E2822", {"start": v(129.42, 691.17) * mm, "end": v(129, 691.1) * mm});
            skLineSegment(sketch, "E2823", {"start": v(129, 691.1) * mm, "end": v(128.59, 691.05) * mm});
            skLineSegment(sketch, "E2824", {"start": v(128.59, 691.05) * mm, "end": v(128.17, 691.02) * mm});
            skLineSegment(sketch, "E2825", {"start": v(128.17, 691.02) * mm, "end": v(127.75, 691.02) * mm});
            skLineSegment(sketch, "E2826", {"start": v(127.75, 691.02) * mm, "end": v(127.32, 691.03) * mm});
            skLineSegment(sketch, "E2827", {"start": v(127.32, 691.03) * mm, "end": v(109.22, 691.03) * mm});
            skLineSegment(sketch, "E2828", {"start": v(135.21, 726.37) * mm, "end": v(135.34, 726.14) * mm});
            skLineSegment(sketch, "E2829", {"start": v(135.34, 726.14) * mm, "end": v(135.44, 725.9) * mm});
            skLineSegment(sketch, "E2830", {"start": v(135.44, 725.9) * mm, "end": v(135.53, 725.66) * mm});
            skLineSegment(sketch, "E2831", {"start": v(135.53, 725.66) * mm, "end": v(135.6, 725.4) * mm});
            skLineSegment(sketch, "E2832", {"start": v(135.6, 725.4) * mm, "end": v(135.66, 725.15) * mm});
            skLineSegment(sketch, "E2833", {"start": v(135.66, 725.15) * mm, "end": v(135.7, 724.9) * mm});
            skLineSegment(sketch, "E2834", {"start": v(135.7, 724.9) * mm, "end": v(135.72, 724.63) * mm});
            skLineSegment(sketch, "E2835", {"start": v(135.72, 724.63) * mm, "end": v(135.72, 724.37) * mm});
            skLineSegment(sketch, "E2836", {"start": v(135.72, 724.37) * mm, "end": v(135.71, 724.18) * mm});
            skLineSegment(sketch, "E2837", {"start": v(135.71, 724.18) * mm, "end": v(135.7, 723.99) * mm});
            skLineSegment(sketch, "E2838", {"start": v(135.7, 723.99) * mm, "end": v(135.68, 723.8) * mm});
            skLineSegment(sketch, "E2839", {"start": v(135.68, 723.8) * mm, "end": v(135.66, 723.62) * mm});
            skLineSegment(sketch, "E2840", {"start": v(135.66, 723.62) * mm, "end": v(135.62, 723.43) * mm});
            skLineSegment(sketch, "E2841", {"start": v(135.62, 723.43) * mm, "end": v(135.58, 723.25) * mm});
            skLineSegment(sketch, "E2842", {"start": v(135.58, 723.25) * mm, "end": v(135.53, 723.07) * mm});
            skLineSegment(sketch, "E2843", {"start": v(135.53, 723.07) * mm, "end": v(135.46, 722.89) * mm});
            skLineSegment(sketch, "E2844", {"start": v(135.46, 722.89) * mm, "end": v(135.4, 722.71) * mm});
            skLineSegment(sketch, "E2845", {"start": v(135.4, 722.71) * mm, "end": v(135.32, 722.54) * mm});
            skLineSegment(sketch, "E2846", {"start": v(135.32, 722.54) * mm, "end": v(135.24, 722.37) * mm});
            skLineSegment(sketch, "E2847", {"start": v(135.24, 722.37) * mm, "end": v(135.15, 722.2) * mm});
            skLineSegment(sketch, "E2848", {"start": v(135.15, 722.2) * mm, "end": v(135.05, 722.05) * mm});
            skLineSegment(sketch, "E2849", {"start": v(135.05, 722.05) * mm, "end": v(134.94, 721.9) * mm});
            skLineSegment(sketch, "E2850", {"start": v(134.94, 721.9) * mm, "end": v(134.83, 721.74) * mm});
            skLineSegment(sketch, "E2851", {"start": v(134.83, 721.74) * mm, "end": v(134.7, 721.6) * mm});
            skLineSegment(sketch, "E2852", {"start": v(134.7, 721.6) * mm, "end": v(134.59, 721.47) * mm});
            skLineSegment(sketch, "E2853", {"start": v(134.59, 721.47) * mm, "end": v(134.46, 721.36) * mm});
            skLineSegment(sketch, "E2854", {"start": v(134.46, 721.36) * mm, "end": v(134.33, 721.25) * mm});
            skLineSegment(sketch, "E2855", {"start": v(134.33, 721.25) * mm, "end": v(134.2, 721.15) * mm});
            skLineSegment(sketch, "E2856", {"start": v(134.2, 721.15) * mm, "end": v(134.05, 721.06) * mm});
            skLineSegment(sketch, "E2857", {"start": v(134.05, 721.06) * mm, "end": v(133.9, 720.98) * mm});
            skLineSegment(sketch, "E2858", {"start": v(133.9, 720.98) * mm, "end": v(133.75, 720.9) * mm});
            skLineSegment(sketch, "E2859", {"start": v(133.75, 720.9) * mm, "end": v(133.6, 720.83) * mm});
            skLineSegment(sketch, "E2860", {"start": v(133.6, 720.83) * mm, "end": v(133.45, 720.77) * mm});
            skLineSegment(sketch, "E2861", {"start": v(133.45, 720.77) * mm, "end": v(133.29, 720.72) * mm});
            skLineSegment(sketch, "E2862", {"start": v(133.29, 720.72) * mm, "end": v(133.12, 720.67) * mm});
            skLineSegment(sketch, "E2863", {"start": v(133.12, 720.67) * mm, "end": v(132.96, 720.63) * mm});
            skLineSegment(sketch, "E2864", {"start": v(132.96, 720.63) * mm, "end": v(132.8, 720.6) * mm});
            skLineSegment(sketch, "E2865", {"start": v(132.8, 720.6) * mm, "end": v(132.63, 720.58) * mm});
            skLineSegment(sketch, "E2866", {"start": v(132.63, 720.58) * mm, "end": v(132.46, 720.57) * mm});
            skLineSegment(sketch, "E2867", {"start": v(132.46, 720.57) * mm, "end": v(132.29, 720.57) * mm});
            skLineSegment(sketch, "E2868", {"start": v(132.29, 720.57) * mm, "end": v(101.92, 720.57) * mm});
            skLineSegment(sketch, "E2869", {"start": v(109.05, 717.93) * mm, "end": v(109.05, 726) * mm});
            skLineSegment(sketch, "E2870", {"start": v(296.17, 382.01) * mm, "end": v(261.18, 382.01) * mm});
            skLineSegment(sketch, "E2871", {"start": v(261.18, 382.01) * mm, "end": v(261.18, 403.77) * mm});
            skLineSegment(sketch, "E2872", {"start": v(277.9, 382.01) * mm, "end": v(277.9, 402.2) * mm});
            skLineSegment(sketch, "E2873", {"start": v(296.15, 432.03) * mm, "end": v(296.15, 411.47) * mm});
            skLineSegment(sketch, "E2874", {"start": v(296.15, 411.47) * mm, "end": v(261.2, 411.47) * mm});
            skLineSegment(sketch, "E2875", {"start": v(296.64, 445.3) * mm, "end": v(296.64, 444.93) * mm});
            skLineSegment(sketch, "E2876", {"start": v(296.64, 444.93) * mm, "end": v(296.64, 444.56) * mm});
            skLineSegment(sketch, "E2877", {"start": v(296.64, 444.56) * mm, "end": v(296.62, 444.2) * mm});
            skLineSegment(sketch, "E2878", {"start": v(296.62, 444.2) * mm, "end": v(296.6, 443.83) * mm});
            skLineSegment(sketch, "E2879", {"start": v(296.6, 443.83) * mm, "end": v(296.56, 443.47) * mm});
            skLineSegment(sketch, "E2880", {"start": v(296.56, 443.47) * mm, "end": v(296.52, 443.1) * mm});
            skLineSegment(sketch, "E2881", {"start": v(296.52, 443.1) * mm, "end": v(296.47, 442.75) * mm});
            skLineSegment(sketch, "E2882", {"start": v(296.47, 442.75) * mm, "end": v(296.4, 442.39) * mm});
            skLineSegment(sketch, "E2883", {"start": v(296.4, 442.39) * mm, "end": v(296.34, 442.03) * mm});
            skLineSegment(sketch, "E2884", {"start": v(296.34, 442.03) * mm, "end": v(296.26, 441.68) * mm});
            skLineSegment(sketch, "E2885", {"start": v(296.26, 441.68) * mm, "end": v(296.17, 441.32) * mm});
            skLineSegment(sketch, "E2886", {"start": v(296.17, 441.32) * mm, "end": v(296.08, 440.97) * mm});
            skLineSegment(sketch, "E2887", {"start": v(296.08, 440.97) * mm, "end": v(295.97, 440.63) * mm});
            skLineSegment(sketch, "E2888", {"start": v(295.97, 440.63) * mm, "end": v(295.86, 440.28) * mm});
            skLineSegment(sketch, "E2889", {"start": v(295.86, 440.28) * mm, "end": v(295.74, 439.94) * mm});
            skLineSegment(sketch, "E2890", {"start": v(295.74, 439.94) * mm, "end": v(295.6, 439.6) * mm});
            skLineSegment(sketch, "E2891", {"start": v(295.6, 439.6) * mm, "end": v(295.47, 439.27) * mm});
            skLineSegment(sketch, "E2892", {"start": v(295.47, 439.27) * mm, "end": v(295.32, 438.94) * mm});
            skLineSegment(sketch, "E2893", {"start": v(295.32, 438.94) * mm, "end": v(295.17, 438.61) * mm});
            skLineSegment(sketch, "E2894", {"start": v(295.17, 438.61) * mm, "end": v(295, 438.29) * mm});
            skLineSegment(sketch, "E2895", {"start": v(295, 438.29) * mm, "end": v(294.83, 437.97) * mm});
            skLineSegment(sketch, "E2896", {"start": v(294.83, 437.97) * mm, "end": v(294.66, 437.65) * mm});
            skLineSegment(sketch, "E2897", {"start": v(294.66, 437.65) * mm, "end": v(294.47, 437.34) * mm});
            skLineSegment(sketch, "E2898", {"start": v(294.47, 437.34) * mm, "end": v(294.27, 437.04) * mm});
            skLineSegment(sketch, "E2899", {"start": v(294.27, 437.04) * mm, "end": v(294.07, 436.73) * mm});
            skLineSegment(sketch, "E2900", {"start": v(294.07, 436.73) * mm, "end": v(293.86, 436.44) * mm});
            skLineSegment(sketch, "E2901", {"start": v(293.86, 436.44) * mm, "end": v(293.64, 436.14) * mm});
            skLineSegment(sketch, "E2902", {"start": v(293.64, 436.14) * mm, "end": v(293.42, 435.86) * mm});
            skLineSegment(sketch, "E2903", {"start": v(293.42, 435.86) * mm, "end": v(293.19, 435.58) * mm});
            skLineSegment(sketch, "E2904", {"start": v(293.19, 435.58) * mm, "end": v(292.95, 435.3) * mm});
            skLineSegment(sketch, "E2905", {"start": v(292.95, 435.3) * mm, "end": v(292.7, 435.03) * mm});
            skLineSegment(sketch, "E2906", {"start": v(292.7, 435.03) * mm, "end": v(292.44, 434.76) * mm});
            skLineSegment(sketch, "E2907", {"start": v(292.44, 434.76) * mm, "end": v(292.11, 434.46) * mm});
            skLineSegment(sketch, "E2908", {"start": v(292.11, 434.46) * mm, "end": v(291.77, 434.16) * mm});
            skLineSegment(sketch, "E2909", {"start": v(291.77, 434.16) * mm, "end": v(291.43, 433.87) * mm});
            skLineSegment(sketch, "E2910", {"start": v(291.43, 433.87) * mm, "end": v(291.07, 433.6) * mm});
            skLineSegment(sketch, "E2911", {"start": v(291.07, 433.6) * mm, "end": v(290.71, 433.32) * mm});
            skLineSegment(sketch, "E2912", {"start": v(290.71, 433.32) * mm, "end": v(290.35, 433.06) * mm});
            skLineSegment(sketch, "E2913", {"start": v(290.35, 433.06) * mm, "end": v(289.98, 432.81) * mm});
            skLineSegment(sketch, "E2914", {"start": v(289.98, 432.81) * mm, "end": v(289.6, 432.57) * mm});
            skLineSegment(sketch, "E2915", {"start": v(289.6, 432.57) * mm, "end": v(289.22, 432.34) * mm});
            skLineSegment(sketch, "E2916", {"start": v(289.22, 432.34) * mm, "end": v(288.83, 432.12) * mm});
            skLineSegment(sketch, "E2917", {"start": v(288.83, 432.12) * mm, "end": v(288.44, 431.9) * mm});
            skLineSegment(sketch, "E2918", {"start": v(288.44, 431.9) * mm, "end": v(288.04, 431.7) * mm});
            skLineSegment(sketch, "E2919", {"start": v(288.04, 431.7) * mm, "end": v(287.64, 431.51) * mm});
            skLineSegment(sketch, "E2920", {"start": v(287.64, 431.51) * mm, "end": v(287.23, 431.33) * mm});
            skLineSegment(sketch, "E2921", {"start": v(287.23, 431.33) * mm, "end": v(286.82, 431.16) * mm});
            skLineSegment(sketch, "E2922", {"start": v(286.82, 431.16) * mm, "end": v(286.4, 431) * mm});
            skLineSegment(sketch, "E2923", {"start": v(286.4, 431) * mm, "end": v(285.99, 430.84) * mm});
            skLineSegment(sketch, "E2924", {"start": v(285.99, 430.84) * mm, "end": v(285.56, 430.7) * mm});
            skLineSegment(sketch, "E2925", {"start": v(285.56, 430.7) * mm, "end": v(285.14, 430.57) * mm});
            skLineSegment(sketch, "E2926", {"start": v(285.14, 430.57) * mm, "end": v(284.7, 430.45) * mm});
            skLineSegment(sketch, "E2927", {"start": v(284.7, 430.45) * mm, "end": v(284.28, 430.34) * mm});
            skLineSegment(sketch, "E2928", {"start": v(284.28, 430.34) * mm, "end": v(283.84, 430.24) * mm});
            skLineSegment(sketch, "E2929", {"start": v(283.84, 430.24) * mm, "end": v(283.4, 430.15) * mm});
            skLineSegment(sketch, "E2930", {"start": v(283.4, 430.15) * mm, "end": v(282.96, 430.07) * mm});
            skLineSegment(sketch, "E2931", {"start": v(282.96, 430.07) * mm, "end": v(282.52, 430) * mm});
            skLineSegment(sketch, "E2932", {"start": v(282.52, 430) * mm, "end": v(282.08, 429.95) * mm});
            skLineSegment(sketch, "E2933", {"start": v(282.08, 429.95) * mm, "end": v(281.63, 429.9) * mm});
            skLineSegment(sketch, "E2934", {"start": v(281.63, 429.9) * mm, "end": v(281.18, 429.87) * mm});
            skLineSegment(sketch, "E2935", {"start": v(281.18, 429.87) * mm, "end": v(280.73, 429.84) * mm});
            skLineSegment(sketch, "E2936", {"start": v(280.73, 429.84) * mm, "end": v(280.28, 429.83) * mm});
            skLineSegment(sketch, "E2937", {"start": v(280.28, 429.83) * mm, "end": v(279.83, 429.83) * mm});
            skLineSegment(sketch, "E2938", {"start": v(279.83, 429.83) * mm, "end": v(279.38, 429.84) * mm});
            skLineSegment(sketch, "E2939", {"start": v(279.38, 429.84) * mm, "end": v(278.89, 429.83) * mm});
            skLineSegment(sketch, "E2940", {"start": v(278.89, 429.83) * mm, "end": v(278.4, 429.83) * mm});
            skLineSegment(sketch, "E2941", {"start": v(278.4, 429.83) * mm, "end": v(277.9, 429.84) * mm});
            skLineSegment(sketch, "E2942", {"start": v(277.9, 429.84) * mm, "end": v(277.42, 429.86) * mm});
            skLineSegment(sketch, "E2943", {"start": v(277.42, 429.86) * mm, "end": v(276.94, 429.9) * mm});
            skLineSegment(sketch, "E2944", {"start": v(276.94, 429.9) * mm, "end": v(276.45, 429.94) * mm});
            skLineSegment(sketch, "E2945", {"start": v(276.45, 429.94) * mm, "end": v(275.97, 430) * mm});
            skLineSegment(sketch, "E2946", {"start": v(275.97, 430) * mm, "end": v(275.49, 430.07) * mm});
            skLineSegment(sketch, "E2947", {"start": v(275.49, 430.07) * mm, "end": v(275, 430.16) * mm});
            skLineSegment(sketch, "E2948", {"start": v(275, 430.16) * mm, "end": v(274.53, 430.25) * mm});
            skLineSegment(sketch, "E2949", {"start": v(274.53, 430.25) * mm, "end": v(274.06, 430.36) * mm});
            skLineSegment(sketch, "E2950", {"start": v(274.06, 430.36) * mm, "end": v(273.6, 430.48) * mm});
            skLineSegment(sketch, "E2951", {"start": v(273.6, 430.48) * mm, "end": v(273.13, 430.6) * mm});
            skLineSegment(sketch, "E2952", {"start": v(273.13, 430.6) * mm, "end": v(272.66, 430.75) * mm});
            skLineSegment(sketch, "E2953", {"start": v(272.66, 430.75) * mm, "end": v(272.2, 430.9) * mm});
            skLineSegment(sketch, "E2954", {"start": v(272.2, 430.9) * mm, "end": v(271.75, 431.07) * mm});
            skLineSegment(sketch, "E2955", {"start": v(271.75, 431.07) * mm, "end": v(271.3, 431.24) * mm});
            skLineSegment(sketch, "E2956", {"start": v(271.3, 431.24) * mm, "end": v(270.85, 431.43) * mm});
            skLineSegment(sketch, "E2957", {"start": v(270.85, 431.43) * mm, "end": v(270.41, 431.63) * mm});
            skLineSegment(sketch, "E2958", {"start": v(270.41, 431.63) * mm, "end": v(269.97, 431.84) * mm});
            skLineSegment(sketch, "E2959", {"start": v(269.97, 431.84) * mm, "end": v(269.54, 432.06) * mm});
            skLineSegment(sketch, "E2960", {"start": v(269.54, 432.06) * mm, "end": v(269.12, 432.29) * mm});
            skLineSegment(sketch, "E2961", {"start": v(269.12, 432.29) * mm, "end": v(268.7, 432.53) * mm});
            skLineSegment(sketch, "E2962", {"start": v(268.7, 432.53) * mm, "end": v(268.28, 432.78) * mm});
            skLineSegment(sketch, "E2963", {"start": v(268.28, 432.78) * mm, "end": v(267.87, 433.04) * mm});
            skLineSegment(sketch, "E2964", {"start": v(267.87, 433.04) * mm, "end": v(267.47, 433.32) * mm});
            skLineSegment(sketch, "E2965", {"start": v(267.47, 433.32) * mm, "end": v(267.07, 433.6) * mm});
            skLineSegment(sketch, "E2966", {"start": v(267.07, 433.6) * mm, "end": v(266.68, 433.9) * mm});
            skLineSegment(sketch, "E2967", {"start": v(266.68, 433.9) * mm, "end": v(266.3, 434.2) * mm});
            skLineSegment(sketch, "E2968", {"start": v(266.3, 434.2) * mm, "end": v(265.93, 434.51) * mm});
            skLineSegment(sketch, "E2969", {"start": v(265.93, 434.51) * mm, "end": v(265.56, 434.84) * mm});
            skLineSegment(sketch, "E2970", {"start": v(265.56, 434.84) * mm, "end": v(265.2, 435.17) * mm});
            skLineSegment(sketch, "E2971", {"start": v(265.2, 435.17) * mm, "end": v(264.94, 435.42) * mm});
            skLineSegment(sketch, "E2972", {"start": v(264.94, 435.42) * mm, "end": v(264.7, 435.68) * mm});
            skLineSegment(sketch, "E2973", {"start": v(264.7, 435.68) * mm, "end": v(264.46, 435.94) * mm});
            skLineSegment(sketch, "E2974", {"start": v(264.46, 435.94) * mm, "end": v(264.22, 436.2) * mm});
            skLineSegment(sketch, "E2975", {"start": v(264.22, 436.2) * mm, "end": v(264, 436.48) * mm});
            skLineSegment(sketch, "E2976", {"start": v(264, 436.48) * mm, "end": v(263.78, 436.76) * mm});
            skLineSegment(sketch, "E2977", {"start": v(263.78, 436.76) * mm, "end": v(263.57, 437.04) * mm});
            skLineSegment(sketch, "E2978", {"start": v(263.57, 437.04) * mm, "end": v(263.37, 437.33) * mm});
            skLineSegment(sketch, "E2979", {"start": v(263.37, 437.33) * mm, "end": v(263.17, 437.62) * mm});
            skLineSegment(sketch, "E2980", {"start": v(263.17, 437.62) * mm, "end": v(262.99, 437.92) * mm});
            skLineSegment(sketch, "E2981", {"start": v(262.99, 437.92) * mm, "end": v(262.8, 438.22) * mm});
            skLineSegment(sketch, "E2982", {"start": v(262.8, 438.22) * mm, "end": v(262.64, 438.53) * mm});
            skLineSegment(sketch, "E2983", {"start": v(262.64, 438.53) * mm, "end": v(262.47, 438.84) * mm});
            skLineSegment(sketch, "E2984", {"start": v(262.47, 438.84) * mm, "end": v(262.32, 439.15) * mm});
            skLineSegment(sketch, "E2985", {"start": v(262.32, 439.15) * mm, "end": v(262.17, 439.47) * mm});
            skLineSegment(sketch, "E2986", {"start": v(262.17, 439.47) * mm, "end": v(262.03, 439.8) * mm});
            skLineSegment(sketch, "E2987", {"start": v(262.03, 439.8) * mm, "end": v(261.9, 440.12) * mm});
            skLineSegment(sketch, "E2988", {"start": v(261.9, 440.12) * mm, "end": v(261.78, 440.45) * mm});
            skLineSegment(sketch, "E2989", {"start": v(261.78, 440.45) * mm, "end": v(261.66, 440.78) * mm});
            skLineSegment(sketch, "E2990", {"start": v(261.66, 440.78) * mm, "end": v(261.56, 441.12) * mm});
            skLineSegment(sketch, "E2991", {"start": v(261.56, 441.12) * mm, "end": v(261.46, 441.45) * mm});
            skLineSegment(sketch, "E2992", {"start": v(261.46, 441.45) * mm, "end": v(261.37, 441.8) * mm});
            skLineSegment(sketch, "E2993", {"start": v(261.37, 441.8) * mm, "end": v(261.3, 442.14) * mm});
            skLineSegment(sketch, "E2994", {"start": v(261.3, 442.14) * mm, "end": v(261.22, 442.48) * mm});
            skLineSegment(sketch, "E2995", {"start": v(261.22, 442.48) * mm, "end": v(261.16, 442.83) * mm});
            skLineSegment(sketch, "E2996", {"start": v(261.16, 442.83) * mm, "end": v(261.1, 443.18) * mm});
            skLineSegment(sketch, "E2997", {"start": v(261.1, 443.18) * mm, "end": v(261.06, 443.53) * mm});
            skLineSegment(sketch, "E2998", {"start": v(261.06, 443.53) * mm, "end": v(261.02, 443.88) * mm});
            skLineSegment(sketch, "E2999", {"start": v(261.02, 443.88) * mm, "end": v(261, 444.23) * mm});
            skLineSegment(sketch, "E3000", {"start": v(261, 444.23) * mm, "end": v(260.98, 444.59) * mm});
            skLineSegment(sketch, "E3001", {"start": v(260.98, 444.59) * mm, "end": v(260.97, 444.94) * mm});
            skLineSegment(sketch, "E3002", {"start": v(260.97, 444.94) * mm, "end": v(260.97, 445.3) * mm});
            skLineSegment(sketch, "E3003", {"start": v(260.97, 445.3) * mm, "end": v(260.98, 445.66) * mm});
            skLineSegment(sketch, "E3004", {"start": v(260.98, 445.66) * mm, "end": v(261, 446.03) * mm});
            skLineSegment(sketch, "E3005", {"start": v(261, 446.03) * mm, "end": v(261.01, 446.39) * mm});
            skLineSegment(sketch, "E3006", {"start": v(261.01, 446.39) * mm, "end": v(261.04, 446.74) * mm});
            skLineSegment(sketch, "E3007", {"start": v(261.04, 446.74) * mm, "end": v(261.08, 447.1) * mm});
            skLineSegment(sketch, "E3008", {"start": v(261.08, 447.1) * mm, "end": v(261.13, 447.46) * mm});
            skLineSegment(sketch, "E3009", {"start": v(261.13, 447.46) * mm, "end": v(261.2, 447.81) * mm});
            skLineSegment(sketch, "E3010", {"start": v(261.2, 447.81) * mm, "end": v(261.26, 448.16) * mm});
            skLineSegment(sketch, "E3011", {"start": v(261.26, 448.16) * mm, "end": v(261.34, 448.51) * mm});
            skLineSegment(sketch, "E3012", {"start": v(261.34, 448.51) * mm, "end": v(261.42, 448.86) * mm});
            skLineSegment(sketch, "E3013", {"start": v(261.42, 448.86) * mm, "end": v(261.52, 449.2) * mm});
            skLineSegment(sketch, "E3014", {"start": v(261.52, 449.2) * mm, "end": v(261.62, 449.55) * mm});
            skLineSegment(sketch, "E3015", {"start": v(261.62, 449.55) * mm, "end": v(261.73, 449.89) * mm});
            skLineSegment(sketch, "E3016", {"start": v(261.73, 449.89) * mm, "end": v(261.85, 450.22) * mm});
            skLineSegment(sketch, "E3017", {"start": v(261.85, 450.22) * mm, "end": v(261.98, 450.56) * mm});
            skLineSegment(sketch, "E3018", {"start": v(261.98, 450.56) * mm, "end": v(262.12, 450.88) * mm});
            skLineSegment(sketch, "E3019", {"start": v(262.12, 450.88) * mm, "end": v(262.26, 451.21) * mm});
            skLineSegment(sketch, "E3020", {"start": v(262.26, 451.21) * mm, "end": v(262.42, 451.53) * mm});
            skLineSegment(sketch, "E3021", {"start": v(262.42, 451.53) * mm, "end": v(262.58, 451.85) * mm});
            skLineSegment(sketch, "E3022", {"start": v(262.58, 451.85) * mm, "end": v(262.75, 452.16) * mm});
            skLineSegment(sketch, "E3023", {"start": v(262.75, 452.16) * mm, "end": v(262.93, 452.47) * mm});
            skLineSegment(sketch, "E3024", {"start": v(262.93, 452.47) * mm, "end": v(263.11, 452.78) * mm});
            skLineSegment(sketch, "E3025", {"start": v(263.11, 452.78) * mm, "end": v(263.3, 453.08) * mm});
            skLineSegment(sketch, "E3026", {"start": v(263.3, 453.08) * mm, "end": v(263.5, 453.38) * mm});
            skLineSegment(sketch, "E3027", {"start": v(263.5, 453.38) * mm, "end": v(263.72, 453.67) * mm});
            skLineSegment(sketch, "E3028", {"start": v(263.72, 453.67) * mm, "end": v(263.93, 453.95) * mm});
            skLineSegment(sketch, "E3029", {"start": v(263.93, 453.95) * mm, "end": v(264.16, 454.23) * mm});
            skLineSegment(sketch, "E3030", {"start": v(264.16, 454.23) * mm, "end": v(264.4, 454.5) * mm});
            skLineSegment(sketch, "E3031", {"start": v(264.4, 454.5) * mm, "end": v(264.63, 454.78) * mm});
            skLineSegment(sketch, "E3032", {"start": v(264.63, 454.78) * mm, "end": v(264.88, 455.04) * mm});
            skLineSegment(sketch, "E3033", {"start": v(264.88, 455.04) * mm, "end": v(265.13, 455.3) * mm});
            skLineSegment(sketch, "E3034", {"start": v(265.13, 455.3) * mm, "end": v(265.4, 455.55) * mm});
            skLineSegment(sketch, "E3035", {"start": v(265.4, 455.55) * mm, "end": v(265.75, 455.87) * mm});
            skLineSegment(sketch, "E3036", {"start": v(265.75, 455.87) * mm, "end": v(266.12, 456.19) * mm});
            skLineSegment(sketch, "E3037", {"start": v(266.12, 456.19) * mm, "end": v(266.5, 456.49) * mm});
            skLineSegment(sketch, "E3038", {"start": v(266.5, 456.49) * mm, "end": v(266.87, 456.78) * mm});
            skLineSegment(sketch, "E3039", {"start": v(266.87, 456.78) * mm, "end": v(267.26, 457.07) * mm});
            skLineSegment(sketch, "E3040", {"start": v(267.26, 457.07) * mm, "end": v(267.65, 457.34) * mm});
            skLineSegment(sketch, "E3041", {"start": v(267.65, 457.34) * mm, "end": v(268.05, 457.6) * mm});
            skLineSegment(sketch, "E3042", {"start": v(268.05, 457.6) * mm, "end": v(268.45, 457.86) * mm});
            skLineSegment(sketch, "E3043", {"start": v(268.45, 457.86) * mm, "end": v(268.86, 458.1) * mm});
            skLineSegment(sketch, "E3044", {"start": v(268.86, 458.1) * mm, "end": v(269.28, 458.34) * mm});
            skLineSegment(sketch, "E3045", {"start": v(269.28, 458.34) * mm, "end": v(269.7, 458.56) * mm});
            skLineSegment(sketch, "E3046", {"start": v(269.7, 458.56) * mm, "end": v(270.13, 458.77) * mm});
            skLineSegment(sketch, "E3047", {"start": v(270.13, 458.77) * mm, "end": v(270.56, 458.97) * mm});
            skLineSegment(sketch, "E3048", {"start": v(270.56, 458.97) * mm, "end": v(271, 459.16) * mm});
            skLineSegment(sketch, "E3049", {"start": v(271, 459.16) * mm, "end": v(271.44, 459.34) * mm});
            skLineSegment(sketch, "E3050", {"start": v(271.44, 459.34) * mm, "end": v(271.88, 459.5) * mm});
            skLineSegment(sketch, "E3051", {"start": v(271.88, 459.5) * mm, "end": v(272.33, 459.67) * mm});
            skLineSegment(sketch, "E3052", {"start": v(272.33, 459.67) * mm, "end": v(272.79, 459.81) * mm});
            skLineSegment(sketch, "E3053", {"start": v(272.79, 459.81) * mm, "end": v(273.24, 459.95) * mm});
            skLineSegment(sketch, "E3054", {"start": v(273.24, 459.95) * mm, "end": v(273.7, 460.07) * mm});
            skLineSegment(sketch, "E3055", {"start": v(273.7, 460.07) * mm, "end": v(274.16, 460.18) * mm});
            skLineSegment(sketch, "E3056", {"start": v(274.16, 460.18) * mm, "end": v(274.63, 460.29) * mm});
            skLineSegment(sketch, "E3057", {"start": v(274.63, 460.29) * mm, "end": v(275.1, 460.38) * mm});
            skLineSegment(sketch, "E3058", {"start": v(275.1, 460.38) * mm, "end": v(275.57, 460.45) * mm});
            skLineSegment(sketch, "E3059", {"start": v(275.57, 460.45) * mm, "end": v(276.04, 460.52) * mm});
            skLineSegment(sketch, "E3060", {"start": v(276.04, 460.52) * mm, "end": v(276.52, 460.57) * mm});
            skLineSegment(sketch, "E3061", {"start": v(276.52, 460.57) * mm, "end": v(277, 460.62) * mm});
            skLineSegment(sketch, "E3062", {"start": v(277, 460.62) * mm, "end": v(277.47, 460.65) * mm});
            skLineSegment(sketch, "E3063", {"start": v(277.47, 460.65) * mm, "end": v(277.95, 460.67) * mm});
            skLineSegment(sketch, "E3064", {"start": v(277.95, 460.67) * mm, "end": v(278.44, 460.67) * mm});
            skLineSegment(sketch, "E3065", {"start": v(278.44, 460.67) * mm, "end": v(278.92, 460.67) * mm});
            skLineSegment(sketch, "E3066", {"start": v(278.92, 460.67) * mm, "end": v(279.4, 460.65) * mm});
            skLineSegment(sketch, "E3067", {"start": v(279.4, 460.65) * mm, "end": v(279.85, 460.66) * mm});
            skLineSegment(sketch, "E3068", {"start": v(279.85, 460.66) * mm, "end": v(280.3, 460.66) * mm});
            skLineSegment(sketch, "E3069", {"start": v(280.3, 460.66) * mm, "end": v(280.75, 460.64) * mm});
            skLineSegment(sketch, "E3070", {"start": v(280.75, 460.64) * mm, "end": v(281.2, 460.61) * mm});
            skLineSegment(sketch, "E3071", {"start": v(281.2, 460.61) * mm, "end": v(281.64, 460.58) * mm});
            skLineSegment(sketch, "E3072", {"start": v(281.64, 460.58) * mm, "end": v(282.09, 460.53) * mm});
            skLineSegment(sketch, "E3073", {"start": v(282.09, 460.53) * mm, "end": v(282.53, 460.47) * mm});
            skLineSegment(sketch, "E3074", {"start": v(282.53, 460.47) * mm, "end": v(282.97, 460.4) * mm});
            skLineSegment(sketch, "E3075", {"start": v(282.97, 460.4) * mm, "end": v(283.4, 460.31) * mm});
            skLineSegment(sketch, "E3076", {"start": v(283.4, 460.31) * mm, "end": v(283.84, 460.22) * mm});
            skLineSegment(sketch, "E3077", {"start": v(283.84, 460.22) * mm, "end": v(284.27, 460.12) * mm});
            skLineSegment(sketch, "E3078", {"start": v(284.27, 460.12) * mm, "end": v(284.7, 460) * mm});
            skLineSegment(sketch, "E3079", {"start": v(284.7, 460) * mm, "end": v(285.13, 459.88) * mm});
            skLineSegment(sketch, "E3080", {"start": v(285.13, 459.88) * mm, "end": v(285.55, 459.74) * mm});
            skLineSegment(sketch, "E3081", {"start": v(285.55, 459.74) * mm, "end": v(285.97, 459.6) * mm});
            skLineSegment(sketch, "E3082", {"start": v(285.97, 459.6) * mm, "end": v(286.39, 459.44) * mm});
            skLineSegment(sketch, "E3083", {"start": v(286.39, 459.44) * mm, "end": v(286.8, 459.28) * mm});
            skLineSegment(sketch, "E3084", {"start": v(286.8, 459.28) * mm, "end": v(287.2, 459.1) * mm});
            skLineSegment(sketch, "E3085", {"start": v(287.2, 459.1) * mm, "end": v(287.6, 458.91) * mm});
            skLineSegment(sketch, "E3086", {"start": v(287.6, 458.91) * mm, "end": v(288, 458.72) * mm});
            skLineSegment(sketch, "E3087", {"start": v(288, 458.72) * mm, "end": v(288.4, 458.51) * mm});
            skLineSegment(sketch, "E3088", {"start": v(288.4, 458.51) * mm, "end": v(288.79, 458.3) * mm});
            skLineSegment(sketch, "E3089", {"start": v(288.79, 458.3) * mm, "end": v(289.17, 458.07) * mm});
            skLineSegment(sketch, "E3090", {"start": v(289.17, 458.07) * mm, "end": v(289.55, 457.83) * mm});
            skLineSegment(sketch, "E3091", {"start": v(289.55, 457.83) * mm, "end": v(289.92, 457.59) * mm});
            skLineSegment(sketch, "E3092", {"start": v(289.92, 457.59) * mm, "end": v(290.29, 457.33) * mm});
            skLineSegment(sketch, "E3093", {"start": v(290.29, 457.33) * mm, "end": v(290.65, 457.07) * mm});
            skLineSegment(sketch, "E3094", {"start": v(290.65, 457.07) * mm, "end": v(291, 456.8) * mm});
            skLineSegment(sketch, "E3095", {"start": v(291, 456.8) * mm, "end": v(291.35, 456.51) * mm});
            skLineSegment(sketch, "E3096", {"start": v(291.35, 456.51) * mm, "end": v(291.7, 456.22) * mm});
            skLineSegment(sketch, "E3097", {"start": v(291.7, 456.22) * mm, "end": v(292.03, 455.92) * mm});
            skLineSegment(sketch, "E3098", {"start": v(292.03, 455.92) * mm, "end": v(292.35, 455.61) * mm});
            skLineSegment(sketch, "E3099", {"start": v(292.35, 455.61) * mm, "end": v(292.6, 455.35) * mm});
            skLineSegment(sketch, "E3100", {"start": v(292.6, 455.35) * mm, "end": v(292.86, 455.09) * mm});
            skLineSegment(sketch, "E3101", {"start": v(292.86, 455.09) * mm, "end": v(293.1, 454.82) * mm});
            skLineSegment(sketch, "E3102", {"start": v(293.1, 454.82) * mm, "end": v(293.33, 454.55) * mm});
            skLineSegment(sketch, "E3103", {"start": v(293.33, 454.55) * mm, "end": v(293.56, 454.27) * mm});
            skLineSegment(sketch, "E3104", {"start": v(293.56, 454.27) * mm, "end": v(293.77, 453.98) * mm});
            skLineSegment(sketch, "E3105", {"start": v(293.77, 453.98) * mm, "end": v(293.98, 453.7) * mm});
            skLineSegment(sketch, "E3106", {"start": v(293.98, 453.7) * mm, "end": v(294.19, 453.4) * mm});
            skLineSegment(sketch, "E3107", {"start": v(294.19, 453.4) * mm, "end": v(294.38, 453.1) * mm});
            skLineSegment(sketch, "E3108", {"start": v(294.38, 453.1) * mm, "end": v(294.57, 452.8) * mm});
            skLineSegment(sketch, "E3109", {"start": v(294.57, 452.8) * mm, "end": v(294.75, 452.49) * mm});
            skLineSegment(sketch, "E3110", {"start": v(294.75, 452.49) * mm, "end": v(294.93, 452.17) * mm});
            skLineSegment(sketch, "E3111", {"start": v(294.93, 452.17) * mm, "end": v(295.1, 451.86) * mm});
            skLineSegment(sketch, "E3112", {"start": v(295.1, 451.86) * mm, "end": v(295.25, 451.54) * mm});
            skLineSegment(sketch, "E3113", {"start": v(295.25, 451.54) * mm, "end": v(295.4, 451.21) * mm});
            skLineSegment(sketch, "E3114", {"start": v(295.4, 451.21) * mm, "end": v(295.54, 450.89) * mm});
            skLineSegment(sketch, "E3115", {"start": v(295.54, 450.89) * mm, "end": v(295.67, 450.55) * mm});
            skLineSegment(sketch, "E3116", {"start": v(295.67, 450.55) * mm, "end": v(295.8, 450.22) * mm});
            skLineSegment(sketch, "E3117", {"start": v(295.8, 450.22) * mm, "end": v(295.91, 449.88) * mm});
            skLineSegment(sketch, "E3118", {"start": v(295.91, 449.88) * mm, "end": v(296.02, 449.54) * mm});
            skLineSegment(sketch, "E3119", {"start": v(296.02, 449.54) * mm, "end": v(296.12, 449.2) * mm});
            skLineSegment(sketch, "E3120", {"start": v(296.12, 449.2) * mm, "end": v(296.21, 448.85) * mm});
            skLineSegment(sketch, "E3121", {"start": v(296.21, 448.85) * mm, "end": v(296.3, 448.5) * mm});
            skLineSegment(sketch, "E3122", {"start": v(296.3, 448.5) * mm, "end": v(296.37, 448.16) * mm});
            skLineSegment(sketch, "E3123", {"start": v(296.37, 448.16) * mm, "end": v(296.43, 447.8) * mm});
            skLineSegment(sketch, "E3124", {"start": v(296.43, 447.8) * mm, "end": v(296.49, 447.45) * mm});
            skLineSegment(sketch, "E3125", {"start": v(296.49, 447.45) * mm, "end": v(296.54, 447.1) * mm});
            skLineSegment(sketch, "E3126", {"start": v(296.54, 447.1) * mm, "end": v(296.57, 446.74) * mm});
            skLineSegment(sketch, "E3127", {"start": v(296.57, 446.74) * mm, "end": v(296.6, 446.38) * mm});
            skLineSegment(sketch, "E3128", {"start": v(296.6, 446.38) * mm, "end": v(296.63, 446.02) * mm});
            skLineSegment(sketch, "E3129", {"start": v(296.63, 446.02) * mm, "end": v(296.64, 445.66) * mm});
            skLineSegment(sketch, "E3130", {"start": v(296.64, 445.66) * mm, "end": v(296.64, 445.3) * mm});
            skLineSegment(sketch, "E3131", {"start": v(296.64, 484) * mm, "end": v(296.64, 483.64) * mm});
            skLineSegment(sketch, "E3132", {"start": v(296.64, 483.64) * mm, "end": v(296.64, 483.28) * mm});
            skLineSegment(sketch, "E3133", {"start": v(296.64, 483.28) * mm, "end": v(296.62, 482.9) * mm});
            skLineSegment(sketch, "E3134", {"start": v(296.62, 482.9) * mm, "end": v(296.6, 482.54) * mm});
            skLineSegment(sketch, "E3135", {"start": v(296.6, 482.54) * mm, "end": v(296.56, 482.18) * mm});
            skLineSegment(sketch, "E3136", {"start": v(296.56, 482.18) * mm, "end": v(296.52, 481.82) * mm});
            skLineSegment(sketch, "E3137", {"start": v(296.52, 481.82) * mm, "end": v(296.47, 481.46) * mm});
            skLineSegment(sketch, "E3138", {"start": v(296.47, 481.46) * mm, "end": v(296.4, 481.1) * mm});
            skLineSegment(sketch, "E3139", {"start": v(296.4, 481.1) * mm, "end": v(296.34, 480.75) * mm});
            skLineSegment(sketch, "E3140", {"start": v(296.34, 480.75) * mm, "end": v(296.26, 480.4) * mm});
            skLineSegment(sketch, "E3141", {"start": v(296.26, 480.4) * mm, "end": v(296.17, 480.04) * mm});
            skLineSegment(sketch, "E3142", {"start": v(296.17, 480.04) * mm, "end": v(296.08, 479.69) * mm});
            skLineSegment(sketch, "E3143", {"start": v(296.08, 479.69) * mm, "end": v(295.97, 479.34) * mm});
            skLineSegment(sketch, "E3144", {"start": v(295.97, 479.34) * mm, "end": v(295.86, 479) * mm});
            skLineSegment(sketch, "E3145", {"start": v(295.86, 479) * mm, "end": v(295.74, 478.66) * mm});
            skLineSegment(sketch, "E3146", {"start": v(295.74, 478.66) * mm, "end": v(295.6, 478.32) * mm});
            skLineSegment(sketch, "E3147", {"start": v(295.6, 478.32) * mm, "end": v(295.47, 477.98) * mm});
            skLineSegment(sketch, "E3148", {"start": v(295.47, 477.98) * mm, "end": v(295.32, 477.65) * mm});
            skLineSegment(sketch, "E3149", {"start": v(295.32, 477.65) * mm, "end": v(295.17, 477.33) * mm});
            skLineSegment(sketch, "E3150", {"start": v(295.17, 477.33) * mm, "end": v(295, 477) * mm});
            skLineSegment(sketch, "E3151", {"start": v(295, 477) * mm, "end": v(294.83, 476.68) * mm});
            skLineSegment(sketch, "E3152", {"start": v(294.83, 476.68) * mm, "end": v(294.66, 476.37) * mm});
            skLineSegment(sketch, "E3153", {"start": v(294.66, 476.37) * mm, "end": v(294.47, 476.06) * mm});
            skLineSegment(sketch, "E3154", {"start": v(294.47, 476.06) * mm, "end": v(294.27, 475.75) * mm});
            skLineSegment(sketch, "E3155", {"start": v(294.27, 475.75) * mm, "end": v(294.07, 475.45) * mm});
            skLineSegment(sketch, "E3156", {"start": v(294.07, 475.45) * mm, "end": v(293.86, 475.15) * mm});
            skLineSegment(sketch, "E3157", {"start": v(293.86, 475.15) * mm, "end": v(293.64, 474.86) * mm});
            skLineSegment(sketch, "E3158", {"start": v(293.64, 474.86) * mm, "end": v(293.42, 474.57) * mm});
            skLineSegment(sketch, "E3159", {"start": v(293.42, 474.57) * mm, "end": v(293.19, 474.29) * mm});
            skLineSegment(sketch, "E3160", {"start": v(293.19, 474.29) * mm, "end": v(292.95, 474.01) * mm});
            skLineSegment(sketch, "E3161", {"start": v(292.95, 474.01) * mm, "end": v(292.7, 473.74) * mm});
            skLineSegment(sketch, "E3162", {"start": v(292.7, 473.74) * mm, "end": v(292.44, 473.48) * mm});
            skLineSegment(sketch, "E3163", {"start": v(292.44, 473.48) * mm, "end": v(292.11, 473.17) * mm});
            skLineSegment(sketch, "E3164", {"start": v(292.11, 473.17) * mm, "end": v(291.77, 472.88) * mm});
            skLineSegment(sketch, "E3165", {"start": v(291.77, 472.88) * mm, "end": v(291.43, 472.59) * mm});
            skLineSegment(sketch, "E3166", {"start": v(291.43, 472.59) * mm, "end": v(291.07, 472.3) * mm});
            skLineSegment(sketch, "E3167", {"start": v(291.07, 472.3) * mm, "end": v(290.71, 472.04) * mm});
            skLineSegment(sketch, "E3168", {"start": v(290.71, 472.04) * mm, "end": v(290.35, 471.78) * mm});
            skLineSegment(sketch, "E3169", {"start": v(290.35, 471.78) * mm, "end": v(289.98, 471.53) * mm});
            skLineSegment(sketch, "E3170", {"start": v(289.98, 471.53) * mm, "end": v(289.6, 471.29) * mm});
            skLineSegment(sketch, "E3171", {"start": v(289.6, 471.29) * mm, "end": v(289.22, 471.06) * mm});
            skLineSegment(sketch, "E3172", {"start": v(289.22, 471.06) * mm, "end": v(288.83, 470.83) * mm});
            skLineSegment(sketch, "E3173", {"start": v(288.83, 470.83) * mm, "end": v(288.44, 470.62) * mm});
            skLineSegment(sketch, "E3174", {"start": v(288.44, 470.62) * mm, "end": v(288.04, 470.42) * mm});
            skLineSegment(sketch, "E3175", {"start": v(288.04, 470.42) * mm, "end": v(287.64, 470.23) * mm});
            skLineSegment(sketch, "E3176", {"start": v(287.64, 470.23) * mm, "end": v(287.23, 470.04) * mm});
            skLineSegment(sketch, "E3177", {"start": v(287.23, 470.04) * mm, "end": v(286.82, 469.87) * mm});
            skLineSegment(sketch, "E3178", {"start": v(286.82, 469.87) * mm, "end": v(286.4, 469.7) * mm});
            skLineSegment(sketch, "E3179", {"start": v(286.4, 469.7) * mm, "end": v(285.99, 469.56) * mm});
            skLineSegment(sketch, "E3180", {"start": v(285.99, 469.56) * mm, "end": v(285.56, 469.42) * mm});
            skLineSegment(sketch, "E3181", {"start": v(285.56, 469.42) * mm, "end": v(285.14, 469.28) * mm});
            skLineSegment(sketch, "E3182", {"start": v(285.14, 469.28) * mm, "end": v(284.7, 469.16) * mm});
            skLineSegment(sketch, "E3183", {"start": v(284.7, 469.16) * mm, "end": v(284.28, 469.05) * mm});
            skLineSegment(sketch, "E3184", {"start": v(284.28, 469.05) * mm, "end": v(283.84, 468.95) * mm});
            skLineSegment(sketch, "E3185", {"start": v(283.84, 468.95) * mm, "end": v(283.4, 468.86) * mm});
            skLineSegment(sketch, "E3186", {"start": v(283.4, 468.86) * mm, "end": v(282.96, 468.79) * mm});
            skLineSegment(sketch, "E3187", {"start": v(282.96, 468.79) * mm, "end": v(282.52, 468.72) * mm});
            skLineSegment(sketch, "E3188", {"start": v(282.52, 468.72) * mm, "end": v(282.08, 468.66) * mm});
            skLineSegment(sketch, "E3189", {"start": v(282.08, 468.66) * mm, "end": v(281.63, 468.62) * mm});
            skLineSegment(sketch, "E3190", {"start": v(281.63, 468.62) * mm, "end": v(281.18, 468.58) * mm});
            skLineSegment(sketch, "E3191", {"start": v(281.18, 468.58) * mm, "end": v(280.73, 468.56) * mm});
            skLineSegment(sketch, "E3192", {"start": v(280.73, 468.56) * mm, "end": v(280.28, 468.55) * mm});
            skLineSegment(sketch, "E3193", {"start": v(280.28, 468.55) * mm, "end": v(279.83, 468.54) * mm});
            skLineSegment(sketch, "E3194", {"start": v(279.83, 468.54) * mm, "end": v(279.38, 468.56) * mm});
            skLineSegment(sketch, "E3195", {"start": v(279.38, 468.56) * mm, "end": v(278.89, 468.54) * mm});
            skLineSegment(sketch, "E3196", {"start": v(278.89, 468.54) * mm, "end": v(278.4, 468.54) * mm});
            skLineSegment(sketch, "E3197", {"start": v(278.4, 468.54) * mm, "end": v(277.9, 468.55) * mm});
            skLineSegment(sketch, "E3198", {"start": v(277.9, 468.55) * mm, "end": v(277.42, 468.57) * mm});
            skLineSegment(sketch, "E3199", {"start": v(277.42, 468.57) * mm, "end": v(276.94, 468.6) * mm});
            skLineSegment(sketch, "E3200", {"start": v(276.94, 468.6) * mm, "end": v(276.45, 468.66) * mm});
            skLineSegment(sketch, "E3201", {"start": v(276.45, 468.66) * mm, "end": v(275.97, 468.72) * mm});
            skLineSegment(sketch, "E3202", {"start": v(275.97, 468.72) * mm, "end": v(275.49, 468.79) * mm});
            skLineSegment(sketch, "E3203", {"start": v(275.49, 468.79) * mm, "end": v(275, 468.87) * mm});
            skLineSegment(sketch, "E3204", {"start": v(275, 468.87) * mm, "end": v(274.53, 468.97) * mm});
            skLineSegment(sketch, "E3205", {"start": v(274.53, 468.97) * mm, "end": v(274.06, 469.07) * mm});
            skLineSegment(sketch, "E3206", {"start": v(274.06, 469.07) * mm, "end": v(273.6, 469.2) * mm});
            skLineSegment(sketch, "E3207", {"start": v(273.6, 469.2) * mm, "end": v(273.13, 469.32) * mm});
            skLineSegment(sketch, "E3208", {"start": v(273.13, 469.32) * mm, "end": v(272.66, 469.47) * mm});
            skLineSegment(sketch, "E3209", {"start": v(272.66, 469.47) * mm, "end": v(272.2, 469.62) * mm});
            skLineSegment(sketch, "E3210", {"start": v(272.2, 469.62) * mm, "end": v(271.75, 469.78) * mm});
            skLineSegment(sketch, "E3211", {"start": v(271.75, 469.78) * mm, "end": v(271.3, 469.96) * mm});
            skLineSegment(sketch, "E3212", {"start": v(271.3, 469.96) * mm, "end": v(270.85, 470.15) * mm});
            skLineSegment(sketch, "E3213", {"start": v(270.85, 470.15) * mm, "end": v(270.41, 470.34) * mm});
            skLineSegment(sketch, "E3214", {"start": v(270.41, 470.34) * mm, "end": v(269.97, 470.55) * mm});
            skLineSegment(sketch, "E3215", {"start": v(269.97, 470.55) * mm, "end": v(269.54, 470.77) * mm});
            skLineSegment(sketch, "E3216", {"start": v(269.54, 470.77) * mm, "end": v(269.12, 471) * mm});
            skLineSegment(sketch, "E3217", {"start": v(269.12, 471) * mm, "end": v(268.7, 471.24) * mm});
            skLineSegment(sketch, "E3218", {"start": v(268.7, 471.24) * mm, "end": v(268.28, 471.5) * mm});
            skLineSegment(sketch, "E3219", {"start": v(268.28, 471.5) * mm, "end": v(267.87, 471.76) * mm});
            skLineSegment(sketch, "E3220", {"start": v(267.87, 471.76) * mm, "end": v(267.47, 472.03) * mm});
            skLineSegment(sketch, "E3221", {"start": v(267.47, 472.03) * mm, "end": v(267.07, 472.32) * mm});
            skLineSegment(sketch, "E3222", {"start": v(267.07, 472.32) * mm, "end": v(266.68, 472.6) * mm});
            skLineSegment(sketch, "E3223", {"start": v(266.68, 472.6) * mm, "end": v(266.3, 472.91) * mm});
            skLineSegment(sketch, "E3224", {"start": v(266.3, 472.91) * mm, "end": v(265.93, 473.23) * mm});
            skLineSegment(sketch, "E3225", {"start": v(265.93, 473.23) * mm, "end": v(265.56, 473.55) * mm});
            skLineSegment(sketch, "E3226", {"start": v(265.56, 473.55) * mm, "end": v(265.2, 473.88) * mm});
            skLineSegment(sketch, "E3227", {"start": v(265.2, 473.88) * mm, "end": v(264.94, 474.13) * mm});
            skLineSegment(sketch, "E3228", {"start": v(264.94, 474.13) * mm, "end": v(264.7, 474.4) * mm});
            skLineSegment(sketch, "E3229", {"start": v(264.7, 474.4) * mm, "end": v(264.46, 474.65) * mm});
            skLineSegment(sketch, "E3230", {"start": v(264.46, 474.65) * mm, "end": v(264.22, 474.92) * mm});
            skLineSegment(sketch, "E3231", {"start": v(264.22, 474.92) * mm, "end": v(264, 475.2) * mm});
            skLineSegment(sketch, "E3232", {"start": v(264, 475.2) * mm, "end": v(263.78, 475.47) * mm});
            skLineSegment(sketch, "E3233", {"start": v(263.78, 475.47) * mm, "end": v(263.57, 475.76) * mm});
            skLineSegment(sketch, "E3234", {"start": v(263.57, 475.76) * mm, "end": v(263.37, 476.04) * mm});
            skLineSegment(sketch, "E3235", {"start": v(263.37, 476.04) * mm, "end": v(263.17, 476.34) * mm});
            skLineSegment(sketch, "E3236", {"start": v(263.17, 476.34) * mm, "end": v(262.99, 476.63) * mm});
            skLineSegment(sketch, "E3237", {"start": v(262.99, 476.63) * mm, "end": v(262.8, 476.94) * mm});
            skLineSegment(sketch, "E3238", {"start": v(262.8, 476.94) * mm, "end": v(262.64, 477.24) * mm});
            skLineSegment(sketch, "E3239", {"start": v(262.64, 477.24) * mm, "end": v(262.47, 477.55) * mm});
            skLineSegment(sketch, "E3240", {"start": v(262.47, 477.55) * mm, "end": v(262.32, 477.87) * mm});
            skLineSegment(sketch, "E3241", {"start": v(262.32, 477.87) * mm, "end": v(262.17, 478.19) * mm});
            skLineSegment(sketch, "E3242", {"start": v(262.17, 478.19) * mm, "end": v(262.03, 478.51) * mm});
            skLineSegment(sketch, "E3243", {"start": v(262.03, 478.51) * mm, "end": v(261.9, 478.84) * mm});
            skLineSegment(sketch, "E3244", {"start": v(261.9, 478.84) * mm, "end": v(261.78, 479.16) * mm});
            skLineSegment(sketch, "E3245", {"start": v(261.78, 479.16) * mm, "end": v(261.66, 479.5) * mm});
            skLineSegment(sketch, "E3246", {"start": v(261.66, 479.5) * mm, "end": v(261.56, 479.83) * mm});
            skLineSegment(sketch, "E3247", {"start": v(261.56, 479.83) * mm, "end": v(261.46, 480.17) * mm});
            skLineSegment(sketch, "E3248", {"start": v(261.46, 480.17) * mm, "end": v(261.37, 480.5) * mm});
            skLineSegment(sketch, "E3249", {"start": v(261.37, 480.5) * mm, "end": v(261.3, 480.85) * mm});
            skLineSegment(sketch, "E3250", {"start": v(261.3, 480.85) * mm, "end": v(261.22, 481.2) * mm});
            skLineSegment(sketch, "E3251", {"start": v(261.22, 481.2) * mm, "end": v(261.16, 481.54) * mm});
            skLineSegment(sketch, "E3252", {"start": v(261.16, 481.54) * mm, "end": v(261.1, 481.9) * mm});
            skLineSegment(sketch, "E3253", {"start": v(261.1, 481.9) * mm, "end": v(261.06, 482.24) * mm});
            skLineSegment(sketch, "E3254", {"start": v(261.06, 482.24) * mm, "end": v(261.02, 482.6) * mm});
            skLineSegment(sketch, "E3255", {"start": v(261.02, 482.6) * mm, "end": v(261, 482.95) * mm});
            skLineSegment(sketch, "E3256", {"start": v(261, 482.95) * mm, "end": v(260.98, 483.3) * mm});
            skLineSegment(sketch, "E3257", {"start": v(260.98, 483.3) * mm, "end": v(260.97, 483.66) * mm});
            skLineSegment(sketch, "E3258", {"start": v(260.97, 483.66) * mm, "end": v(260.97, 484.02) * mm});
            skLineSegment(sketch, "E3259", {"start": v(260.97, 484.02) * mm, "end": v(260.98, 484.38) * mm});
            skLineSegment(sketch, "E3260", {"start": v(260.98, 484.38) * mm, "end": v(261, 484.74) * mm});
            skLineSegment(sketch, "E3261", {"start": v(261, 484.74) * mm, "end": v(261.01, 485.1) * mm});
            skLineSegment(sketch, "E3262", {"start": v(261.01, 485.1) * mm, "end": v(261.04, 485.46) * mm});
            skLineSegment(sketch, "E3263", {"start": v(261.04, 485.46) * mm, "end": v(261.08, 485.82) * mm});
            skLineSegment(sketch, "E3264", {"start": v(261.08, 485.82) * mm, "end": v(261.13, 486.17) * mm});
            skLineSegment(sketch, "E3265", {"start": v(261.13, 486.17) * mm, "end": v(261.2, 486.53) * mm});
            skLineSegment(sketch, "E3266", {"start": v(261.2, 486.53) * mm, "end": v(261.26, 486.88) * mm});
            skLineSegment(sketch, "E3267", {"start": v(261.26, 486.88) * mm, "end": v(261.34, 487.23) * mm});
            skLineSegment(sketch, "E3268", {"start": v(261.34, 487.23) * mm, "end": v(261.42, 487.58) * mm});
            skLineSegment(sketch, "E3269", {"start": v(261.42, 487.58) * mm, "end": v(261.52, 487.92) * mm});
            skLineSegment(sketch, "E3270", {"start": v(261.52, 487.92) * mm, "end": v(261.62, 488.26) * mm});
            skLineSegment(sketch, "E3271", {"start": v(261.62, 488.26) * mm, "end": v(261.73, 488.6) * mm});
            skLineSegment(sketch, "E3272", {"start": v(261.73, 488.6) * mm, "end": v(261.85, 488.94) * mm});
            skLineSegment(sketch, "E3273", {"start": v(261.85, 488.94) * mm, "end": v(261.98, 489.27) * mm});
            skLineSegment(sketch, "E3274", {"start": v(261.98, 489.27) * mm, "end": v(262.12, 489.6) * mm});
            skLineSegment(sketch, "E3275", {"start": v(262.12, 489.6) * mm, "end": v(262.26, 489.92) * mm});
            skLineSegment(sketch, "E3276", {"start": v(262.26, 489.92) * mm, "end": v(262.42, 490.25) * mm});
            skLineSegment(sketch, "E3277", {"start": v(262.42, 490.25) * mm, "end": v(262.58, 490.56) * mm});
            skLineSegment(sketch, "E3278", {"start": v(262.58, 490.56) * mm, "end": v(262.75, 490.88) * mm});
            skLineSegment(sketch, "E3279", {"start": v(262.75, 490.88) * mm, "end": v(262.93, 491.19) * mm});
            skLineSegment(sketch, "E3280", {"start": v(262.93, 491.19) * mm, "end": v(263.11, 491.5) * mm});
            skLineSegment(sketch, "E3281", {"start": v(263.11, 491.5) * mm, "end": v(263.3, 491.8) * mm});
            skLineSegment(sketch, "E3282", {"start": v(263.3, 491.8) * mm, "end": v(263.5, 492.09) * mm});
            skLineSegment(sketch, "E3283", {"start": v(263.5, 492.09) * mm, "end": v(263.72, 492.38) * mm});
            skLineSegment(sketch, "E3284", {"start": v(263.72, 492.38) * mm, "end": v(263.93, 492.67) * mm});
            skLineSegment(sketch, "E3285", {"start": v(263.93, 492.67) * mm, "end": v(264.16, 492.95) * mm});
            skLineSegment(sketch, "E3286", {"start": v(264.16, 492.95) * mm, "end": v(264.4, 493.22) * mm});
            skLineSegment(sketch, "E3287", {"start": v(264.4, 493.22) * mm, "end": v(264.63, 493.5) * mm});
            skLineSegment(sketch, "E3288", {"start": v(264.63, 493.5) * mm, "end": v(264.88, 493.75) * mm});
            skLineSegment(sketch, "E3289", {"start": v(264.88, 493.75) * mm, "end": v(265.13, 494.01) * mm});
            skLineSegment(sketch, "E3290", {"start": v(265.13, 494.01) * mm, "end": v(265.4, 494.26) * mm});
            skLineSegment(sketch, "E3291", {"start": v(265.4, 494.26) * mm, "end": v(265.75, 494.59) * mm});
            skLineSegment(sketch, "E3292", {"start": v(265.75, 494.59) * mm, "end": v(266.12, 494.9) * mm});
            skLineSegment(sketch, "E3293", {"start": v(266.12, 494.9) * mm, "end": v(266.5, 495.2) * mm});
            skLineSegment(sketch, "E3294", {"start": v(266.5, 495.2) * mm, "end": v(266.87, 495.5) * mm});
            skLineSegment(sketch, "E3295", {"start": v(266.87, 495.5) * mm, "end": v(267.26, 495.78) * mm});
            skLineSegment(sketch, "E3296", {"start": v(267.26, 495.78) * mm, "end": v(267.65, 496.06) * mm});
            skLineSegment(sketch, "E3297", {"start": v(267.65, 496.06) * mm, "end": v(268.05, 496.32) * mm});
            skLineSegment(sketch, "E3298", {"start": v(268.05, 496.32) * mm, "end": v(268.45, 496.57) * mm});
            skLineSegment(sketch, "E3299", {"start": v(268.45, 496.57) * mm, "end": v(268.86, 496.82) * mm});
            skLineSegment(sketch, "E3300", {"start": v(268.86, 496.82) * mm, "end": v(269.28, 497.05) * mm});
            skLineSegment(sketch, "E3301", {"start": v(269.28, 497.05) * mm, "end": v(269.7, 497.27) * mm});
            skLineSegment(sketch, "E3302", {"start": v(269.7, 497.27) * mm, "end": v(270.13, 497.48) * mm});
            skLineSegment(sketch, "E3303", {"start": v(270.13, 497.48) * mm, "end": v(270.56, 497.69) * mm});
            skLineSegment(sketch, "E3304", {"start": v(270.56, 497.69) * mm, "end": v(271, 497.88) * mm});
            skLineSegment(sketch, "E3305", {"start": v(271, 497.88) * mm, "end": v(271.44, 498.05) * mm});
            skLineSegment(sketch, "E3306", {"start": v(271.44, 498.05) * mm, "end": v(271.88, 498.22) * mm});
            skLineSegment(sketch, "E3307", {"start": v(271.88, 498.22) * mm, "end": v(272.33, 498.38) * mm});
            skLineSegment(sketch, "E3308", {"start": v(272.33, 498.38) * mm, "end": v(272.79, 498.53) * mm});
            skLineSegment(sketch, "E3309", {"start": v(272.79, 498.53) * mm, "end": v(273.24, 498.66) * mm});
            skLineSegment(sketch, "E3310", {"start": v(273.24, 498.66) * mm, "end": v(273.7, 498.79) * mm});
            skLineSegment(sketch, "E3311", {"start": v(273.7, 498.79) * mm, "end": v(274.16, 498.9) * mm});
            skLineSegment(sketch, "E3312", {"start": v(274.16, 498.9) * mm, "end": v(274.63, 499) * mm});
            skLineSegment(sketch, "E3313", {"start": v(274.63, 499) * mm, "end": v(275.1, 499.09) * mm});
            skLineSegment(sketch, "E3314", {"start": v(275.1, 499.09) * mm, "end": v(275.57, 499.17) * mm});
            skLineSegment(sketch, "E3315", {"start": v(275.57, 499.17) * mm, "end": v(276.04, 499.23) * mm});
            skLineSegment(sketch, "E3316", {"start": v(276.04, 499.23) * mm, "end": v(276.52, 499.29) * mm});
            skLineSegment(sketch, "E3317", {"start": v(276.52, 499.29) * mm, "end": v(277, 499.33) * mm});
            skLineSegment(sketch, "E3318", {"start": v(277, 499.33) * mm, "end": v(277.47, 499.36) * mm});
            skLineSegment(sketch, "E3319", {"start": v(277.47, 499.36) * mm, "end": v(277.95, 499.38) * mm});
            skLineSegment(sketch, "E3320", {"start": v(277.95, 499.38) * mm, "end": v(278.44, 499.39) * mm});
            skLineSegment(sketch, "E3321", {"start": v(278.44, 499.39) * mm, "end": v(278.92, 499.38) * mm});
            skLineSegment(sketch, "E3322", {"start": v(278.92, 499.38) * mm, "end": v(279.4, 499.37) * mm});
            skLineSegment(sketch, "E3323", {"start": v(279.4, 499.37) * mm, "end": v(279.85, 499.37) * mm});
            skLineSegment(sketch, "E3324", {"start": v(279.85, 499.37) * mm, "end": v(280.3, 499.37) * mm});
            skLineSegment(sketch, "E3325", {"start": v(280.3, 499.37) * mm, "end": v(280.75, 499.35) * mm});
            skLineSegment(sketch, "E3326", {"start": v(280.75, 499.35) * mm, "end": v(281.2, 499.33) * mm});
            skLineSegment(sketch, "E3327", {"start": v(281.2, 499.33) * mm, "end": v(281.64, 499.3) * mm});
            skLineSegment(sketch, "E3328", {"start": v(281.64, 499.3) * mm, "end": v(282.09, 499.24) * mm});
            skLineSegment(sketch, "E3329", {"start": v(282.09, 499.24) * mm, "end": v(282.53, 499.18) * mm});
            skLineSegment(sketch, "E3330", {"start": v(282.53, 499.18) * mm, "end": v(282.97, 499.11) * mm});
            skLineSegment(sketch, "E3331", {"start": v(282.97, 499.11) * mm, "end": v(283.4, 499.03) * mm});
            skLineSegment(sketch, "E3332", {"start": v(283.4, 499.03) * mm, "end": v(283.84, 498.94) * mm});
            skLineSegment(sketch, "E3333", {"start": v(283.84, 498.94) * mm, "end": v(284.27, 498.83) * mm});
            skLineSegment(sketch, "E3334", {"start": v(284.27, 498.83) * mm, "end": v(284.7, 498.72) * mm});
            skLineSegment(sketch, "E3335", {"start": v(284.7, 498.72) * mm, "end": v(285.13, 498.6) * mm});
            skLineSegment(sketch, "E3336", {"start": v(285.13, 498.6) * mm, "end": v(285.55, 498.46) * mm});
            skLineSegment(sketch, "E3337", {"start": v(285.55, 498.46) * mm, "end": v(285.97, 498.31) * mm});
            skLineSegment(sketch, "E3338", {"start": v(285.97, 498.31) * mm, "end": v(286.39, 498.16) * mm});
            skLineSegment(sketch, "E3339", {"start": v(286.39, 498.16) * mm, "end": v(286.8, 498) * mm});
            skLineSegment(sketch, "E3340", {"start": v(286.8, 498) * mm, "end": v(287.2, 497.81) * mm});
            skLineSegment(sketch, "E3341", {"start": v(287.2, 497.81) * mm, "end": v(287.6, 497.63) * mm});
            skLineSegment(sketch, "E3342", {"start": v(287.6, 497.63) * mm, "end": v(288, 497.43) * mm});
            skLineSegment(sketch, "E3343", {"start": v(288, 497.43) * mm, "end": v(288.4, 497.23) * mm});
            skLineSegment(sketch, "E3344", {"start": v(288.4, 497.23) * mm, "end": v(288.79, 497) * mm});
            skLineSegment(sketch, "E3345", {"start": v(288.79, 497) * mm, "end": v(289.17, 496.78) * mm});
            skLineSegment(sketch, "E3346", {"start": v(289.17, 496.78) * mm, "end": v(289.55, 496.55) * mm});
            skLineSegment(sketch, "E3347", {"start": v(289.55, 496.55) * mm, "end": v(289.92, 496.3) * mm});
            skLineSegment(sketch, "E3348", {"start": v(289.92, 496.3) * mm, "end": v(290.29, 496.05) * mm});
            skLineSegment(sketch, "E3349", {"start": v(290.29, 496.05) * mm, "end": v(290.65, 495.78) * mm});
            skLineSegment(sketch, "E3350", {"start": v(290.65, 495.78) * mm, "end": v(291, 495.51) * mm});
            skLineSegment(sketch, "E3351", {"start": v(291, 495.51) * mm, "end": v(291.35, 495.23) * mm});
            skLineSegment(sketch, "E3352", {"start": v(291.35, 495.23) * mm, "end": v(291.7, 494.94) * mm});
            skLineSegment(sketch, "E3353", {"start": v(291.7, 494.94) * mm, "end": v(292.03, 494.63) * mm});
            skLineSegment(sketch, "E3354", {"start": v(292.03, 494.63) * mm, "end": v(292.35, 494.32) * mm});
            skLineSegment(sketch, "E3355", {"start": v(292.35, 494.32) * mm, "end": v(292.6, 494.07) * mm});
            skLineSegment(sketch, "E3356", {"start": v(292.6, 494.07) * mm, "end": v(292.86, 493.8) * mm});
            skLineSegment(sketch, "E3357", {"start": v(292.86, 493.8) * mm, "end": v(293.1, 493.54) * mm});
            skLineSegment(sketch, "E3358", {"start": v(293.1, 493.54) * mm, "end": v(293.33, 493.26) * mm});
            skLineSegment(sketch, "E3359", {"start": v(293.33, 493.26) * mm, "end": v(293.56, 492.98) * mm});
            skLineSegment(sketch, "E3360", {"start": v(293.56, 492.98) * mm, "end": v(293.77, 492.7) * mm});
            skLineSegment(sketch, "E3361", {"start": v(293.77, 492.7) * mm, "end": v(293.98, 492.4) * mm});
            skLineSegment(sketch, "E3362", {"start": v(293.98, 492.4) * mm, "end": v(294.19, 492.11) * mm});
            skLineSegment(sketch, "E3363", {"start": v(294.19, 492.11) * mm, "end": v(294.38, 491.81) * mm});
            skLineSegment(sketch, "E3364", {"start": v(294.38, 491.81) * mm, "end": v(294.57, 491.5) * mm});
            skLineSegment(sketch, "E3365", {"start": v(294.57, 491.5) * mm, "end": v(294.75, 491.2) * mm});
            skLineSegment(sketch, "E3366", {"start": v(294.75, 491.2) * mm, "end": v(294.93, 490.89) * mm});
            skLineSegment(sketch, "E3367", {"start": v(294.93, 490.89) * mm, "end": v(295.1, 490.57) * mm});
            skLineSegment(sketch, "E3368", {"start": v(295.1, 490.57) * mm, "end": v(295.25, 490.25) * mm});
            skLineSegment(sketch, "E3369", {"start": v(295.25, 490.25) * mm, "end": v(295.4, 489.93) * mm});
            skLineSegment(sketch, "E3370", {"start": v(295.4, 489.93) * mm, "end": v(295.54, 489.6) * mm});
            skLineSegment(sketch, "E3371", {"start": v(295.54, 489.6) * mm, "end": v(295.67, 489.27) * mm});
            skLineSegment(sketch, "E3372", {"start": v(295.67, 489.27) * mm, "end": v(295.8, 488.93) * mm});
            skLineSegment(sketch, "E3373", {"start": v(295.8, 488.93) * mm, "end": v(295.91, 488.6) * mm});
            skLineSegment(sketch, "E3374", {"start": v(295.91, 488.6) * mm, "end": v(296.02, 488.26) * mm});
            skLineSegment(sketch, "E3375", {"start": v(296.02, 488.26) * mm, "end": v(296.12, 487.91) * mm});
            skLineSegment(sketch, "E3376", {"start": v(296.12, 487.91) * mm, "end": v(296.21, 487.57) * mm});
            skLineSegment(sketch, "E3377", {"start": v(296.21, 487.57) * mm, "end": v(296.3, 487.22) * mm});
            skLineSegment(sketch, "E3378", {"start": v(296.3, 487.22) * mm, "end": v(296.37, 486.87) * mm});
            skLineSegment(sketch, "E3379", {"start": v(296.37, 486.87) * mm, "end": v(296.43, 486.52) * mm});
            skLineSegment(sketch, "E3380", {"start": v(296.43, 486.52) * mm, "end": v(296.49, 486.16) * mm});
            skLineSegment(sketch, "E3381", {"start": v(296.49, 486.16) * mm, "end": v(296.54, 485.8) * mm});
            skLineSegment(sketch, "E3382", {"start": v(296.54, 485.8) * mm, "end": v(296.57, 485.45) * mm});
            skLineSegment(sketch, "E3383", {"start": v(296.57, 485.45) * mm, "end": v(296.6, 485.1) * mm});
            skLineSegment(sketch, "E3384", {"start": v(296.6, 485.1) * mm, "end": v(296.63, 484.73) * mm});
            skLineSegment(sketch, "E3385", {"start": v(296.63, 484.73) * mm, "end": v(296.64, 484.37) * mm});
            skLineSegment(sketch, "E3386", {"start": v(296.64, 484.37) * mm, "end": v(296.64, 484) * mm});
            skLineSegment(sketch, "E3387", {"start": v(296.15, 507.26) * mm, "end": v(261.18, 507.26) * mm});
            skLineSegment(sketch, "E3388", {"start": v(261.18, 507.26) * mm, "end": v(261.18, 522.63) * mm});
            skLineSegment(sketch, "E3389", {"start": v(261.18, 522.63) * mm, "end": v(261.19, 523.06) * mm});
            skLineSegment(sketch, "E3390", {"start": v(261.19, 523.06) * mm, "end": v(261.21, 523.49) * mm});
            skLineSegment(sketch, "E3391", {"start": v(261.21, 523.49) * mm, "end": v(261.26, 523.92) * mm});
            skLineSegment(sketch, "E3392", {"start": v(261.26, 523.92) * mm, "end": v(261.33, 524.34) * mm});
            skLineSegment(sketch, "E3393", {"start": v(261.33, 524.34) * mm, "end": v(261.42, 524.76) * mm});
            skLineSegment(sketch, "E3394", {"start": v(261.42, 524.76) * mm, "end": v(261.53, 525.17) * mm});
            skLineSegment(sketch, "E3395", {"start": v(261.53, 525.17) * mm, "end": v(261.66, 525.57) * mm});
            skLineSegment(sketch, "E3396", {"start": v(261.66, 525.57) * mm, "end": v(261.81, 525.97) * mm});
            skLineSegment(sketch, "E3397", {"start": v(261.81, 525.97) * mm, "end": v(261.99, 526.36) * mm});
            skLineSegment(sketch, "E3398", {"start": v(261.99, 526.36) * mm, "end": v(262.18, 526.74) * mm});
            skLineSegment(sketch, "E3399", {"start": v(262.18, 526.74) * mm, "end": v(262.4, 527.11) * mm});
            skLineSegment(sketch, "E3400", {"start": v(262.4, 527.11) * mm, "end": v(262.62, 527.47) * mm});
            skLineSegment(sketch, "E3401", {"start": v(262.62, 527.47) * mm, "end": v(262.87, 527.82) * mm});
            skLineSegment(sketch, "E3402", {"start": v(262.87, 527.82) * mm, "end": v(263.14, 528.16) * mm});
            skLineSegment(sketch, "E3403", {"start": v(263.14, 528.16) * mm, "end": v(263.42, 528.48) * mm});
            skLineSegment(sketch, "E3404", {"start": v(263.42, 528.48) * mm, "end": v(263.72, 528.79) * mm});
            skLineSegment(sketch, "E3405", {"start": v(263.72, 528.79) * mm, "end": v(264.03, 529.09) * mm});
            skLineSegment(sketch, "E3406", {"start": v(264.03, 529.09) * mm, "end": v(264.35, 529.37) * mm});
            skLineSegment(sketch, "E3407", {"start": v(264.35, 529.37) * mm, "end": v(264.69, 529.63) * mm});
            skLineSegment(sketch, "E3408", {"start": v(264.69, 529.63) * mm, "end": v(265.03, 529.88) * mm});
            skLineSegment(sketch, "E3409", {"start": v(265.03, 529.88) * mm, "end": v(265.39, 530.1) * mm});
            skLineSegment(sketch, "E3410", {"start": v(265.39, 530.1) * mm, "end": v(265.76, 530.31) * mm});
            skLineSegment(sketch, "E3411", {"start": v(265.76, 530.31) * mm, "end": v(266.13, 530.5) * mm});
            skLineSegment(sketch, "E3412", {"start": v(266.13, 530.5) * mm, "end": v(266.52, 530.68) * mm});
            skLineSegment(sketch, "E3413", {"start": v(266.52, 530.68) * mm, "end": v(266.91, 530.83) * mm});
            skLineSegment(sketch, "E3414", {"start": v(266.91, 530.83) * mm, "end": v(267.31, 530.97) * mm});
            skLineSegment(sketch, "E3415", {"start": v(267.31, 530.97) * mm, "end": v(267.72, 531.08) * mm});
            skLineSegment(sketch, "E3416", {"start": v(267.72, 531.08) * mm, "end": v(268.13, 531.17) * mm});
            skLineSegment(sketch, "E3417", {"start": v(268.13, 531.17) * mm, "end": v(268.55, 531.25) * mm});
            skLineSegment(sketch, "E3418", {"start": v(268.55, 531.25) * mm, "end": v(268.97, 531.3) * mm});
            skLineSegment(sketch, "E3419", {"start": v(268.97, 531.3) * mm, "end": v(269.4, 531.33) * mm});
            skLineSegment(sketch, "E3420", {"start": v(269.4, 531.33) * mm, "end": v(269.83, 531.34) * mm});
            skLineSegment(sketch, "E3421", {"start": v(269.83, 531.34) * mm, "end": v(270.27, 531.34) * mm});
            skLineSegment(sketch, "E3422", {"start": v(270.27, 531.34) * mm, "end": v(270.7, 531.32) * mm});
            skLineSegment(sketch, "E3423", {"start": v(270.7, 531.32) * mm, "end": v(271.14, 531.28) * mm});
            skLineSegment(sketch, "E3424", {"start": v(271.14, 531.28) * mm, "end": v(271.57, 531.22) * mm});
            skLineSegment(sketch, "E3425", {"start": v(271.57, 531.22) * mm, "end": v(272, 531.13) * mm});
            skLineSegment(sketch, "E3426", {"start": v(272, 531.13) * mm, "end": v(272.41, 531.02) * mm});
            skLineSegment(sketch, "E3427", {"start": v(272.41, 531.02) * mm, "end": v(272.82, 530.9) * mm});
            skLineSegment(sketch, "E3428", {"start": v(272.82, 530.9) * mm, "end": v(273.23, 530.75) * mm});
            skLineSegment(sketch, "E3429", {"start": v(273.23, 530.75) * mm, "end": v(273.63, 530.58) * mm});
            skLineSegment(sketch, "E3430", {"start": v(273.63, 530.58) * mm, "end": v(274.02, 530.4) * mm});
            skLineSegment(sketch, "E3431", {"start": v(274.02, 530.4) * mm, "end": v(274.4, 530.18) * mm});
            skLineSegment(sketch, "E3432", {"start": v(274.4, 530.18) * mm, "end": v(274.77, 529.95) * mm});
            skLineSegment(sketch, "E3433", {"start": v(274.77, 529.95) * mm, "end": v(275.12, 529.7) * mm});
            skLineSegment(sketch, "E3434", {"start": v(275.12, 529.7) * mm, "end": v(275.47, 529.44) * mm});
            skLineSegment(sketch, "E3435", {"start": v(275.47, 529.44) * mm, "end": v(275.8, 529.16) * mm});
            skLineSegment(sketch, "E3436", {"start": v(275.8, 529.16) * mm, "end": v(276.12, 528.86) * mm});
            skLineSegment(sketch, "E3437", {"start": v(276.12, 528.86) * mm, "end": v(276.42, 528.54) * mm});
            skLineSegment(sketch, "E3438", {"start": v(276.42, 528.54) * mm, "end": v(276.7, 528.21) * mm});
            skLineSegment(sketch, "E3439", {"start": v(276.7, 528.21) * mm, "end": v(276.97, 527.87) * mm});
            skLineSegment(sketch, "E3440", {"start": v(276.97, 527.87) * mm, "end": v(277.22, 527.52) * mm});
            skLineSegment(sketch, "E3441", {"start": v(277.22, 527.52) * mm, "end": v(277.45, 527.15) * mm});
            skLineSegment(sketch, "E3442", {"start": v(277.45, 527.15) * mm, "end": v(277.66, 526.78) * mm});
            skLineSegment(sketch, "E3443", {"start": v(277.66, 526.78) * mm, "end": v(277.85, 526.4) * mm});
            skLineSegment(sketch, "E3444", {"start": v(277.85, 526.4) * mm, "end": v(278.02, 526) * mm});
            skLineSegment(sketch, "E3445", {"start": v(278.02, 526) * mm, "end": v(278.18, 525.6) * mm});
            skLineSegment(sketch, "E3446", {"start": v(278.18, 525.6) * mm, "end": v(278.3, 525.19) * mm});
            skLineSegment(sketch, "E3447", {"start": v(278.3, 525.19) * mm, "end": v(278.42, 524.77) * mm});
            skLineSegment(sketch, "E3448", {"start": v(278.42, 524.77) * mm, "end": v(278.5, 524.35) * mm});
            skLineSegment(sketch, "E3449", {"start": v(278.5, 524.35) * mm, "end": v(278.58, 523.92) * mm});
            skLineSegment(sketch, "E3450", {"start": v(278.58, 523.92) * mm, "end": v(278.63, 523.5) * mm});
            skLineSegment(sketch, "E3451", {"start": v(278.63, 523.5) * mm, "end": v(278.65, 523.06) * mm});
            skLineSegment(sketch, "E3452", {"start": v(278.65, 523.06) * mm, "end": v(278.66, 522.63) * mm});
            skLineSegment(sketch, "E3453", {"start": v(278.66, 522.63) * mm, "end": v(278.66, 507.26) * mm});
            skLineSegment(sketch, "E3454", {"start": v(278.66, 522.63) * mm, "end": v(278.66, 522.98) * mm});
            skLineSegment(sketch, "E3455", {"start": v(278.66, 522.98) * mm, "end": v(278.68, 523.34) * mm});
            skLineSegment(sketch, "E3456", {"start": v(278.68, 523.34) * mm, "end": v(278.72, 523.7) * mm});
            skLineSegment(sketch, "E3457", {"start": v(278.72, 523.7) * mm, "end": v(278.77, 524.05) * mm});
            skLineSegment(sketch, "E3458", {"start": v(278.77, 524.05) * mm, "end": v(278.85, 524.4) * mm});
            skLineSegment(sketch, "E3459", {"start": v(278.85, 524.4) * mm, "end": v(278.94, 524.73) * mm});
            skLineSegment(sketch, "E3460", {"start": v(278.94, 524.73) * mm, "end": v(279.05, 525.07) * mm});
            skLineSegment(sketch, "E3461", {"start": v(279.05, 525.07) * mm, "end": v(279.17, 525.4) * mm});
            skLineSegment(sketch, "E3462", {"start": v(279.17, 525.4) * mm, "end": v(279.31, 525.72) * mm});
            skLineSegment(sketch, "E3463", {"start": v(279.31, 525.72) * mm, "end": v(279.47, 526.04) * mm});
            skLineSegment(sketch, "E3464", {"start": v(279.47, 526.04) * mm, "end": v(279.65, 526.35) * mm});
            skLineSegment(sketch, "E3465", {"start": v(279.65, 526.35) * mm, "end": v(279.83, 526.65) * mm});
            skLineSegment(sketch, "E3466", {"start": v(279.83, 526.65) * mm, "end": v(280.04, 526.94) * mm});
            skLineSegment(sketch, "E3467", {"start": v(280.04, 526.94) * mm, "end": v(280.26, 527.22) * mm});
            skLineSegment(sketch, "E3468", {"start": v(280.26, 527.22) * mm, "end": v(280.5, 527.49) * mm});
            skLineSegment(sketch, "E3469", {"start": v(280.5, 527.49) * mm, "end": v(280.74, 527.75) * mm});
            skLineSegment(sketch, "E3470", {"start": v(280.74, 527.75) * mm, "end": v(281.18, 528.04) * mm});
            skLineSegment(sketch, "E3471", {"start": v(281.18, 528.04) * mm, "end": v(281.63, 528.32) * mm});
            skLineSegment(sketch, "E3472", {"start": v(281.63, 528.32) * mm, "end": v(282.1, 528.58) * mm});
            skLineSegment(sketch, "E3473", {"start": v(282.1, 528.58) * mm, "end": v(282.56, 528.81) * mm});
            skLineSegment(sketch, "E3474", {"start": v(282.56, 528.81) * mm, "end": v(283.04, 529.03) * mm});
            skLineSegment(sketch, "E3475", {"start": v(283.04, 529.03) * mm, "end": v(283.53, 529.22) * mm});
            skLineSegment(sketch, "E3476", {"start": v(283.53, 529.22) * mm, "end": v(284.02, 529.39) * mm});
            skLineSegment(sketch, "E3477", {"start": v(284.02, 529.39) * mm, "end": v(284.53, 529.54) * mm});
            skLineSegment(sketch, "E3478", {"start": v(284.53, 529.54) * mm, "end": v(285.03, 529.66) * mm});
            skLineSegment(sketch, "E3479", {"start": v(285.03, 529.66) * mm, "end": v(285.55, 529.77) * mm});
            skLineSegment(sketch, "E3480", {"start": v(285.55, 529.77) * mm, "end": v(286.07, 529.85) * mm});
            skLineSegment(sketch, "E3481", {"start": v(286.07, 529.85) * mm, "end": v(286.59, 529.9) * mm});
            skLineSegment(sketch, "E3482", {"start": v(286.59, 529.9) * mm, "end": v(287.11, 529.94) * mm});
            skLineSegment(sketch, "E3483", {"start": v(287.11, 529.94) * mm, "end": v(287.64, 529.95) * mm});
            skLineSegment(sketch, "E3484", {"start": v(287.64, 529.95) * mm, "end": v(288.17, 529.94) * mm});
            skLineSegment(sketch, "E3485", {"start": v(288.17, 529.94) * mm, "end": v(288.7, 529.9) * mm});
            skLineSegment(sketch, "E3486", {"start": v(288.7, 529.9) * mm, "end": v(289.16, 529.9) * mm});
            skLineSegment(sketch, "E3487", {"start": v(289.16, 529.9) * mm, "end": v(289.64, 529.9) * mm});
            skLineSegment(sketch, "E3488", {"start": v(289.64, 529.9) * mm, "end": v(290.1, 529.9) * mm});
            skLineSegment(sketch, "E3489", {"start": v(290.1, 529.9) * mm, "end": v(290.58, 529.92) * mm});
            skLineSegment(sketch, "E3490", {"start": v(290.58, 529.92) * mm, "end": v(291.05, 529.95) * mm});
            skLineSegment(sketch, "E3491", {"start": v(291.05, 529.95) * mm, "end": v(291.52, 529.98) * mm});
            skLineSegment(sketch, "E3492", {"start": v(291.52, 529.98) * mm, "end": v(291.99, 530.03) * mm});
            skLineSegment(sketch, "E3493", {"start": v(291.99, 530.03) * mm, "end": v(292.45, 530.08) * mm});
            skLineSegment(sketch, "E3494", {"start": v(292.45, 530.08) * mm, "end": v(292.92, 530.14) * mm});
            skLineSegment(sketch, "E3495", {"start": v(292.92, 530.14) * mm, "end": v(293.39, 530.21) * mm});
            skLineSegment(sketch, "E3496", {"start": v(293.39, 530.21) * mm, "end": v(293.85, 530.29) * mm});
            skLineSegment(sketch, "E3497", {"start": v(293.85, 530.29) * mm, "end": v(294.32, 530.37) * mm});
            skLineSegment(sketch, "E3498", {"start": v(294.32, 530.37) * mm, "end": v(294.78, 530.47) * mm});
            skLineSegment(sketch, "E3499", {"start": v(294.78, 530.47) * mm, "end": v(295.24, 530.57) * mm});
            skLineSegment(sketch, "E3500", {"start": v(295.24, 530.57) * mm, "end": v(295.7, 530.68) * mm});
            skLineSegment(sketch, "E3501", {"start": v(295.7, 530.68) * mm, "end": v(296.15, 530.8) * mm});
            skLineSegment(sketch, "E3502", {"start": v(283.09, 539.04) * mm, "end": v(283.09, 563.17) * mm});
            skLineSegment(sketch, "E3503", {"start": v(296.16, 570.87) * mm, "end": v(269.98, 570.87) * mm});
            skLineSegment(sketch, "E3504", {"start": v(261.7, 570.87) * mm, "end": v(261.26, 570.87) * mm});
            skLineSegment(sketch, "E3505", {"start": v(296.16, 578.57) * mm, "end": v(269.93, 578.57) * mm});
            skLineSegment(sketch, "E3506", {"start": v(280.18, 578.57) * mm, "end": v(279.6, 578.59) * mm});
            skLineSegment(sketch, "E3507", {"start": v(279.6, 578.59) * mm, "end": v(279.03, 578.63) * mm});
            skLineSegment(sketch, "E3508", {"start": v(279.03, 578.63) * mm, "end": v(278.47, 578.7) * mm});
            skLineSegment(sketch, "E3509", {"start": v(278.47, 578.7) * mm, "end": v(277.91, 578.8) * mm});
            skLineSegment(sketch, "E3510", {"start": v(277.91, 578.8) * mm, "end": v(277.36, 578.94) * mm});
            skLineSegment(sketch, "E3511", {"start": v(277.36, 578.94) * mm, "end": v(276.81, 579.1) * mm});
            skLineSegment(sketch, "E3512", {"start": v(276.81, 579.1) * mm, "end": v(276.28, 579.28) * mm});
            skLineSegment(sketch, "E3513", {"start": v(276.28, 579.28) * mm, "end": v(275.75, 579.49) * mm});
            skLineSegment(sketch, "E3514", {"start": v(275.75, 579.49) * mm, "end": v(275.24, 579.72) * mm});
            skLineSegment(sketch, "E3515", {"start": v(275.24, 579.72) * mm, "end": v(274.74, 579.98) * mm});
            skLineSegment(sketch, "E3516", {"start": v(274.74, 579.98) * mm, "end": v(274.25, 580.27) * mm});
            skLineSegment(sketch, "E3517", {"start": v(274.25, 580.27) * mm, "end": v(273.77, 580.58) * mm});
            skLineSegment(sketch, "E3518", {"start": v(273.77, 580.58) * mm, "end": v(273.31, 580.9) * mm});
            skLineSegment(sketch, "E3519", {"start": v(273.31, 580.9) * mm, "end": v(272.87, 581.27) * mm});
            skLineSegment(sketch, "E3520", {"start": v(272.87, 581.27) * mm, "end": v(272.44, 581.65) * mm});
            skLineSegment(sketch, "E3521", {"start": v(272.44, 581.65) * mm, "end": v(272.04, 582.05) * mm});
            skLineSegment(sketch, "E3522", {"start": v(272.04, 582.05) * mm, "end": v(271.7, 582.4) * mm});
            skLineSegment(sketch, "E3523", {"start": v(271.7, 582.4) * mm, "end": v(271.4, 582.77) * mm});
            skLineSegment(sketch, "E3524", {"start": v(271.4, 582.77) * mm, "end": v(271.1, 583.16) * mm});
            skLineSegment(sketch, "E3525", {"start": v(271.1, 583.16) * mm, "end": v(270.83, 583.55) * mm});
            skLineSegment(sketch, "E3526", {"start": v(270.83, 583.55) * mm, "end": v(270.58, 583.96) * mm});
            skLineSegment(sketch, "E3527", {"start": v(270.58, 583.96) * mm, "end": v(270.35, 584.38) * mm});
            skLineSegment(sketch, "E3528", {"start": v(270.35, 584.38) * mm, "end": v(270.15, 584.8) * mm});
            skLineSegment(sketch, "E3529", {"start": v(270.15, 584.8) * mm, "end": v(269.96, 585.25) * mm});
            skLineSegment(sketch, "E3530", {"start": v(269.96, 585.25) * mm, "end": v(269.8, 585.7) * mm});
            skLineSegment(sketch, "E3531", {"start": v(269.8, 585.7) * mm, "end": v(269.65, 586.15) * mm});
            skLineSegment(sketch, "E3532", {"start": v(269.65, 586.15) * mm, "end": v(269.53, 586.62) * mm});
            skLineSegment(sketch, "E3533", {"start": v(269.53, 586.62) * mm, "end": v(269.44, 587.08) * mm});
            skLineSegment(sketch, "E3534", {"start": v(269.44, 587.08) * mm, "end": v(269.37, 587.56) * mm});
            skLineSegment(sketch, "E3535", {"start": v(269.37, 587.56) * mm, "end": v(269.32, 588.04) * mm});
            skLineSegment(sketch, "E3536", {"start": v(269.32, 588.04) * mm, "end": v(269.3, 588.52) * mm});
            skLineSegment(sketch, "E3537", {"start": v(269.3, 588.52) * mm, "end": v(269.3, 589) * mm});
            skLineSegment(sketch, "E3538", {"start": v(269.3, 589) * mm, "end": v(269.26, 589.46) * mm});
            skLineSegment(sketch, "E3539", {"start": v(269.26, 589.46) * mm, "end": v(269.26, 589.92) * mm});
            skLineSegment(sketch, "E3540", {"start": v(269.26, 589.92) * mm, "end": v(269.27, 590.38) * mm});
            skLineSegment(sketch, "E3541", {"start": v(269.27, 590.38) * mm, "end": v(269.32, 590.84) * mm});
            skLineSegment(sketch, "E3542", {"start": v(269.32, 590.84) * mm, "end": v(269.38, 591.3) * mm});
            skLineSegment(sketch, "E3543", {"start": v(269.38, 591.3) * mm, "end": v(269.47, 591.74) * mm});
            skLineSegment(sketch, "E3544", {"start": v(269.47, 591.74) * mm, "end": v(269.58, 592.18) * mm});
            skLineSegment(sketch, "E3545", {"start": v(269.58, 592.18) * mm, "end": v(269.72, 592.62) * mm});
            skLineSegment(sketch, "E3546", {"start": v(269.72, 592.62) * mm, "end": v(269.87, 593.05) * mm});
            skLineSegment(sketch, "E3547", {"start": v(269.87, 593.05) * mm, "end": v(270.05, 593.47) * mm});
            skLineSegment(sketch, "E3548", {"start": v(270.05, 593.47) * mm, "end": v(270.25, 593.88) * mm});
            skLineSegment(sketch, "E3549", {"start": v(270.25, 593.88) * mm, "end": v(270.47, 594.28) * mm});
            skLineSegment(sketch, "E3550", {"start": v(270.47, 594.28) * mm, "end": v(270.71, 594.67) * mm});
            skLineSegment(sketch, "E3551", {"start": v(270.71, 594.67) * mm, "end": v(270.98, 595.04) * mm});
            skLineSegment(sketch, "E3552", {"start": v(270.98, 595.04) * mm, "end": v(271.26, 595.4) * mm});
            skLineSegment(sketch, "E3553", {"start": v(271.26, 595.4) * mm, "end": v(271.56, 595.76) * mm});
            skLineSegment(sketch, "E3554", {"start": v(271.56, 595.76) * mm, "end": v(271.82, 595.97) * mm});
            skLineSegment(sketch, "E3555", {"start": v(271.82, 595.97) * mm, "end": v(272.08, 596.17) * mm});
            skLineSegment(sketch, "E3556", {"start": v(272.08, 596.17) * mm, "end": v(272.35, 596.36) * mm});
            skLineSegment(sketch, "E3557", {"start": v(272.35, 596.36) * mm, "end": v(272.63, 596.54) * mm});
            skLineSegment(sketch, "E3558", {"start": v(272.63, 596.54) * mm, "end": v(272.92, 596.7) * mm});
            skLineSegment(sketch, "E3559", {"start": v(272.92, 596.7) * mm, "end": v(273.22, 596.84) * mm});
            skLineSegment(sketch, "E3560", {"start": v(273.22, 596.84) * mm, "end": v(273.52, 596.98) * mm});
            skLineSegment(sketch, "E3561", {"start": v(273.52, 596.98) * mm, "end": v(273.82, 597.1) * mm});
            skLineSegment(sketch, "E3562", {"start": v(273.82, 597.1) * mm, "end": v(274.13, 597.2) * mm});
            skLineSegment(sketch, "E3563", {"start": v(274.13, 597.2) * mm, "end": v(274.45, 597.3) * mm});
            skLineSegment(sketch, "E3564", {"start": v(274.45, 597.3) * mm, "end": v(274.77, 597.37) * mm});
            skLineSegment(sketch, "E3565", {"start": v(274.77, 597.37) * mm, "end": v(275.1, 597.43) * mm});
            skLineSegment(sketch, "E3566", {"start": v(275.1, 597.43) * mm, "end": v(275.42, 597.48) * mm});
            skLineSegment(sketch, "E3567", {"start": v(275.42, 597.48) * mm, "end": v(275.75, 597.5) * mm});
            skLineSegment(sketch, "E3568", {"start": v(275.75, 597.5) * mm, "end": v(276.08, 597.53) * mm});
            skLineSegment(sketch, "E3569", {"start": v(276.08, 597.53) * mm, "end": v(276.41, 597.53) * mm});
            skLineSegment(sketch, "E3570", {"start": v(276.41, 597.53) * mm, "end": v(296.16, 597.53) * mm});
            skArc(sketch, "E3571", {"start": v(-573.8, -810.76) * mm, "mid": v(-575.93, -811.63) * mm, "end": v(-576.8, -813.76) * mm});
            skArc(sketch, "E3572", {"start": v(-576.8, -813.76) * mm, "mid": v(-575.93, -815.88) * mm, "end": v(-573.8, -816.76) * mm});
            skArc(sketch, "E3573", {"start": v(-573.8, -816.76) * mm, "mid": v(-571.68, -815.88) * mm, "end": v(-570.8, -813.76) * mm});
            skArc(sketch, "E3574", {"start": v(-570.8, -813.76) * mm, "mid": v(-571.68, -811.63) * mm, "end": v(-573.8, -810.76) * mm});
            skArc(sketch, "E3575", {"start": v(10.73, -1172.55) * mm, "mid": v(8.6, -1173.43) * mm, "end": v(7.73, -1175.55) * mm});
            skArc(sketch, "E3576", {"start": v(7.73, -1175.55) * mm, "mid": v(8.6, -1177.67) * mm, "end": v(10.73, -1178.55) * mm});
            skArc(sketch, "E3577", {"start": v(10.73, -1178.55) * mm, "mid": v(12.85, -1177.67) * mm, "end": v(13.73, -1175.55) * mm});
            skArc(sketch, "E3578", {"start": v(13.73, -1175.55) * mm, "mid": v(12.85, -1173.43) * mm, "end": v(10.73, -1172.55) * mm});
            skArc(sketch, "E3579", {"start": v(259.15, -952.35) * mm, "mid": v(257.03, -953.23) * mm, "end": v(256.15, -955.35) * mm});
            skArc(sketch, "E3580", {"start": v(256.15, -955.35) * mm, "mid": v(257.03, -957.47) * mm, "end": v(259.15, -958.35) * mm});
            skArc(sketch, "E3581", {"start": v(259.15, -958.35) * mm, "mid": v(261.28, -957.47) * mm, "end": v(262.15, -955.35) * mm});
            skArc(sketch, "E3582", {"start": v(262.15, -955.35) * mm, "mid": v(261.28, -953.23) * mm, "end": v(259.15, -952.35) * mm});
            skArc(sketch, "E3583", {"start": v(505.27, -1161.94) * mm, "mid": v(503.15, -1162.82) * mm, "end": v(502.27, -1164.94) * mm});
            skArc(sketch, "E3584", {"start": v(502.27, -1164.94) * mm, "mid": v(503.15, -1167.06) * mm, "end": v(505.27, -1167.94) * mm});
            skArc(sketch, "E3585", {"start": v(505.27, -1167.94) * mm, "mid": v(507.4, -1167.06) * mm, "end": v(508.27, -1164.94) * mm});
            skArc(sketch, "E3586", {"start": v(508.27, -1164.94) * mm, "mid": v(507.4, -1162.82) * mm, "end": v(505.27, -1161.94) * mm});
            skArc(sketch, "E3587", {"start": v(557.19, -613.94) * mm, "mid": v(555.07, -614.82) * mm, "end": v(554.19, -616.94) * mm});
            skArc(sketch, "E3588", {"start": v(554.19, -616.94) * mm, "mid": v(555.07, -619.06) * mm, "end": v(557.19, -619.94) * mm});
            skArc(sketch, "E3589", {"start": v(557.19, -619.94) * mm, "mid": v(559.31, -619.06) * mm, "end": v(560.19, -616.94) * mm});
            skArc(sketch, "E3590", {"start": v(560.19, -616.94) * mm, "mid": v(559.31, -614.82) * mm, "end": v(557.19, -613.94) * mm});
            skArc(sketch, "E3591", {"start": v(78.4, -463.96) * mm, "mid": v(76.29, -464.84) * mm, "end": v(75.4, -466.96) * mm});
            skArc(sketch, "E3592", {"start": v(75.4, -466.96) * mm, "mid": v(76.29, -469.08) * mm, "end": v(78.4, -469.96) * mm});
            skArc(sketch, "E3593", {"start": v(78.4, -469.96) * mm, "mid": v(80.53, -469.08) * mm, "end": v(81.4, -466.96) * mm});
            skArc(sketch, "E3594", {"start": v(81.4, -466.96) * mm, "mid": v(80.53, -464.84) * mm, "end": v(78.4, -463.96) * mm});
            skArc(sketch, "E3595", {"start": v(-269.62, -621.63) * mm, "mid": v(-271.74, -622.5) * mm, "end": v(-272.62, -624.63) * mm});
            skArc(sketch, "E3596", {"start": v(-272.62, -624.63) * mm, "mid": v(-271.74, -626.75) * mm, "end": v(-269.62, -627.63) * mm});
            skArc(sketch, "E3597", {"start": v(-269.62, -627.63) * mm, "mid": v(-267.5, -626.75) * mm, "end": v(-266.62, -624.63) * mm});
            skArc(sketch, "E3598", {"start": v(-266.62, -624.63) * mm, "mid": v(-267.5, -622.5) * mm, "end": v(-269.62, -621.63) * mm});
            skArc(sketch, "E3599", {"start": v(-579.72, -243.34) * mm, "mid": v(-581.84, -244.22) * mm, "end": v(-582.72, -246.34) * mm});
            skArc(sketch, "E3600", {"start": v(-582.72, -246.34) * mm, "mid": v(-581.84, -248.46) * mm, "end": v(-579.72, -249.34) * mm});
            skArc(sketch, "E3601", {"start": v(-579.72, -249.34) * mm, "mid": v(-577.6, -248.46) * mm, "end": v(-576.72, -246.34) * mm});
            skArc(sketch, "E3602", {"start": v(-576.72, -246.34) * mm, "mid": v(-577.6, -244.22) * mm, "end": v(-579.72, -243.34) * mm});
            skArc(sketch, "E3603", {"start": v(36.34, 178.6) * mm, "mid": v(34.21, 177.72) * mm, "end": v(33.34, 175.6) * mm});
            skArc(sketch, "E3604", {"start": v(33.34, 175.6) * mm, "mid": v(34.21, 173.48) * mm, "end": v(36.34, 172.6) * mm});
            skArc(sketch, "E3605", {"start": v(36.34, 172.6) * mm, "mid": v(38.46, 173.48) * mm, "end": v(39.34, 175.6) * mm});
            skArc(sketch, "E3606", {"start": v(39.34, 175.6) * mm, "mid": v(38.46, 177.72) * mm, "end": v(36.34, 178.6) * mm});
            skArc(sketch, "E3607", {"start": v(522.57, -8.94) * mm, "mid": v(520.45, -9.82) * mm, "end": v(519.57, -11.94) * mm});
            skArc(sketch, "E3608", {"start": v(519.57, -11.94) * mm, "mid": v(520.45, -14.06) * mm, "end": v(522.57, -14.94) * mm});
            skArc(sketch, "E3609", {"start": v(522.57, -14.94) * mm, "mid": v(524.7, -14.06) * mm, "end": v(525.57, -11.94) * mm});
            skArc(sketch, "E3610", {"start": v(525.57, -11.94) * mm, "mid": v(524.7, -9.82) * mm, "end": v(522.57, -8.94) * mm});
            skArc(sketch, "E3611", {"start": v(522.72, 590.22) * mm, "mid": v(520.6, 589.34) * mm, "end": v(519.72, 587.22) * mm});
            skArc(sketch, "E3612", {"start": v(519.72, 587.22) * mm, "mid": v(520.6, 585.1) * mm, "end": v(522.72, 584.22) * mm});
            skArc(sketch, "E3613", {"start": v(522.72, 584.22) * mm, "mid": v(524.84, 585.1) * mm, "end": v(525.72, 587.22) * mm});
            skArc(sketch, "E3614", {"start": v(525.72, 587.22) * mm, "mid": v(524.84, 589.34) * mm, "end": v(522.72, 590.22) * mm});
            skArc(sketch, "E3615", {"start": v(571.3, 1183.8) * mm, "mid": v(569.17, 1182.91) * mm, "end": v(568.3, 1180.8) * mm});
            skArc(sketch, "E3616", {"start": v(568.3, 1180.8) * mm, "mid": v(569.17, 1178.67) * mm, "end": v(571.3, 1177.8) * mm});
            skArc(sketch, "E3617", {"start": v(571.3, 1177.8) * mm, "mid": v(573.42, 1178.67) * mm, "end": v(574.3, 1180.8) * mm});
            skArc(sketch, "E3618", {"start": v(574.3, 1180.8) * mm, "mid": v(573.42, 1182.91) * mm, "end": v(571.3, 1183.8) * mm});
            skArc(sketch, "E3619", {"start": v(198.32, 1135.66) * mm, "mid": v(196.2, 1134.78) * mm, "end": v(195.32, 1132.66) * mm});
            skArc(sketch, "E3620", {"start": v(195.32, 1132.66) * mm, "mid": v(196.2, 1130.53) * mm, "end": v(198.32, 1129.66) * mm});
            skArc(sketch, "E3621", {"start": v(198.32, 1129.66) * mm, "mid": v(200.44, 1130.53) * mm, "end": v(201.32, 1132.66) * mm});
            skArc(sketch, "E3622", {"start": v(201.32, 1132.66) * mm, "mid": v(200.44, 1134.78) * mm, "end": v(198.32, 1135.66) * mm});
            skArc(sketch, "E3623", {"start": v(-274.15, 895.04) * mm, "mid": v(-276.27, 894.16) * mm, "end": v(-277.15, 892.04) * mm});
            skArc(sketch, "E3624", {"start": v(-277.15, 892.04) * mm, "mid": v(-276.27, 889.91) * mm, "end": v(-274.15, 889.04) * mm});
            skArc(sketch, "E3625", {"start": v(-274.15, 889.04) * mm, "mid": v(-272.02, 889.91) * mm, "end": v(-271.15, 892.04) * mm});
            skArc(sketch, "E3626", {"start": v(-271.15, 892.04) * mm, "mid": v(-272.02, 894.16) * mm, "end": v(-274.15, 895.04) * mm});
            skArc(sketch, "E3627", {"start": v(-572.38, 1049.1) * mm, "mid": v(-574.5, 1048.22) * mm, "end": v(-575.38, 1046.1) * mm});
            skArc(sketch, "E3628", {"start": v(-575.38, 1046.1) * mm, "mid": v(-574.5, 1043.98) * mm, "end": v(-572.38, 1043.1) * mm});
            skArc(sketch, "E3629", {"start": v(-572.38, 1043.1) * mm, "mid": v(-570.26, 1043.98) * mm, "end": v(-569.38, 1046.1) * mm});
            skArc(sketch, "E3630", {"start": v(-569.38, 1046.1) * mm, "mid": v(-570.26, 1048.22) * mm, "end": v(-572.38, 1049.1) * mm});
            skArc(sketch, "E3631", {"start": v(-578.02, 593.93) * mm, "mid": v(-580.14, 593.06) * mm, "end": v(-581.02, 590.93) * mm});
            skArc(sketch, "E3632", {"start": v(-581.02, 590.93) * mm, "mid": v(-580.14, 588.81) * mm, "end": v(-578.02, 587.93) * mm});
            skArc(sketch, "E3633", {"start": v(-578.02, 587.93) * mm, "mid": v(-575.9, 588.81) * mm, "end": v(-575.02, 590.93) * mm});
            skArc(sketch, "E3634", {"start": v(-575.02, 590.93) * mm, "mid": v(-575.9, 593.06) * mm, "end": v(-578.02, 593.93) * mm});
            skArc(sketch, "E3635", {"start": v(198.64, 592.74) * mm, "mid": v(196.51, 591.86) * mm, "end": v(195.64, 589.74) * mm});
            skArc(sketch, "E3636", {"start": v(195.64, 589.74) * mm, "mid": v(196.51, 587.62) * mm, "end": v(198.64, 586.74) * mm});
            skArc(sketch, "E3637", {"start": v(198.64, 586.74) * mm, "mid": v(200.76, 587.62) * mm, "end": v(201.64, 589.74) * mm});
            skArc(sketch, "E3638", {"start": v(201.64, 589.74) * mm, "mid": v(200.76, 591.86) * mm, "end": v(198.64, 592.74) * mm});
            skArc(sketch, "E3639", {"start": v(-274.48, 283.47) * mm, "mid": v(-276.6, 282.6) * mm, "end": v(-277.48, 280.47) * mm});
            skArc(sketch, "E3640", {"start": v(-277.48, 280.47) * mm, "mid": v(-276.6, 278.35) * mm, "end": v(-274.48, 277.47) * mm});
            skArc(sketch, "E3641", {"start": v(-274.48, 277.47) * mm, "mid": v(-272.36, 278.35) * mm, "end": v(-271.48, 280.47) * mm});
            skArc(sketch, "E3642", {"start": v(-271.48, 280.47) * mm, "mid": v(-272.36, 282.6) * mm, "end": v(-274.48, 283.47) * mm});
            skSolve(sketch);
        }
        {
            var Q0;
            Q0=makeQuery(id+"F0.imprint","IMPRINT",FACE,{"disambiguationData":[TD([[makeQuery(id+"F0.imprint","IMPRINT",EDGE,{"derivedFrom":sQuery(id+"F0.wireOp",EDGE,"E0")}),-1.0]])]});
            extrude(context, id + "F1", {"entities" : qUnion([Q0]), "depth" : 18 * mm});
        }
        {
            var Q0;
            Q0=makeQuery(id+"F0.imprint","IMPRINT",FACE,{"disambiguationData":[TD([[makeQuery(id+"F0.imprint","IMPRINT",EDGE,{"derivedFrom":sQuery(id+"F0.wireOp",EDGE,"E418")}),1.0]])]});
            var Q1;
            Q1=makeQuery(id+"F0.imprint","IMPRINT",FACE,{"disambiguationData":[TD([[makeQuery(id+"F0.imprint","IMPRINT",EDGE,{"derivedFrom":sQuery(id+"F0.wireOp",EDGE,"E1942")}),-1.0]])]});
            var Q2;
            Q2=makeQuery(id+"F0.imprint","IMPRINT",FACE,{"disambiguationData":[TD([[makeQuery(id+"F0.imprint","IMPRINT",EDGE,{"derivedFrom":sQuery(id+"F0.wireOp",EDGE,"E2198")}),-1.0]])]});
            var Q3;
            {var subQ0=sQuery(id+"F0.wireOp",EDGE,"E2455");Q3=makeQuery(id+"F0.imprint","IMPRINT",FACE,{"disambiguationData":[TD([[makeQuery(id+"F0.imprint","IMPRINT",EDGE,{"derivedFrom":subQ0}),-1.0]])]});}
            var Q4;
            Q4=makeQuery(id+"F0.imprint","IMPRINT",FACE,{"disambiguationData":[TD([[makeQuery(id+"F0.imprint","IMPRINT",EDGE,{"derivedFrom":sQuery(id+"F0.wireOp",EDGE,"E2570")}),-1.0]])]});
            extrude(context, id + "F2", {"entities" : qUnion([Q0, Q1, Q2, Q3, Q4]), "depth" : 18 * mm});
        }
        {
            var Q0;
            Q0=makeQuery(id+"F0.imprint","IMPRINT",FACE,{"disambiguationData":[TD([[makeQuery(id+"F0.imprint","IMPRINT",EDGE,{"derivedFrom":sQuery(id+"F0.wireOp",EDGE,"E530")}),1.0]])]});
            var Q1;
            {var subQ0=sQuery(id+"F0.wireOp",EDGE,"E3388");Q1=makeQuery(id+"F0.imprint","IMPRINT",FACE,{"disambiguationData":[TD([[makeQuery(id+"F0.imprint","IMPRINT",EDGE,{"derivedFrom":subQ0}),-1.0]])]});}
            var Q2;
            Q2=makeQuery(id+"F0.imprint","IMPRINT",FACE,{"disambiguationData":[TD([[makeQuery(id+"F0.imprint","IMPRINT",EDGE,{"derivedFrom":sQuery(id+"F0.wireOp",EDGE,"E3131")}),-1.0]])]});
            var Q3;
            Q3=makeQuery(id+"F0.imprint","IMPRINT",FACE,{"disambiguationData":[TD([[makeQuery(id+"F0.imprint","IMPRINT",EDGE,{"derivedFrom":sQuery(id+"F0.wireOp",EDGE,"E2875")}),-1.0]])]});
            extrude(context, id + "F3", {"entities" : qUnion([Q0, Q1, Q2, Q3]), "depth" : 18 * mm});
        }
        {
            var Q0;
            Q0=makeQuery(id+"F0.imprint","IMPRINT",FACE,{"disambiguationData":[TD([[makeQuery(id+"F0.imprint","IMPRINT",EDGE,{"derivedFrom":sQuery(id+"F0.wireOp",EDGE,"E68")}),1.0]])]});
            var Q1;
            {var subQ0=sQuery(id+"F0.wireOp",EDGE,"E822");Q1=makeQuery(id+"F0.imprint","IMPRINT",FACE,{"disambiguationData":[TD([[makeQuery(id+"F0.imprint","IMPRINT",EDGE,{"derivedFrom":subQ0}),-1.0]])]});}
            extrude(context, id + "F4", {"entities" : qUnion([Q0, Q1]), "depth" : 18 * mm});
        }
    });
